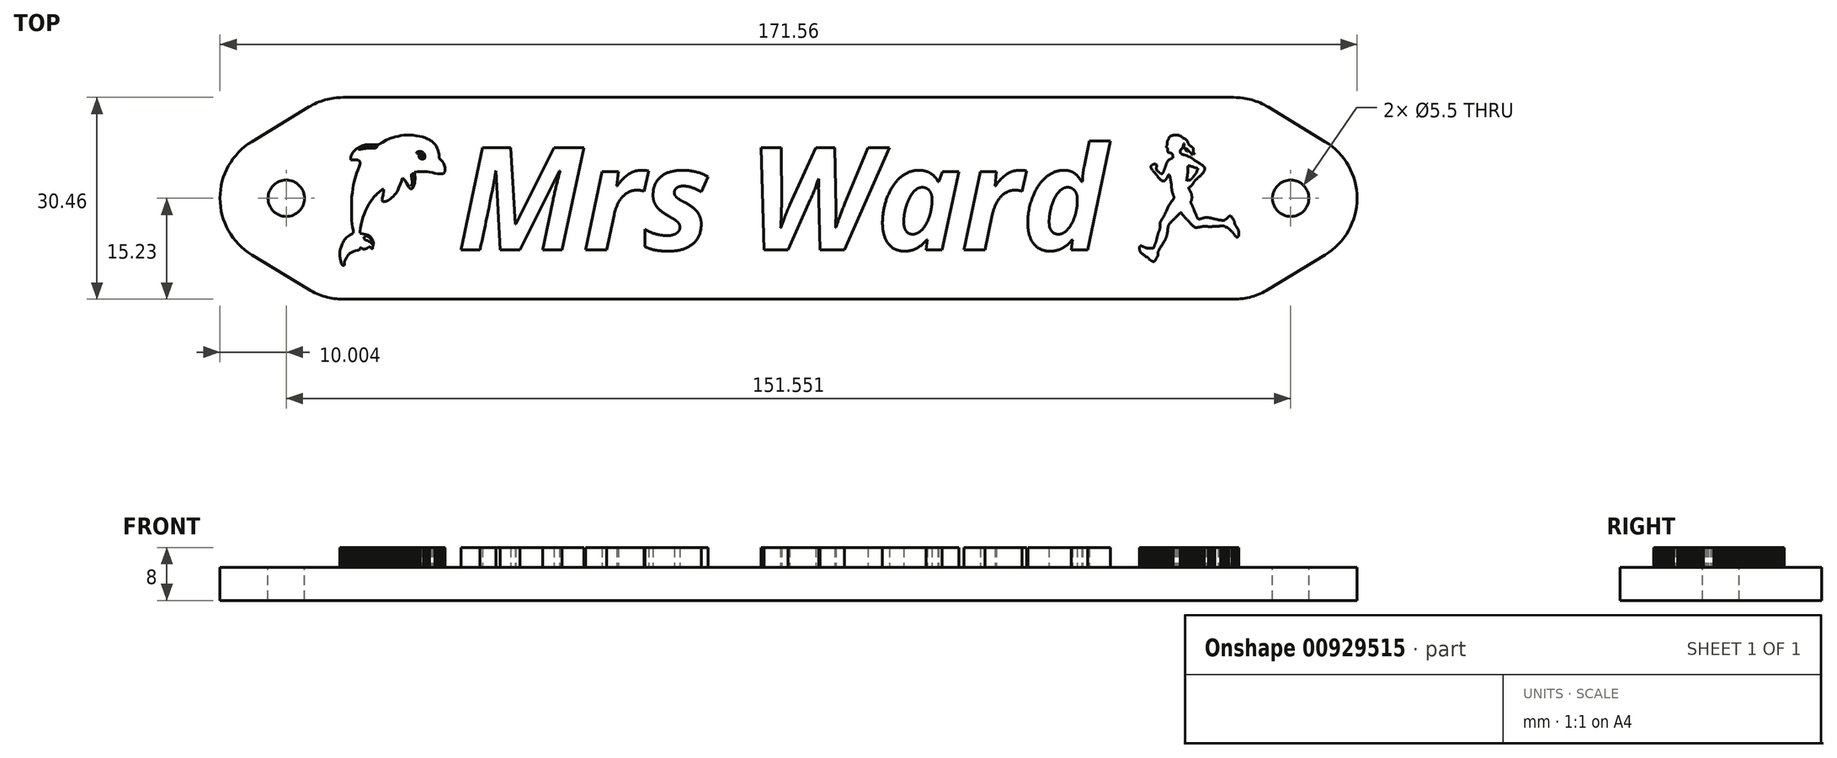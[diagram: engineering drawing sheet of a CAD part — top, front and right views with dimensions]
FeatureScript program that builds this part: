
annotation { "Feature Type Name" : "Feature", "Feature Type Description" : "" }
export const myFeature = defineFeature(function(context is Context, id is Id, definition is map)
    precondition{}
    {
        {
            var Q0;
            Q0=qCreatedBy(makeId("Top.planeOp"),FACE);
            var sketch = newSketch(context, id + "F0", { "sketchPlane" : qUnion([Q0])});
            skLineSegment(sketch, "E0.bottom", {"start": v(-100, -37.5) * mm, "end": v(100, -37.5) * mm, "construction": true});
            skLineSegment(sketch, "E0.top", {"start": v(-100, 37.5) * mm, "end": v(100, 37.5) * mm, "construction": true});
            skLineSegment(sketch, "E0.left", {"start": v(-100, -37.5) * mm, "end": v(-100, 37.5) * mm, "construction": true});
            skLineSegment(sketch, "E0.right", {"start": v(100, -37.5) * mm, "end": v(100, 37.5) * mm, "construction": true});
            skPoint(sketch, "E0.middle", {"position": v(0, 0) * mm});
            skLineSegment(sketch, "E1.bottom", {"start": v(-70, -15.23) * mm, "end": v(70, -15.23) * mm});
            skLineSegment(sketch, "E1.top", {"start": v(-70, 15.23) * mm, "end": v(70, 15.23) * mm});
            skLineSegment(sketch, "E1.left", {"start": v(-70, -15.23) * mm, "end": v(-70, 15.23) * mm});
            skLineSegment(sketch, "E1.right", {"start": v(70, -15.23) * mm, "end": v(70, 15.23) * mm});
            skLineSegment(sketch, "E2", {"start": v(-70, 0) * mm, "end": v(-95, 0) * mm, "construction": true});
            skLineSegment(sketch, "E3", {"start": v(-95, 0) * mm, "end": v(-70, 15.23) * mm});
            skLineSegment(sketch, "E4", {"start": v(-95, 0) * mm, "end": v(-70, -15.23) * mm});
            skLineSegment(sketch, "E5", {"start": v(70, 15.23) * mm, "end": v(95, 0) * mm});
            skLineSegment(sketch, "E6", {"start": v(95, 0) * mm, "end": v(70, -15.23) * mm});
            skLineSegment(sketch, "E7", {"start": v(70, 0) * mm, "end": v(95, 0) * mm, "construction": true});
            skSolve(sketch);
        }
        {
            var Q0;
            Q0 = qSketchRegion(id + "F0", true);
            extrude(context, id + "F1", {"entities" : qUnion([Q0]), "depth" : 5 * mm, "offsetDistance" : 25 * mm});
        }
        {
            var Q0;
            Q0=makeQuery(id+"F1.opExtrude","SWEPT_EDGE",EDGE,{"disambiguationData":[OSD([sQuery(id+"F0.wireOp",EDGE,"E3"),sQuery(id+"F0.wireOp",EDGE,"E4")])]});
            var Q1;
            Q1=makeQuery(id+"F1.opExtrude","SWEPT_EDGE",EDGE,{"disambiguationData":[OSD([sQuery(id+"F0.wireOp",EDGE,"E5"),sQuery(id+"F0.wireOp",EDGE,"E6")])]});
            fillet(context, id + "F2", {"entities" : qUnion([Q0, Q1]), "radius" : 10 * mm, "tangentPropagation" : true, "allowEdgeOverflow" : false});
        }
        {
            var Q0;
            Q0=makeQuery(id+"F1.opExtrude","SWEPT_EDGE",EDGE,{"disambiguationData":[OSD([sQuery(id+"F0.wireOp",EDGE,"E1.bottom"),sQuery(id+"F0.wireOp",EDGE,"E1.right"),sQuery(id+"F0.wireOp",EDGE,"E6")])]});
            var Q1;
            Q1=makeQuery(id+"F1.opExtrude","SWEPT_EDGE",EDGE,{"disambiguationData":[OSD([sQuery(id+"F0.wireOp",EDGE,"E1.bottom"),sQuery(id+"F0.wireOp",EDGE,"E1.left"),sQuery(id+"F0.wireOp",EDGE,"E4")])]});
            var Q2;
            Q2=makeQuery(id+"F1.opExtrude","SWEPT_EDGE",EDGE,{"disambiguationData":[OSD([sQuery(id+"F0.wireOp",EDGE,"E1.top"),sQuery(id+"F0.wireOp",EDGE,"E1.left"),sQuery(id+"F0.wireOp",EDGE,"E3")])]});
            var Q3;
            Q3=makeQuery(id+"F1.opExtrude","SWEPT_EDGE",EDGE,{"disambiguationData":[OSD([sQuery(id+"F0.wireOp",EDGE,"E1.top"),sQuery(id+"F0.wireOp",EDGE,"E1.right"),sQuery(id+"F0.wireOp",EDGE,"E5")])]});
            fillet(context, id + "F3", {"entities" : qUnion([Q0, Q1, Q2, Q3]), "radius" : 10 * mm, "tangentPropagation" : true, "allowEdgeOverflow" : false});
        }
        {
            var Q0;
            Q0=makeQuery(id+"F1.opExtrude","CAP_FACE",FACE,{"disambiguationData":[OSD([sQuery(id+"F0.wireOp",EDGE,"E1.bottom"),sQuery(id+"F0.wireOp",EDGE,"E1.top"),sQuery(id+"F0.wireOp",EDGE,"E3"),sQuery(id+"F0.wireOp",EDGE,"E4"),sQuery(id+"F0.wireOp",EDGE,"E5"),sQuery(id+"F0.wireOp",EDGE,"E6")])],"isStart":false});
            var sketch = newSketch(context, id + "F4", { "sketchPlane" : qUnion([Q0])});
            skText(sketch, "E8", { "text": "Mrs Ward", "fontName": "OpenSans-BoldItalic.ttf"});
            const initialGuessF4  = {"E8": [-0.05, -0.00778, 1, 0, 0.01555]};
            skSetInitialGuess(sketch, initialGuessF4);
            skSolve(sketch);
        }
        {
            var Q0;
            Q0 = qSketchRegion(id + "F4", true);
            extrude(context, id + "F5", {"entities" : qUnion([Q0]), "operationType" : NewBodyOperationType.ADD, "depth" : 3 * mm, "offsetDistance" : 25 * mm});
        }
        {
            var Q0;
            {var subQ0=sQuery(id+"F0.wireOp",EDGE,"E5");var subQ2=sQuery(id+"F0.wireOp",EDGE,"E1.top");var subQ3=sQuery(id+"F0.wireOp",EDGE,"E3");var subQ5=sQuery(id+"F0.wireOp",EDGE,"E4");var subQ6=sQuery(id+"F0.wireOp",EDGE,"E6");var subQ7=sQuery(id+"F0.wireOp",EDGE,"E1.bottom");Q0=makeQuery(id+"F5.boolean.opBoolean","SPLIT",FACE,{"disambiguationData":[TD([makeQuery(id+"F1.opExtrude","SWEPT_FACE",FACE,{"disambiguationData":[OSD([subQ7])]})])],"derivedFrom":makeQuery(id+"F1.opExtrude","CAP_FACE",FACE,{"disambiguationData":[OSD([subQ7,subQ2,subQ3,subQ5,subQ0,subQ6])],"isStart":false})});}
            var sketch = newSketch(context, id + "F6", { "sketchPlane" : qUnion([Q0])});
            skPoint(sketch, "E9", {"position": v(-75.78, 0) * mm});
            skPoint(sketch, "E10", {"position": v(75.78, 0) * mm});
            skSolve(sketch);
        }
        {
            var Q0;
            Q0=sQuery(id+"F6.wireOp",VERTEX,"E10");
            var Q1;
            Q1=sQuery(id+"F6.wireOp",VERTEX,"E9");
            var Q2;
            Q2=makeQuery(id+"F1.opExtrude","SWEPT_BODY",BODY,{"disambiguationData":[OSD([sQuery(id+"F0.wireOp",EDGE,"E1.bottom"),sQuery(id+"F0.wireOp",EDGE,"E1.top"),sQuery(id+"F0.wireOp",EDGE,"E3"),sQuery(id+"F0.wireOp",EDGE,"E4"),sQuery(id+"F0.wireOp",EDGE,"E5"),sQuery(id+"F0.wireOp",EDGE,"E6")])]});
            hole(context, id + "F7", {"style" : HoleStyle.SIMPLE, "endStyle" : HoleEndStyle.THROUGH, "standardTappedOrClearance" : lookupTablePath({ "fit" : "Normal", "standard" : "ISO", "size" : "M5", "type" : "Clearance" }), "standardBlindInLast" : lookupTablePath({ "fit" : "Normal", "standard" : "ISO", "size" : "M5", "type" : "Clearance" }), "holeDiameter" : 5.5 * mm, "majorDiameter" : 5 * mm, "isTappedThrough" : true, "tappedDepth" : 12 * mm, "tapClearance" : 3, "locations" : qUnion([Q0, Q1]), "scope" : qUnion([Q2])});
        }
        {
            var Q0;
            {var subQ0=sQuery(id+"F0.wireOp",EDGE,"E5");var subQ2=sQuery(id+"F0.wireOp",EDGE,"E1.top");var subQ3=sQuery(id+"F0.wireOp",EDGE,"E3");var subQ5=sQuery(id+"F0.wireOp",EDGE,"E4");var subQ6=sQuery(id+"F0.wireOp",EDGE,"E6");var subQ7=sQuery(id+"F0.wireOp",EDGE,"E1.bottom");Q0=makeQuery(id+"F5.boolean.opBoolean","SPLIT",FACE,{"disambiguationData":[TD([makeQuery(id+"F1.opExtrude","SWEPT_FACE",FACE,{"disambiguationData":[OSD([subQ7])]})])],"derivedFrom":makeQuery(id+"F1.opExtrude","CAP_FACE",FACE,{"disambiguationData":[OSD([subQ7,subQ2,subQ3,subQ5,subQ0,subQ6])],"isStart":false})});}
            var sketch = newSketch(context, id + "F8", { "sketchPlane" : qUnion([Q0])});
            skLineSegment(sketch, "E11.bottom", {"start": v(-69.8, 10) * mm, "end": v(-49.8, 10) * mm, "construction": true});
            skLineSegment(sketch, "E11.top", {"start": v(-69.8, -10) * mm, "end": v(-49.8, -10) * mm, "construction": true});
            skLineSegment(sketch, "E11.left", {"start": v(-69.8, 10) * mm, "end": v(-69.8, -10) * mm, "construction": true});
            skLineSegment(sketch, "E11.right", {"start": v(-49.8, 10) * mm, "end": v(-49.8, -10) * mm, "construction": true});
            skLineSegment(sketch, "E12", {"start": v(-69.8, -10) * mm, "end": v(-49.8, 10) * mm, "construction": true});
            skLineSegment(sketch, "E13", {"start": v(-75.78, 0) * mm, "end": v(-59.8, 0) * mm, "construction": true});
            skLineSegment(sketch, "E14", {"start": v(-67.3, -10.07) * mm, "end": v(-67.35, -10.02) * mm});
            skLineSegment(sketch, "E15", {"start": v(-67.35, -10.02) * mm, "end": v(-67.4, -9.96) * mm});
            skLineSegment(sketch, "E16", {"start": v(-67.4, -9.96) * mm, "end": v(-67.44, -9.9) * mm});
            skLineSegment(sketch, "E17", {"start": v(-67.44, -9.9) * mm, "end": v(-67.47, -9.81) * mm});
            skLineSegment(sketch, "E18", {"start": v(-67.47, -9.81) * mm, "end": v(-67.53, -9.61) * mm});
            skLineSegment(sketch, "E19", {"start": v(-67.53, -9.61) * mm, "end": v(-67.57, -9.36) * mm});
            skLineSegment(sketch, "E20", {"start": v(-67.57, -9.36) * mm, "end": v(-67.62, -9.1) * mm});
            skLineSegment(sketch, "E21", {"start": v(-67.62, -9.1) * mm, "end": v(-67.65, -8.93) * mm});
            skLineSegment(sketch, "E22", {"start": v(-67.65, -8.93) * mm, "end": v(-67.67, -8.85) * mm});
            skLineSegment(sketch, "E23", {"start": v(-67.67, -8.85) * mm, "end": v(-67.68, -8.72) * mm});
            skLineSegment(sketch, "E24", {"start": v(-67.68, -8.72) * mm, "end": v(-67.69, -8.36) * mm});
            skLineSegment(sketch, "E25", {"start": v(-67.69, -8.36) * mm, "end": v(-67.68, -8.02) * mm});
            skLineSegment(sketch, "E26", {"start": v(-67.68, -8.02) * mm, "end": v(-67.67, -7.9) * mm});
            skLineSegment(sketch, "E27", {"start": v(-67.67, -7.9) * mm, "end": v(-67.66, -7.84) * mm});
            skLineSegment(sketch, "E28", {"start": v(-67.66, -7.84) * mm, "end": v(-67.62, -7.74) * mm});
            skLineSegment(sketch, "E29", {"start": v(-67.62, -7.74) * mm, "end": v(-67.57, -7.54) * mm});
            skLineSegment(sketch, "E30", {"start": v(-67.57, -7.54) * mm, "end": v(-67.53, -7.38) * mm});
            skLineSegment(sketch, "E31", {"start": v(-67.53, -7.38) * mm, "end": v(-67.47, -7.2) * mm});
            skLineSegment(sketch, "E32", {"start": v(-67.47, -7.2) * mm, "end": v(-67.4, -7.02) * mm});
            skLineSegment(sketch, "E33", {"start": v(-67.4, -7.02) * mm, "end": v(-67.3, -6.83) * mm});
            skLineSegment(sketch, "E34", {"start": v(-67.3, -6.83) * mm, "end": v(-67.2, -6.64) * mm});
            skLineSegment(sketch, "E35", {"start": v(-67.2, -6.64) * mm, "end": v(-67.1, -6.46) * mm});
            skLineSegment(sketch, "E36", {"start": v(-67.1, -6.46) * mm, "end": v(-67, -6.29) * mm});
            skLineSegment(sketch, "E37", {"start": v(-67, -6.29) * mm, "end": v(-66.88, -6.14) * mm});
            skLineSegment(sketch, "E38", {"start": v(-66.88, -6.14) * mm, "end": v(-66.72, -5.95) * mm});
            skLineSegment(sketch, "E39", {"start": v(-66.72, -5.95) * mm, "end": v(-66.57, -5.8) * mm});
            skLineSegment(sketch, "E40", {"start": v(-66.57, -5.8) * mm, "end": v(-66.38, -5.68) * mm});
            skLineSegment(sketch, "E41", {"start": v(-66.38, -5.68) * mm, "end": v(-66.11, -5.51) * mm});
            skLineSegment(sketch, "E42", {"start": v(-66.11, -5.51) * mm, "end": v(-65.85, -5.36) * mm});
            skLineSegment(sketch, "E43", {"start": v(-65.85, -5.36) * mm, "end": v(-65.7, -5.26) * mm});
            skLineSegment(sketch, "E44", {"start": v(-65.7, -5.26) * mm, "end": v(-65.67, -5.22) * mm});
            skLineSegment(sketch, "E45", {"start": v(-65.67, -5.22) * mm, "end": v(-65.64, -5.2) * mm});
            skLineSegment(sketch, "E46", {"start": v(-65.64, -5.2) * mm, "end": v(-65.63, -5.16) * mm});
            skLineSegment(sketch, "E47", {"start": v(-65.63, -5.16) * mm, "end": v(-65.64, -5.13) * mm});
            skLineSegment(sketch, "E48", {"start": v(-65.64, -5.13) * mm, "end": v(-65.7, -4.8) * mm});
            skLineSegment(sketch, "E49", {"start": v(-65.7, -4.8) * mm, "end": v(-65.76, -4.4) * mm});
            skLineSegment(sketch, "E50", {"start": v(-65.76, -4.4) * mm, "end": v(-65.9, -3.34) * mm});
            skLineSegment(sketch, "E51", {"start": v(-65.9, -3.34) * mm, "end": v(-65.92, -3.07) * mm});
            skLineSegment(sketch, "E52", {"start": v(-65.92, -3.07) * mm, "end": v(-65.93, -2.66) * mm});
            skLineSegment(sketch, "E53", {"start": v(-65.93, -2.66) * mm, "end": v(-65.94, -1.6) * mm});
            skLineSegment(sketch, "E54", {"start": v(-65.94, -1.6) * mm, "end": v(-65.93, -0.52) * mm});
            skLineSegment(sketch, "E55", {"start": v(-65.93, -0.52) * mm, "end": v(-65.92, -0.1) * mm});
            skLineSegment(sketch, "E56", {"start": v(-65.92, -0.1) * mm, "end": v(-65.9, 0.18) * mm});
            skLineSegment(sketch, "E57", {"start": v(-65.9, 0.18) * mm, "end": v(-65.82, 0.86) * mm});
            skLineSegment(sketch, "E58", {"start": v(-65.82, 0.86) * mm, "end": v(-65.74, 1.46) * mm});
            skLineSegment(sketch, "E59", {"start": v(-65.74, 1.46) * mm, "end": v(-65.65, 1.99) * mm});
            skLineSegment(sketch, "E60", {"start": v(-65.65, 1.99) * mm, "end": v(-65.55, 2.47) * mm});
            skLineSegment(sketch, "E61", {"start": v(-65.55, 2.47) * mm, "end": v(-65.44, 2.92) * mm});
            skLineSegment(sketch, "E62", {"start": v(-65.44, 2.92) * mm, "end": v(-65.3, 3.37) * mm});
            skLineSegment(sketch, "E63", {"start": v(-65.3, 3.37) * mm, "end": v(-65.14, 3.82) * mm});
            skLineSegment(sketch, "E64", {"start": v(-65.14, 3.82) * mm, "end": v(-64.96, 4.3) * mm});
            skLineSegment(sketch, "E65", {"start": v(-64.96, 4.3) * mm, "end": v(-64.76, 4.8) * mm});
            skLineSegment(sketch, "E66", {"start": v(-64.76, 4.8) * mm, "end": v(-64.7, 5) * mm});
            skLineSegment(sketch, "E67", {"start": v(-64.7, 5) * mm, "end": v(-64.66, 5.15) * mm});
            skLineSegment(sketch, "E68", {"start": v(-64.66, 5.15) * mm, "end": v(-64.64, 5.28) * mm});
            skLineSegment(sketch, "E69", {"start": v(-64.64, 5.28) * mm, "end": v(-64.64, 5.38) * mm});
            skLineSegment(sketch, "E70", {"start": v(-64.64, 5.38) * mm, "end": v(-64.65, 5.47) * mm});
            skLineSegment(sketch, "E71", {"start": v(-64.65, 5.47) * mm, "end": v(-64.68, 5.54) * mm});
            skLineSegment(sketch, "E72", {"start": v(-64.68, 5.54) * mm, "end": v(-64.73, 5.62) * mm});
            skLineSegment(sketch, "E73", {"start": v(-64.73, 5.62) * mm, "end": v(-64.79, 5.68) * mm});
            skLineSegment(sketch, "E74", {"start": v(-64.79, 5.68) * mm, "end": v(-64.85, 5.73) * mm});
            skLineSegment(sketch, "E75", {"start": v(-64.85, 5.73) * mm, "end": v(-64.94, 5.76) * mm});
            skLineSegment(sketch, "E76", {"start": v(-64.94, 5.76) * mm, "end": v(-65.04, 5.78) * mm});
            skLineSegment(sketch, "E77", {"start": v(-65.04, 5.78) * mm, "end": v(-65.17, 5.8) * mm});
            skLineSegment(sketch, "E78", {"start": v(-65.17, 5.8) * mm, "end": v(-65.54, 5.8) * mm});
            skLineSegment(sketch, "E79", {"start": v(-65.54, 5.8) * mm, "end": v(-66.08, 5.77) * mm});
            skLineSegment(sketch, "E80", {"start": v(-66.08, 5.77) * mm, "end": v(-66.08, 5.96) * mm});
            skLineSegment(sketch, "E81", {"start": v(-66.08, 5.96) * mm, "end": v(-66.07, 6.05) * mm});
            skLineSegment(sketch, "E82", {"start": v(-66.07, 6.05) * mm, "end": v(-66.04, 6.16) * mm});
            skLineSegment(sketch, "E83", {"start": v(-66.04, 6.16) * mm, "end": v(-65.96, 6.42) * mm});
            skLineSegment(sketch, "E84", {"start": v(-65.96, 6.42) * mm, "end": v(-65.84, 6.7) * mm});
            skLineSegment(sketch, "E85", {"start": v(-65.84, 6.7) * mm, "end": v(-65.78, 6.82) * mm});
            skLineSegment(sketch, "E86", {"start": v(-65.78, 6.82) * mm, "end": v(-65.72, 6.92) * mm});
            skLineSegment(sketch, "E87", {"start": v(-65.72, 6.92) * mm, "end": v(-65.59, 7.09) * mm});
            skLineSegment(sketch, "E88", {"start": v(-65.59, 7.09) * mm, "end": v(-65.42, 7.25) * mm});
            skLineSegment(sketch, "E89", {"start": v(-65.42, 7.25) * mm, "end": v(-65.22, 7.42) * mm});
            skLineSegment(sketch, "E90", {"start": v(-65.22, 7.42) * mm, "end": v(-65, 7.57) * mm});
            skLineSegment(sketch, "E91", {"start": v(-65, 7.57) * mm, "end": v(-64.76, 7.71) * mm});
            skLineSegment(sketch, "E92", {"start": v(-64.76, 7.71) * mm, "end": v(-64.51, 7.84) * mm});
            skLineSegment(sketch, "E93", {"start": v(-64.51, 7.84) * mm, "end": v(-64.27, 7.94) * mm});
            skLineSegment(sketch, "E94", {"start": v(-64.27, 7.94) * mm, "end": v(-64.03, 8) * mm});
            skLineSegment(sketch, "E95", {"start": v(-64.03, 8) * mm, "end": v(-63.8, 8.05) * mm});
            skLineSegment(sketch, "E96", {"start": v(-63.8, 8.05) * mm, "end": v(-63.55, 8.08) * mm});
            skLineSegment(sketch, "E97", {"start": v(-63.55, 8.08) * mm, "end": v(-63.21, 8.1) * mm});
            skLineSegment(sketch, "E98", {"start": v(-63.21, 8.1) * mm, "end": v(-62.74, 8.1) * mm});
            skLineSegment(sketch, "E99", {"start": v(-62.74, 8.1) * mm, "end": v(-62.23, 8.1) * mm});
            skLineSegment(sketch, "E100", {"start": v(-62.23, 8.1) * mm, "end": v(-61.94, 8.11) * mm});
            skLineSegment(sketch, "E101", {"start": v(-61.94, 8.11) * mm, "end": v(-61.85, 8.12) * mm});
            skLineSegment(sketch, "E102", {"start": v(-61.85, 8.12) * mm, "end": v(-61.79, 8.14) * mm});
            skLineSegment(sketch, "E103", {"start": v(-61.79, 8.14) * mm, "end": v(-61.73, 8.17) * mm});
            skLineSegment(sketch, "E104", {"start": v(-61.73, 8.17) * mm, "end": v(-61.69, 8.2) * mm});
            skLineSegment(sketch, "E105", {"start": v(-61.69, 8.2) * mm, "end": v(-61.49, 8.33) * mm});
            skLineSegment(sketch, "E106", {"start": v(-61.49, 8.33) * mm, "end": v(-61.25, 8.47) * mm});
            skLineSegment(sketch, "E107", {"start": v(-61.25, 8.47) * mm, "end": v(-60.71, 8.76) * mm});
            skLineSegment(sketch, "E108", {"start": v(-60.71, 8.76) * mm, "end": v(-60.17, 9) * mm});
            skLineSegment(sketch, "E109", {"start": v(-60.17, 9) * mm, "end": v(-59.93, 9.1) * mm});
            skLineSegment(sketch, "E110", {"start": v(-59.93, 9.1) * mm, "end": v(-59.72, 9.18) * mm});
            skLineSegment(sketch, "E111", {"start": v(-59.72, 9.18) * mm, "end": v(-59.32, 9.29) * mm});
            skLineSegment(sketch, "E112", {"start": v(-59.32, 9.29) * mm, "end": v(-58.9, 9.38) * mm});
            skLineSegment(sketch, "E113", {"start": v(-58.9, 9.38) * mm, "end": v(-58.48, 9.46) * mm});
            skLineSegment(sketch, "E114", {"start": v(-58.48, 9.46) * mm, "end": v(-58.07, 9.52) * mm});
            skLineSegment(sketch, "E115", {"start": v(-58.07, 9.52) * mm, "end": v(-57.67, 9.55) * mm});
            skLineSegment(sketch, "E116", {"start": v(-57.67, 9.55) * mm, "end": v(-57.3, 9.57) * mm});
            skLineSegment(sketch, "E117", {"start": v(-57.3, 9.57) * mm, "end": v(-56.99, 9.56) * mm});
            skLineSegment(sketch, "E118", {"start": v(-56.99, 9.56) * mm, "end": v(-56.72, 9.53) * mm});
            skLineSegment(sketch, "E119", {"start": v(-56.72, 9.53) * mm, "end": v(-56.06, 9.43) * mm});
            skLineSegment(sketch, "E120", {"start": v(-56.06, 9.43) * mm, "end": v(-55.64, 9.36) * mm});
            skLineSegment(sketch, "E121", {"start": v(-55.64, 9.36) * mm, "end": v(-55.24, 9.26) * mm});
            skLineSegment(sketch, "E122", {"start": v(-55.24, 9.26) * mm, "end": v(-54.86, 9.14) * mm});
            skLineSegment(sketch, "E123", {"start": v(-54.86, 9.14) * mm, "end": v(-54.5, 9) * mm});
            skLineSegment(sketch, "E124", {"start": v(-54.5, 9) * mm, "end": v(-54.17, 8.82) * mm});
            skLineSegment(sketch, "E125", {"start": v(-54.17, 8.82) * mm, "end": v(-54.02, 8.73) * mm});
            skLineSegment(sketch, "E126", {"start": v(-54.02, 8.73) * mm, "end": v(-53.88, 8.63) * mm});
            skLineSegment(sketch, "E127", {"start": v(-53.88, 8.63) * mm, "end": v(-53.74, 8.52) * mm});
            skLineSegment(sketch, "E128", {"start": v(-53.74, 8.52) * mm, "end": v(-53.61, 8.41) * mm});
            skLineSegment(sketch, "E129", {"start": v(-53.61, 8.41) * mm, "end": v(-53.5, 8.3) * mm});
            skLineSegment(sketch, "E130", {"start": v(-53.5, 8.3) * mm, "end": v(-53.39, 8.18) * mm});
            skLineSegment(sketch, "E131", {"start": v(-53.39, 8.18) * mm, "end": v(-53.25, 8) * mm});
            skLineSegment(sketch, "E132", {"start": v(-53.25, 8) * mm, "end": v(-53.12, 7.8) * mm});
            skLineSegment(sketch, "E133", {"start": v(-53.12, 7.8) * mm, "end": v(-53, 7.56) * mm});
            skLineSegment(sketch, "E134", {"start": v(-53, 7.56) * mm, "end": v(-52.9, 7.32) * mm});
            skLineSegment(sketch, "E135", {"start": v(-52.9, 7.32) * mm, "end": v(-52.82, 7.07) * mm});
            skLineSegment(sketch, "E136", {"start": v(-52.82, 7.07) * mm, "end": v(-52.76, 6.83) * mm});
            skLineSegment(sketch, "E137", {"start": v(-52.76, 6.83) * mm, "end": v(-52.72, 6.6) * mm});
            skLineSegment(sketch, "E138", {"start": v(-52.72, 6.6) * mm, "end": v(-52.7, 6.38) * mm});
            skLineSegment(sketch, "E139", {"start": v(-52.7, 6.38) * mm, "end": v(-52.7, 6.04) * mm});
            skLineSegment(sketch, "E140", {"start": v(-52.7, 6.04) * mm, "end": v(-52.52, 5.86) * mm});
            skLineSegment(sketch, "E141", {"start": v(-52.52, 5.86) * mm, "end": v(-52.35, 5.7) * mm});
            skLineSegment(sketch, "E142", {"start": v(-52.35, 5.7) * mm, "end": v(-52.2, 5.54) * mm});
            skLineSegment(sketch, "E143", {"start": v(-52.2, 5.54) * mm, "end": v(-52.1, 5.38) * mm});
            skLineSegment(sketch, "E144", {"start": v(-52.1, 5.38) * mm, "end": v(-52, 5.21) * mm});
            skLineSegment(sketch, "E145", {"start": v(-52, 5.21) * mm, "end": v(-51.93, 5.04) * mm});
            skLineSegment(sketch, "E146", {"start": v(-51.93, 5.04) * mm, "end": v(-51.88, 4.86) * mm});
            skLineSegment(sketch, "E147", {"start": v(-51.88, 4.86) * mm, "end": v(-51.85, 4.67) * mm});
            skLineSegment(sketch, "E148", {"start": v(-51.85, 4.67) * mm, "end": v(-51.84, 4.46) * mm});
            skLineSegment(sketch, "E149", {"start": v(-51.84, 4.46) * mm, "end": v(-51.83, 4.25) * mm});
            skLineSegment(sketch, "E150", {"start": v(-51.83, 4.25) * mm, "end": v(-51.84, 4.11) * mm});
            skLineSegment(sketch, "E151", {"start": v(-51.84, 4.11) * mm, "end": v(-51.86, 4.01) * mm});
            skLineSegment(sketch, "E152", {"start": v(-51.86, 4.01) * mm, "end": v(-51.9, 3.93) * mm});
            skLineSegment(sketch, "E153", {"start": v(-51.9, 3.93) * mm, "end": v(-51.93, 3.88) * mm});
            skLineSegment(sketch, "E154", {"start": v(-51.93, 3.88) * mm, "end": v(-51.98, 3.83) * mm});
            skLineSegment(sketch, "E155", {"start": v(-51.98, 3.83) * mm, "end": v(-52.03, 3.79) * mm});
            skLineSegment(sketch, "E156", {"start": v(-52.03, 3.79) * mm, "end": v(-52.1, 3.75) * mm});
            skLineSegment(sketch, "E157", {"start": v(-52.1, 3.75) * mm, "end": v(-52.17, 3.72) * mm});
            skLineSegment(sketch, "E158", {"start": v(-52.17, 3.72) * mm, "end": v(-52.25, 3.7) * mm});
            skLineSegment(sketch, "E159", {"start": v(-52.25, 3.7) * mm, "end": v(-52.44, 3.68) * mm});
            skLineSegment(sketch, "E160", {"start": v(-52.44, 3.68) * mm, "end": v(-52.69, 3.68) * mm});
            skLineSegment(sketch, "E161", {"start": v(-52.69, 3.68) * mm, "end": v(-52.98, 3.72) * mm});
            skLineSegment(sketch, "E162", {"start": v(-52.98, 3.72) * mm, "end": v(-53.32, 3.78) * mm});
            skLineSegment(sketch, "E163", {"start": v(-53.32, 3.78) * mm, "end": v(-53.72, 3.86) * mm});
            skLineSegment(sketch, "E164", {"start": v(-53.72, 3.86) * mm, "end": v(-54.16, 3.96) * mm});
            skLineSegment(sketch, "E165", {"start": v(-54.16, 3.96) * mm, "end": v(-54.47, 4.02) * mm});
            skLineSegment(sketch, "E166", {"start": v(-54.47, 4.02) * mm, "end": v(-54.75, 4.04) * mm});
            skLineSegment(sketch, "E167", {"start": v(-54.75, 4.04) * mm, "end": v(-55.07, 4.05) * mm});
            skLineSegment(sketch, "E168", {"start": v(-55.07, 4.05) * mm, "end": v(-55.54, 4.04) * mm});
            skLineSegment(sketch, "E169", {"start": v(-55.54, 4.04) * mm, "end": v(-55.96, 4) * mm});
            skLineSegment(sketch, "E170", {"start": v(-55.96, 4) * mm, "end": v(-56.27, 3.96) * mm});
            skLineSegment(sketch, "E171", {"start": v(-56.27, 3.96) * mm, "end": v(-56.37, 3.94) * mm});
            skLineSegment(sketch, "E172", {"start": v(-56.37, 3.94) * mm, "end": v(-56.41, 3.91) * mm});
            skLineSegment(sketch, "E173", {"start": v(-56.41, 3.91) * mm, "end": v(-56.43, 3.87) * mm});
            skLineSegment(sketch, "E174", {"start": v(-56.43, 3.87) * mm, "end": v(-56.43, 3.8) * mm});
            skLineSegment(sketch, "E175", {"start": v(-56.43, 3.8) * mm, "end": v(-56.4, 3.55) * mm});
            skLineSegment(sketch, "E176", {"start": v(-56.4, 3.55) * mm, "end": v(-56.38, 3.4) * mm});
            skLineSegment(sketch, "E177", {"start": v(-56.38, 3.4) * mm, "end": v(-56.36, 3.22) * mm});
            skLineSegment(sketch, "E178", {"start": v(-56.36, 3.22) * mm, "end": v(-56.35, 2.87) * mm});
            skLineSegment(sketch, "E179", {"start": v(-56.35, 2.87) * mm, "end": v(-56.37, 2.52) * mm});
            skLineSegment(sketch, "E180", {"start": v(-56.37, 2.52) * mm, "end": v(-56.4, 2.37) * mm});
            skLineSegment(sketch, "E181", {"start": v(-56.4, 2.37) * mm, "end": v(-56.42, 2.25) * mm});
            skLineSegment(sketch, "E182", {"start": v(-56.42, 2.25) * mm, "end": v(-56.5, 2) * mm});
            skLineSegment(sketch, "E183", {"start": v(-56.5, 2) * mm, "end": v(-56.6, 1.74) * mm});
            skLineSegment(sketch, "E184", {"start": v(-56.6, 1.74) * mm, "end": v(-56.72, 1.52) * mm});
            skLineSegment(sketch, "E185", {"start": v(-56.72, 1.52) * mm, "end": v(-56.77, 1.45) * mm});
            skLineSegment(sketch, "E186", {"start": v(-56.77, 1.45) * mm, "end": v(-56.8, 1.4) * mm});
            skLineSegment(sketch, "E187", {"start": v(-56.8, 1.4) * mm, "end": v(-56.85, 1.4) * mm});
            skLineSegment(sketch, "E188", {"start": v(-56.85, 1.4) * mm, "end": v(-56.9, 1.4) * mm});
            skLineSegment(sketch, "E189", {"start": v(-56.9, 1.4) * mm, "end": v(-56.96, 1.41) * mm});
            skLineSegment(sketch, "E190", {"start": v(-56.96, 1.41) * mm, "end": v(-57.02, 1.44) * mm});
            skLineSegment(sketch, "E191", {"start": v(-57.02, 1.44) * mm, "end": v(-57.08, 1.5) * mm});
            skLineSegment(sketch, "E192", {"start": v(-57.08, 1.5) * mm, "end": v(-57.15, 1.55) * mm});
            skLineSegment(sketch, "E193", {"start": v(-57.15, 1.55) * mm, "end": v(-57.2, 1.62) * mm});
            skLineSegment(sketch, "E194", {"start": v(-57.2, 1.62) * mm, "end": v(-57.26, 1.7) * mm});
            skLineSegment(sketch, "E195", {"start": v(-57.26, 1.7) * mm, "end": v(-57.6, 2.26) * mm});
            skLineSegment(sketch, "E196", {"start": v(-57.6, 2.26) * mm, "end": v(-57.88, 2.68) * mm});
            skLineSegment(sketch, "E197", {"start": v(-57.88, 2.68) * mm, "end": v(-58, 2.83) * mm});
            skLineSegment(sketch, "E198", {"start": v(-58, 2.83) * mm, "end": v(-58.1, 2.95) * mm});
            skLineSegment(sketch, "E199", {"start": v(-58.1, 2.95) * mm, "end": v(-58.16, 3.01) * mm});
            skLineSegment(sketch, "E200", {"start": v(-58.16, 3.01) * mm, "end": v(-58.21, 3.04) * mm});
            skLineSegment(sketch, "E201", {"start": v(-58.21, 3.04) * mm, "end": v(-58.24, 3) * mm});
            skLineSegment(sketch, "E202", {"start": v(-58.24, 3) * mm, "end": v(-58.28, 2.92) * mm});
            skLineSegment(sketch, "E203", {"start": v(-58.28, 2.92) * mm, "end": v(-58.38, 2.65) * mm});
            skLineSegment(sketch, "E204", {"start": v(-58.38, 2.65) * mm, "end": v(-58.56, 2.18) * mm});
            skLineSegment(sketch, "E205", {"start": v(-58.56, 2.18) * mm, "end": v(-58.8, 1.6) * mm});
            skLineSegment(sketch, "E206", {"start": v(-58.8, 1.6) * mm, "end": v(-58.95, 1.23) * mm});
            skLineSegment(sketch, "E207", {"start": v(-58.95, 1.23) * mm, "end": v(-59.08, 0.98) * mm});
            skLineSegment(sketch, "E208", {"start": v(-59.08, 0.98) * mm, "end": v(-59.22, 0.78) * mm});
            skLineSegment(sketch, "E209", {"start": v(-59.22, 0.78) * mm, "end": v(-59.42, 0.55) * mm});
            skLineSegment(sketch, "E210", {"start": v(-59.42, 0.55) * mm, "end": v(-59.66, 0.3) * mm});
            skLineSegment(sketch, "E211", {"start": v(-59.66, 0.3) * mm, "end": v(-59.88, 0.07) * mm});
            skLineSegment(sketch, "E212", {"start": v(-59.88, 0.07) * mm, "end": v(-60.1, -0.11) * mm});
            skLineSegment(sketch, "E213", {"start": v(-60.1, -0.11) * mm, "end": v(-60.29, -0.26) * mm});
            skLineSegment(sketch, "E214", {"start": v(-60.29, -0.26) * mm, "end": v(-60.48, -0.37) * mm});
            skLineSegment(sketch, "E215", {"start": v(-60.48, -0.37) * mm, "end": v(-60.66, -0.44) * mm});
            skLineSegment(sketch, "E216", {"start": v(-60.66, -0.44) * mm, "end": v(-60.84, -0.49) * mm});
            skLineSegment(sketch, "E217", {"start": v(-60.84, -0.49) * mm, "end": v(-61.01, -0.5) * mm});
            skLineSegment(sketch, "E218", {"start": v(-61.01, -0.5) * mm, "end": v(-61.13, -0.5) * mm});
            skLineSegment(sketch, "E219", {"start": v(-61.13, -0.5) * mm, "end": v(-61.22, -0.47) * mm});
            skLineSegment(sketch, "E220", {"start": v(-61.22, -0.47) * mm, "end": v(-61.28, -0.43) * mm});
            skLineSegment(sketch, "E221", {"start": v(-61.28, -0.43) * mm, "end": v(-61.31, -0.35) * mm});
            skLineSegment(sketch, "E222", {"start": v(-61.31, -0.35) * mm, "end": v(-61.32, -0.25) * mm});
            skLineSegment(sketch, "E223", {"start": v(-61.32, -0.25) * mm, "end": v(-61.3, -0.12) * mm});
            skLineSegment(sketch, "E224", {"start": v(-61.3, -0.12) * mm, "end": v(-61.27, 0.05) * mm});
            skLineSegment(sketch, "E225", {"start": v(-61.27, 0.05) * mm, "end": v(-61.22, 0.27) * mm});
            skLineSegment(sketch, "E226", {"start": v(-61.22, 0.27) * mm, "end": v(-61.18, 0.43) * mm});
            skLineSegment(sketch, "E227", {"start": v(-61.18, 0.43) * mm, "end": v(-61.14, 0.61) * mm});
            skLineSegment(sketch, "E228", {"start": v(-61.14, 0.61) * mm, "end": v(-61.1, 0.98) * mm});
            skLineSegment(sketch, "E229", {"start": v(-61.1, 0.98) * mm, "end": v(-61.09, 1.14) * mm});
            skLineSegment(sketch, "E230", {"start": v(-61.09, 1.14) * mm, "end": v(-61.09, 1.26) * mm});
            skLineSegment(sketch, "E231", {"start": v(-61.09, 1.26) * mm, "end": v(-61.1, 1.35) * mm});
            skLineSegment(sketch, "E232", {"start": v(-61.1, 1.35) * mm, "end": v(-61.11, 1.37) * mm});
            skLineSegment(sketch, "E233", {"start": v(-61.11, 1.37) * mm, "end": v(-61.12, 1.38) * mm});
            skLineSegment(sketch, "E234", {"start": v(-61.12, 1.38) * mm, "end": v(-61.2, 1.35) * mm});
            skLineSegment(sketch, "E235", {"start": v(-61.2, 1.35) * mm, "end": v(-61.32, 1.26) * mm});
            skLineSegment(sketch, "E236", {"start": v(-61.32, 1.26) * mm, "end": v(-61.7, 0.97) * mm});
            skLineSegment(sketch, "E237", {"start": v(-61.7, 0.97) * mm, "end": v(-62.1, 0.63) * mm});
            skLineSegment(sketch, "E238", {"start": v(-62.1, 0.63) * mm, "end": v(-62.26, 0.48) * mm});
            skLineSegment(sketch, "E239", {"start": v(-62.26, 0.48) * mm, "end": v(-62.38, 0.37) * mm});
            skLineSegment(sketch, "E240", {"start": v(-62.38, 0.37) * mm, "end": v(-62.53, 0.2) * mm});
            skLineSegment(sketch, "E241", {"start": v(-62.53, 0.2) * mm, "end": v(-62.69, 0) * mm});
            skLineSegment(sketch, "E242", {"start": v(-62.69, 0) * mm, "end": v(-63, -0.42) * mm});
            skLineSegment(sketch, "E243", {"start": v(-63, -0.42) * mm, "end": v(-63.29, -0.89) * mm});
            skLineSegment(sketch, "E244", {"start": v(-63.29, -0.89) * mm, "end": v(-63.56, -1.38) * mm});
            skLineSegment(sketch, "E245", {"start": v(-63.56, -1.38) * mm, "end": v(-63.82, -1.88) * mm});
            skLineSegment(sketch, "E246", {"start": v(-63.82, -1.88) * mm, "end": v(-64.04, -2.38) * mm});
            skLineSegment(sketch, "E247", {"start": v(-64.04, -2.38) * mm, "end": v(-64.21, -2.87) * mm});
            skLineSegment(sketch, "E248", {"start": v(-64.21, -2.87) * mm, "end": v(-64.29, -3.1) * mm});
            skLineSegment(sketch, "E249", {"start": v(-64.29, -3.1) * mm, "end": v(-64.35, -3.32) * mm});
            skLineSegment(sketch, "E250", {"start": v(-64.35, -3.32) * mm, "end": v(-64.46, -3.89) * mm});
            skLineSegment(sketch, "E251", {"start": v(-64.46, -3.89) * mm, "end": v(-64.56, -4.5) * mm});
            skLineSegment(sketch, "E252", {"start": v(-64.56, -4.5) * mm, "end": v(-64.63, -5.02) * mm});
            skLineSegment(sketch, "E253", {"start": v(-64.63, -5.02) * mm, "end": v(-64.64, -5.19) * mm});
            skLineSegment(sketch, "E254", {"start": v(-64.64, -5.19) * mm, "end": v(-64.63, -5.26) * mm});
            skLineSegment(sketch, "E255", {"start": v(-64.63, -5.26) * mm, "end": v(-64.59, -5.28) * mm});
            skLineSegment(sketch, "E256", {"start": v(-64.59, -5.28) * mm, "end": v(-64.5, -5.3) * mm});
            skLineSegment(sketch, "E257", {"start": v(-64.5, -5.3) * mm, "end": v(-64.22, -5.36) * mm});
            skLineSegment(sketch, "E258", {"start": v(-64.22, -5.36) * mm, "end": v(-63.9, -5.43) * mm});
            skLineSegment(sketch, "E259", {"start": v(-63.9, -5.43) * mm, "end": v(-63.63, -5.5) * mm});
            skLineSegment(sketch, "E260", {"start": v(-63.63, -5.5) * mm, "end": v(-63.4, -5.6) * mm});
            skLineSegment(sketch, "E261", {"start": v(-63.4, -5.6) * mm, "end": v(-63.2, -5.7) * mm});
            skLineSegment(sketch, "E262", {"start": v(-63.2, -5.7) * mm, "end": v(-63.12, -5.77) * mm});
            skLineSegment(sketch, "E263", {"start": v(-63.12, -5.77) * mm, "end": v(-63.05, -5.84) * mm});
            skLineSegment(sketch, "E264", {"start": v(-63.05, -5.84) * mm, "end": v(-62.98, -5.91) * mm});
            skLineSegment(sketch, "E265", {"start": v(-62.98, -5.91) * mm, "end": v(-62.91, -6) * mm});
            skLineSegment(sketch, "E266", {"start": v(-62.91, -6) * mm, "end": v(-62.8, -6.18) * mm});
            skLineSegment(sketch, "E267", {"start": v(-62.8, -6.18) * mm, "end": v(-62.71, -6.4) * mm});
            skLineSegment(sketch, "E268", {"start": v(-62.71, -6.4) * mm, "end": v(-62.66, -6.54) * mm});
            skLineSegment(sketch, "E269", {"start": v(-62.66, -6.54) * mm, "end": v(-62.65, -6.67) * mm});
            skLineSegment(sketch, "E270", {"start": v(-62.65, -6.67) * mm, "end": v(-62.65, -6.84) * mm});
            skLineSegment(sketch, "E271", {"start": v(-62.65, -6.84) * mm, "end": v(-62.68, -7.1) * mm});
            skLineSegment(sketch, "E272", {"start": v(-62.68, -7.1) * mm, "end": v(-62.72, -7.45) * mm});
            skLineSegment(sketch, "E273", {"start": v(-62.72, -7.45) * mm, "end": v(-62.75, -7.55) * mm});
            skLineSegment(sketch, "E274", {"start": v(-62.75, -7.55) * mm, "end": v(-62.78, -7.61) * mm});
            skLineSegment(sketch, "E275", {"start": v(-62.78, -7.61) * mm, "end": v(-62.8, -7.63) * mm});
            skLineSegment(sketch, "E276", {"start": v(-62.8, -7.63) * mm, "end": v(-62.81, -7.64) * mm});
            skLineSegment(sketch, "E277", {"start": v(-62.81, -7.64) * mm, "end": v(-62.86, -7.62) * mm});
            skLineSegment(sketch, "E278", {"start": v(-62.86, -7.62) * mm, "end": v(-62.92, -7.57) * mm});
            skLineSegment(sketch, "E279", {"start": v(-62.92, -7.57) * mm, "end": v(-63, -7.5) * mm});
            skLineSegment(sketch, "E280", {"start": v(-63, -7.5) * mm, "end": v(-63.14, -7.37) * mm});
            skLineSegment(sketch, "E281", {"start": v(-63.14, -7.37) * mm, "end": v(-63.2, -7.33) * mm});
            skLineSegment(sketch, "E282", {"start": v(-63.2, -7.33) * mm, "end": v(-63.23, -7.31) * mm});
            skLineSegment(sketch, "E283", {"start": v(-63.23, -7.31) * mm, "end": v(-63.26, -7.32) * mm});
            skLineSegment(sketch, "E284", {"start": v(-63.26, -7.32) * mm, "end": v(-63.3, -7.35) * mm});
            skLineSegment(sketch, "E285", {"start": v(-63.3, -7.35) * mm, "end": v(-63.41, -7.43) * mm});
            skLineSegment(sketch, "E286", {"start": v(-63.41, -7.43) * mm, "end": v(-63.56, -7.53) * mm});
            skLineSegment(sketch, "E287", {"start": v(-63.56, -7.53) * mm, "end": v(-63.72, -7.61) * mm});
            skLineSegment(sketch, "E288", {"start": v(-63.72, -7.61) * mm, "end": v(-63.9, -7.66) * mm});
            skLineSegment(sketch, "E289", {"start": v(-63.9, -7.66) * mm, "end": v(-64.08, -7.68) * mm});
            skLineSegment(sketch, "E290", {"start": v(-64.08, -7.68) * mm, "end": v(-64.18, -7.68) * mm});
            skLineSegment(sketch, "E291", {"start": v(-64.18, -7.68) * mm, "end": v(-64.26, -7.66) * mm});
            skLineSegment(sketch, "E292", {"start": v(-64.26, -7.66) * mm, "end": v(-64.32, -7.61) * mm});
            skLineSegment(sketch, "E293", {"start": v(-64.32, -7.61) * mm, "end": v(-64.4, -7.54) * mm});
            skLineSegment(sketch, "E294", {"start": v(-64.4, -7.54) * mm, "end": v(-64.46, -7.48) * mm});
            skLineSegment(sketch, "E295", {"start": v(-64.46, -7.48) * mm, "end": v(-64.5, -7.45) * mm});
            skLineSegment(sketch, "E296", {"start": v(-64.5, -7.45) * mm, "end": v(-64.54, -7.44) * mm});
            skLineSegment(sketch, "E297", {"start": v(-64.54, -7.44) * mm, "end": v(-64.57, -7.46) * mm});
            skLineSegment(sketch, "E298", {"start": v(-64.57, -7.46) * mm, "end": v(-64.61, -7.51) * mm});
            skLineSegment(sketch, "E299", {"start": v(-64.61, -7.51) * mm, "end": v(-64.63, -7.57) * mm});
            skLineSegment(sketch, "E300", {"start": v(-64.63, -7.57) * mm, "end": v(-64.64, -7.62) * mm});
            skLineSegment(sketch, "E301", {"start": v(-64.64, -7.62) * mm, "end": v(-64.66, -7.67) * mm});
            skLineSegment(sketch, "E302", {"start": v(-64.66, -7.67) * mm, "end": v(-64.7, -7.72) * mm});
            skLineSegment(sketch, "E303", {"start": v(-64.7, -7.72) * mm, "end": v(-64.75, -7.76) * mm});
            skLineSegment(sketch, "E304", {"start": v(-64.75, -7.76) * mm, "end": v(-64.81, -7.8) * mm});
            skLineSegment(sketch, "E305", {"start": v(-64.81, -7.8) * mm, "end": v(-64.88, -7.84) * mm});
            skLineSegment(sketch, "E306", {"start": v(-64.88, -7.84) * mm, "end": v(-64.96, -7.87) * mm});
            skLineSegment(sketch, "E307", {"start": v(-64.96, -7.87) * mm, "end": v(-65.04, -7.89) * mm});
            skLineSegment(sketch, "E308", {"start": v(-65.04, -7.89) * mm, "end": v(-65.37, -7.95) * mm});
            skLineSegment(sketch, "E309", {"start": v(-65.37, -7.95) * mm, "end": v(-65.67, -8.03) * mm});
            skLineSegment(sketch, "E310", {"start": v(-65.67, -8.03) * mm, "end": v(-65.8, -8.08) * mm});
            skLineSegment(sketch, "E311", {"start": v(-65.8, -8.08) * mm, "end": v(-65.93, -8.14) * mm});
            skLineSegment(sketch, "E312", {"start": v(-65.93, -8.14) * mm, "end": v(-66.04, -8.2) * mm});
            skLineSegment(sketch, "E313", {"start": v(-66.04, -8.2) * mm, "end": v(-66.15, -8.28) * mm});
            skLineSegment(sketch, "E314", {"start": v(-66.15, -8.28) * mm, "end": v(-66.25, -8.36) * mm});
            skLineSegment(sketch, "E315", {"start": v(-66.25, -8.36) * mm, "end": v(-66.35, -8.45) * mm});
            skLineSegment(sketch, "E316", {"start": v(-66.35, -8.45) * mm, "end": v(-66.44, -8.55) * mm});
            skLineSegment(sketch, "E317", {"start": v(-66.44, -8.55) * mm, "end": v(-66.52, -8.66) * mm});
            skLineSegment(sketch, "E318", {"start": v(-66.52, -8.66) * mm, "end": v(-66.68, -8.9) * mm});
            skLineSegment(sketch, "E319", {"start": v(-66.68, -8.9) * mm, "end": v(-66.82, -9.2) * mm});
            skLineSegment(sketch, "E320", {"start": v(-66.82, -9.2) * mm, "end": v(-66.92, -9.43) * mm});
            skLineSegment(sketch, "E321", {"start": v(-66.92, -9.43) * mm, "end": v(-66.98, -9.6) * mm});
            skLineSegment(sketch, "E322", {"start": v(-66.98, -9.6) * mm, "end": v(-67, -9.74) * mm});
            skLineSegment(sketch, "E323", {"start": v(-67, -9.74) * mm, "end": v(-67.01, -9.9) * mm});
            skLineSegment(sketch, "E324", {"start": v(-67.01, -9.9) * mm, "end": v(-67.01, -10.04) * mm});
            skLineSegment(sketch, "E325", {"start": v(-67.01, -10.04) * mm, "end": v(-67.03, -10.12) * mm});
            skLineSegment(sketch, "E326", {"start": v(-67.03, -10.12) * mm, "end": v(-67.04, -10.15) * mm});
            skLineSegment(sketch, "E327", {"start": v(-67.04, -10.15) * mm, "end": v(-67.05, -10.16) * mm});
            skLineSegment(sketch, "E328", {"start": v(-67.05, -10.16) * mm, "end": v(-67.1, -10.17) * mm});
            skLineSegment(sketch, "E329", {"start": v(-67.1, -10.17) * mm, "end": v(-67.14, -10.16) * mm});
            skLineSegment(sketch, "E330", {"start": v(-67.14, -10.16) * mm, "end": v(-67.2, -10.14) * mm});
            skLineSegment(sketch, "E331", {"start": v(-67.2, -10.14) * mm, "end": v(-67.3, -10.07) * mm});
            skLineSegment(sketch, "E332", {"start": v(-67.16, -9.43) * mm, "end": v(-67.13, -9.21) * mm});
            skLineSegment(sketch, "E333", {"start": v(-67.13, -9.21) * mm, "end": v(-67.08, -9.03) * mm});
            skLineSegment(sketch, "E334", {"start": v(-67.08, -9.03) * mm, "end": v(-67, -8.85) * mm});
            skLineSegment(sketch, "E335", {"start": v(-67, -8.85) * mm, "end": v(-66.89, -8.63) * mm});
            skLineSegment(sketch, "E336", {"start": v(-66.89, -8.63) * mm, "end": v(-66.82, -8.52) * mm});
            skLineSegment(sketch, "E337", {"start": v(-66.82, -8.52) * mm, "end": v(-66.74, -8.4) * mm});
            skLineSegment(sketch, "E338", {"start": v(-66.74, -8.4) * mm, "end": v(-66.54, -8.18) * mm});
            skLineSegment(sketch, "E339", {"start": v(-66.54, -8.18) * mm, "end": v(-66.33, -7.98) * mm});
            skLineSegment(sketch, "E340", {"start": v(-66.33, -7.98) * mm, "end": v(-66.23, -7.9) * mm});
            skLineSegment(sketch, "E341", {"start": v(-66.23, -7.9) * mm, "end": v(-66.14, -7.85) * mm});
            skLineSegment(sketch, "E342", {"start": v(-66.14, -7.85) * mm, "end": v(-65.92, -7.77) * mm});
            skLineSegment(sketch, "E343", {"start": v(-65.92, -7.77) * mm, "end": v(-65.6, -7.69) * mm});
            skLineSegment(sketch, "E344", {"start": v(-65.6, -7.69) * mm, "end": v(-65.42, -7.64) * mm});
            skLineSegment(sketch, "E345", {"start": v(-65.42, -7.64) * mm, "end": v(-65.26, -7.59) * mm});
            skLineSegment(sketch, "E346", {"start": v(-65.26, -7.59) * mm, "end": v(-65.12, -7.53) * mm});
            skLineSegment(sketch, "E347", {"start": v(-65.12, -7.53) * mm, "end": v(-65, -7.47) * mm});
            skLineSegment(sketch, "E348", {"start": v(-65, -7.47) * mm, "end": v(-64.9, -7.41) * mm});
            skLineSegment(sketch, "E349", {"start": v(-64.9, -7.41) * mm, "end": v(-64.82, -7.34) * mm});
            skLineSegment(sketch, "E350", {"start": v(-64.82, -7.34) * mm, "end": v(-64.76, -7.27) * mm});
            skLineSegment(sketch, "E351", {"start": v(-64.76, -7.27) * mm, "end": v(-64.72, -7.2) * mm});
            skLineSegment(sketch, "E352", {"start": v(-64.72, -7.2) * mm, "end": v(-64.67, -7.04) * mm});
            skLineSegment(sketch, "E353", {"start": v(-64.67, -7.04) * mm, "end": v(-64.56, -7.13) * mm});
            skLineSegment(sketch, "E354", {"start": v(-64.56, -7.13) * mm, "end": v(-64.49, -7.18) * mm});
            skLineSegment(sketch, "E355", {"start": v(-64.49, -7.18) * mm, "end": v(-64.4, -7.23) * mm});
            skLineSegment(sketch, "E356", {"start": v(-64.4, -7.23) * mm, "end": v(-64.2, -7.32) * mm});
            skLineSegment(sketch, "E357", {"start": v(-64.2, -7.32) * mm, "end": v(-64.02, -7.37) * mm});
            skLineSegment(sketch, "E358", {"start": v(-64.02, -7.37) * mm, "end": v(-63.94, -7.38) * mm});
            skLineSegment(sketch, "E359", {"start": v(-63.94, -7.38) * mm, "end": v(-63.88, -7.38) * mm});
            skLineSegment(sketch, "E360", {"start": v(-63.88, -7.38) * mm, "end": v(-63.74, -7.32) * mm});
            skLineSegment(sketch, "E361", {"start": v(-63.74, -7.32) * mm, "end": v(-63.54, -7.24) * mm});
            skLineSegment(sketch, "E362", {"start": v(-63.54, -7.24) * mm, "end": v(-63.4, -7.17) * mm});
            skLineSegment(sketch, "E363", {"start": v(-63.4, -7.17) * mm, "end": v(-63.31, -7.15) * mm});
            skLineSegment(sketch, "E364", {"start": v(-63.31, -7.15) * mm, "end": v(-63.24, -7.16) * mm});
            skLineSegment(sketch, "E365", {"start": v(-63.24, -7.16) * mm, "end": v(-63.14, -7.2) * mm});
            skLineSegment(sketch, "E366", {"start": v(-63.14, -7.2) * mm, "end": v(-63.04, -7.24) * mm});
            skLineSegment(sketch, "E367", {"start": v(-63.04, -7.24) * mm, "end": v(-62.97, -7.24) * mm});
            skLineSegment(sketch, "E368", {"start": v(-62.97, -7.24) * mm, "end": v(-62.96, -7.23) * mm});
            skLineSegment(sketch, "E369", {"start": v(-62.96, -7.23) * mm, "end": v(-62.96, -7.2) * mm});
            skLineSegment(sketch, "E370", {"start": v(-62.96, -7.2) * mm, "end": v(-62.98, -7.14) * mm});
            skLineSegment(sketch, "E371", {"start": v(-62.98, -7.14) * mm, "end": v(-63.02, -7.09) * mm});
            skLineSegment(sketch, "E372", {"start": v(-63.02, -7.09) * mm, "end": v(-63.08, -7.03) * mm});
            skLineSegment(sketch, "E373", {"start": v(-63.08, -7.03) * mm, "end": v(-63.15, -6.98) * mm});
            skLineSegment(sketch, "E374", {"start": v(-63.15, -6.98) * mm, "end": v(-63.23, -6.94) * mm});
            skLineSegment(sketch, "E375", {"start": v(-63.23, -6.94) * mm, "end": v(-63.44, -6.85) * mm});
            skLineSegment(sketch, "E376", {"start": v(-63.44, -6.85) * mm, "end": v(-63.68, -6.8) * mm});
            skLineSegment(sketch, "E377", {"start": v(-63.68, -6.8) * mm, "end": v(-63.92, -6.74) * mm});
            skLineSegment(sketch, "E378", {"start": v(-63.92, -6.74) * mm, "end": v(-64.01, -6.7) * mm});
            skLineSegment(sketch, "E379", {"start": v(-64.01, -6.7) * mm, "end": v(-64.1, -6.67) * mm});
            skLineSegment(sketch, "E380", {"start": v(-64.1, -6.67) * mm, "end": v(-64.17, -6.63) * mm});
            skLineSegment(sketch, "E381", {"start": v(-64.17, -6.63) * mm, "end": v(-64.24, -6.58) * mm});
            skLineSegment(sketch, "E382", {"start": v(-64.24, -6.58) * mm, "end": v(-64.3, -6.52) * mm});
            skLineSegment(sketch, "E383", {"start": v(-64.3, -6.52) * mm, "end": v(-64.35, -6.46) * mm});
            skLineSegment(sketch, "E384", {"start": v(-64.35, -6.46) * mm, "end": v(-64.45, -6.32) * mm});
            skLineSegment(sketch, "E385", {"start": v(-64.45, -6.32) * mm, "end": v(-64.52, -6.2) * mm});
            skLineSegment(sketch, "E386", {"start": v(-64.52, -6.2) * mm, "end": v(-64.59, -6.04) * mm});
            skLineSegment(sketch, "E387", {"start": v(-64.59, -6.04) * mm, "end": v(-64.66, -5.84) * mm});
            skLineSegment(sketch, "E388", {"start": v(-64.66, -5.84) * mm, "end": v(-64.73, -5.57) * mm});
            skLineSegment(sketch, "E389", {"start": v(-64.73, -5.57) * mm, "end": v(-64.75, -5.44) * mm});
            skLineSegment(sketch, "E390", {"start": v(-64.75, -5.44) * mm, "end": v(-64.77, -5.3) * mm});
            skLineSegment(sketch, "E391", {"start": v(-64.77, -5.3) * mm, "end": v(-64.77, -4.97) * mm});
            skLineSegment(sketch, "E392", {"start": v(-64.77, -4.97) * mm, "end": v(-64.75, -4.54) * mm});
            skLineSegment(sketch, "E393", {"start": v(-64.75, -4.54) * mm, "end": v(-64.7, -4.04) * mm});
            skLineSegment(sketch, "E394", {"start": v(-64.7, -4.04) * mm, "end": v(-64.7, -3.8) * mm});
            skLineSegment(sketch, "E395", {"start": v(-64.7, -3.8) * mm, "end": v(-64.7, -3.74) * mm});
            skLineSegment(sketch, "E396", {"start": v(-64.7, -3.74) * mm, "end": v(-64.71, -3.7) * mm});
            skLineSegment(sketch, "E397", {"start": v(-64.71, -3.7) * mm, "end": v(-64.73, -3.7) * mm});
            skLineSegment(sketch, "E398", {"start": v(-64.73, -3.7) * mm, "end": v(-64.75, -3.7) * mm});
            skLineSegment(sketch, "E399", {"start": v(-64.75, -3.7) * mm, "end": v(-64.78, -3.7) * mm});
            skLineSegment(sketch, "E400", {"start": v(-64.78, -3.7) * mm, "end": v(-64.81, -3.71) * mm});
            skLineSegment(sketch, "E401", {"start": v(-64.81, -3.71) * mm, "end": v(-64.84, -3.75) * mm});
            skLineSegment(sketch, "E402", {"start": v(-64.84, -3.75) * mm, "end": v(-64.88, -3.8) * mm});
            skLineSegment(sketch, "E403", {"start": v(-64.88, -3.8) * mm, "end": v(-64.95, -3.97) * mm});
            skLineSegment(sketch, "E404", {"start": v(-64.95, -3.97) * mm, "end": v(-65.02, -4.2) * mm});
            skLineSegment(sketch, "E405", {"start": v(-65.02, -4.2) * mm, "end": v(-65.08, -4.37) * mm});
            skLineSegment(sketch, "E406", {"start": v(-65.08, -4.37) * mm, "end": v(-65.11, -4.43) * mm});
            skLineSegment(sketch, "E407", {"start": v(-65.11, -4.43) * mm, "end": v(-65.13, -4.45) * mm});
            skLineSegment(sketch, "E408", {"start": v(-65.13, -4.45) * mm, "end": v(-65.15, -4.45) * mm});
            skLineSegment(sketch, "E409", {"start": v(-65.15, -4.45) * mm, "end": v(-65.16, -4.43) * mm});
            skLineSegment(sketch, "E410", {"start": v(-65.16, -4.43) * mm, "end": v(-65.18, -4.37) * mm});
            skLineSegment(sketch, "E411", {"start": v(-65.18, -4.37) * mm, "end": v(-65.21, -4.1) * mm});
            skLineSegment(sketch, "E412", {"start": v(-65.21, -4.1) * mm, "end": v(-65.23, -3.67) * mm});
            skLineSegment(sketch, "E413", {"start": v(-65.23, -3.67) * mm, "end": v(-65.23, -3.1) * mm});
            skLineSegment(sketch, "E414", {"start": v(-65.23, -3.1) * mm, "end": v(-65.23, -2.69) * mm});
            skLineSegment(sketch, "E415", {"start": v(-65.23, -2.69) * mm, "end": v(-65.2, -2.38) * mm});
            skLineSegment(sketch, "E416", {"start": v(-65.2, -2.38) * mm, "end": v(-65.17, -2.08) * mm});
            skLineSegment(sketch, "E417", {"start": v(-65.17, -2.08) * mm, "end": v(-65.1, -1.7) * mm});
            skLineSegment(sketch, "E418", {"start": v(-65.1, -1.7) * mm, "end": v(-64.9, -0.78) * mm});
            skLineSegment(sketch, "E419", {"start": v(-64.9, -0.78) * mm, "end": v(-64.75, -0.28) * mm});
            skLineSegment(sketch, "E420", {"start": v(-64.75, -0.28) * mm, "end": v(-64.54, 0.38) * mm});
            skLineSegment(sketch, "E421", {"start": v(-64.54, 0.38) * mm, "end": v(-64.32, 1.02) * mm});
            skLineSegment(sketch, "E422", {"start": v(-64.32, 1.02) * mm, "end": v(-64.16, 1.44) * mm});
            skLineSegment(sketch, "E423", {"start": v(-64.16, 1.44) * mm, "end": v(-64.06, 1.66) * mm});
            skLineSegment(sketch, "E424", {"start": v(-64.06, 1.66) * mm, "end": v(-63.93, 1.9) * mm});
            skLineSegment(sketch, "E425", {"start": v(-63.93, 1.9) * mm, "end": v(-63.63, 2.42) * mm});
            skLineSegment(sketch, "E426", {"start": v(-63.63, 2.42) * mm, "end": v(-63.3, 2.93) * mm});
            skLineSegment(sketch, "E427", {"start": v(-63.3, 2.93) * mm, "end": v(-63, 3.37) * mm});
            skLineSegment(sketch, "E428", {"start": v(-63, 3.37) * mm, "end": v(-62.88, 3.52) * mm});
            skLineSegment(sketch, "E429", {"start": v(-62.88, 3.52) * mm, "end": v(-62.73, 3.67) * mm});
            skLineSegment(sketch, "E430", {"start": v(-62.73, 3.67) * mm, "end": v(-62.4, 4) * mm});
            skLineSegment(sketch, "E431", {"start": v(-62.4, 4) * mm, "end": v(-62.06, 4.3) * mm});
            skLineSegment(sketch, "E432", {"start": v(-62.06, 4.3) * mm, "end": v(-61.91, 4.4) * mm});
            skLineSegment(sketch, "E433", {"start": v(-61.91, 4.4) * mm, "end": v(-61.79, 4.48) * mm});
            skLineSegment(sketch, "E434", {"start": v(-61.79, 4.48) * mm, "end": v(-61.34, 4.72) * mm});
            skLineSegment(sketch, "E435", {"start": v(-61.34, 4.72) * mm, "end": v(-60.98, 4.9) * mm});
            skLineSegment(sketch, "E436", {"start": v(-60.98, 4.9) * mm, "end": v(-60.74, 5) * mm});
            skLineSegment(sketch, "E437", {"start": v(-60.74, 5) * mm, "end": v(-60.68, 5) * mm});
            skLineSegment(sketch, "E438", {"start": v(-60.68, 5) * mm, "end": v(-60.66, 5) * mm});
            skLineSegment(sketch, "E439", {"start": v(-60.66, 5) * mm, "end": v(-60.65, 5) * mm});
            skLineSegment(sketch, "E440", {"start": v(-60.65, 5) * mm, "end": v(-60.71, 4.94) * mm});
            skLineSegment(sketch, "E441", {"start": v(-60.71, 4.94) * mm, "end": v(-60.86, 4.84) * mm});
            skLineSegment(sketch, "E442", {"start": v(-60.86, 4.84) * mm, "end": v(-61.24, 4.59) * mm});
            skLineSegment(sketch, "E443", {"start": v(-61.24, 4.59) * mm, "end": v(-61.55, 4.36) * mm});
            skLineSegment(sketch, "E444", {"start": v(-61.55, 4.36) * mm, "end": v(-61.84, 4.1) * mm});
            skLineSegment(sketch, "E445", {"start": v(-61.84, 4.1) * mm, "end": v(-62.17, 3.76) * mm});
            skLineSegment(sketch, "E446", {"start": v(-62.17, 3.76) * mm, "end": v(-62.37, 3.55) * mm});
            skLineSegment(sketch, "E447", {"start": v(-62.37, 3.55) * mm, "end": v(-62.5, 3.39) * mm});
            skLineSegment(sketch, "E448", {"start": v(-62.5, 3.39) * mm, "end": v(-62.6, 3.2) * mm});
            skLineSegment(sketch, "E449", {"start": v(-62.6, 3.2) * mm, "end": v(-62.7, 2.96) * mm});
            skLineSegment(sketch, "E450", {"start": v(-62.7, 2.96) * mm, "end": v(-62.8, 2.7) * mm});
            skLineSegment(sketch, "E451", {"start": v(-62.8, 2.7) * mm, "end": v(-62.85, 2.53) * mm});
            skLineSegment(sketch, "E452", {"start": v(-62.85, 2.53) * mm, "end": v(-62.86, 2.47) * mm});
            skLineSegment(sketch, "E453", {"start": v(-62.86, 2.47) * mm, "end": v(-62.85, 2.43) * mm});
            skLineSegment(sketch, "E454", {"start": v(-62.85, 2.43) * mm, "end": v(-62.83, 2.4) * mm});
            skLineSegment(sketch, "E455", {"start": v(-62.83, 2.4) * mm, "end": v(-62.8, 2.4) * mm});
            skLineSegment(sketch, "E456", {"start": v(-62.8, 2.4) * mm, "end": v(-62.77, 2.41) * mm});
            skLineSegment(sketch, "E457", {"start": v(-62.77, 2.41) * mm, "end": v(-62.73, 2.47) * mm});
            skLineSegment(sketch, "E458", {"start": v(-62.73, 2.47) * mm, "end": v(-62.6, 2.66) * mm});
            skLineSegment(sketch, "E459", {"start": v(-62.6, 2.66) * mm, "end": v(-62.44, 2.9) * mm});
            skLineSegment(sketch, "E460", {"start": v(-62.44, 2.9) * mm, "end": v(-62.2, 3.2) * mm});
            skLineSegment(sketch, "E461", {"start": v(-62.2, 3.2) * mm, "end": v(-61.93, 3.48) * mm});
            skLineSegment(sketch, "E462", {"start": v(-61.93, 3.48) * mm, "end": v(-61.65, 3.75) * mm});
            skLineSegment(sketch, "E463", {"start": v(-61.65, 3.75) * mm, "end": v(-61.4, 3.96) * mm});
            skLineSegment(sketch, "E464", {"start": v(-61.4, 3.96) * mm, "end": v(-61.1, 4.18) * mm});
            skLineSegment(sketch, "E465", {"start": v(-61.1, 4.18) * mm, "end": v(-60.85, 4.34) * mm});
            skLineSegment(sketch, "E466", {"start": v(-60.85, 4.34) * mm, "end": v(-60.77, 4.39) * mm});
            skLineSegment(sketch, "E467", {"start": v(-60.77, 4.39) * mm, "end": v(-60.74, 4.4) * mm});
            skLineSegment(sketch, "E468", {"start": v(-60.74, 4.4) * mm, "end": v(-60.74, 4.37) * mm});
            skLineSegment(sketch, "E469", {"start": v(-60.74, 4.37) * mm, "end": v(-60.76, 4.33) * mm});
            skLineSegment(sketch, "E470", {"start": v(-60.76, 4.33) * mm, "end": v(-60.85, 4.2) * mm});
            skLineSegment(sketch, "E471", {"start": v(-60.85, 4.2) * mm, "end": v(-60.93, 4.08) * mm});
            skLineSegment(sketch, "E472", {"start": v(-60.93, 4.08) * mm, "end": v(-60.95, 4.03) * mm});
            skLineSegment(sketch, "E473", {"start": v(-60.95, 4.03) * mm, "end": v(-60.96, 3.99) * mm});
            skLineSegment(sketch, "E474", {"start": v(-60.96, 3.99) * mm, "end": v(-60.96, 3.94) * mm});
            skLineSegment(sketch, "E475", {"start": v(-60.96, 3.94) * mm, "end": v(-60.94, 3.9) * mm});
            skLineSegment(sketch, "E476", {"start": v(-60.94, 3.9) * mm, "end": v(-60.87, 3.78) * mm});
            skLineSegment(sketch, "E477", {"start": v(-60.87, 3.78) * mm, "end": v(-60.8, 3.7) * mm});
            skLineSegment(sketch, "E478", {"start": v(-60.8, 3.7) * mm, "end": v(-60.76, 3.59) * mm});
            skLineSegment(sketch, "E479", {"start": v(-60.76, 3.59) * mm, "end": v(-60.72, 3.47) * mm});
            skLineSegment(sketch, "E480", {"start": v(-60.72, 3.47) * mm, "end": v(-60.68, 3.32) * mm});
            skLineSegment(sketch, "E481", {"start": v(-60.68, 3.32) * mm, "end": v(-60.62, 2.98) * mm});
            skLineSegment(sketch, "E482", {"start": v(-60.62, 2.98) * mm, "end": v(-60.57, 2.54) * mm});
            skLineSegment(sketch, "E483", {"start": v(-60.57, 2.54) * mm, "end": v(-60.56, 2.23) * mm});
            skLineSegment(sketch, "E484", {"start": v(-60.56, 2.23) * mm, "end": v(-60.55, 1.96) * mm});
            skLineSegment(sketch, "E485", {"start": v(-60.55, 1.96) * mm, "end": v(-60.57, 1.7) * mm});
            skLineSegment(sketch, "E486", {"start": v(-60.57, 1.7) * mm, "end": v(-60.6, 1.47) * mm});
            skLineSegment(sketch, "E487", {"start": v(-60.6, 1.47) * mm, "end": v(-60.64, 1.24) * mm});
            skLineSegment(sketch, "E488", {"start": v(-60.64, 1.24) * mm, "end": v(-60.7, 1) * mm});
            skLineSegment(sketch, "E489", {"start": v(-60.7, 1) * mm, "end": v(-60.79, 0.75) * mm});
            skLineSegment(sketch, "E490", {"start": v(-60.79, 0.75) * mm, "end": v(-60.9, 0.47) * mm});
            skLineSegment(sketch, "E491", {"start": v(-60.9, 0.47) * mm, "end": v(-61, 0.21) * mm});
            skLineSegment(sketch, "E492", {"start": v(-61, 0.21) * mm, "end": v(-61.04, 0.06) * mm});
            skLineSegment(sketch, "E493", {"start": v(-61.04, 0.06) * mm, "end": v(-61.04, 0) * mm});
            skLineSegment(sketch, "E494", {"start": v(-61.04, 0) * mm, "end": v(-61.04, -0.03) * mm});
            skLineSegment(sketch, "E495", {"start": v(-61.04, -0.03) * mm, "end": v(-61.02, -0.06) * mm});
            skLineSegment(sketch, "E496", {"start": v(-61.02, -0.06) * mm, "end": v(-60.99, -0.08) * mm});
            skLineSegment(sketch, "E497", {"start": v(-60.99, -0.08) * mm, "end": v(-60.94, -0.1) * mm});
            skLineSegment(sketch, "E498", {"start": v(-60.94, -0.1) * mm, "end": v(-60.9, -0.1) * mm});
            skLineSegment(sketch, "E499", {"start": v(-60.9, -0.1) * mm, "end": v(-60.83, -0.1) * mm});
            skLineSegment(sketch, "E500", {"start": v(-60.83, -0.1) * mm, "end": v(-60.76, -0.06) * mm});
            skLineSegment(sketch, "E501", {"start": v(-60.76, -0.06) * mm, "end": v(-60.55, 0.09) * mm});
            skLineSegment(sketch, "E502", {"start": v(-60.55, 0.09) * mm, "end": v(-60.24, 0.35) * mm});
            skLineSegment(sketch, "E503", {"start": v(-60.24, 0.35) * mm, "end": v(-59.97, 0.6) * mm});
            skLineSegment(sketch, "E504", {"start": v(-59.97, 0.6) * mm, "end": v(-59.75, 0.81) * mm});
            skLineSegment(sketch, "E505", {"start": v(-59.75, 0.81) * mm, "end": v(-59.58, 1.02) * mm});
            skLineSegment(sketch, "E506", {"start": v(-59.58, 1.02) * mm, "end": v(-59.5, 1.13) * mm});
            skLineSegment(sketch, "E507", {"start": v(-59.5, 1.13) * mm, "end": v(-59.44, 1.25) * mm});
            skLineSegment(sketch, "E508", {"start": v(-59.44, 1.25) * mm, "end": v(-59.38, 1.38) * mm});
            skLineSegment(sketch, "E509", {"start": v(-59.38, 1.38) * mm, "end": v(-59.32, 1.52) * mm});
            skLineSegment(sketch, "E510", {"start": v(-59.32, 1.52) * mm, "end": v(-59.21, 1.85) * mm});
            skLineSegment(sketch, "E511", {"start": v(-59.21, 1.85) * mm, "end": v(-59.1, 2.26) * mm});
            skLineSegment(sketch, "E512", {"start": v(-59.1, 2.26) * mm, "end": v(-58.98, 2.78) * mm});
            skLineSegment(sketch, "E513", {"start": v(-58.98, 2.78) * mm, "end": v(-58.76, 3.72) * mm});
            skLineSegment(sketch, "E514", {"start": v(-58.76, 3.72) * mm, "end": v(-58.67, 4.06) * mm});
            skLineSegment(sketch, "E515", {"start": v(-58.67, 4.06) * mm, "end": v(-58.58, 4.33) * mm});
            skLineSegment(sketch, "E516", {"start": v(-58.58, 4.33) * mm, "end": v(-58.49, 4.55) * mm});
            skLineSegment(sketch, "E517", {"start": v(-58.49, 4.55) * mm, "end": v(-58.39, 4.72) * mm});
            skLineSegment(sketch, "E518", {"start": v(-58.39, 4.72) * mm, "end": v(-58.28, 4.88) * mm});
            skLineSegment(sketch, "E519", {"start": v(-58.28, 4.88) * mm, "end": v(-58.16, 5.02) * mm});
            skLineSegment(sketch, "E520", {"start": v(-58.16, 5.02) * mm, "end": v(-58.06, 5.13) * mm});
            skLineSegment(sketch, "E521", {"start": v(-58.06, 5.13) * mm, "end": v(-58, 5.2) * mm});
            skLineSegment(sketch, "E522", {"start": v(-58, 5.2) * mm, "end": v(-57.97, 5.26) * mm});
            skLineSegment(sketch, "E523", {"start": v(-57.97, 5.26) * mm, "end": v(-57.98, 5.3) * mm});
            skLineSegment(sketch, "E524", {"start": v(-57.98, 5.3) * mm, "end": v(-58.02, 5.32) * mm});
            skLineSegment(sketch, "E525", {"start": v(-58.02, 5.32) * mm, "end": v(-58.1, 5.33) * mm});
            skLineSegment(sketch, "E526", {"start": v(-58.1, 5.33) * mm, "end": v(-58.34, 5.35) * mm});
            skLineSegment(sketch, "E527", {"start": v(-58.34, 5.35) * mm, "end": v(-58.57, 5.36) * mm});
            skLineSegment(sketch, "E528", {"start": v(-58.57, 5.36) * mm, "end": v(-58.64, 5.37) * mm});
            skLineSegment(sketch, "E529", {"start": v(-58.64, 5.37) * mm, "end": v(-58.67, 5.38) * mm});
            skLineSegment(sketch, "E530", {"start": v(-58.67, 5.38) * mm, "end": v(-58.65, 5.4) * mm});
            skLineSegment(sketch, "E531", {"start": v(-58.65, 5.4) * mm, "end": v(-58.61, 5.44) * mm});
            skLineSegment(sketch, "E532", {"start": v(-58.61, 5.44) * mm, "end": v(-58.47, 5.51) * mm});
            skLineSegment(sketch, "E533", {"start": v(-58.47, 5.51) * mm, "end": v(-58.29, 5.6) * mm});
            skLineSegment(sketch, "E534", {"start": v(-58.29, 5.6) * mm, "end": v(-58.1, 5.66) * mm});
            skLineSegment(sketch, "E535", {"start": v(-58.1, 5.66) * mm, "end": v(-57.97, 5.69) * mm});
            skLineSegment(sketch, "E536", {"start": v(-57.97, 5.69) * mm, "end": v(-57.8, 5.7) * mm});
            skLineSegment(sketch, "E537", {"start": v(-57.8, 5.7) * mm, "end": v(-57.6, 5.7) * mm});
            skLineSegment(sketch, "E538", {"start": v(-57.6, 5.7) * mm, "end": v(-57.4, 5.7) * mm});
            skLineSegment(sketch, "E539", {"start": v(-57.4, 5.7) * mm, "end": v(-57.19, 5.69) * mm});
            skLineSegment(sketch, "E540", {"start": v(-57.19, 5.69) * mm, "end": v(-57, 5.66) * mm});
            skLineSegment(sketch, "E541", {"start": v(-57, 5.66) * mm, "end": v(-56.86, 5.63) * mm});
            skLineSegment(sketch, "E542", {"start": v(-56.86, 5.63) * mm, "end": v(-56.77, 5.6) * mm});
            skLineSegment(sketch, "E543", {"start": v(-56.77, 5.6) * mm, "end": v(-56.69, 5.54) * mm});
            skLineSegment(sketch, "E544", {"start": v(-56.69, 5.54) * mm, "end": v(-56.64, 5.48) * mm});
            skLineSegment(sketch, "E545", {"start": v(-56.64, 5.48) * mm, "end": v(-56.64, 5.46) * mm});
            skLineSegment(sketch, "E546", {"start": v(-56.64, 5.46) * mm, "end": v(-56.65, 5.44) * mm});
            skLineSegment(sketch, "E547", {"start": v(-56.65, 5.44) * mm, "end": v(-56.67, 5.43) * mm});
            skLineSegment(sketch, "E548", {"start": v(-56.67, 5.43) * mm, "end": v(-56.7, 5.43) * mm});
            skLineSegment(sketch, "E549", {"start": v(-56.7, 5.43) * mm, "end": v(-56.78, 5.42) * mm});
            skLineSegment(sketch, "E550", {"start": v(-56.78, 5.42) * mm, "end": v(-56.88, 5.38) * mm});
            skLineSegment(sketch, "E551", {"start": v(-56.88, 5.38) * mm, "end": v(-57.14, 5.26) * mm});
            skLineSegment(sketch, "E552", {"start": v(-57.14, 5.26) * mm, "end": v(-57.4, 5.1) * mm});
            skLineSegment(sketch, "E553", {"start": v(-57.4, 5.1) * mm, "end": v(-57.5, 5.03) * mm});
            skLineSegment(sketch, "E554", {"start": v(-57.5, 5.03) * mm, "end": v(-57.58, 4.96) * mm});
            skLineSegment(sketch, "E555", {"start": v(-57.58, 4.96) * mm, "end": v(-57.68, 4.82) * mm});
            skLineSegment(sketch, "E556", {"start": v(-57.68, 4.82) * mm, "end": v(-57.75, 4.7) * mm});
            skLineSegment(sketch, "E557", {"start": v(-57.75, 4.7) * mm, "end": v(-57.76, 4.65) * mm});
            skLineSegment(sketch, "E558", {"start": v(-57.76, 4.65) * mm, "end": v(-57.75, 4.62) * mm});
            skLineSegment(sketch, "E559", {"start": v(-57.75, 4.62) * mm, "end": v(-57.74, 4.6) * mm});
            skLineSegment(sketch, "E560", {"start": v(-57.74, 4.6) * mm, "end": v(-57.7, 4.61) * mm});
            skLineSegment(sketch, "E561", {"start": v(-57.7, 4.61) * mm, "end": v(-57.13, 4.8) * mm});
            skLineSegment(sketch, "E562", {"start": v(-57.13, 4.8) * mm, "end": v(-56.84, 4.87) * mm});
            skLineSegment(sketch, "E563", {"start": v(-56.84, 4.87) * mm, "end": v(-56.62, 4.92) * mm});
            skLineSegment(sketch, "E564", {"start": v(-56.62, 4.92) * mm, "end": v(-56.39, 4.94) * mm});
            skLineSegment(sketch, "E565", {"start": v(-56.39, 4.94) * mm, "end": v(-56.08, 4.94) * mm});
            skLineSegment(sketch, "E566", {"start": v(-56.08, 4.94) * mm, "end": v(-55.77, 4.93) * mm});
            skLineSegment(sketch, "E567", {"start": v(-55.77, 4.93) * mm, "end": v(-55.48, 4.9) * mm});
            skLineSegment(sketch, "E568", {"start": v(-55.48, 4.9) * mm, "end": v(-55.21, 4.86) * mm});
            skLineSegment(sketch, "E569", {"start": v(-55.21, 4.86) * mm, "end": v(-54.95, 4.8) * mm});
            skLineSegment(sketch, "E570", {"start": v(-54.95, 4.8) * mm, "end": v(-54.67, 4.7) * mm});
            skLineSegment(sketch, "E571", {"start": v(-54.67, 4.7) * mm, "end": v(-54.37, 4.57) * mm});
            skLineSegment(sketch, "E572", {"start": v(-54.37, 4.57) * mm, "end": v(-54.04, 4.4) * mm});
            skLineSegment(sketch, "E573", {"start": v(-54.04, 4.4) * mm, "end": v(-53.66, 4.2) * mm});
            skLineSegment(sketch, "E574", {"start": v(-53.66, 4.2) * mm, "end": v(-53.3, 4) * mm});
            skLineSegment(sketch, "E575", {"start": v(-53.3, 4) * mm, "end": v(-53.04, 3.89) * mm});
            skLineSegment(sketch, "E576", {"start": v(-53.04, 3.89) * mm, "end": v(-52.93, 3.85) * mm});
            skLineSegment(sketch, "E577", {"start": v(-52.93, 3.85) * mm, "end": v(-52.83, 3.83) * mm});
            skLineSegment(sketch, "E578", {"start": v(-52.83, 3.83) * mm, "end": v(-52.73, 3.82) * mm});
            skLineSegment(sketch, "E579", {"start": v(-52.73, 3.82) * mm, "end": v(-52.62, 3.82) * mm});
            skLineSegment(sketch, "E580", {"start": v(-52.62, 3.82) * mm, "end": v(-52.54, 3.82) * mm});
            skLineSegment(sketch, "E581", {"start": v(-52.54, 3.82) * mm, "end": v(-52.46, 3.84) * mm});
            skLineSegment(sketch, "E582", {"start": v(-52.46, 3.84) * mm, "end": v(-52.3, 3.9) * mm});
            skLineSegment(sketch, "E583", {"start": v(-52.3, 3.9) * mm, "end": v(-52.23, 3.92) * mm});
            skLineSegment(sketch, "E584", {"start": v(-52.23, 3.92) * mm, "end": v(-52.18, 3.96) * mm});
            skLineSegment(sketch, "E585", {"start": v(-52.18, 3.96) * mm, "end": v(-52.14, 4) * mm});
            skLineSegment(sketch, "E586", {"start": v(-52.14, 4) * mm, "end": v(-52.13, 4.03) * mm});
            skLineSegment(sketch, "E587", {"start": v(-52.13, 4.03) * mm, "end": v(-52.14, 4.05) * mm});
            skLineSegment(sketch, "E588", {"start": v(-52.14, 4.05) * mm, "end": v(-52.18, 4.06) * mm});
            skLineSegment(sketch, "E589", {"start": v(-52.18, 4.06) * mm, "end": v(-52.29, 4.09) * mm});
            skLineSegment(sketch, "E590", {"start": v(-52.29, 4.09) * mm, "end": v(-52.62, 4.13) * mm});
            skLineSegment(sketch, "E591", {"start": v(-52.62, 4.13) * mm, "end": v(-52.93, 4.2) * mm});
            skLineSegment(sketch, "E592", {"start": v(-52.93, 4.2) * mm, "end": v(-53.2, 4.28) * mm});
            skLineSegment(sketch, "E593", {"start": v(-53.2, 4.28) * mm, "end": v(-53.33, 4.33) * mm});
            skLineSegment(sketch, "E594", {"start": v(-53.33, 4.33) * mm, "end": v(-53.43, 4.38) * mm});
            skLineSegment(sketch, "E595", {"start": v(-53.43, 4.38) * mm, "end": v(-53.68, 4.53) * mm});
            skLineSegment(sketch, "E596", {"start": v(-53.68, 4.53) * mm, "end": v(-53.96, 4.72) * mm});
            skLineSegment(sketch, "E597", {"start": v(-53.96, 4.72) * mm, "end": v(-54.23, 4.92) * mm});
            skLineSegment(sketch, "E598", {"start": v(-54.23, 4.92) * mm, "end": v(-54.48, 5.13) * mm});
            skLineSegment(sketch, "E599", {"start": v(-54.48, 5.13) * mm, "end": v(-54.67, 5.29) * mm});
            skLineSegment(sketch, "E600", {"start": v(-54.67, 5.29) * mm, "end": v(-54.86, 5.41) * mm});
            skLineSegment(sketch, "E601", {"start": v(-54.86, 5.41) * mm, "end": v(-55.03, 5.5) * mm});
            skLineSegment(sketch, "E602", {"start": v(-55.03, 5.5) * mm, "end": v(-55.1, 5.51) * mm});
            skLineSegment(sketch, "E603", {"start": v(-55.1, 5.51) * mm, "end": v(-55.17, 5.52) * mm});
            skLineSegment(sketch, "E604", {"start": v(-55.17, 5.52) * mm, "end": v(-55.26, 5.54) * mm});
            skLineSegment(sketch, "E605", {"start": v(-55.26, 5.54) * mm, "end": v(-55.3, 5.55) * mm});
            skLineSegment(sketch, "E606", {"start": v(-55.3, 5.55) * mm, "end": v(-55.31, 5.57) * mm});
            skLineSegment(sketch, "E607", {"start": v(-55.31, 5.57) * mm, "end": v(-55.31, 5.59) * mm});
            skLineSegment(sketch, "E608", {"start": v(-55.31, 5.59) * mm, "end": v(-55.3, 5.6) * mm});
            skLineSegment(sketch, "E609", {"start": v(-55.3, 5.6) * mm, "end": v(-55.27, 5.6) * mm});
            skLineSegment(sketch, "E610", {"start": v(-55.27, 5.6) * mm, "end": v(-55.2, 5.6) * mm});
            skLineSegment(sketch, "E611", {"start": v(-55.2, 5.6) * mm, "end": v(-55.1, 5.6) * mm});
            skLineSegment(sketch, "E612", {"start": v(-55.1, 5.6) * mm, "end": v(-54.9, 5.55) * mm});
            skLineSegment(sketch, "E613", {"start": v(-54.9, 5.55) * mm, "end": v(-54.81, 5.51) * mm});
            skLineSegment(sketch, "E614", {"start": v(-54.81, 5.51) * mm, "end": v(-54.73, 5.48) * mm});
            skLineSegment(sketch, "E615", {"start": v(-54.73, 5.48) * mm, "end": v(-54.51, 5.32) * mm});
            skLineSegment(sketch, "E616", {"start": v(-54.51, 5.32) * mm, "end": v(-54.2, 5.09) * mm});
            skLineSegment(sketch, "E617", {"start": v(-54.2, 5.09) * mm, "end": v(-53.9, 4.86) * mm});
            skLineSegment(sketch, "E618", {"start": v(-53.9, 4.86) * mm, "end": v(-53.57, 4.64) * mm});
            skLineSegment(sketch, "E619", {"start": v(-53.57, 4.64) * mm, "end": v(-53.3, 4.48) * mm});
            skLineSegment(sketch, "E620", {"start": v(-53.3, 4.48) * mm, "end": v(-53.2, 4.43) * mm});
            skLineSegment(sketch, "E621", {"start": v(-53.2, 4.43) * mm, "end": v(-53.14, 4.42) * mm});
            skLineSegment(sketch, "E622", {"start": v(-53.14, 4.42) * mm, "end": v(-53.11, 4.42) * mm});
            skLineSegment(sketch, "E623", {"start": v(-53.11, 4.42) * mm, "end": v(-53.1, 4.44) * mm});
            skLineSegment(sketch, "E624", {"start": v(-53.1, 4.44) * mm, "end": v(-53.1, 4.46) * mm});
            skLineSegment(sketch, "E625", {"start": v(-53.1, 4.46) * mm, "end": v(-53.12, 4.49) * mm});
            skLineSegment(sketch, "E626", {"start": v(-53.12, 4.49) * mm, "end": v(-53.2, 4.57) * mm});
            skLineSegment(sketch, "E627", {"start": v(-53.2, 4.57) * mm, "end": v(-53.34, 4.68) * mm});
            skLineSegment(sketch, "E628", {"start": v(-53.34, 4.68) * mm, "end": v(-53.6, 4.89) * mm});
            skLineSegment(sketch, "E629", {"start": v(-53.6, 4.89) * mm, "end": v(-53.9, 5.14) * mm});
            skLineSegment(sketch, "E630", {"start": v(-53.9, 5.14) * mm, "end": v(-54.12, 5.36) * mm});
            skLineSegment(sketch, "E631", {"start": v(-54.12, 5.36) * mm, "end": v(-54.18, 5.43) * mm});
            skLineSegment(sketch, "E632", {"start": v(-54.18, 5.43) * mm, "end": v(-54.2, 5.47) * mm});
            skLineSegment(sketch, "E633", {"start": v(-54.2, 5.47) * mm, "end": v(-54.18, 5.47) * mm});
            skLineSegment(sketch, "E634", {"start": v(-54.18, 5.47) * mm, "end": v(-54.15, 5.45) * mm});
            skLineSegment(sketch, "E635", {"start": v(-54.15, 5.45) * mm, "end": v(-54.07, 5.37) * mm});
            skLineSegment(sketch, "E636", {"start": v(-54.07, 5.37) * mm, "end": v(-53.98, 5.29) * mm});
            skLineSegment(sketch, "E637", {"start": v(-53.98, 5.29) * mm, "end": v(-53.86, 5.19) * mm});
            skLineSegment(sketch, "E638", {"start": v(-53.86, 5.19) * mm, "end": v(-53.55, 4.95) * mm});
            skLineSegment(sketch, "E639", {"start": v(-53.55, 4.95) * mm, "end": v(-53.24, 4.74) * mm});
            skLineSegment(sketch, "E640", {"start": v(-53.24, 4.74) * mm, "end": v(-53.1, 4.66) * mm});
            skLineSegment(sketch, "E641", {"start": v(-53.1, 4.66) * mm, "end": v(-53, 4.6) * mm});
            skLineSegment(sketch, "E642", {"start": v(-53, 4.6) * mm, "end": v(-52.9, 4.57) * mm});
            skLineSegment(sketch, "E643", {"start": v(-52.9, 4.57) * mm, "end": v(-52.78, 4.53) * mm});
            skLineSegment(sketch, "E644", {"start": v(-52.78, 4.53) * mm, "end": v(-52.52, 4.49) * mm});
            skLineSegment(sketch, "E645", {"start": v(-52.52, 4.49) * mm, "end": v(-52.38, 4.48) * mm});
            skLineSegment(sketch, "E646", {"start": v(-52.38, 4.48) * mm, "end": v(-52.27, 4.48) * mm});
            skLineSegment(sketch, "E647", {"start": v(-52.27, 4.48) * mm, "end": v(-52.2, 4.5) * mm});
            skLineSegment(sketch, "E648", {"start": v(-52.2, 4.5) * mm, "end": v(-52.12, 4.55) * mm});
            skLineSegment(sketch, "E649", {"start": v(-52.12, 4.55) * mm, "end": v(-52.07, 4.6) * mm});
            skLineSegment(sketch, "E650", {"start": v(-52.07, 4.6) * mm, "end": v(-52.04, 4.63) * mm});
            skLineSegment(sketch, "E651", {"start": v(-52.04, 4.63) * mm, "end": v(-52.01, 4.68) * mm});
            skLineSegment(sketch, "E652", {"start": v(-52.01, 4.68) * mm, "end": v(-52, 4.72) * mm});
            skLineSegment(sketch, "E653", {"start": v(-52, 4.72) * mm, "end": v(-52, 4.78) * mm});
            skLineSegment(sketch, "E654", {"start": v(-52, 4.78) * mm, "end": v(-52, 4.83) * mm});
            skLineSegment(sketch, "E655", {"start": v(-52, 4.83) * mm, "end": v(-52.02, 4.9) * mm});
            skLineSegment(sketch, "E656", {"start": v(-52.02, 4.9) * mm, "end": v(-52.05, 4.96) * mm});
            skLineSegment(sketch, "E657", {"start": v(-52.05, 4.96) * mm, "end": v(-52.15, 5.1) * mm});
            skLineSegment(sketch, "E658", {"start": v(-52.15, 5.1) * mm, "end": v(-52.3, 5.27) * mm});
            skLineSegment(sketch, "E659", {"start": v(-52.3, 5.27) * mm, "end": v(-52.48, 5.46) * mm});
            skLineSegment(sketch, "E660", {"start": v(-52.48, 5.46) * mm, "end": v(-52.73, 5.69) * mm});
            skLineSegment(sketch, "E661", {"start": v(-52.73, 5.69) * mm, "end": v(-52.88, 5.82) * mm});
            skLineSegment(sketch, "E662", {"start": v(-52.88, 5.82) * mm, "end": v(-53.54, 5.82) * mm});
            skLineSegment(sketch, "E663", {"start": v(-53.54, 5.82) * mm, "end": v(-53.92, 5.82) * mm});
            skLineSegment(sketch, "E664", {"start": v(-53.92, 5.82) * mm, "end": v(-54.14, 5.84) * mm});
            skLineSegment(sketch, "E665", {"start": v(-54.14, 5.84) * mm, "end": v(-54.21, 5.85) * mm});
            skLineSegment(sketch, "E666", {"start": v(-54.21, 5.85) * mm, "end": v(-54.27, 5.88) * mm});
            skLineSegment(sketch, "E667", {"start": v(-54.27, 5.88) * mm, "end": v(-54.4, 5.95) * mm});
            skLineSegment(sketch, "E668", {"start": v(-54.4, 5.95) * mm, "end": v(-54.55, 6.06) * mm});
            skLineSegment(sketch, "E669", {"start": v(-54.55, 6.06) * mm, "end": v(-54.6, 6.1) * mm});
            skLineSegment(sketch, "E670", {"start": v(-54.6, 6.1) * mm, "end": v(-54.61, 6.13) * mm});
            skLineSegment(sketch, "E671", {"start": v(-54.61, 6.13) * mm, "end": v(-54.6, 6.16) * mm});
            skLineSegment(sketch, "E672", {"start": v(-54.6, 6.16) * mm, "end": v(-54.56, 6.15) * mm});
            skLineSegment(sketch, "E673", {"start": v(-54.56, 6.15) * mm, "end": v(-54.3, 6.05) * mm});
            skLineSegment(sketch, "E674", {"start": v(-54.3, 6.05) * mm, "end": v(-54.2, 6.01) * mm});
            skLineSegment(sketch, "E675", {"start": v(-54.2, 6.01) * mm, "end": v(-54.07, 5.99) * mm});
            skLineSegment(sketch, "E676", {"start": v(-54.07, 5.99) * mm, "end": v(-53.92, 5.97) * mm});
            skLineSegment(sketch, "E677", {"start": v(-53.92, 5.97) * mm, "end": v(-53.75, 5.96) * mm});
            skLineSegment(sketch, "E678", {"start": v(-53.75, 5.96) * mm, "end": v(-53.54, 5.96) * mm});
            skLineSegment(sketch, "E679", {"start": v(-53.54, 5.96) * mm, "end": v(-53.42, 5.98) * mm});
            skLineSegment(sketch, "E680", {"start": v(-53.42, 5.98) * mm, "end": v(-53.38, 5.99) * mm});
            skLineSegment(sketch, "E681", {"start": v(-53.38, 5.99) * mm, "end": v(-53.35, 6) * mm});
            skLineSegment(sketch, "E682", {"start": v(-53.35, 6) * mm, "end": v(-53.3, 6.07) * mm});
            skLineSegment(sketch, "E683", {"start": v(-53.3, 6.07) * mm, "end": v(-53.25, 6.17) * mm});
            skLineSegment(sketch, "E684", {"start": v(-53.25, 6.17) * mm, "end": v(-53.23, 6.29) * mm});
            skLineSegment(sketch, "E685", {"start": v(-53.23, 6.29) * mm, "end": v(-53.23, 6.42) * mm});
            skLineSegment(sketch, "E686", {"start": v(-53.23, 6.42) * mm, "end": v(-53.25, 6.57) * mm});
            skLineSegment(sketch, "E687", {"start": v(-53.25, 6.57) * mm, "end": v(-53.3, 6.74) * mm});
            skLineSegment(sketch, "E688", {"start": v(-53.3, 6.74) * mm, "end": v(-53.37, 6.94) * mm});
            skLineSegment(sketch, "E689", {"start": v(-53.37, 6.94) * mm, "end": v(-53.47, 7.15) * mm});
            skLineSegment(sketch, "E690", {"start": v(-53.47, 7.15) * mm, "end": v(-53.6, 7.4) * mm});
            skLineSegment(sketch, "E691", {"start": v(-53.6, 7.4) * mm, "end": v(-53.75, 7.7) * mm});
            skLineSegment(sketch, "E692", {"start": v(-53.75, 7.7) * mm, "end": v(-53.8, 7.8) * mm});
            skLineSegment(sketch, "E693", {"start": v(-53.8, 7.8) * mm, "end": v(-53.8, 7.85) * mm});
            skLineSegment(sketch, "E694", {"start": v(-53.8, 7.85) * mm, "end": v(-53.79, 7.85) * mm});
            skLineSegment(sketch, "E695", {"start": v(-53.79, 7.85) * mm, "end": v(-53.76, 7.84) * mm});
            skLineSegment(sketch, "E696", {"start": v(-53.76, 7.84) * mm, "end": v(-53.7, 7.77) * mm});
            skLineSegment(sketch, "E697", {"start": v(-53.7, 7.77) * mm, "end": v(-53.6, 7.66) * mm});
            skLineSegment(sketch, "E698", {"start": v(-53.6, 7.66) * mm, "end": v(-53.5, 7.5) * mm});
            skLineSegment(sketch, "E699", {"start": v(-53.5, 7.5) * mm, "end": v(-53.28, 7.16) * mm});
            skLineSegment(sketch, "E700", {"start": v(-53.28, 7.16) * mm, "end": v(-53.19, 6.98) * mm});
            skLineSegment(sketch, "E701", {"start": v(-53.19, 6.98) * mm, "end": v(-53.12, 6.83) * mm});
            skLineSegment(sketch, "E702", {"start": v(-53.12, 6.83) * mm, "end": v(-53.04, 6.66) * mm});
            skLineSegment(sketch, "E703", {"start": v(-53.04, 6.66) * mm, "end": v(-53, 6.62) * mm});
            skLineSegment(sketch, "E704", {"start": v(-53, 6.62) * mm, "end": v(-52.98, 6.6) * mm});
            skLineSegment(sketch, "E705", {"start": v(-52.98, 6.6) * mm, "end": v(-52.96, 6.6) * mm});
            skLineSegment(sketch, "E706", {"start": v(-52.96, 6.6) * mm, "end": v(-52.94, 6.64) * mm});
            skLineSegment(sketch, "E707", {"start": v(-52.94, 6.64) * mm, "end": v(-52.93, 6.7) * mm});
            skLineSegment(sketch, "E708", {"start": v(-52.93, 6.7) * mm, "end": v(-52.93, 6.78) * mm});
            skLineSegment(sketch, "E709", {"start": v(-52.93, 6.78) * mm, "end": v(-52.94, 6.87) * mm});
            skLineSegment(sketch, "E710", {"start": v(-52.94, 6.87) * mm, "end": v(-52.97, 7) * mm});
            skLineSegment(sketch, "E711", {"start": v(-52.97, 7) * mm, "end": v(-53.08, 7.3) * mm});
            skLineSegment(sketch, "E712", {"start": v(-53.08, 7.3) * mm, "end": v(-53.23, 7.62) * mm});
            skLineSegment(sketch, "E713", {"start": v(-53.23, 7.62) * mm, "end": v(-53.3, 7.77) * mm});
            skLineSegment(sketch, "E714", {"start": v(-53.3, 7.77) * mm, "end": v(-53.37, 7.9) * mm});
            skLineSegment(sketch, "E715", {"start": v(-53.37, 7.9) * mm, "end": v(-53.42, 7.97) * mm});
            skLineSegment(sketch, "E716", {"start": v(-53.42, 7.97) * mm, "end": v(-53.5, 8.05) * mm});
            skLineSegment(sketch, "E717", {"start": v(-53.5, 8.05) * mm, "end": v(-53.67, 8.2) * mm});
            skLineSegment(sketch, "E718", {"start": v(-53.67, 8.2) * mm, "end": v(-53.88, 8.37) * mm});
            skLineSegment(sketch, "E719", {"start": v(-53.88, 8.37) * mm, "end": v(-54.13, 8.52) * mm});
            skLineSegment(sketch, "E720", {"start": v(-54.13, 8.52) * mm, "end": v(-54.4, 8.67) * mm});
            skLineSegment(sketch, "E721", {"start": v(-54.4, 8.67) * mm, "end": v(-54.69, 8.8) * mm});
            skLineSegment(sketch, "E722", {"start": v(-54.69, 8.8) * mm, "end": v(-54.98, 8.93) * mm});
            skLineSegment(sketch, "E723", {"start": v(-54.98, 8.93) * mm, "end": v(-55.27, 9.02) * mm});
            skLineSegment(sketch, "E724", {"start": v(-55.27, 9.02) * mm, "end": v(-55.54, 9.08) * mm});
            skLineSegment(sketch, "E725", {"start": v(-55.54, 9.08) * mm, "end": v(-55.85, 9.13) * mm});
            skLineSegment(sketch, "E726", {"start": v(-55.85, 9.13) * mm, "end": v(-56.18, 9.17) * mm});
            skLineSegment(sketch, "E727", {"start": v(-56.18, 9.17) * mm, "end": v(-56.54, 9.2) * mm});
            skLineSegment(sketch, "E728", {"start": v(-56.54, 9.2) * mm, "end": v(-56.9, 9.2) * mm});
            skLineSegment(sketch, "E729", {"start": v(-56.9, 9.2) * mm, "end": v(-57.25, 9.2) * mm});
            skLineSegment(sketch, "E730", {"start": v(-57.25, 9.2) * mm, "end": v(-57.6, 9.19) * mm});
            skLineSegment(sketch, "E731", {"start": v(-57.6, 9.19) * mm, "end": v(-57.9, 9.16) * mm});
            skLineSegment(sketch, "E732", {"start": v(-57.9, 9.16) * mm, "end": v(-58.22, 9.1) * mm});
            skLineSegment(sketch, "E733", {"start": v(-58.22, 9.1) * mm, "end": v(-58.53, 9.05) * mm});
            skLineSegment(sketch, "E734", {"start": v(-58.53, 9.05) * mm, "end": v(-58.84, 8.98) * mm});
            skLineSegment(sketch, "E735", {"start": v(-58.84, 8.98) * mm, "end": v(-59.14, 8.9) * mm});
            skLineSegment(sketch, "E736", {"start": v(-59.14, 8.9) * mm, "end": v(-59.44, 8.8) * mm});
            skLineSegment(sketch, "E737", {"start": v(-59.44, 8.8) * mm, "end": v(-59.73, 8.7) * mm});
            skLineSegment(sketch, "E738", {"start": v(-59.73, 8.7) * mm, "end": v(-60.02, 8.58) * mm});
            skLineSegment(sketch, "E739", {"start": v(-60.02, 8.58) * mm, "end": v(-60.3, 8.45) * mm});
            skLineSegment(sketch, "E740", {"start": v(-60.3, 8.45) * mm, "end": v(-60.58, 8.31) * mm});
            skLineSegment(sketch, "E741", {"start": v(-60.58, 8.31) * mm, "end": v(-60.85, 8.17) * mm});
            skLineSegment(sketch, "E742", {"start": v(-60.85, 8.17) * mm, "end": v(-61.1, 8) * mm});
            skLineSegment(sketch, "E743", {"start": v(-61.1, 8) * mm, "end": v(-61.36, 7.84) * mm});
            skLineSegment(sketch, "E744", {"start": v(-61.36, 7.84) * mm, "end": v(-61.6, 7.66) * mm});
            skLineSegment(sketch, "E745", {"start": v(-61.6, 7.66) * mm, "end": v(-61.84, 7.47) * mm});
            skLineSegment(sketch, "E746", {"start": v(-61.84, 7.47) * mm, "end": v(-62.07, 7.28) * mm});
            skLineSegment(sketch, "E747", {"start": v(-62.07, 7.28) * mm, "end": v(-62.29, 7.07) * mm});
            skLineSegment(sketch, "E748", {"start": v(-62.29, 7.07) * mm, "end": v(-62.44, 6.91) * mm});
            skLineSegment(sketch, "E749", {"start": v(-62.44, 6.91) * mm, "end": v(-62.6, 6.72) * mm});
            skLineSegment(sketch, "E750", {"start": v(-62.6, 6.72) * mm, "end": v(-62.96, 6.27) * mm});
            skLineSegment(sketch, "E751", {"start": v(-62.96, 6.27) * mm, "end": v(-63.3, 5.79) * mm});
            skLineSegment(sketch, "E752", {"start": v(-63.3, 5.79) * mm, "end": v(-63.45, 5.56) * mm});
            skLineSegment(sketch, "E753", {"start": v(-63.45, 5.56) * mm, "end": v(-63.58, 5.36) * mm});
            skLineSegment(sketch, "E754", {"start": v(-63.58, 5.36) * mm, "end": v(-63.8, 4.93) * mm});
            skLineSegment(sketch, "E755", {"start": v(-63.8, 4.93) * mm, "end": v(-64.06, 4.35) * mm});
            skLineSegment(sketch, "E756", {"start": v(-64.06, 4.35) * mm, "end": v(-64.31, 3.74) * mm});
            skLineSegment(sketch, "E757", {"start": v(-64.31, 3.74) * mm, "end": v(-64.5, 3.22) * mm});
            skLineSegment(sketch, "E758", {"start": v(-64.5, 3.22) * mm, "end": v(-64.6, 2.98) * mm});
            skLineSegment(sketch, "E759", {"start": v(-64.6, 2.98) * mm, "end": v(-64.63, 2.92) * mm});
            skLineSegment(sketch, "E760", {"start": v(-64.63, 2.92) * mm, "end": v(-64.65, 2.9) * mm});
            skLineSegment(sketch, "E761", {"start": v(-64.65, 2.9) * mm, "end": v(-64.66, 2.92) * mm});
            skLineSegment(sketch, "E762", {"start": v(-64.66, 2.92) * mm, "end": v(-64.66, 2.97) * mm});
            skLineSegment(sketch, "E763", {"start": v(-64.66, 2.97) * mm, "end": v(-64.6, 3.2) * mm});
            skLineSegment(sketch, "E764", {"start": v(-64.6, 3.2) * mm, "end": v(-64.47, 3.63) * mm});
            skLineSegment(sketch, "E765", {"start": v(-64.47, 3.63) * mm, "end": v(-64.26, 4.22) * mm});
            skLineSegment(sketch, "E766", {"start": v(-64.26, 4.22) * mm, "end": v(-64.04, 4.8) * mm});
            skLineSegment(sketch, "E767", {"start": v(-64.04, 4.8) * mm, "end": v(-63.86, 5.2) * mm});
            skLineSegment(sketch, "E768", {"start": v(-63.86, 5.2) * mm, "end": v(-63.67, 5.55) * mm});
            skLineSegment(sketch, "E769", {"start": v(-63.67, 5.55) * mm, "end": v(-63.44, 5.93) * mm});
            skLineSegment(sketch, "E770", {"start": v(-63.44, 5.93) * mm, "end": v(-63.17, 6.32) * mm});
            skLineSegment(sketch, "E771", {"start": v(-63.17, 6.32) * mm, "end": v(-62.86, 6.76) * mm});
            skLineSegment(sketch, "E772", {"start": v(-62.86, 6.76) * mm, "end": v(-62.56, 7.16) * mm});
            skLineSegment(sketch, "E773", {"start": v(-62.56, 7.16) * mm, "end": v(-62.47, 7.3) * mm});
            skLineSegment(sketch, "E774", {"start": v(-62.47, 7.3) * mm, "end": v(-62.44, 7.36) * mm});
            skLineSegment(sketch, "E775", {"start": v(-62.44, 7.36) * mm, "end": v(-62.45, 7.38) * mm});
            skLineSegment(sketch, "E776", {"start": v(-62.45, 7.38) * mm, "end": v(-62.46, 7.4) * mm});
            skLineSegment(sketch, "E777", {"start": v(-62.46, 7.4) * mm, "end": v(-62.48, 7.4) * mm});
            skLineSegment(sketch, "E778", {"start": v(-62.48, 7.4) * mm, "end": v(-62.52, 7.4) * mm});
            skLineSegment(sketch, "E779", {"start": v(-62.52, 7.4) * mm, "end": v(-62.6, 7.36) * mm});
            skLineSegment(sketch, "E780", {"start": v(-62.6, 7.36) * mm, "end": v(-62.7, 7.3) * mm});
            skLineSegment(sketch, "E781", {"start": v(-62.7, 7.3) * mm, "end": v(-62.82, 7.2) * mm});
            skLineSegment(sketch, "E782", {"start": v(-62.82, 7.2) * mm, "end": v(-62.95, 7.1) * mm});
            skLineSegment(sketch, "E783", {"start": v(-62.95, 7.1) * mm, "end": v(-63.07, 6.97) * mm});
            skLineSegment(sketch, "E784", {"start": v(-63.07, 6.97) * mm, "end": v(-63.2, 6.84) * mm});
            skLineSegment(sketch, "E785", {"start": v(-63.2, 6.84) * mm, "end": v(-63.31, 6.7) * mm});
            skLineSegment(sketch, "E786", {"start": v(-63.31, 6.7) * mm, "end": v(-63.39, 6.64) * mm});
            skLineSegment(sketch, "E787", {"start": v(-63.39, 6.64) * mm, "end": v(-63.41, 6.63) * mm});
            skLineSegment(sketch, "E788", {"start": v(-63.41, 6.63) * mm, "end": v(-63.42, 6.64) * mm});
            skLineSegment(sketch, "E789", {"start": v(-63.42, 6.64) * mm, "end": v(-63.44, 6.7) * mm});
            skLineSegment(sketch, "E790", {"start": v(-63.44, 6.7) * mm, "end": v(-63.45, 6.77) * mm});
            skLineSegment(sketch, "E791", {"start": v(-63.45, 6.77) * mm, "end": v(-63.48, 6.84) * mm});
            skLineSegment(sketch, "E792", {"start": v(-63.48, 6.84) * mm, "end": v(-63.59, 7) * mm});
            skLineSegment(sketch, "E793", {"start": v(-63.59, 7) * mm, "end": v(-63.73, 7.14) * mm});
            skLineSegment(sketch, "E794", {"start": v(-63.73, 7.14) * mm, "end": v(-63.8, 7.2) * mm});
            skLineSegment(sketch, "E795", {"start": v(-63.8, 7.2) * mm, "end": v(-63.86, 7.23) * mm});
            skLineSegment(sketch, "E796", {"start": v(-63.86, 7.23) * mm, "end": v(-63.94, 7.25) * mm});
            skLineSegment(sketch, "E797", {"start": v(-63.94, 7.25) * mm, "end": v(-64.05, 7.26) * mm});
            skLineSegment(sketch, "E798", {"start": v(-64.05, 7.26) * mm, "end": v(-64.17, 7.26) * mm});
            skLineSegment(sketch, "E799", {"start": v(-64.17, 7.26) * mm, "end": v(-64.3, 7.26) * mm});
            skLineSegment(sketch, "E800", {"start": v(-64.3, 7.26) * mm, "end": v(-64.45, 7.24) * mm});
            skLineSegment(sketch, "E801", {"start": v(-64.45, 7.24) * mm, "end": v(-64.6, 7.2) * mm});
            skLineSegment(sketch, "E802", {"start": v(-64.6, 7.2) * mm, "end": v(-64.73, 7.16) * mm});
            skLineSegment(sketch, "E803", {"start": v(-64.73, 7.16) * mm, "end": v(-64.86, 7.1) * mm});
            skLineSegment(sketch, "E804", {"start": v(-64.86, 7.1) * mm, "end": v(-64.98, 7.03) * mm});
            skLineSegment(sketch, "E805", {"start": v(-64.98, 7.03) * mm, "end": v(-65.1, 6.95) * mm});
            skLineSegment(sketch, "E806", {"start": v(-65.1, 6.95) * mm, "end": v(-65.2, 6.85) * mm});
            skLineSegment(sketch, "E807", {"start": v(-65.2, 6.85) * mm, "end": v(-65.29, 6.75) * mm});
            skLineSegment(sketch, "E808", {"start": v(-65.29, 6.75) * mm, "end": v(-65.4, 6.6) * mm});
            skLineSegment(sketch, "E809", {"start": v(-65.4, 6.6) * mm, "end": v(-65.46, 6.48) * mm});
            skLineSegment(sketch, "E810", {"start": v(-65.46, 6.48) * mm, "end": v(-65.5, 6.38) * mm});
            skLineSegment(sketch, "E811", {"start": v(-65.5, 6.38) * mm, "end": v(-65.5, 6.35) * mm});
            skLineSegment(sketch, "E812", {"start": v(-65.5, 6.35) * mm, "end": v(-65.49, 6.31) * mm});
            skLineSegment(sketch, "E813", {"start": v(-65.49, 6.31) * mm, "end": v(-65.47, 6.29) * mm});
            skLineSegment(sketch, "E814", {"start": v(-65.47, 6.29) * mm, "end": v(-65.44, 6.26) * mm});
            skLineSegment(sketch, "E815", {"start": v(-65.44, 6.26) * mm, "end": v(-65.35, 6.23) * mm});
            skLineSegment(sketch, "E816", {"start": v(-65.35, 6.23) * mm, "end": v(-65.22, 6.22) * mm});
            skLineSegment(sketch, "E817", {"start": v(-65.22, 6.22) * mm, "end": v(-65.04, 6.21) * mm});
            skLineSegment(sketch, "E818", {"start": v(-65.04, 6.21) * mm, "end": v(-64.77, 6.2) * mm});
            skLineSegment(sketch, "E819", {"start": v(-64.77, 6.2) * mm, "end": v(-64.66, 6.18) * mm});
            skLineSegment(sketch, "E820", {"start": v(-64.66, 6.18) * mm, "end": v(-64.57, 6.16) * mm});
            skLineSegment(sketch, "E821", {"start": v(-64.57, 6.16) * mm, "end": v(-64.5, 6.12) * mm});
            skLineSegment(sketch, "E822", {"start": v(-64.5, 6.12) * mm, "end": v(-64.42, 6.08) * mm});
            skLineSegment(sketch, "E823", {"start": v(-64.42, 6.08) * mm, "end": v(-64.37, 6.02) * mm});
            skLineSegment(sketch, "E824", {"start": v(-64.37, 6.02) * mm, "end": v(-64.31, 5.95) * mm});
            skLineSegment(sketch, "E825", {"start": v(-64.31, 5.95) * mm, "end": v(-64.27, 5.87) * mm});
            skLineSegment(sketch, "E826", {"start": v(-64.27, 5.87) * mm, "end": v(-64.24, 5.78) * mm});
            skLineSegment(sketch, "E827", {"start": v(-64.24, 5.78) * mm, "end": v(-64.23, 5.67) * mm});
            skLineSegment(sketch, "E828", {"start": v(-64.23, 5.67) * mm, "end": v(-64.24, 5.55) * mm});
            skLineSegment(sketch, "E829", {"start": v(-64.24, 5.55) * mm, "end": v(-64.27, 5.4) * mm});
            skLineSegment(sketch, "E830", {"start": v(-64.27, 5.4) * mm, "end": v(-64.32, 5.23) * mm});
            skLineSegment(sketch, "E831", {"start": v(-64.32, 5.23) * mm, "end": v(-64.48, 4.79) * mm});
            skLineSegment(sketch, "E832", {"start": v(-64.48, 4.79) * mm, "end": v(-64.74, 4.12) * mm});
            skLineSegment(sketch, "E833", {"start": v(-64.74, 4.12) * mm, "end": v(-64.84, 3.84) * mm});
            skLineSegment(sketch, "E834", {"start": v(-64.84, 3.84) * mm, "end": v(-64.92, 3.61) * mm});
            skLineSegment(sketch, "E835", {"start": v(-64.92, 3.61) * mm, "end": v(-65.02, 3.28) * mm});
            skLineSegment(sketch, "E836", {"start": v(-65.02, 3.28) * mm, "end": v(-65.24, 2.45) * mm});
            skLineSegment(sketch, "E837", {"start": v(-65.24, 2.45) * mm, "end": v(-65.45, 1.56) * mm});
            skLineSegment(sketch, "E838", {"start": v(-65.45, 1.56) * mm, "end": v(-65.53, 1.17) * mm});
            skLineSegment(sketch, "E839", {"start": v(-65.53, 1.17) * mm, "end": v(-65.6, 0.85) * mm});
            skLineSegment(sketch, "E840", {"start": v(-65.6, 0.85) * mm, "end": v(-65.65, 0.46) * mm});
            skLineSegment(sketch, "E841", {"start": v(-65.65, 0.46) * mm, "end": v(-65.7, 0.01) * mm});
            skLineSegment(sketch, "E842", {"start": v(-65.7, 0.01) * mm, "end": v(-65.73, -0.49) * mm});
            skLineSegment(sketch, "E843", {"start": v(-65.73, -0.49) * mm, "end": v(-65.75, -1.02) * mm});
            skLineSegment(sketch, "E844", {"start": v(-65.75, -1.02) * mm, "end": v(-65.76, -1.56) * mm});
            skLineSegment(sketch, "E845", {"start": v(-65.76, -1.56) * mm, "end": v(-65.75, -2.11) * mm});
            skLineSegment(sketch, "E846", {"start": v(-65.75, -2.11) * mm, "end": v(-65.74, -2.65) * mm});
            skLineSegment(sketch, "E847", {"start": v(-65.74, -2.65) * mm, "end": v(-65.7, -3.15) * mm});
            skLineSegment(sketch, "E848", {"start": v(-65.7, -3.15) * mm, "end": v(-65.67, -3.58) * mm});
            skLineSegment(sketch, "E849", {"start": v(-65.67, -3.58) * mm, "end": v(-65.61, -4) * mm});
            skLineSegment(sketch, "E850", {"start": v(-65.61, -4) * mm, "end": v(-65.53, -4.53) * mm});
            skLineSegment(sketch, "E851", {"start": v(-65.53, -4.53) * mm, "end": v(-65.4, -5.28) * mm});
            skLineSegment(sketch, "E852", {"start": v(-65.4, -5.28) * mm, "end": v(-65.36, -5.52) * mm});
            skLineSegment(sketch, "E853", {"start": v(-65.36, -5.52) * mm, "end": v(-65.35, -5.64) * mm});
            skLineSegment(sketch, "E854", {"start": v(-65.35, -5.64) * mm, "end": v(-65.44, -5.67) * mm});
            skLineSegment(sketch, "E855", {"start": v(-65.44, -5.67) * mm, "end": v(-65.62, -5.7) * mm});
            skLineSegment(sketch, "E856", {"start": v(-65.62, -5.7) * mm, "end": v(-65.78, -5.74) * mm});
            skLineSegment(sketch, "E857", {"start": v(-65.78, -5.74) * mm, "end": v(-65.93, -5.79) * mm});
            skLineSegment(sketch, "E858", {"start": v(-65.93, -5.79) * mm, "end": v(-66.07, -5.84) * mm});
            skLineSegment(sketch, "E859", {"start": v(-66.07, -5.84) * mm, "end": v(-66.2, -5.9) * mm});
            skLineSegment(sketch, "E860", {"start": v(-66.2, -5.9) * mm, "end": v(-66.33, -5.97) * mm});
            skLineSegment(sketch, "E861", {"start": v(-66.33, -5.97) * mm, "end": v(-66.44, -6.05) * mm});
            skLineSegment(sketch, "E862", {"start": v(-66.44, -6.05) * mm, "end": v(-66.55, -6.14) * mm});
            skLineSegment(sketch, "E863", {"start": v(-66.55, -6.14) * mm, "end": v(-66.64, -6.23) * mm});
            skLineSegment(sketch, "E864", {"start": v(-66.64, -6.23) * mm, "end": v(-66.73, -6.35) * mm});
            skLineSegment(sketch, "E865", {"start": v(-66.73, -6.35) * mm, "end": v(-66.82, -6.48) * mm});
            skLineSegment(sketch, "E866", {"start": v(-66.82, -6.48) * mm, "end": v(-67, -6.76) * mm});
            skLineSegment(sketch, "E867", {"start": v(-67, -6.76) * mm, "end": v(-67.15, -7.07) * mm});
            skLineSegment(sketch, "E868", {"start": v(-67.15, -7.07) * mm, "end": v(-67.27, -7.4) * mm});
            skLineSegment(sketch, "E869", {"start": v(-67.27, -7.4) * mm, "end": v(-67.38, -7.72) * mm});
            skLineSegment(sketch, "E870", {"start": v(-67.38, -7.72) * mm, "end": v(-67.44, -8.04) * mm});
            skLineSegment(sketch, "E871", {"start": v(-67.44, -8.04) * mm, "end": v(-67.48, -8.33) * mm});
            skLineSegment(sketch, "E872", {"start": v(-67.48, -8.33) * mm, "end": v(-67.48, -8.47) * mm});
            skLineSegment(sketch, "E873", {"start": v(-67.48, -8.47) * mm, "end": v(-67.47, -8.6) * mm});
            skLineSegment(sketch, "E874", {"start": v(-67.47, -8.6) * mm, "end": v(-67.4, -9.1) * mm});
            skLineSegment(sketch, "E875", {"start": v(-67.4, -9.1) * mm, "end": v(-67.35, -9.44) * mm});
            skLineSegment(sketch, "E876", {"start": v(-67.35, -9.44) * mm, "end": v(-67.3, -9.64) * mm});
            skLineSegment(sketch, "E877", {"start": v(-67.3, -9.64) * mm, "end": v(-67.28, -9.68) * mm});
            skLineSegment(sketch, "E878", {"start": v(-67.28, -9.68) * mm, "end": v(-67.25, -9.7) * mm});
            skLineSegment(sketch, "E879", {"start": v(-67.25, -9.7) * mm, "end": v(-67.22, -9.68) * mm});
            skLineSegment(sketch, "E880", {"start": v(-67.22, -9.68) * mm, "end": v(-67.2, -9.63) * mm});
            skLineSegment(sketch, "E881", {"start": v(-67.2, -9.63) * mm, "end": v(-67.18, -9.54) * mm});
            skLineSegment(sketch, "E882", {"start": v(-67.18, -9.54) * mm, "end": v(-67.16, -9.43) * mm});
            skLineSegment(sketch, "E883", {"start": v(-55.65, 6.07) * mm, "end": v(-55.7, 6.13) * mm});
            skLineSegment(sketch, "E884", {"start": v(-55.7, 6.13) * mm, "end": v(-55.72, 6.19) * mm});
            skLineSegment(sketch, "E885", {"start": v(-55.72, 6.19) * mm, "end": v(-55.75, 6.25) * mm});
            skLineSegment(sketch, "E886", {"start": v(-55.75, 6.25) * mm, "end": v(-55.76, 6.31) * mm});
            skLineSegment(sketch, "E887", {"start": v(-55.76, 6.31) * mm, "end": v(-55.77, 6.38) * mm});
            skLineSegment(sketch, "E888", {"start": v(-55.77, 6.38) * mm, "end": v(-55.76, 6.45) * mm});
            skLineSegment(sketch, "E889", {"start": v(-55.76, 6.45) * mm, "end": v(-55.72, 6.6) * mm});
            skLineSegment(sketch, "E890", {"start": v(-55.72, 6.6) * mm, "end": v(-55.68, 6.68) * mm});
            skLineSegment(sketch, "E891", {"start": v(-55.68, 6.68) * mm, "end": v(-55.66, 6.7) * mm});
            skLineSegment(sketch, "E892", {"start": v(-55.66, 6.7) * mm, "end": v(-55.63, 6.71) * mm});
            skLineSegment(sketch, "E893", {"start": v(-55.63, 6.71) * mm, "end": v(-55.6, 6.71) * mm});
            skLineSegment(sketch, "E894", {"start": v(-55.6, 6.71) * mm, "end": v(-55.55, 6.7) * mm});
            skLineSegment(sketch, "E895", {"start": v(-55.55, 6.7) * mm, "end": v(-55.43, 6.65) * mm});
            skLineSegment(sketch, "E896", {"start": v(-55.43, 6.65) * mm, "end": v(-55.33, 6.59) * mm});
            skLineSegment(sketch, "E897", {"start": v(-55.33, 6.59) * mm, "end": v(-55.27, 6.53) * mm});
            skLineSegment(sketch, "E898", {"start": v(-55.27, 6.53) * mm, "end": v(-55.26, 6.5) * mm});
            skLineSegment(sketch, "E899", {"start": v(-55.26, 6.5) * mm, "end": v(-55.26, 6.47) * mm});
            skLineSegment(sketch, "E900", {"start": v(-55.26, 6.47) * mm, "end": v(-55.28, 6.44) * mm});
            skLineSegment(sketch, "E901", {"start": v(-55.28, 6.44) * mm, "end": v(-55.3, 6.42) * mm});
            skLineSegment(sketch, "E902", {"start": v(-55.3, 6.42) * mm, "end": v(-55.35, 6.36) * mm});
            skLineSegment(sketch, "E903", {"start": v(-55.35, 6.36) * mm, "end": v(-55.36, 6.3) * mm});
            skLineSegment(sketch, "E904", {"start": v(-55.36, 6.3) * mm, "end": v(-55.35, 6.23) * mm});
            skLineSegment(sketch, "E905", {"start": v(-55.35, 6.23) * mm, "end": v(-55.32, 6.18) * mm});
            skLineSegment(sketch, "E906", {"start": v(-55.32, 6.18) * mm, "end": v(-55.28, 6.13) * mm});
            skLineSegment(sketch, "E907", {"start": v(-55.28, 6.13) * mm, "end": v(-55.22, 6.1) * mm});
            skLineSegment(sketch, "E908", {"start": v(-55.22, 6.1) * mm, "end": v(-55.16, 6.1) * mm});
            skLineSegment(sketch, "E909", {"start": v(-55.16, 6.1) * mm, "end": v(-55.09, 6.12) * mm});
            skLineSegment(sketch, "E910", {"start": v(-55.09, 6.12) * mm, "end": v(-55.03, 6.17) * mm});
            skLineSegment(sketch, "E911", {"start": v(-55.03, 6.17) * mm, "end": v(-55, 6.24) * mm});
            skLineSegment(sketch, "E912", {"start": v(-55, 6.24) * mm, "end": v(-54.99, 6.31) * mm});
            skLineSegment(sketch, "E913", {"start": v(-54.99, 6.31) * mm, "end": v(-55, 6.4) * mm});
            skLineSegment(sketch, "E914", {"start": v(-55, 6.4) * mm, "end": v(-55.03, 6.49) * mm});
            skLineSegment(sketch, "E915", {"start": v(-55.03, 6.49) * mm, "end": v(-55.09, 6.58) * mm});
            skLineSegment(sketch, "E916", {"start": v(-55.09, 6.58) * mm, "end": v(-55.16, 6.67) * mm});
            skLineSegment(sketch, "E917", {"start": v(-55.16, 6.67) * mm, "end": v(-55.25, 6.75) * mm});
            skLineSegment(sketch, "E918", {"start": v(-55.25, 6.75) * mm, "end": v(-55.32, 6.8) * mm});
            skLineSegment(sketch, "E919", {"start": v(-55.32, 6.8) * mm, "end": v(-55.4, 6.83) * mm});
            skLineSegment(sketch, "E920", {"start": v(-55.4, 6.83) * mm, "end": v(-55.48, 6.86) * mm});
            skLineSegment(sketch, "E921", {"start": v(-55.48, 6.86) * mm, "end": v(-55.57, 6.87) * mm});
            skLineSegment(sketch, "E922", {"start": v(-55.57, 6.87) * mm, "end": v(-55.66, 6.88) * mm});
            skLineSegment(sketch, "E923", {"start": v(-55.66, 6.88) * mm, "end": v(-55.77, 6.87) * mm});
            skLineSegment(sketch, "E924", {"start": v(-55.77, 6.87) * mm, "end": v(-56, 6.84) * mm});
            skLineSegment(sketch, "E925", {"start": v(-56, 6.84) * mm, "end": v(-56.12, 6.82) * mm});
            skLineSegment(sketch, "E926", {"start": v(-56.12, 6.82) * mm, "end": v(-56.15, 6.83) * mm});
            skLineSegment(sketch, "E927", {"start": v(-56.15, 6.83) * mm, "end": v(-56.16, 6.85) * mm});
            skLineSegment(sketch, "E928", {"start": v(-56.16, 6.85) * mm, "end": v(-56.15, 6.9) * mm});
            skLineSegment(sketch, "E929", {"start": v(-56.15, 6.9) * mm, "end": v(-56.1, 6.94) * mm});
            skLineSegment(sketch, "E930", {"start": v(-56.1, 6.94) * mm, "end": v(-56.04, 6.98) * mm});
            skLineSegment(sketch, "E931", {"start": v(-56.04, 6.98) * mm, "end": v(-55.97, 7.02) * mm});
            skLineSegment(sketch, "E932", {"start": v(-55.97, 7.02) * mm, "end": v(-55.88, 7.05) * mm});
            skLineSegment(sketch, "E933", {"start": v(-55.88, 7.05) * mm, "end": v(-55.78, 7.07) * mm});
            skLineSegment(sketch, "E934", {"start": v(-55.78, 7.07) * mm, "end": v(-55.68, 7.09) * mm});
            skLineSegment(sketch, "E935", {"start": v(-55.68, 7.09) * mm, "end": v(-55.6, 7.1) * mm});
            skLineSegment(sketch, "E936", {"start": v(-55.6, 7.1) * mm, "end": v(-55.44, 7.07) * mm});
            skLineSegment(sketch, "E937", {"start": v(-55.44, 7.07) * mm, "end": v(-55.3, 7.03) * mm});
            skLineSegment(sketch, "E938", {"start": v(-55.3, 7.03) * mm, "end": v(-55.17, 6.95) * mm});
            skLineSegment(sketch, "E939", {"start": v(-55.17, 6.95) * mm, "end": v(-55.06, 6.86) * mm});
            skLineSegment(sketch, "E940", {"start": v(-55.06, 6.86) * mm, "end": v(-54.97, 6.74) * mm});
            skLineSegment(sketch, "E941", {"start": v(-54.97, 6.74) * mm, "end": v(-54.9, 6.61) * mm});
            skLineSegment(sketch, "E942", {"start": v(-54.9, 6.61) * mm, "end": v(-54.86, 6.46) * mm});
            skLineSegment(sketch, "E943", {"start": v(-54.86, 6.46) * mm, "end": v(-54.84, 6.3) * mm});
            skLineSegment(sketch, "E944", {"start": v(-54.84, 6.3) * mm, "end": v(-54.84, 6.2) * mm});
            skLineSegment(sketch, "E945", {"start": v(-54.84, 6.2) * mm, "end": v(-54.86, 6.13) * mm});
            skLineSegment(sketch, "E946", {"start": v(-54.86, 6.13) * mm, "end": v(-54.88, 6.06) * mm});
            skLineSegment(sketch, "E947", {"start": v(-54.88, 6.06) * mm, "end": v(-54.93, 6.01) * mm});
            skLineSegment(sketch, "E948", {"start": v(-54.93, 6.01) * mm, "end": v(-54.99, 5.98) * mm});
            skLineSegment(sketch, "E949", {"start": v(-54.99, 5.98) * mm, "end": v(-55.06, 5.95) * mm});
            skLineSegment(sketch, "E950", {"start": v(-55.06, 5.95) * mm, "end": v(-55.16, 5.94) * mm});
            skLineSegment(sketch, "E951", {"start": v(-55.16, 5.94) * mm, "end": v(-55.28, 5.94) * mm});
            skLineSegment(sketch, "E952", {"start": v(-55.28, 5.94) * mm, "end": v(-55.42, 5.94) * mm});
            skLineSegment(sketch, "E953", {"start": v(-55.42, 5.94) * mm, "end": v(-55.5, 5.96) * mm});
            skLineSegment(sketch, "E954", {"start": v(-55.5, 5.96) * mm, "end": v(-55.58, 6) * mm});
            skLineSegment(sketch, "E955", {"start": v(-55.58, 6) * mm, "end": v(-55.65, 6.07) * mm});
            skLineSegment(sketch, "E956", {"start": v(-62.76, -6.83) * mm, "end": v(-62.76, -6.75) * mm});
            skLineSegment(sketch, "E957", {"start": v(-62.76, -6.75) * mm, "end": v(-62.78, -6.67) * mm});
            skLineSegment(sketch, "E958", {"start": v(-62.78, -6.67) * mm, "end": v(-62.84, -6.49) * mm});
            skLineSegment(sketch, "E959", {"start": v(-62.84, -6.49) * mm, "end": v(-62.93, -6.3) * mm});
            skLineSegment(sketch, "E960", {"start": v(-62.93, -6.3) * mm, "end": v(-63.05, -6.13) * mm});
            skLineSegment(sketch, "E961", {"start": v(-63.05, -6.13) * mm, "end": v(-63.2, -5.95) * mm});
            skLineSegment(sketch, "E962", {"start": v(-63.2, -5.95) * mm, "end": v(-63.27, -5.89) * mm});
            skLineSegment(sketch, "E963", {"start": v(-63.27, -5.89) * mm, "end": v(-63.34, -5.83) * mm});
            skLineSegment(sketch, "E964", {"start": v(-63.34, -5.83) * mm, "end": v(-63.41, -5.8) * mm});
            skLineSegment(sketch, "E965", {"start": v(-63.41, -5.8) * mm, "end": v(-63.48, -5.77) * mm});
            skLineSegment(sketch, "E966", {"start": v(-63.48, -5.77) * mm, "end": v(-63.66, -5.73) * mm});
            skLineSegment(sketch, "E967", {"start": v(-63.66, -5.73) * mm, "end": v(-63.76, -5.71) * mm});
            skLineSegment(sketch, "E968", {"start": v(-63.76, -5.71) * mm, "end": v(-63.84, -5.72) * mm});
            skLineSegment(sketch, "E969", {"start": v(-63.84, -5.72) * mm, "end": v(-63.9, -5.75) * mm});
            skLineSegment(sketch, "E970", {"start": v(-63.9, -5.75) * mm, "end": v(-63.96, -5.8) * mm});
            skLineSegment(sketch, "E971", {"start": v(-63.96, -5.8) * mm, "end": v(-64, -5.84) * mm});
            skLineSegment(sketch, "E972", {"start": v(-64, -5.84) * mm, "end": v(-64.04, -5.89) * mm});
            skLineSegment(sketch, "E973", {"start": v(-64.04, -5.89) * mm, "end": v(-64.06, -5.94) * mm});
            skLineSegment(sketch, "E974", {"start": v(-64.06, -5.94) * mm, "end": v(-64.07, -5.98) * mm});
            skLineSegment(sketch, "E975", {"start": v(-64.07, -5.98) * mm, "end": v(-64.06, -6.02) * mm});
            skLineSegment(sketch, "E976", {"start": v(-64.06, -6.02) * mm, "end": v(-64.04, -6.07) * mm});
            skLineSegment(sketch, "E977", {"start": v(-64.04, -6.07) * mm, "end": v(-63.96, -6.18) * mm});
            skLineSegment(sketch, "E978", {"start": v(-63.96, -6.18) * mm, "end": v(-63.86, -6.28) * mm});
            skLineSegment(sketch, "E979", {"start": v(-63.86, -6.28) * mm, "end": v(-63.8, -6.31) * mm});
            skLineSegment(sketch, "E980", {"start": v(-63.8, -6.31) * mm, "end": v(-63.76, -6.33) * mm});
            skLineSegment(sketch, "E981", {"start": v(-63.76, -6.33) * mm, "end": v(-63.51, -6.4) * mm});
            skLineSegment(sketch, "E982", {"start": v(-63.51, -6.4) * mm, "end": v(-63.3, -6.5) * mm});
            skLineSegment(sketch, "E983", {"start": v(-63.3, -6.5) * mm, "end": v(-63.13, -6.6) * mm});
            skLineSegment(sketch, "E984", {"start": v(-63.13, -6.6) * mm, "end": v(-63.06, -6.65) * mm});
            skLineSegment(sketch, "E985", {"start": v(-63.06, -6.65) * mm, "end": v(-63, -6.71) * mm});
            skLineSegment(sketch, "E986", {"start": v(-63, -6.71) * mm, "end": v(-62.9, -6.83) * mm});
            skLineSegment(sketch, "E987", {"start": v(-62.9, -6.83) * mm, "end": v(-62.82, -6.88) * mm});
            skLineSegment(sketch, "E988", {"start": v(-62.82, -6.88) * mm, "end": v(-62.8, -6.9) * mm});
            skLineSegment(sketch, "E989", {"start": v(-62.8, -6.9) * mm, "end": v(-62.78, -6.88) * mm});
            skLineSegment(sketch, "E990", {"start": v(-62.78, -6.88) * mm, "end": v(-62.76, -6.86) * mm});
            skLineSegment(sketch, "E991", {"start": v(-62.76, -6.86) * mm, "end": v(-62.76, -6.83) * mm});
            skLineSegment(sketch, "E992", {"start": v(-64.24, -1.97) * mm, "end": v(-64.04, -1.6) * mm});
            skLineSegment(sketch, "E993", {"start": v(-64.04, -1.6) * mm, "end": v(-63.76, -1.12) * mm});
            skLineSegment(sketch, "E994", {"start": v(-63.76, -1.12) * mm, "end": v(-63.46, -0.64) * mm});
            skLineSegment(sketch, "E995", {"start": v(-63.46, -0.64) * mm, "end": v(-63.22, -0.28) * mm});
            skLineSegment(sketch, "E996", {"start": v(-63.22, -0.28) * mm, "end": v(-62.95, 0.08) * mm});
            skLineSegment(sketch, "E997", {"start": v(-62.95, 0.08) * mm, "end": v(-62.7, 0.4) * mm});
            skLineSegment(sketch, "E998", {"start": v(-62.7, 0.4) * mm, "end": v(-62.45, 0.7) * mm});
            skLineSegment(sketch, "E999", {"start": v(-62.45, 0.7) * mm, "end": v(-62.22, 0.95) * mm});
            skLineSegment(sketch, "E1000", {"start": v(-62.22, 0.95) * mm, "end": v(-62, 1.18) * mm});
            skLineSegment(sketch, "E1001", {"start": v(-62, 1.18) * mm, "end": v(-61.78, 1.37) * mm});
            skLineSegment(sketch, "E1002", {"start": v(-61.78, 1.37) * mm, "end": v(-61.57, 1.53) * mm});
            skLineSegment(sketch, "E1003", {"start": v(-61.57, 1.53) * mm, "end": v(-61.37, 1.65) * mm});
            skLineSegment(sketch, "E1004", {"start": v(-61.37, 1.65) * mm, "end": v(-61.14, 1.8) * mm});
            skLineSegment(sketch, "E1005", {"start": v(-61.14, 1.8) * mm, "end": v(-61.06, 1.87) * mm});
            skLineSegment(sketch, "E1006", {"start": v(-61.06, 1.87) * mm, "end": v(-61, 1.91) * mm});
            skLineSegment(sketch, "E1007", {"start": v(-61, 1.91) * mm, "end": v(-60.98, 2) * mm});
            skLineSegment(sketch, "E1008", {"start": v(-60.98, 2) * mm, "end": v(-60.96, 2.12) * mm});
            skLineSegment(sketch, "E1009", {"start": v(-60.96, 2.12) * mm, "end": v(-60.95, 2.28) * mm});
            skLineSegment(sketch, "E1010", {"start": v(-60.95, 2.28) * mm, "end": v(-60.95, 2.47) * mm});
            skLineSegment(sketch, "E1011", {"start": v(-60.95, 2.47) * mm, "end": v(-60.95, 2.65) * mm});
            skLineSegment(sketch, "E1012", {"start": v(-60.95, 2.65) * mm, "end": v(-60.97, 2.82) * mm});
            skLineSegment(sketch, "E1013", {"start": v(-60.97, 2.82) * mm, "end": v(-61, 2.96) * mm});
            skLineSegment(sketch, "E1014", {"start": v(-61, 2.96) * mm, "end": v(-61.02, 3.05) * mm});
            skLineSegment(sketch, "E1015", {"start": v(-61.02, 3.05) * mm, "end": v(-61.05, 3.1) * mm});
            skLineSegment(sketch, "E1016", {"start": v(-61.05, 3.1) * mm, "end": v(-61.1, 3.14) * mm});
            skLineSegment(sketch, "E1017", {"start": v(-61.1, 3.14) * mm, "end": v(-61.13, 3.16) * mm});
            skLineSegment(sketch, "E1018", {"start": v(-61.13, 3.16) * mm, "end": v(-61.16, 3.17) * mm});
            skLineSegment(sketch, "E1019", {"start": v(-61.16, 3.17) * mm, "end": v(-61.21, 3.16) * mm});
            skLineSegment(sketch, "E1020", {"start": v(-61.21, 3.16) * mm, "end": v(-61.31, 3.11) * mm});
            skLineSegment(sketch, "E1021", {"start": v(-61.31, 3.11) * mm, "end": v(-61.58, 2.96) * mm});
            skLineSegment(sketch, "E1022", {"start": v(-61.58, 2.96) * mm, "end": v(-61.9, 2.77) * mm});
            skLineSegment(sketch, "E1023", {"start": v(-61.9, 2.77) * mm, "end": v(-62.15, 2.6) * mm});
            skLineSegment(sketch, "E1024", {"start": v(-62.15, 2.6) * mm, "end": v(-62.28, 2.48) * mm});
            skLineSegment(sketch, "E1025", {"start": v(-62.28, 2.48) * mm, "end": v(-62.43, 2.33) * mm});
            skLineSegment(sketch, "E1026", {"start": v(-62.43, 2.33) * mm, "end": v(-62.77, 1.93) * mm});
            skLineSegment(sketch, "E1027", {"start": v(-62.77, 1.93) * mm, "end": v(-63.11, 1.48) * mm});
            skLineSegment(sketch, "E1028", {"start": v(-63.11, 1.48) * mm, "end": v(-63.26, 1.27) * mm});
            skLineSegment(sketch, "E1029", {"start": v(-63.26, 1.27) * mm, "end": v(-63.37, 1.09) * mm});
            skLineSegment(sketch, "E1030", {"start": v(-63.37, 1.09) * mm, "end": v(-63.5, 0.87) * mm});
            skLineSegment(sketch, "E1031", {"start": v(-63.5, 0.87) * mm, "end": v(-63.61, 0.63) * mm});
            skLineSegment(sketch, "E1032", {"start": v(-63.61, 0.63) * mm, "end": v(-63.83, 0.11) * mm});
            skLineSegment(sketch, "E1033", {"start": v(-63.83, 0.11) * mm, "end": v(-64.02, -0.4) * mm});
            skLineSegment(sketch, "E1034", {"start": v(-64.02, -0.4) * mm, "end": v(-64.1, -0.65) * mm});
            skLineSegment(sketch, "E1035", {"start": v(-64.1, -0.65) * mm, "end": v(-64.16, -0.87) * mm});
            skLineSegment(sketch, "E1036", {"start": v(-64.16, -0.87) * mm, "end": v(-64.23, -1.2) * mm});
            skLineSegment(sketch, "E1037", {"start": v(-64.23, -1.2) * mm, "end": v(-64.34, -1.68) * mm});
            skLineSegment(sketch, "E1038", {"start": v(-64.34, -1.68) * mm, "end": v(-64.37, -1.9) * mm});
            skLineSegment(sketch, "E1039", {"start": v(-64.37, -1.9) * mm, "end": v(-64.39, -2.04) * mm});
            skLineSegment(sketch, "E1040", {"start": v(-64.39, -2.04) * mm, "end": v(-64.39, -2.08) * mm});
            skLineSegment(sketch, "E1041", {"start": v(-64.39, -2.08) * mm, "end": v(-64.38, -2.1) * mm});
            skLineSegment(sketch, "E1042", {"start": v(-64.38, -2.1) * mm, "end": v(-64.36, -2.11) * mm});
            skLineSegment(sketch, "E1043", {"start": v(-64.36, -2.11) * mm, "end": v(-64.34, -2.11) * mm});
            skLineSegment(sketch, "E1044", {"start": v(-64.34, -2.11) * mm, "end": v(-64.3, -2.07) * mm});
            skLineSegment(sketch, "E1045", {"start": v(-64.3, -2.07) * mm, "end": v(-64.24, -1.97) * mm});
            skLineSegment(sketch, "E1046", {"start": v(-56.7, 1.98) * mm, "end": v(-56.65, 2.06) * mm});
            skLineSegment(sketch, "E1047", {"start": v(-56.65, 2.06) * mm, "end": v(-56.61, 2.15) * mm});
            skLineSegment(sketch, "E1048", {"start": v(-56.61, 2.15) * mm, "end": v(-56.58, 2.24) * mm});
            skLineSegment(sketch, "E1049", {"start": v(-56.58, 2.24) * mm, "end": v(-56.55, 2.35) * mm});
            skLineSegment(sketch, "E1050", {"start": v(-56.55, 2.35) * mm, "end": v(-56.52, 2.62) * mm});
            skLineSegment(sketch, "E1051", {"start": v(-56.52, 2.62) * mm, "end": v(-56.51, 2.97) * mm});
            skLineSegment(sketch, "E1052", {"start": v(-56.51, 2.97) * mm, "end": v(-56.53, 3.34) * mm});
            skLineSegment(sketch, "E1053", {"start": v(-56.53, 3.34) * mm, "end": v(-56.54, 3.47) * mm});
            skLineSegment(sketch, "E1054", {"start": v(-56.54, 3.47) * mm, "end": v(-56.56, 3.57) * mm});
            skLineSegment(sketch, "E1055", {"start": v(-56.56, 3.57) * mm, "end": v(-56.6, 3.65) * mm});
            skLineSegment(sketch, "E1056", {"start": v(-56.6, 3.65) * mm, "end": v(-56.63, 3.7) * mm});
            skLineSegment(sketch, "E1057", {"start": v(-56.63, 3.7) * mm, "end": v(-56.67, 3.72) * mm});
            skLineSegment(sketch, "E1058", {"start": v(-56.67, 3.72) * mm, "end": v(-56.72, 3.73) * mm});
            skLineSegment(sketch, "E1059", {"start": v(-56.72, 3.73) * mm, "end": v(-56.79, 3.72) * mm});
            skLineSegment(sketch, "E1060", {"start": v(-56.79, 3.72) * mm, "end": v(-56.84, 3.7) * mm});
            skLineSegment(sketch, "E1061", {"start": v(-56.84, 3.7) * mm, "end": v(-56.87, 3.65) * mm});
            skLineSegment(sketch, "E1062", {"start": v(-56.87, 3.65) * mm, "end": v(-56.9, 3.57) * mm});
            skLineSegment(sketch, "E1063", {"start": v(-56.9, 3.57) * mm, "end": v(-56.9, 3.47) * mm});
            skLineSegment(sketch, "E1064", {"start": v(-56.9, 3.47) * mm, "end": v(-56.89, 3.34) * mm});
            skLineSegment(sketch, "E1065", {"start": v(-56.89, 3.34) * mm, "end": v(-56.84, 2.96) * mm});
            skLineSegment(sketch, "E1066", {"start": v(-56.84, 2.96) * mm, "end": v(-56.79, 2.6) * mm});
            skLineSegment(sketch, "E1067", {"start": v(-56.79, 2.6) * mm, "end": v(-56.77, 2.35) * mm});
            skLineSegment(sketch, "E1068", {"start": v(-56.77, 2.35) * mm, "end": v(-56.78, 2.26) * mm});
            skLineSegment(sketch, "E1069", {"start": v(-56.78, 2.26) * mm, "end": v(-56.8, 2.18) * mm});
            skLineSegment(sketch, "E1070", {"start": v(-56.8, 2.18) * mm, "end": v(-56.82, 2.12) * mm});
            skLineSegment(sketch, "E1071", {"start": v(-56.82, 2.12) * mm, "end": v(-56.86, 2.07) * mm});
            skLineSegment(sketch, "E1072", {"start": v(-56.86, 2.07) * mm, "end": v(-56.88, 2.04) * mm});
            skLineSegment(sketch, "E1073", {"start": v(-56.88, 2.04) * mm, "end": v(-56.9, 2) * mm});
            skLineSegment(sketch, "E1074", {"start": v(-56.9, 2) * mm, "end": v(-56.92, 1.93) * mm});
            skLineSegment(sketch, "E1075", {"start": v(-56.92, 1.93) * mm, "end": v(-56.9, 1.87) * mm});
            skLineSegment(sketch, "E1076", {"start": v(-56.9, 1.87) * mm, "end": v(-56.89, 1.85) * mm});
            skLineSegment(sketch, "E1077", {"start": v(-56.89, 1.85) * mm, "end": v(-56.86, 1.84) * mm});
            skLineSegment(sketch, "E1078", {"start": v(-56.86, 1.84) * mm, "end": v(-56.83, 1.85) * mm});
            skLineSegment(sketch, "E1079", {"start": v(-56.83, 1.85) * mm, "end": v(-56.8, 1.88) * mm});
            skLineSegment(sketch, "E1080", {"start": v(-56.8, 1.88) * mm, "end": v(-56.7, 1.98) * mm});
            skLineSegment(sketch, "E1081", {"start": v(-64.27, 7.48) * mm, "end": v(-64.07, 7.5) * mm});
            skLineSegment(sketch, "E1082", {"start": v(-64.07, 7.5) * mm, "end": v(-63.83, 7.53) * mm});
            skLineSegment(sketch, "E1083", {"start": v(-63.83, 7.53) * mm, "end": v(-63.52, 7.54) * mm});
            skLineSegment(sketch, "E1084", {"start": v(-63.52, 7.54) * mm, "end": v(-63.13, 7.55) * mm});
            skLineSegment(sketch, "E1085", {"start": v(-63.13, 7.55) * mm, "end": v(-62.32, 7.54) * mm});
            skLineSegment(sketch, "E1086", {"start": v(-62.32, 7.54) * mm, "end": v(-62.17, 7.71) * mm});
            skLineSegment(sketch, "E1087", {"start": v(-62.17, 7.71) * mm, "end": v(-62.06, 7.84) * mm});
            skLineSegment(sketch, "E1088", {"start": v(-62.06, 7.84) * mm, "end": v(-62.03, 7.89) * mm});
            skLineSegment(sketch, "E1089", {"start": v(-62.03, 7.89) * mm, "end": v(-62.03, 7.92) * mm});
            skLineSegment(sketch, "E1090", {"start": v(-62.03, 7.92) * mm, "end": v(-62.05, 7.93) * mm});
            skLineSegment(sketch, "E1091", {"start": v(-62.05, 7.93) * mm, "end": v(-62.08, 7.94) * mm});
            skLineSegment(sketch, "E1092", {"start": v(-62.08, 7.94) * mm, "end": v(-62.22, 7.95) * mm});
            skLineSegment(sketch, "E1093", {"start": v(-62.22, 7.95) * mm, "end": v(-62.64, 7.96) * mm});
            skLineSegment(sketch, "E1094", {"start": v(-62.64, 7.96) * mm, "end": v(-63.14, 7.94) * mm});
            skLineSegment(sketch, "E1095", {"start": v(-63.14, 7.94) * mm, "end": v(-63.38, 7.92) * mm});
            skLineSegment(sketch, "E1096", {"start": v(-63.38, 7.92) * mm, "end": v(-63.6, 7.9) * mm});
            skLineSegment(sketch, "E1097", {"start": v(-63.6, 7.9) * mm, "end": v(-63.8, 7.85) * mm});
            skLineSegment(sketch, "E1098", {"start": v(-63.8, 7.85) * mm, "end": v(-64.03, 7.8) * mm});
            skLineSegment(sketch, "E1099", {"start": v(-64.03, 7.8) * mm, "end": v(-64.25, 7.73) * mm});
            skLineSegment(sketch, "E1100", {"start": v(-64.25, 7.73) * mm, "end": v(-64.46, 7.66) * mm});
            skLineSegment(sketch, "E1101", {"start": v(-64.46, 7.66) * mm, "end": v(-64.64, 7.59) * mm});
            skLineSegment(sketch, "E1102", {"start": v(-64.64, 7.59) * mm, "end": v(-64.78, 7.52) * mm});
            skLineSegment(sketch, "E1103", {"start": v(-64.78, 7.52) * mm, "end": v(-64.87, 7.45) * mm});
            skLineSegment(sketch, "E1104", {"start": v(-64.87, 7.45) * mm, "end": v(-64.9, 7.42) * mm});
            skLineSegment(sketch, "E1105", {"start": v(-64.9, 7.42) * mm, "end": v(-64.9, 7.4) * mm});
            skLineSegment(sketch, "E1106", {"start": v(-64.9, 7.4) * mm, "end": v(-64.9, 7.38) * mm});
            skLineSegment(sketch, "E1107", {"start": v(-64.9, 7.38) * mm, "end": v(-64.88, 7.37) * mm});
            skLineSegment(sketch, "E1108", {"start": v(-64.88, 7.37) * mm, "end": v(-64.8, 7.37) * mm});
            skLineSegment(sketch, "E1109", {"start": v(-64.8, 7.37) * mm, "end": v(-64.6, 7.4) * mm});
            skLineSegment(sketch, "E1110", {"start": v(-64.6, 7.4) * mm, "end": v(-64.27, 7.48) * mm});
            skSolve(sketch);
        }
        {
            var Q0;
            Q0=makeQuery(id+"F8.imprint","IMPRINT",FACE,{"disambiguationData":[TD([[makeQuery(id+"F8.imprint","IMPRINT",EDGE,{"derivedFrom":sQuery(id+"F8.wireOp",EDGE,"E332")}),1.0]])]});
            var Q1;
            Q1=makeQuery(id+"F8.imprint","IMPRINT",FACE,{"disambiguationData":[TD([[makeQuery(id+"F8.imprint","IMPRINT",EDGE,{"derivedFrom":sQuery(id+"F8.wireOp",EDGE,"E992")}),1.0]])]});
            var Q2;
            Q2=makeQuery(id+"F8.imprint","IMPRINT",FACE,{"disambiguationData":[TD([[makeQuery(id+"F8.imprint","IMPRINT",EDGE,{"derivedFrom":sQuery(id+"F8.wireOp",EDGE,"E14")}),-1.0]])]});
            extrude(context, id + "F9", {"entities" : qUnion([Q0, Q1, Q2]), "operationType" : NewBodyOperationType.ADD, "depth" : 3 * mm, "offsetDistance" : 25 * mm});
        }
        {
            var Q0;
            {var subQ44=sQuery(id+"F0.wireOp",EDGE,"E5");var subQ46=sQuery(id+"F0.wireOp",EDGE,"E1.top");var subQ49=sQuery(id+"F0.wireOp",EDGE,"E3");var subQ55=sQuery(id+"F0.wireOp",EDGE,"E6");var subQ56=sQuery(id+"F0.wireOp",EDGE,"E1.bottom");var subQ63=sQuery(id+"F0.wireOp",EDGE,"E4");var subQ74=makeQuery(id+"F1.opExtrude","SWEPT_FACE",FACE,{"disambiguationData":[OSD([subQ56])]});Q0=makeQuery(id+"F9.boolean.opBoolean","SPLIT",FACE,{"disambiguationData":[TD([subQ74])],"derivedFrom":makeQuery(id+"F5.boolean.opBoolean","SPLIT",FACE,{"disambiguationData":[TD([subQ74])],"derivedFrom":makeQuery(id+"F1.opExtrude","CAP_FACE",FACE,{"disambiguationData":[OSD([subQ56,subQ46,subQ49,subQ63,subQ44,subQ55])],"isStart":false})})});}
            var sketch = newSketch(context, id + "F10", { "sketchPlane" : qUnion([Q0])});
            skLineSegment(sketch, "E1111", {"start": v(54.8, -9.47) * mm, "end": v(54.76, -9.44) * mm});
            skLineSegment(sketch, "E1112", {"start": v(54.76, -9.44) * mm, "end": v(54.71, -9.42) * mm});
            skLineSegment(sketch, "E1113", {"start": v(54.71, -9.42) * mm, "end": v(54.67, -9.4) * mm});
            skLineSegment(sketch, "E1114", {"start": v(54.67, -9.4) * mm, "end": v(54.63, -9.36) * mm});
            skLineSegment(sketch, "E1115", {"start": v(54.63, -9.36) * mm, "end": v(54.59, -9.33) * mm});
            skLineSegment(sketch, "E1116", {"start": v(54.59, -9.33) * mm, "end": v(54.55, -9.3) * mm});
            skLineSegment(sketch, "E1117", {"start": v(54.55, -9.3) * mm, "end": v(54.5, -9.26) * mm});
            skLineSegment(sketch, "E1118", {"start": v(54.5, -9.26) * mm, "end": v(54.47, -9.23) * mm});
            skLineSegment(sketch, "E1119", {"start": v(54.47, -9.23) * mm, "end": v(54.43, -9.2) * mm});
            skLineSegment(sketch, "E1120", {"start": v(54.43, -9.2) * mm, "end": v(54.4, -9.16) * mm});
            skLineSegment(sketch, "E1121", {"start": v(54.4, -9.16) * mm, "end": v(54.37, -9.13) * mm});
            skLineSegment(sketch, "E1122", {"start": v(54.37, -9.13) * mm, "end": v(54.35, -9.1) * mm});
            skLineSegment(sketch, "E1123", {"start": v(54.35, -9.1) * mm, "end": v(54.33, -9.07) * mm});
            skLineSegment(sketch, "E1124", {"start": v(54.33, -9.07) * mm, "end": v(54.31, -9.04) * mm});
            skLineSegment(sketch, "E1125", {"start": v(54.31, -9.04) * mm, "end": v(54.3, -9.02) * mm});
            skLineSegment(sketch, "E1126", {"start": v(54.3, -9.02) * mm, "end": v(54.3, -9) * mm});
            skLineSegment(sketch, "E1127", {"start": v(54.3, -9) * mm, "end": v(54.3, -8.99) * mm});
            skLineSegment(sketch, "E1128", {"start": v(54.3, -8.99) * mm, "end": v(54.3, -8.97) * mm});
            skLineSegment(sketch, "E1129", {"start": v(54.3, -8.97) * mm, "end": v(54.28, -8.96) * mm});
            skLineSegment(sketch, "E1130", {"start": v(54.28, -8.96) * mm, "end": v(54.26, -8.95) * mm});
            skLineSegment(sketch, "E1131", {"start": v(54.26, -8.95) * mm, "end": v(54.24, -8.94) * mm});
            skLineSegment(sketch, "E1132", {"start": v(54.24, -8.94) * mm, "end": v(54.21, -8.92) * mm});
            skLineSegment(sketch, "E1133", {"start": v(54.21, -8.92) * mm, "end": v(54.18, -8.91) * mm});
            skLineSegment(sketch, "E1134", {"start": v(54.18, -8.91) * mm, "end": v(54.15, -8.9) * mm});
            skLineSegment(sketch, "E1135", {"start": v(54.15, -8.9) * mm, "end": v(54.08, -8.88) * mm});
            skLineSegment(sketch, "E1136", {"start": v(54.08, -8.88) * mm, "end": v(54, -8.85) * mm});
            skLineSegment(sketch, "E1137", {"start": v(54, -8.85) * mm, "end": v(53.93, -8.8) * mm});
            skLineSegment(sketch, "E1138", {"start": v(53.93, -8.8) * mm, "end": v(53.85, -8.76) * mm});
            skLineSegment(sketch, "E1139", {"start": v(53.85, -8.76) * mm, "end": v(53.77, -8.7) * mm});
            skLineSegment(sketch, "E1140", {"start": v(53.77, -8.7) * mm, "end": v(53.69, -8.65) * mm});
            skLineSegment(sketch, "E1141", {"start": v(53.69, -8.65) * mm, "end": v(53.6, -8.58) * mm});
            skLineSegment(sketch, "E1142", {"start": v(53.6, -8.58) * mm, "end": v(53.52, -8.52) * mm});
            skLineSegment(sketch, "E1143", {"start": v(53.52, -8.52) * mm, "end": v(53.44, -8.45) * mm});
            skLineSegment(sketch, "E1144", {"start": v(53.44, -8.45) * mm, "end": v(53.36, -8.37) * mm});
            skLineSegment(sketch, "E1145", {"start": v(53.36, -8.37) * mm, "end": v(53.29, -8.3) * mm});
            skLineSegment(sketch, "E1146", {"start": v(53.29, -8.3) * mm, "end": v(53.22, -8.23) * mm});
            skLineSegment(sketch, "E1147", {"start": v(53.22, -8.23) * mm, "end": v(53.16, -8.16) * mm});
            skLineSegment(sketch, "E1148", {"start": v(53.16, -8.16) * mm, "end": v(53.1, -8.09) * mm});
            skLineSegment(sketch, "E1149", {"start": v(53.1, -8.09) * mm, "end": v(53.06, -8.02) * mm});
            skLineSegment(sketch, "E1150", {"start": v(53.06, -8.02) * mm, "end": v(53.03, -7.96) * mm});
            skLineSegment(sketch, "E1151", {"start": v(53.03, -7.96) * mm, "end": v(53, -7.9) * mm});
            skLineSegment(sketch, "E1152", {"start": v(53, -7.9) * mm, "end": v(52.98, -7.84) * mm});
            skLineSegment(sketch, "E1153", {"start": v(52.98, -7.84) * mm, "end": v(52.97, -7.78) * mm});
            skLineSegment(sketch, "E1154", {"start": v(52.97, -7.78) * mm, "end": v(52.95, -7.72) * mm});
            skLineSegment(sketch, "E1155", {"start": v(52.95, -7.72) * mm, "end": v(52.95, -7.66) * mm});
            skLineSegment(sketch, "E1156", {"start": v(52.95, -7.66) * mm, "end": v(52.94, -7.6) * mm});
            skLineSegment(sketch, "E1157", {"start": v(52.94, -7.6) * mm, "end": v(52.94, -7.55) * mm});
            skLineSegment(sketch, "E1158", {"start": v(52.94, -7.55) * mm, "end": v(52.94, -7.5) * mm});
            skLineSegment(sketch, "E1159", {"start": v(52.94, -7.5) * mm, "end": v(52.95, -7.44) * mm});
            skLineSegment(sketch, "E1160", {"start": v(52.95, -7.44) * mm, "end": v(52.96, -7.4) * mm});
            skLineSegment(sketch, "E1161", {"start": v(52.96, -7.4) * mm, "end": v(52.98, -7.35) * mm});
            skLineSegment(sketch, "E1162", {"start": v(52.98, -7.35) * mm, "end": v(53, -7.3) * mm});
            skLineSegment(sketch, "E1163", {"start": v(53, -7.3) * mm, "end": v(53.02, -7.27) * mm});
            skLineSegment(sketch, "E1164", {"start": v(53.02, -7.27) * mm, "end": v(53.04, -7.24) * mm});
            skLineSegment(sketch, "E1165", {"start": v(53.04, -7.24) * mm, "end": v(53.07, -7.22) * mm});
            skLineSegment(sketch, "E1166", {"start": v(53.07, -7.22) * mm, "end": v(53.1, -7.2) * mm});
            skLineSegment(sketch, "E1167", {"start": v(53.1, -7.2) * mm, "end": v(53.12, -7.2) * mm});
            skLineSegment(sketch, "E1168", {"start": v(53.12, -7.2) * mm, "end": v(53.14, -7.19) * mm});
            skLineSegment(sketch, "E1169", {"start": v(53.14, -7.19) * mm, "end": v(53.15, -7.18) * mm});
            skLineSegment(sketch, "E1170", {"start": v(53.15, -7.18) * mm, "end": v(53.17, -7.18) * mm});
            skLineSegment(sketch, "E1171", {"start": v(53.17, -7.18) * mm, "end": v(53.18, -7.18) * mm});
            skLineSegment(sketch, "E1172", {"start": v(53.18, -7.18) * mm, "end": v(53.2, -7.18) * mm});
            skLineSegment(sketch, "E1173", {"start": v(53.2, -7.18) * mm, "end": v(53.22, -7.19) * mm});
            skLineSegment(sketch, "E1174", {"start": v(53.22, -7.19) * mm, "end": v(53.25, -7.2) * mm});
            skLineSegment(sketch, "E1175", {"start": v(53.25, -7.2) * mm, "end": v(53.27, -7.2) * mm});
            skLineSegment(sketch, "E1176", {"start": v(53.27, -7.2) * mm, "end": v(53.3, -7.21) * mm});
            skLineSegment(sketch, "E1177", {"start": v(53.3, -7.21) * mm, "end": v(53.34, -7.23) * mm});
            skLineSegment(sketch, "E1178", {"start": v(53.34, -7.23) * mm, "end": v(53.37, -7.24) * mm});
            skLineSegment(sketch, "E1179", {"start": v(53.37, -7.24) * mm, "end": v(53.42, -7.26) * mm});
            skLineSegment(sketch, "E1180", {"start": v(53.42, -7.26) * mm, "end": v(53.46, -7.28) * mm});
            skLineSegment(sketch, "E1181", {"start": v(53.46, -7.28) * mm, "end": v(53.52, -7.3) * mm});
            skLineSegment(sketch, "E1182", {"start": v(53.52, -7.3) * mm, "end": v(53.58, -7.33) * mm});
            skLineSegment(sketch, "E1183", {"start": v(53.58, -7.33) * mm, "end": v(53.64, -7.37) * mm});
            skLineSegment(sketch, "E1184", {"start": v(53.64, -7.37) * mm, "end": v(53.7, -7.4) * mm});
            skLineSegment(sketch, "E1185", {"start": v(53.7, -7.4) * mm, "end": v(53.75, -7.42) * mm});
            skLineSegment(sketch, "E1186", {"start": v(53.75, -7.42) * mm, "end": v(53.8, -7.44) * mm});
            skLineSegment(sketch, "E1187", {"start": v(53.8, -7.44) * mm, "end": v(53.85, -7.46) * mm});
            skLineSegment(sketch, "E1188", {"start": v(53.85, -7.46) * mm, "end": v(53.89, -7.47) * mm});
            skLineSegment(sketch, "E1189", {"start": v(53.89, -7.47) * mm, "end": v(53.93, -7.48) * mm});
            skLineSegment(sketch, "E1190", {"start": v(53.93, -7.48) * mm, "end": v(53.97, -7.5) * mm});
            skLineSegment(sketch, "E1191", {"start": v(53.97, -7.5) * mm, "end": v(54.02, -7.5) * mm});
            skLineSegment(sketch, "E1192", {"start": v(54.02, -7.5) * mm, "end": v(54.06, -7.51) * mm});
            skLineSegment(sketch, "E1193", {"start": v(54.06, -7.51) * mm, "end": v(54.11, -7.52) * mm});
            skLineSegment(sketch, "E1194", {"start": v(54.11, -7.52) * mm, "end": v(54.17, -7.52) * mm});
            skLineSegment(sketch, "E1195", {"start": v(54.17, -7.52) * mm, "end": v(54.23, -7.53) * mm});
            skLineSegment(sketch, "E1196", {"start": v(54.23, -7.53) * mm, "end": v(54.3, -7.54) * mm});
            skLineSegment(sketch, "E1197", {"start": v(54.3, -7.54) * mm, "end": v(54.39, -7.54) * mm});
            skLineSegment(sketch, "E1198", {"start": v(54.39, -7.54) * mm, "end": v(54.48, -7.55) * mm});
            skLineSegment(sketch, "E1199", {"start": v(54.48, -7.55) * mm, "end": v(54.58, -7.55) * mm});
            skLineSegment(sketch, "E1200", {"start": v(54.58, -7.55) * mm, "end": v(54.67, -7.56) * mm});
            skLineSegment(sketch, "E1201", {"start": v(54.67, -7.56) * mm, "end": v(54.75, -7.56) * mm});
            skLineSegment(sketch, "E1202", {"start": v(54.75, -7.56) * mm, "end": v(54.82, -7.56) * mm});
            skLineSegment(sketch, "E1203", {"start": v(54.82, -7.56) * mm, "end": v(54.88, -7.56) * mm});
            skLineSegment(sketch, "E1204", {"start": v(54.88, -7.56) * mm, "end": v(54.93, -7.56) * mm});
            skLineSegment(sketch, "E1205", {"start": v(54.93, -7.56) * mm, "end": v(54.97, -7.56) * mm});
            skLineSegment(sketch, "E1206", {"start": v(54.97, -7.56) * mm, "end": v(55, -7.55) * mm});
            skLineSegment(sketch, "E1207", {"start": v(55, -7.55) * mm, "end": v(55.04, -7.54) * mm});
            skLineSegment(sketch, "E1208", {"start": v(55.04, -7.54) * mm, "end": v(55.06, -7.52) * mm});
            skLineSegment(sketch, "E1209", {"start": v(55.06, -7.52) * mm, "end": v(55.08, -7.5) * mm});
            skLineSegment(sketch, "E1210", {"start": v(55.08, -7.5) * mm, "end": v(55.1, -7.49) * mm});
            skLineSegment(sketch, "E1211", {"start": v(55.1, -7.49) * mm, "end": v(55.11, -7.46) * mm});
            skLineSegment(sketch, "E1212", {"start": v(55.11, -7.46) * mm, "end": v(55.13, -7.43) * mm});
            skLineSegment(sketch, "E1213", {"start": v(55.13, -7.43) * mm, "end": v(55.14, -7.4) * mm});
            skLineSegment(sketch, "E1214", {"start": v(55.14, -7.4) * mm, "end": v(55.15, -7.36) * mm});
            skLineSegment(sketch, "E1215", {"start": v(55.15, -7.36) * mm, "end": v(55.16, -7.32) * mm});
            skLineSegment(sketch, "E1216", {"start": v(55.16, -7.32) * mm, "end": v(55.18, -7.28) * mm});
            skLineSegment(sketch, "E1217", {"start": v(55.18, -7.28) * mm, "end": v(55.2, -7.23) * mm});
            skLineSegment(sketch, "E1218", {"start": v(55.2, -7.23) * mm, "end": v(55.22, -7.18) * mm});
            skLineSegment(sketch, "E1219", {"start": v(55.22, -7.18) * mm, "end": v(55.24, -7.12) * mm});
            skLineSegment(sketch, "E1220", {"start": v(55.24, -7.12) * mm, "end": v(55.27, -7.06) * mm});
            skLineSegment(sketch, "E1221", {"start": v(55.27, -7.06) * mm, "end": v(55.3, -7) * mm});
            skLineSegment(sketch, "E1222", {"start": v(55.3, -7) * mm, "end": v(55.32, -6.94) * mm});
            skLineSegment(sketch, "E1223", {"start": v(55.32, -6.94) * mm, "end": v(55.33, -6.9) * mm});
            skLineSegment(sketch, "E1224", {"start": v(55.33, -6.9) * mm, "end": v(55.35, -6.87) * mm});
            skLineSegment(sketch, "E1225", {"start": v(55.35, -6.87) * mm, "end": v(55.36, -6.83) * mm});
            skLineSegment(sketch, "E1226", {"start": v(55.36, -6.83) * mm, "end": v(55.38, -6.78) * mm});
            skLineSegment(sketch, "E1227", {"start": v(55.38, -6.78) * mm, "end": v(55.4, -6.73) * mm});
            skLineSegment(sketch, "E1228", {"start": v(55.4, -6.73) * mm, "end": v(55.41, -6.68) * mm});
            skLineSegment(sketch, "E1229", {"start": v(55.41, -6.68) * mm, "end": v(55.43, -6.63) * mm});
            skLineSegment(sketch, "E1230", {"start": v(55.43, -6.63) * mm, "end": v(55.45, -6.57) * mm});
            skLineSegment(sketch, "E1231", {"start": v(55.45, -6.57) * mm, "end": v(55.46, -6.51) * mm});
            skLineSegment(sketch, "E1232", {"start": v(55.46, -6.51) * mm, "end": v(55.48, -6.45) * mm});
            skLineSegment(sketch, "E1233", {"start": v(55.48, -6.45) * mm, "end": v(55.5, -6.4) * mm});
            skLineSegment(sketch, "E1234", {"start": v(55.5, -6.4) * mm, "end": v(55.51, -6.33) * mm});
            skLineSegment(sketch, "E1235", {"start": v(55.51, -6.33) * mm, "end": v(55.53, -6.27) * mm});
            skLineSegment(sketch, "E1236", {"start": v(55.53, -6.27) * mm, "end": v(55.54, -6.2) * mm});
            skLineSegment(sketch, "E1237", {"start": v(55.54, -6.2) * mm, "end": v(55.56, -6.15) * mm});
            skLineSegment(sketch, "E1238", {"start": v(55.56, -6.15) * mm, "end": v(55.57, -6.09) * mm});
            skLineSegment(sketch, "E1239", {"start": v(55.57, -6.09) * mm, "end": v(55.6, -5.97) * mm});
            skLineSegment(sketch, "E1240", {"start": v(55.6, -5.97) * mm, "end": v(55.62, -5.86) * mm});
            skLineSegment(sketch, "E1241", {"start": v(55.62, -5.86) * mm, "end": v(55.65, -5.77) * mm});
            skLineSegment(sketch, "E1242", {"start": v(55.65, -5.77) * mm, "end": v(55.67, -5.69) * mm});
            skLineSegment(sketch, "E1243", {"start": v(55.67, -5.69) * mm, "end": v(55.68, -5.61) * mm});
            skLineSegment(sketch, "E1244", {"start": v(55.68, -5.61) * mm, "end": v(55.7, -5.54) * mm});
            skLineSegment(sketch, "E1245", {"start": v(55.7, -5.54) * mm, "end": v(55.72, -5.48) * mm});
            skLineSegment(sketch, "E1246", {"start": v(55.72, -5.48) * mm, "end": v(55.73, -5.42) * mm});
            skLineSegment(sketch, "E1247", {"start": v(55.73, -5.42) * mm, "end": v(55.75, -5.37) * mm});
            skLineSegment(sketch, "E1248", {"start": v(55.75, -5.37) * mm, "end": v(55.77, -5.31) * mm});
            skLineSegment(sketch, "E1249", {"start": v(55.77, -5.31) * mm, "end": v(55.79, -5.26) * mm});
            skLineSegment(sketch, "E1250", {"start": v(55.79, -5.26) * mm, "end": v(55.8, -5.2) * mm});
            skLineSegment(sketch, "E1251", {"start": v(55.8, -5.2) * mm, "end": v(55.83, -5.15) * mm});
            skLineSegment(sketch, "E1252", {"start": v(55.83, -5.15) * mm, "end": v(55.86, -5.09) * mm});
            skLineSegment(sketch, "E1253", {"start": v(55.86, -5.09) * mm, "end": v(55.88, -5.02) * mm});
            skLineSegment(sketch, "E1254", {"start": v(55.88, -5.02) * mm, "end": v(55.91, -4.95) * mm});
            skLineSegment(sketch, "E1255", {"start": v(55.91, -4.95) * mm, "end": v(55.93, -4.9) * mm});
            skLineSegment(sketch, "E1256", {"start": v(55.93, -4.9) * mm, "end": v(55.95, -4.85) * mm});
            skLineSegment(sketch, "E1257", {"start": v(55.95, -4.85) * mm, "end": v(55.97, -4.8) * mm});
            skLineSegment(sketch, "E1258", {"start": v(55.97, -4.8) * mm, "end": v(55.99, -4.76) * mm});
            skLineSegment(sketch, "E1259", {"start": v(55.99, -4.76) * mm, "end": v(56, -4.72) * mm});
            skLineSegment(sketch, "E1260", {"start": v(56, -4.72) * mm, "end": v(56, -4.68) * mm});
            skLineSegment(sketch, "E1261", {"start": v(56, -4.68) * mm, "end": v(56.02, -4.64) * mm});
            skLineSegment(sketch, "E1262", {"start": v(56.02, -4.64) * mm, "end": v(56.03, -4.6) * mm});
            skLineSegment(sketch, "E1263", {"start": v(56.03, -4.6) * mm, "end": v(56.03, -4.56) * mm});
            skLineSegment(sketch, "E1264", {"start": v(56.03, -4.56) * mm, "end": v(56.04, -4.51) * mm});
            skLineSegment(sketch, "E1265", {"start": v(56.04, -4.51) * mm, "end": v(56.05, -4.46) * mm});
            skLineSegment(sketch, "E1266", {"start": v(56.05, -4.46) * mm, "end": v(56.05, -4.4) * mm});
            skLineSegment(sketch, "E1267", {"start": v(56.05, -4.4) * mm, "end": v(56.05, -4.34) * mm});
            skLineSegment(sketch, "E1268", {"start": v(56.05, -4.34) * mm, "end": v(56.06, -4.27) * mm});
            skLineSegment(sketch, "E1269", {"start": v(56.06, -4.27) * mm, "end": v(56.06, -4.2) * mm});
            skLineSegment(sketch, "E1270", {"start": v(56.06, -4.2) * mm, "end": v(56.06, -4.1) * mm});
            skLineSegment(sketch, "E1271", {"start": v(56.06, -4.1) * mm, "end": v(56.09, -3.59) * mm});
            skLineSegment(sketch, "E1272", {"start": v(56.09, -3.59) * mm, "end": v(56.3, -3.28) * mm});
            skLineSegment(sketch, "E1273", {"start": v(56.3, -3.28) * mm, "end": v(56.34, -3.2) * mm});
            skLineSegment(sketch, "E1274", {"start": v(56.34, -3.2) * mm, "end": v(56.4, -3.12) * mm});
            skLineSegment(sketch, "E1275", {"start": v(56.4, -3.12) * mm, "end": v(56.45, -3.03) * mm});
            skLineSegment(sketch, "E1276", {"start": v(56.45, -3.03) * mm, "end": v(56.5, -2.93) * mm});
            skLineSegment(sketch, "E1277", {"start": v(56.5, -2.93) * mm, "end": v(56.56, -2.82) * mm});
            skLineSegment(sketch, "E1278", {"start": v(56.56, -2.82) * mm, "end": v(56.62, -2.72) * mm});
            skLineSegment(sketch, "E1279", {"start": v(56.62, -2.72) * mm, "end": v(56.67, -2.62) * mm});
            skLineSegment(sketch, "E1280", {"start": v(56.67, -2.62) * mm, "end": v(56.71, -2.52) * mm});
            skLineSegment(sketch, "E1281", {"start": v(56.71, -2.52) * mm, "end": v(56.81, -2.31) * mm});
            skLineSegment(sketch, "E1282", {"start": v(56.81, -2.31) * mm, "end": v(56.9, -2.12) * mm});
            skLineSegment(sketch, "E1283", {"start": v(56.9, -2.12) * mm, "end": v(57, -1.93) * mm});
            skLineSegment(sketch, "E1284", {"start": v(57, -1.93) * mm, "end": v(57.08, -1.76) * mm});
            skLineSegment(sketch, "E1285", {"start": v(57.08, -1.76) * mm, "end": v(57.15, -1.6) * mm});
            skLineSegment(sketch, "E1286", {"start": v(57.15, -1.6) * mm, "end": v(57.23, -1.46) * mm});
            skLineSegment(sketch, "E1287", {"start": v(57.23, -1.46) * mm, "end": v(57.3, -1.32) * mm});
            skLineSegment(sketch, "E1288", {"start": v(57.3, -1.32) * mm, "end": v(57.36, -1.2) * mm});
            skLineSegment(sketch, "E1289", {"start": v(57.36, -1.2) * mm, "end": v(57.42, -1.09) * mm});
            skLineSegment(sketch, "E1290", {"start": v(57.42, -1.09) * mm, "end": v(57.47, -0.99) * mm});
            skLineSegment(sketch, "E1291", {"start": v(57.47, -0.99) * mm, "end": v(57.52, -0.9) * mm});
            skLineSegment(sketch, "E1292", {"start": v(57.52, -0.9) * mm, "end": v(57.57, -0.8) * mm});
            skLineSegment(sketch, "E1293", {"start": v(57.57, -0.8) * mm, "end": v(57.62, -0.74) * mm});
            skLineSegment(sketch, "E1294", {"start": v(57.62, -0.74) * mm, "end": v(57.66, -0.67) * mm});
            skLineSegment(sketch, "E1295", {"start": v(57.66, -0.67) * mm, "end": v(57.7, -0.61) * mm});
            skLineSegment(sketch, "E1296", {"start": v(57.7, -0.61) * mm, "end": v(57.74, -0.56) * mm});
            skLineSegment(sketch, "E1297", {"start": v(57.74, -0.56) * mm, "end": v(57.8, -0.49) * mm});
            skLineSegment(sketch, "E1298", {"start": v(57.8, -0.49) * mm, "end": v(57.85, -0.42) * mm});
            skLineSegment(sketch, "E1299", {"start": v(57.85, -0.42) * mm, "end": v(57.9, -0.36) * mm});
            skLineSegment(sketch, "E1300", {"start": v(57.9, -0.36) * mm, "end": v(57.94, -0.3) * mm});
            skLineSegment(sketch, "E1301", {"start": v(57.94, -0.3) * mm, "end": v(57.98, -0.24) * mm});
            skLineSegment(sketch, "E1302", {"start": v(57.98, -0.24) * mm, "end": v(58.01, -0.2) * mm});
            skLineSegment(sketch, "E1303", {"start": v(58.01, -0.2) * mm, "end": v(58.04, -0.15) * mm});
            skLineSegment(sketch, "E1304", {"start": v(58.04, -0.15) * mm, "end": v(58.07, -0.1) * mm});
            skLineSegment(sketch, "E1305", {"start": v(58.07, -0.1) * mm, "end": v(58.1, -0.07) * mm});
            skLineSegment(sketch, "E1306", {"start": v(58.1, -0.07) * mm, "end": v(58.11, -0.03) * mm});
            skLineSegment(sketch, "E1307", {"start": v(58.11, -0.03) * mm, "end": v(58.13, 0) * mm});
            skLineSegment(sketch, "E1308", {"start": v(58.13, 0) * mm, "end": v(58.14, 0.03) * mm});
            skLineSegment(sketch, "E1309", {"start": v(58.14, 0.03) * mm, "end": v(58.15, 0.06) * mm});
            skLineSegment(sketch, "E1310", {"start": v(58.15, 0.06) * mm, "end": v(58.16, 0.08) * mm});
            skLineSegment(sketch, "E1311", {"start": v(58.16, 0.08) * mm, "end": v(58.16, 0.1) * mm});
            skLineSegment(sketch, "E1312", {"start": v(58.16, 0.1) * mm, "end": v(58.16, 0.13) * mm});
            skLineSegment(sketch, "E1313", {"start": v(58.16, 0.13) * mm, "end": v(58.16, 0.16) * mm});
            skLineSegment(sketch, "E1314", {"start": v(58.16, 0.16) * mm, "end": v(58.15, 0.2) * mm});
            skLineSegment(sketch, "E1315", {"start": v(58.15, 0.2) * mm, "end": v(58.14, 0.24) * mm});
            skLineSegment(sketch, "E1316", {"start": v(58.14, 0.24) * mm, "end": v(58.13, 0.3) * mm});
            skLineSegment(sketch, "E1317", {"start": v(58.13, 0.3) * mm, "end": v(58.1, 0.35) * mm});
            skLineSegment(sketch, "E1318", {"start": v(58.1, 0.35) * mm, "end": v(58.09, 0.41) * mm});
            skLineSegment(sketch, "E1319", {"start": v(58.09, 0.41) * mm, "end": v(58.07, 0.48) * mm});
            skLineSegment(sketch, "E1320", {"start": v(58.07, 0.48) * mm, "end": v(58.04, 0.54) * mm});
            skLineSegment(sketch, "E1321", {"start": v(58.04, 0.54) * mm, "end": v(58.01, 0.62) * mm});
            skLineSegment(sketch, "E1322", {"start": v(58.01, 0.62) * mm, "end": v(57.98, 0.69) * mm});
            skLineSegment(sketch, "E1323", {"start": v(57.98, 0.69) * mm, "end": v(57.96, 0.75) * mm});
            skLineSegment(sketch, "E1324", {"start": v(57.96, 0.75) * mm, "end": v(57.94, 0.82) * mm});
            skLineSegment(sketch, "E1325", {"start": v(57.94, 0.82) * mm, "end": v(57.92, 0.88) * mm});
            skLineSegment(sketch, "E1326", {"start": v(57.92, 0.88) * mm, "end": v(57.9, 0.94) * mm});
            skLineSegment(sketch, "E1327", {"start": v(57.9, 0.94) * mm, "end": v(57.88, 1) * mm});
            skLineSegment(sketch, "E1328", {"start": v(57.88, 1) * mm, "end": v(57.87, 1.07) * mm});
            skLineSegment(sketch, "E1329", {"start": v(57.87, 1.07) * mm, "end": v(57.86, 1.13) * mm});
            skLineSegment(sketch, "E1330", {"start": v(57.86, 1.13) * mm, "end": v(57.84, 1.2) * mm});
            skLineSegment(sketch, "E1331", {"start": v(57.84, 1.2) * mm, "end": v(57.83, 1.27) * mm});
            skLineSegment(sketch, "E1332", {"start": v(57.83, 1.27) * mm, "end": v(57.83, 1.34) * mm});
            skLineSegment(sketch, "E1333", {"start": v(57.83, 1.34) * mm, "end": v(57.82, 1.42) * mm});
            skLineSegment(sketch, "E1334", {"start": v(57.82, 1.42) * mm, "end": v(57.8, 1.51) * mm});
            skLineSegment(sketch, "E1335", {"start": v(57.8, 1.51) * mm, "end": v(57.8, 1.6) * mm});
            skLineSegment(sketch, "E1336", {"start": v(57.8, 1.6) * mm, "end": v(57.8, 1.7) * mm});
            skLineSegment(sketch, "E1337", {"start": v(57.8, 1.7) * mm, "end": v(57.79, 1.82) * mm});
            skLineSegment(sketch, "E1338", {"start": v(57.79, 1.82) * mm, "end": v(57.78, 1.93) * mm});
            skLineSegment(sketch, "E1339", {"start": v(57.78, 1.93) * mm, "end": v(57.76, 2.05) * mm});
            skLineSegment(sketch, "E1340", {"start": v(57.76, 2.05) * mm, "end": v(57.75, 2.16) * mm});
            skLineSegment(sketch, "E1341", {"start": v(57.75, 2.16) * mm, "end": v(57.74, 2.27) * mm});
            skLineSegment(sketch, "E1342", {"start": v(57.74, 2.27) * mm, "end": v(57.72, 2.38) * mm});
            skLineSegment(sketch, "E1343", {"start": v(57.72, 2.38) * mm, "end": v(57.7, 2.47) * mm});
            skLineSegment(sketch, "E1344", {"start": v(57.7, 2.47) * mm, "end": v(57.69, 2.54) * mm});
            skLineSegment(sketch, "E1345", {"start": v(57.69, 2.54) * mm, "end": v(57.67, 2.62) * mm});
            skLineSegment(sketch, "E1346", {"start": v(57.67, 2.62) * mm, "end": v(57.66, 2.7) * mm});
            skLineSegment(sketch, "E1347", {"start": v(57.66, 2.7) * mm, "end": v(57.64, 2.78) * mm});
            skLineSegment(sketch, "E1348", {"start": v(57.64, 2.78) * mm, "end": v(57.62, 2.87) * mm});
            skLineSegment(sketch, "E1349", {"start": v(57.62, 2.87) * mm, "end": v(57.6, 2.96) * mm});
            skLineSegment(sketch, "E1350", {"start": v(57.6, 2.96) * mm, "end": v(57.59, 3.04) * mm});
            skLineSegment(sketch, "E1351", {"start": v(57.59, 3.04) * mm, "end": v(57.57, 3.12) * mm});
            skLineSegment(sketch, "E1352", {"start": v(57.57, 3.12) * mm, "end": v(57.56, 3.2) * mm});
            skLineSegment(sketch, "E1353", {"start": v(57.56, 3.2) * mm, "end": v(57.53, 3.3) * mm});
            skLineSegment(sketch, "E1354", {"start": v(57.53, 3.3) * mm, "end": v(57.51, 3.4) * mm});
            skLineSegment(sketch, "E1355", {"start": v(57.51, 3.4) * mm, "end": v(57.48, 3.48) * mm});
            skLineSegment(sketch, "E1356", {"start": v(57.48, 3.48) * mm, "end": v(57.46, 3.54) * mm});
            skLineSegment(sketch, "E1357", {"start": v(57.46, 3.54) * mm, "end": v(57.43, 3.57) * mm});
            skLineSegment(sketch, "E1358", {"start": v(57.43, 3.57) * mm, "end": v(57.4, 3.59) * mm});
            skLineSegment(sketch, "E1359", {"start": v(57.4, 3.59) * mm, "end": v(57.37, 3.59) * mm});
            skLineSegment(sketch, "E1360", {"start": v(57.37, 3.59) * mm, "end": v(57.34, 3.56) * mm});
            skLineSegment(sketch, "E1361", {"start": v(57.34, 3.56) * mm, "end": v(57.33, 3.55) * mm});
            skLineSegment(sketch, "E1362", {"start": v(57.33, 3.55) * mm, "end": v(57.32, 3.53) * mm});
            skLineSegment(sketch, "E1363", {"start": v(57.32, 3.53) * mm, "end": v(57.3, 3.5) * mm});
            skLineSegment(sketch, "E1364", {"start": v(57.3, 3.5) * mm, "end": v(57.29, 3.47) * mm});
            skLineSegment(sketch, "E1365", {"start": v(57.29, 3.47) * mm, "end": v(57.27, 3.44) * mm});
            skLineSegment(sketch, "E1366", {"start": v(57.27, 3.44) * mm, "end": v(57.26, 3.4) * mm});
            skLineSegment(sketch, "E1367", {"start": v(57.26, 3.4) * mm, "end": v(57.24, 3.37) * mm});
            skLineSegment(sketch, "E1368", {"start": v(57.24, 3.37) * mm, "end": v(57.23, 3.33) * mm});
            skLineSegment(sketch, "E1369", {"start": v(57.23, 3.33) * mm, "end": v(57.21, 3.28) * mm});
            skLineSegment(sketch, "E1370", {"start": v(57.21, 3.28) * mm, "end": v(57.19, 3.23) * mm});
            skLineSegment(sketch, "E1371", {"start": v(57.19, 3.23) * mm, "end": v(57.16, 3.18) * mm});
            skLineSegment(sketch, "E1372", {"start": v(57.16, 3.18) * mm, "end": v(57.14, 3.13) * mm});
            skLineSegment(sketch, "E1373", {"start": v(57.14, 3.13) * mm, "end": v(57.1, 3.08) * mm});
            skLineSegment(sketch, "E1374", {"start": v(57.1, 3.08) * mm, "end": v(57.08, 3.02) * mm});
            skLineSegment(sketch, "E1375", {"start": v(57.08, 3.02) * mm, "end": v(57.04, 2.97) * mm});
            skLineSegment(sketch, "E1376", {"start": v(57.04, 2.97) * mm, "end": v(57.01, 2.92) * mm});
            skLineSegment(sketch, "E1377", {"start": v(57.01, 2.92) * mm, "end": v(56.98, 2.88) * mm});
            skLineSegment(sketch, "E1378", {"start": v(56.98, 2.88) * mm, "end": v(56.95, 2.83) * mm});
            skLineSegment(sketch, "E1379", {"start": v(56.95, 2.83) * mm, "end": v(56.91, 2.8) * mm});
            skLineSegment(sketch, "E1380", {"start": v(56.91, 2.8) * mm, "end": v(56.88, 2.75) * mm});
            skLineSegment(sketch, "E1381", {"start": v(56.88, 2.75) * mm, "end": v(56.85, 2.72) * mm});
            skLineSegment(sketch, "E1382", {"start": v(56.85, 2.72) * mm, "end": v(56.82, 2.7) * mm});
            skLineSegment(sketch, "E1383", {"start": v(56.82, 2.7) * mm, "end": v(56.8, 2.67) * mm});
            skLineSegment(sketch, "E1384", {"start": v(56.8, 2.67) * mm, "end": v(56.77, 2.66) * mm});
            skLineSegment(sketch, "E1385", {"start": v(56.77, 2.66) * mm, "end": v(56.75, 2.65) * mm});
            skLineSegment(sketch, "E1386", {"start": v(56.75, 2.65) * mm, "end": v(56.72, 2.64) * mm});
            skLineSegment(sketch, "E1387", {"start": v(56.72, 2.64) * mm, "end": v(56.68, 2.63) * mm});
            skLineSegment(sketch, "E1388", {"start": v(56.68, 2.63) * mm, "end": v(56.65, 2.62) * mm});
            skLineSegment(sketch, "E1389", {"start": v(56.65, 2.62) * mm, "end": v(56.61, 2.6) * mm});
            skLineSegment(sketch, "E1390", {"start": v(56.61, 2.6) * mm, "end": v(56.58, 2.6) * mm});
            skLineSegment(sketch, "E1391", {"start": v(56.58, 2.6) * mm, "end": v(56.54, 2.6) * mm});
            skLineSegment(sketch, "E1392", {"start": v(56.54, 2.6) * mm, "end": v(56.5, 2.6) * mm});
            skLineSegment(sketch, "E1393", {"start": v(56.5, 2.6) * mm, "end": v(56.48, 2.6) * mm});
            skLineSegment(sketch, "E1394", {"start": v(56.48, 2.6) * mm, "end": v(56.46, 2.6) * mm});
            skLineSegment(sketch, "E1395", {"start": v(56.46, 2.6) * mm, "end": v(56.44, 2.6) * mm});
            skLineSegment(sketch, "E1396", {"start": v(56.44, 2.6) * mm, "end": v(56.42, 2.6) * mm});
            skLineSegment(sketch, "E1397", {"start": v(56.42, 2.6) * mm, "end": v(56.4, 2.61) * mm});
            skLineSegment(sketch, "E1398", {"start": v(56.4, 2.61) * mm, "end": v(56.38, 2.62) * mm});
            skLineSegment(sketch, "E1399", {"start": v(56.38, 2.62) * mm, "end": v(56.36, 2.63) * mm});
            skLineSegment(sketch, "E1400", {"start": v(56.36, 2.63) * mm, "end": v(56.34, 2.64) * mm});
            skLineSegment(sketch, "E1401", {"start": v(56.34, 2.64) * mm, "end": v(56.32, 2.65) * mm});
            skLineSegment(sketch, "E1402", {"start": v(56.32, 2.65) * mm, "end": v(56.3, 2.67) * mm});
            skLineSegment(sketch, "E1403", {"start": v(56.3, 2.67) * mm, "end": v(56.27, 2.69) * mm});
            skLineSegment(sketch, "E1404", {"start": v(56.27, 2.69) * mm, "end": v(56.24, 2.7) * mm});
            skLineSegment(sketch, "E1405", {"start": v(56.24, 2.7) * mm, "end": v(56.2, 2.73) * mm});
            skLineSegment(sketch, "E1406", {"start": v(56.2, 2.73) * mm, "end": v(56.18, 2.76) * mm});
            skLineSegment(sketch, "E1407", {"start": v(56.18, 2.76) * mm, "end": v(56.14, 2.8) * mm});
            skLineSegment(sketch, "E1408", {"start": v(56.14, 2.8) * mm, "end": v(56.1, 2.83) * mm});
            skLineSegment(sketch, "E1409", {"start": v(56.1, 2.83) * mm, "end": v(56.05, 2.88) * mm});
            skLineSegment(sketch, "E1410", {"start": v(56.05, 2.88) * mm, "end": v(56, 2.93) * mm});
            skLineSegment(sketch, "E1411", {"start": v(56, 2.93) * mm, "end": v(55.94, 2.99) * mm});
            skLineSegment(sketch, "E1412", {"start": v(55.94, 2.99) * mm, "end": v(55.89, 3.04) * mm});
            skLineSegment(sketch, "E1413", {"start": v(55.89, 3.04) * mm, "end": v(55.84, 3.1) * mm});
            skLineSegment(sketch, "E1414", {"start": v(55.84, 3.1) * mm, "end": v(55.8, 3.15) * mm});
            skLineSegment(sketch, "E1415", {"start": v(55.8, 3.15) * mm, "end": v(55.77, 3.2) * mm});
            skLineSegment(sketch, "E1416", {"start": v(55.77, 3.2) * mm, "end": v(55.75, 3.23) * mm});
            skLineSegment(sketch, "E1417", {"start": v(55.75, 3.23) * mm, "end": v(55.72, 3.27) * mm});
            skLineSegment(sketch, "E1418", {"start": v(55.72, 3.27) * mm, "end": v(55.7, 3.3) * mm});
            skLineSegment(sketch, "E1419", {"start": v(55.7, 3.3) * mm, "end": v(55.67, 3.35) * mm});
            skLineSegment(sketch, "E1420", {"start": v(55.67, 3.35) * mm, "end": v(55.64, 3.39) * mm});
            skLineSegment(sketch, "E1421", {"start": v(55.64, 3.39) * mm, "end": v(55.62, 3.43) * mm});
            skLineSegment(sketch, "E1422", {"start": v(55.62, 3.43) * mm, "end": v(55.58, 3.47) * mm});
            skLineSegment(sketch, "E1423", {"start": v(55.58, 3.47) * mm, "end": v(55.55, 3.52) * mm});
            skLineSegment(sketch, "E1424", {"start": v(55.55, 3.52) * mm, "end": v(55.52, 3.56) * mm});
            skLineSegment(sketch, "E1425", {"start": v(55.52, 3.56) * mm, "end": v(55.48, 3.61) * mm});
            skLineSegment(sketch, "E1426", {"start": v(55.48, 3.61) * mm, "end": v(55.44, 3.66) * mm});
            skLineSegment(sketch, "E1427", {"start": v(55.44, 3.66) * mm, "end": v(55.4, 3.71) * mm});
            skLineSegment(sketch, "E1428", {"start": v(55.4, 3.71) * mm, "end": v(55.35, 3.76) * mm});
            skLineSegment(sketch, "E1429", {"start": v(55.35, 3.76) * mm, "end": v(55.3, 3.82) * mm});
            skLineSegment(sketch, "E1430", {"start": v(55.3, 3.82) * mm, "end": v(55.24, 3.88) * mm});
            skLineSegment(sketch, "E1431", {"start": v(55.24, 3.88) * mm, "end": v(55.19, 3.94) * mm});
            skLineSegment(sketch, "E1432", {"start": v(55.19, 3.94) * mm, "end": v(55.13, 4) * mm});
            skLineSegment(sketch, "E1433", {"start": v(55.13, 4) * mm, "end": v(55.03, 4.12) * mm});
            skLineSegment(sketch, "E1434", {"start": v(55.03, 4.12) * mm, "end": v(54.94, 4.23) * mm});
            skLineSegment(sketch, "E1435", {"start": v(54.94, 4.23) * mm, "end": v(54.86, 4.33) * mm});
            skLineSegment(sketch, "E1436", {"start": v(54.86, 4.33) * mm, "end": v(54.8, 4.43) * mm});
            skLineSegment(sketch, "E1437", {"start": v(54.8, 4.43) * mm, "end": v(54.74, 4.51) * mm});
            skLineSegment(sketch, "E1438", {"start": v(54.74, 4.51) * mm, "end": v(54.7, 4.6) * mm});
            skLineSegment(sketch, "E1439", {"start": v(54.7, 4.6) * mm, "end": v(54.68, 4.67) * mm});
            skLineSegment(sketch, "E1440", {"start": v(54.68, 4.67) * mm, "end": v(54.67, 4.74) * mm});
            skLineSegment(sketch, "E1441", {"start": v(54.67, 4.74) * mm, "end": v(54.68, 4.8) * mm});
            skLineSegment(sketch, "E1442", {"start": v(54.68, 4.8) * mm, "end": v(54.7, 4.87) * mm});
            skLineSegment(sketch, "E1443", {"start": v(54.7, 4.87) * mm, "end": v(54.72, 4.92) * mm});
            skLineSegment(sketch, "E1444", {"start": v(54.72, 4.92) * mm, "end": v(54.77, 4.97) * mm});
            skLineSegment(sketch, "E1445", {"start": v(54.77, 4.97) * mm, "end": v(54.82, 5.02) * mm});
            skLineSegment(sketch, "E1446", {"start": v(54.82, 5.02) * mm, "end": v(54.9, 5.06) * mm});
            skLineSegment(sketch, "E1447", {"start": v(54.9, 5.06) * mm, "end": v(54.98, 5.1) * mm});
            skLineSegment(sketch, "E1448", {"start": v(54.98, 5.1) * mm, "end": v(55.07, 5.13) * mm});
            skLineSegment(sketch, "E1449", {"start": v(55.07, 5.13) * mm, "end": v(55.13, 5.14) * mm});
            skLineSegment(sketch, "E1450", {"start": v(55.13, 5.14) * mm, "end": v(55.19, 5.15) * mm});
            skLineSegment(sketch, "E1451", {"start": v(55.19, 5.15) * mm, "end": v(55.25, 5.16) * mm});
            skLineSegment(sketch, "E1452", {"start": v(55.25, 5.16) * mm, "end": v(55.3, 5.16) * mm});
            skLineSegment(sketch, "E1453", {"start": v(55.3, 5.16) * mm, "end": v(55.35, 5.15) * mm});
            skLineSegment(sketch, "E1454", {"start": v(55.35, 5.15) * mm, "end": v(55.4, 5.14) * mm});
            skLineSegment(sketch, "E1455", {"start": v(55.4, 5.14) * mm, "end": v(55.44, 5.12) * mm});
            skLineSegment(sketch, "E1456", {"start": v(55.44, 5.12) * mm, "end": v(55.47, 5.1) * mm});
            skLineSegment(sketch, "E1457", {"start": v(55.47, 5.1) * mm, "end": v(55.5, 5.08) * mm});
            skLineSegment(sketch, "E1458", {"start": v(55.5, 5.08) * mm, "end": v(55.53, 5.05) * mm});
            skLineSegment(sketch, "E1459", {"start": v(55.53, 5.05) * mm, "end": v(55.56, 5.02) * mm});
            skLineSegment(sketch, "E1460", {"start": v(55.56, 5.02) * mm, "end": v(55.57, 5) * mm});
            skLineSegment(sketch, "E1461", {"start": v(55.57, 5) * mm, "end": v(55.58, 4.96) * mm});
            skLineSegment(sketch, "E1462", {"start": v(55.58, 4.96) * mm, "end": v(55.58, 4.92) * mm});
            skLineSegment(sketch, "E1463", {"start": v(55.58, 4.92) * mm, "end": v(55.57, 4.88) * mm});
            skLineSegment(sketch, "E1464", {"start": v(55.57, 4.88) * mm, "end": v(55.56, 4.84) * mm});
            skLineSegment(sketch, "E1465", {"start": v(55.56, 4.84) * mm, "end": v(55.55, 4.8) * mm});
            skLineSegment(sketch, "E1466", {"start": v(55.55, 4.8) * mm, "end": v(55.54, 4.77) * mm});
            skLineSegment(sketch, "E1467", {"start": v(55.54, 4.77) * mm, "end": v(55.53, 4.73) * mm});
            skLineSegment(sketch, "E1468", {"start": v(55.53, 4.73) * mm, "end": v(55.52, 4.7) * mm});
            skLineSegment(sketch, "E1469", {"start": v(55.52, 4.7) * mm, "end": v(55.52, 4.65) * mm});
            skLineSegment(sketch, "E1470", {"start": v(55.52, 4.65) * mm, "end": v(55.52, 4.6) * mm});
            skLineSegment(sketch, "E1471", {"start": v(55.52, 4.6) * mm, "end": v(55.52, 4.56) * mm});
            skLineSegment(sketch, "E1472", {"start": v(55.52, 4.56) * mm, "end": v(55.52, 4.5) * mm});
            skLineSegment(sketch, "E1473", {"start": v(55.52, 4.5) * mm, "end": v(55.52, 4.46) * mm});
            skLineSegment(sketch, "E1474", {"start": v(55.52, 4.46) * mm, "end": v(55.52, 4.42) * mm});
            skLineSegment(sketch, "E1475", {"start": v(55.52, 4.42) * mm, "end": v(55.53, 4.37) * mm});
            skLineSegment(sketch, "E1476", {"start": v(55.53, 4.37) * mm, "end": v(55.53, 4.33) * mm});
            skLineSegment(sketch, "E1477", {"start": v(55.53, 4.33) * mm, "end": v(55.54, 4.3) * mm});
            skLineSegment(sketch, "E1478", {"start": v(55.54, 4.3) * mm, "end": v(55.55, 4.26) * mm});
            skLineSegment(sketch, "E1479", {"start": v(55.55, 4.26) * mm, "end": v(55.56, 4.23) * mm});
            skLineSegment(sketch, "E1480", {"start": v(55.56, 4.23) * mm, "end": v(55.58, 4.2) * mm});
            skLineSegment(sketch, "E1481", {"start": v(55.58, 4.2) * mm, "end": v(55.59, 4.19) * mm});
            skLineSegment(sketch, "E1482", {"start": v(55.59, 4.19) * mm, "end": v(55.6, 4.17) * mm});
            skLineSegment(sketch, "E1483", {"start": v(55.6, 4.17) * mm, "end": v(55.63, 4.14) * mm});
            skLineSegment(sketch, "E1484", {"start": v(55.63, 4.14) * mm, "end": v(55.65, 4.12) * mm});
            skLineSegment(sketch, "E1485", {"start": v(55.65, 4.12) * mm, "end": v(55.68, 4.1) * mm});
            skLineSegment(sketch, "E1486", {"start": v(55.68, 4.1) * mm, "end": v(55.7, 4.08) * mm});
            skLineSegment(sketch, "E1487", {"start": v(55.7, 4.08) * mm, "end": v(55.74, 4.06) * mm});
            skLineSegment(sketch, "E1488", {"start": v(55.74, 4.06) * mm, "end": v(55.76, 4.04) * mm});
            skLineSegment(sketch, "E1489", {"start": v(55.76, 4.04) * mm, "end": v(55.8, 4.02) * mm});
            skLineSegment(sketch, "E1490", {"start": v(55.8, 4.02) * mm, "end": v(55.83, 4) * mm});
            skLineSegment(sketch, "E1491", {"start": v(55.83, 4) * mm, "end": v(55.86, 3.97) * mm});
            skLineSegment(sketch, "E1492", {"start": v(55.86, 3.97) * mm, "end": v(55.9, 3.94) * mm});
            skLineSegment(sketch, "E1493", {"start": v(55.9, 3.94) * mm, "end": v(55.94, 3.9) * mm});
            skLineSegment(sketch, "E1494", {"start": v(55.94, 3.9) * mm, "end": v(55.98, 3.88) * mm});
            skLineSegment(sketch, "E1495", {"start": v(55.98, 3.88) * mm, "end": v(56.02, 3.85) * mm});
            skLineSegment(sketch, "E1496", {"start": v(56.02, 3.85) * mm, "end": v(56.06, 3.81) * mm});
            skLineSegment(sketch, "E1497", {"start": v(56.06, 3.81) * mm, "end": v(56.1, 3.78) * mm});
            skLineSegment(sketch, "E1498", {"start": v(56.1, 3.78) * mm, "end": v(56.13, 3.75) * mm});
            skLineSegment(sketch, "E1499", {"start": v(56.13, 3.75) * mm, "end": v(56.17, 3.73) * mm});
            skLineSegment(sketch, "E1500", {"start": v(56.17, 3.73) * mm, "end": v(56.2, 3.7) * mm});
            skLineSegment(sketch, "E1501", {"start": v(56.2, 3.7) * mm, "end": v(56.24, 3.7) * mm});
            skLineSegment(sketch, "E1502", {"start": v(56.24, 3.7) * mm, "end": v(56.27, 3.68) * mm});
            skLineSegment(sketch, "E1503", {"start": v(56.27, 3.68) * mm, "end": v(56.3, 3.67) * mm});
            skLineSegment(sketch, "E1504", {"start": v(56.3, 3.67) * mm, "end": v(56.32, 3.67) * mm});
            skLineSegment(sketch, "E1505", {"start": v(56.32, 3.67) * mm, "end": v(56.34, 3.67) * mm});
            skLineSegment(sketch, "E1506", {"start": v(56.34, 3.67) * mm, "end": v(56.36, 3.67) * mm});
            skLineSegment(sketch, "E1507", {"start": v(56.36, 3.67) * mm, "end": v(56.37, 3.68) * mm});
            skLineSegment(sketch, "E1508", {"start": v(56.37, 3.68) * mm, "end": v(56.39, 3.68) * mm});
            skLineSegment(sketch, "E1509", {"start": v(56.39, 3.68) * mm, "end": v(56.4, 3.7) * mm});
            skLineSegment(sketch, "E1510", {"start": v(56.4, 3.7) * mm, "end": v(56.41, 3.7) * mm});
            skLineSegment(sketch, "E1511", {"start": v(56.41, 3.7) * mm, "end": v(56.43, 3.73) * mm});
            skLineSegment(sketch, "E1512", {"start": v(56.43, 3.73) * mm, "end": v(56.44, 3.75) * mm});
            skLineSegment(sketch, "E1513", {"start": v(56.44, 3.75) * mm, "end": v(56.46, 3.78) * mm});
            skLineSegment(sketch, "E1514", {"start": v(56.46, 3.78) * mm, "end": v(56.48, 3.81) * mm});
            skLineSegment(sketch, "E1515", {"start": v(56.48, 3.81) * mm, "end": v(56.5, 3.86) * mm});
            skLineSegment(sketch, "E1516", {"start": v(56.5, 3.86) * mm, "end": v(56.52, 3.9) * mm});
            skLineSegment(sketch, "E1517", {"start": v(56.52, 3.9) * mm, "end": v(56.55, 3.96) * mm});
            skLineSegment(sketch, "E1518", {"start": v(56.55, 3.96) * mm, "end": v(56.58, 4.03) * mm});
            skLineSegment(sketch, "E1519", {"start": v(56.58, 4.03) * mm, "end": v(56.61, 4.11) * mm});
            skLineSegment(sketch, "E1520", {"start": v(56.61, 4.11) * mm, "end": v(56.65, 4.2) * mm});
            skLineSegment(sketch, "E1521", {"start": v(56.65, 4.2) * mm, "end": v(56.67, 4.25) * mm});
            skLineSegment(sketch, "E1522", {"start": v(56.67, 4.25) * mm, "end": v(56.7, 4.31) * mm});
            skLineSegment(sketch, "E1523", {"start": v(56.7, 4.31) * mm, "end": v(56.72, 4.37) * mm});
            skLineSegment(sketch, "E1524", {"start": v(56.72, 4.37) * mm, "end": v(56.74, 4.43) * mm});
            skLineSegment(sketch, "E1525", {"start": v(56.74, 4.43) * mm, "end": v(56.76, 4.48) * mm});
            skLineSegment(sketch, "E1526", {"start": v(56.76, 4.48) * mm, "end": v(56.78, 4.54) * mm});
            skLineSegment(sketch, "E1527", {"start": v(56.78, 4.54) * mm, "end": v(56.8, 4.6) * mm});
            skLineSegment(sketch, "E1528", {"start": v(56.8, 4.6) * mm, "end": v(56.83, 4.65) * mm});
            skLineSegment(sketch, "E1529", {"start": v(56.83, 4.65) * mm, "end": v(56.85, 4.7) * mm});
            skLineSegment(sketch, "E1530", {"start": v(56.85, 4.7) * mm, "end": v(56.87, 4.76) * mm});
            skLineSegment(sketch, "E1531", {"start": v(56.87, 4.76) * mm, "end": v(56.88, 4.8) * mm});
            skLineSegment(sketch, "E1532", {"start": v(56.88, 4.8) * mm, "end": v(56.9, 4.85) * mm});
            skLineSegment(sketch, "E1533", {"start": v(56.9, 4.85) * mm, "end": v(56.92, 4.9) * mm});
            skLineSegment(sketch, "E1534", {"start": v(56.92, 4.9) * mm, "end": v(56.93, 4.94) * mm});
            skLineSegment(sketch, "E1535", {"start": v(56.93, 4.94) * mm, "end": v(56.94, 4.97) * mm});
            skLineSegment(sketch, "E1536", {"start": v(56.94, 4.97) * mm, "end": v(56.95, 5) * mm});
            skLineSegment(sketch, "E1537", {"start": v(56.95, 5) * mm, "end": v(56.98, 5.1) * mm});
            skLineSegment(sketch, "E1538", {"start": v(56.98, 5.1) * mm, "end": v(57.01, 5.19) * mm});
            skLineSegment(sketch, "E1539", {"start": v(57.01, 5.19) * mm, "end": v(57.04, 5.27) * mm});
            skLineSegment(sketch, "E1540", {"start": v(57.04, 5.27) * mm, "end": v(57.08, 5.35) * mm});
            skLineSegment(sketch, "E1541", {"start": v(57.08, 5.35) * mm, "end": v(57.11, 5.42) * mm});
            skLineSegment(sketch, "E1542", {"start": v(57.11, 5.42) * mm, "end": v(57.15, 5.5) * mm});
            skLineSegment(sketch, "E1543", {"start": v(57.15, 5.5) * mm, "end": v(57.19, 5.56) * mm});
            skLineSegment(sketch, "E1544", {"start": v(57.19, 5.56) * mm, "end": v(57.23, 5.61) * mm});
            skLineSegment(sketch, "E1545", {"start": v(57.23, 5.61) * mm, "end": v(57.27, 5.67) * mm});
            skLineSegment(sketch, "E1546", {"start": v(57.27, 5.67) * mm, "end": v(57.31, 5.72) * mm});
            skLineSegment(sketch, "E1547", {"start": v(57.31, 5.72) * mm, "end": v(57.36, 5.76) * mm});
            skLineSegment(sketch, "E1548", {"start": v(57.36, 5.76) * mm, "end": v(57.41, 5.8) * mm});
            skLineSegment(sketch, "E1549", {"start": v(57.41, 5.8) * mm, "end": v(57.46, 5.84) * mm});
            skLineSegment(sketch, "E1550", {"start": v(57.46, 5.84) * mm, "end": v(57.52, 5.87) * mm});
            skLineSegment(sketch, "E1551", {"start": v(57.52, 5.87) * mm, "end": v(57.58, 5.9) * mm});
            skLineSegment(sketch, "E1552", {"start": v(57.58, 5.9) * mm, "end": v(57.64, 5.93) * mm});
            skLineSegment(sketch, "E1553", {"start": v(57.64, 5.93) * mm, "end": v(57.7, 5.96) * mm});
            skLineSegment(sketch, "E1554", {"start": v(57.7, 5.96) * mm, "end": v(57.76, 5.98) * mm});
            skLineSegment(sketch, "E1555", {"start": v(57.76, 5.98) * mm, "end": v(57.8, 6) * mm});
            skLineSegment(sketch, "E1556", {"start": v(57.8, 6) * mm, "end": v(57.85, 6.02) * mm});
            skLineSegment(sketch, "E1557", {"start": v(57.85, 6.02) * mm, "end": v(57.89, 6.04) * mm});
            skLineSegment(sketch, "E1558", {"start": v(57.89, 6.04) * mm, "end": v(57.92, 6.06) * mm});
            skLineSegment(sketch, "E1559", {"start": v(57.92, 6.06) * mm, "end": v(57.94, 6.08) * mm});
            skLineSegment(sketch, "E1560", {"start": v(57.94, 6.08) * mm, "end": v(57.96, 6.1) * mm});
            skLineSegment(sketch, "E1561", {"start": v(57.96, 6.1) * mm, "end": v(57.98, 6.11) * mm});
            skLineSegment(sketch, "E1562", {"start": v(57.98, 6.11) * mm, "end": v(58, 6.13) * mm});
            skLineSegment(sketch, "E1563", {"start": v(58, 6.13) * mm, "end": v(58, 6.15) * mm});
            skLineSegment(sketch, "E1564", {"start": v(58, 6.15) * mm, "end": v(58, 6.18) * mm});
            skLineSegment(sketch, "E1565", {"start": v(58, 6.18) * mm, "end": v(58, 6.2) * mm});
            skLineSegment(sketch, "E1566", {"start": v(58, 6.2) * mm, "end": v(58, 6.23) * mm});
            skLineSegment(sketch, "E1567", {"start": v(58, 6.23) * mm, "end": v(58, 6.26) * mm});
            skLineSegment(sketch, "E1568", {"start": v(58, 6.26) * mm, "end": v(58, 6.3) * mm});
            skLineSegment(sketch, "E1569", {"start": v(58, 6.3) * mm, "end": v(57.99, 6.36) * mm});
            skLineSegment(sketch, "E1570", {"start": v(57.99, 6.36) * mm, "end": v(57.98, 6.42) * mm});
            skLineSegment(sketch, "E1571", {"start": v(57.98, 6.42) * mm, "end": v(57.97, 6.47) * mm});
            skLineSegment(sketch, "E1572", {"start": v(57.97, 6.47) * mm, "end": v(57.96, 6.52) * mm});
            skLineSegment(sketch, "E1573", {"start": v(57.96, 6.52) * mm, "end": v(57.95, 6.56) * mm});
            skLineSegment(sketch, "E1574", {"start": v(57.95, 6.56) * mm, "end": v(57.94, 6.6) * mm});
            skLineSegment(sketch, "E1575", {"start": v(57.94, 6.6) * mm, "end": v(57.93, 6.63) * mm});
            skLineSegment(sketch, "E1576", {"start": v(57.93, 6.63) * mm, "end": v(57.92, 6.66) * mm});
            skLineSegment(sketch, "E1577", {"start": v(57.92, 6.66) * mm, "end": v(57.9, 6.7) * mm});
            skLineSegment(sketch, "E1578", {"start": v(57.9, 6.7) * mm, "end": v(57.9, 6.71) * mm});
            skLineSegment(sketch, "E1579", {"start": v(57.9, 6.71) * mm, "end": v(57.88, 6.73) * mm});
            skLineSegment(sketch, "E1580", {"start": v(57.88, 6.73) * mm, "end": v(57.86, 6.75) * mm});
            skLineSegment(sketch, "E1581", {"start": v(57.86, 6.75) * mm, "end": v(57.84, 6.76) * mm});
            skLineSegment(sketch, "E1582", {"start": v(57.84, 6.76) * mm, "end": v(57.82, 6.78) * mm});
            skLineSegment(sketch, "E1583", {"start": v(57.82, 6.78) * mm, "end": v(57.8, 6.8) * mm});
            skLineSegment(sketch, "E1584", {"start": v(57.8, 6.8) * mm, "end": v(57.78, 6.8) * mm});
            skLineSegment(sketch, "E1585", {"start": v(57.78, 6.8) * mm, "end": v(57.75, 6.81) * mm});
            skLineSegment(sketch, "E1586", {"start": v(57.75, 6.81) * mm, "end": v(57.72, 6.82) * mm});
            skLineSegment(sketch, "E1587", {"start": v(57.72, 6.82) * mm, "end": v(57.68, 6.83) * mm});
            skLineSegment(sketch, "E1588", {"start": v(57.68, 6.83) * mm, "end": v(57.64, 6.84) * mm});
            skLineSegment(sketch, "E1589", {"start": v(57.64, 6.84) * mm, "end": v(57.6, 6.84) * mm});
            skLineSegment(sketch, "E1590", {"start": v(57.6, 6.84) * mm, "end": v(57.56, 6.85) * mm});
            skLineSegment(sketch, "E1591", {"start": v(57.56, 6.85) * mm, "end": v(57.52, 6.85) * mm});
            skLineSegment(sketch, "E1592", {"start": v(57.52, 6.85) * mm, "end": v(57.49, 6.85) * mm});
            skLineSegment(sketch, "E1593", {"start": v(57.49, 6.85) * mm, "end": v(57.46, 6.85) * mm});
            skLineSegment(sketch, "E1594", {"start": v(57.46, 6.85) * mm, "end": v(57.43, 6.86) * mm});
            skLineSegment(sketch, "E1595", {"start": v(57.43, 6.86) * mm, "end": v(57.4, 6.86) * mm});
            skLineSegment(sketch, "E1596", {"start": v(57.4, 6.86) * mm, "end": v(57.38, 6.86) * mm});
            skLineSegment(sketch, "E1597", {"start": v(57.38, 6.86) * mm, "end": v(57.35, 6.87) * mm});
            skLineSegment(sketch, "E1598", {"start": v(57.35, 6.87) * mm, "end": v(57.33, 6.88) * mm});
            skLineSegment(sketch, "E1599", {"start": v(57.33, 6.88) * mm, "end": v(57.32, 6.89) * mm});
            skLineSegment(sketch, "E1600", {"start": v(57.32, 6.89) * mm, "end": v(57.3, 6.9) * mm});
            skLineSegment(sketch, "E1601", {"start": v(57.3, 6.9) * mm, "end": v(57.29, 6.91) * mm});
            skLineSegment(sketch, "E1602", {"start": v(57.29, 6.91) * mm, "end": v(57.28, 6.93) * mm});
            skLineSegment(sketch, "E1603", {"start": v(57.28, 6.93) * mm, "end": v(57.27, 6.95) * mm});
            skLineSegment(sketch, "E1604", {"start": v(57.27, 6.95) * mm, "end": v(57.26, 6.97) * mm});
            skLineSegment(sketch, "E1605", {"start": v(57.26, 6.97) * mm, "end": v(57.25, 7) * mm});
            skLineSegment(sketch, "E1606", {"start": v(57.25, 7) * mm, "end": v(57.24, 7.03) * mm});
            skLineSegment(sketch, "E1607", {"start": v(57.24, 7.03) * mm, "end": v(57.24, 7.06) * mm});
            skLineSegment(sketch, "E1608", {"start": v(57.24, 7.06) * mm, "end": v(57.23, 7.1) * mm});
            skLineSegment(sketch, "E1609", {"start": v(57.23, 7.1) * mm, "end": v(57.21, 7.18) * mm});
            skLineSegment(sketch, "E1610", {"start": v(57.21, 7.18) * mm, "end": v(57.2, 7.24) * mm});
            skLineSegment(sketch, "E1611", {"start": v(57.2, 7.24) * mm, "end": v(57.2, 7.3) * mm});
            skLineSegment(sketch, "E1612", {"start": v(57.2, 7.3) * mm, "end": v(57.19, 7.35) * mm});
            skLineSegment(sketch, "E1613", {"start": v(57.19, 7.35) * mm, "end": v(57.18, 7.39) * mm});
            skLineSegment(sketch, "E1614", {"start": v(57.18, 7.39) * mm, "end": v(57.18, 7.43) * mm});
            skLineSegment(sketch, "E1615", {"start": v(57.18, 7.43) * mm, "end": v(57.18, 7.47) * mm});
            skLineSegment(sketch, "E1616", {"start": v(57.18, 7.47) * mm, "end": v(57.18, 7.51) * mm});
            skLineSegment(sketch, "E1617", {"start": v(57.18, 7.51) * mm, "end": v(57.17, 7.54) * mm});
            skLineSegment(sketch, "E1618", {"start": v(57.17, 7.54) * mm, "end": v(57.17, 7.57) * mm});
            skLineSegment(sketch, "E1619", {"start": v(57.17, 7.57) * mm, "end": v(57.16, 7.6) * mm});
            skLineSegment(sketch, "E1620", {"start": v(57.16, 7.6) * mm, "end": v(57.15, 7.61) * mm});
            skLineSegment(sketch, "E1621", {"start": v(57.15, 7.61) * mm, "end": v(57.14, 7.63) * mm});
            skLineSegment(sketch, "E1622", {"start": v(57.14, 7.63) * mm, "end": v(57.12, 7.65) * mm});
            skLineSegment(sketch, "E1623", {"start": v(57.12, 7.65) * mm, "end": v(57.1, 7.66) * mm});
            skLineSegment(sketch, "E1624", {"start": v(57.1, 7.66) * mm, "end": v(57.08, 7.67) * mm});
            skLineSegment(sketch, "E1625", {"start": v(57.08, 7.67) * mm, "end": v(57.04, 7.7) * mm});
            skLineSegment(sketch, "E1626", {"start": v(57.04, 7.7) * mm, "end": v(57.01, 7.72) * mm});
            skLineSegment(sketch, "E1627", {"start": v(57.01, 7.72) * mm, "end": v(57, 7.74) * mm});
            skLineSegment(sketch, "E1628", {"start": v(57, 7.74) * mm, "end": v(57, 7.77) * mm});
            skLineSegment(sketch, "E1629", {"start": v(57, 7.77) * mm, "end": v(57, 7.8) * mm});
            skLineSegment(sketch, "E1630", {"start": v(57, 7.8) * mm, "end": v(57.02, 7.85) * mm});
            skLineSegment(sketch, "E1631", {"start": v(57.02, 7.85) * mm, "end": v(57.04, 7.9) * mm});
            skLineSegment(sketch, "E1632", {"start": v(57.04, 7.9) * mm, "end": v(57.08, 7.96) * mm});
            skLineSegment(sketch, "E1633", {"start": v(57.08, 7.96) * mm, "end": v(57.11, 8) * mm});
            skLineSegment(sketch, "E1634", {"start": v(57.11, 8) * mm, "end": v(57.14, 8.05) * mm});
            skLineSegment(sketch, "E1635", {"start": v(57.14, 8.05) * mm, "end": v(57.15, 8.09) * mm});
            skLineSegment(sketch, "E1636", {"start": v(57.15, 8.09) * mm, "end": v(57.16, 8.12) * mm});
            skLineSegment(sketch, "E1637", {"start": v(57.16, 8.12) * mm, "end": v(57.17, 8.16) * mm});
            skLineSegment(sketch, "E1638", {"start": v(57.17, 8.16) * mm, "end": v(57.17, 8.2) * mm});
            skLineSegment(sketch, "E1639", {"start": v(57.17, 8.2) * mm, "end": v(57.16, 8.26) * mm});
            skLineSegment(sketch, "E1640", {"start": v(57.16, 8.26) * mm, "end": v(57.16, 8.33) * mm});
            skLineSegment(sketch, "E1641", {"start": v(57.16, 8.33) * mm, "end": v(57.15, 8.37) * mm});
            skLineSegment(sketch, "E1642", {"start": v(57.15, 8.37) * mm, "end": v(57.15, 8.4) * mm});
            skLineSegment(sketch, "E1643", {"start": v(57.15, 8.4) * mm, "end": v(57.15, 8.43) * mm});
            skLineSegment(sketch, "E1644", {"start": v(57.15, 8.43) * mm, "end": v(57.15, 8.46) * mm});
            skLineSegment(sketch, "E1645", {"start": v(57.15, 8.46) * mm, "end": v(57.15, 8.49) * mm});
            skLineSegment(sketch, "E1646", {"start": v(57.15, 8.49) * mm, "end": v(57.15, 8.51) * mm});
            skLineSegment(sketch, "E1647", {"start": v(57.15, 8.51) * mm, "end": v(57.15, 8.54) * mm});
            skLineSegment(sketch, "E1648", {"start": v(57.15, 8.54) * mm, "end": v(57.16, 8.57) * mm});
            skLineSegment(sketch, "E1649", {"start": v(57.16, 8.57) * mm, "end": v(57.17, 8.6) * mm});
            skLineSegment(sketch, "E1650", {"start": v(57.17, 8.6) * mm, "end": v(57.18, 8.63) * mm});
            skLineSegment(sketch, "E1651", {"start": v(57.18, 8.63) * mm, "end": v(57.2, 8.67) * mm});
            skLineSegment(sketch, "E1652", {"start": v(57.2, 8.67) * mm, "end": v(57.21, 8.71) * mm});
            skLineSegment(sketch, "E1653", {"start": v(57.21, 8.71) * mm, "end": v(57.23, 8.76) * mm});
            skLineSegment(sketch, "E1654", {"start": v(57.23, 8.76) * mm, "end": v(57.26, 8.8) * mm});
            skLineSegment(sketch, "E1655", {"start": v(57.26, 8.8) * mm, "end": v(57.28, 8.87) * mm});
            skLineSegment(sketch, "E1656", {"start": v(57.28, 8.87) * mm, "end": v(57.31, 8.93) * mm});
            skLineSegment(sketch, "E1657", {"start": v(57.31, 8.93) * mm, "end": v(57.34, 9) * mm});
            skLineSegment(sketch, "E1658", {"start": v(57.34, 9) * mm, "end": v(57.37, 9.05) * mm});
            skLineSegment(sketch, "E1659", {"start": v(57.37, 9.05) * mm, "end": v(57.4, 9.1) * mm});
            skLineSegment(sketch, "E1660", {"start": v(57.4, 9.1) * mm, "end": v(57.42, 9.14) * mm});
            skLineSegment(sketch, "E1661", {"start": v(57.42, 9.14) * mm, "end": v(57.44, 9.18) * mm});
            skLineSegment(sketch, "E1662", {"start": v(57.44, 9.18) * mm, "end": v(57.45, 9.21) * mm});
            skLineSegment(sketch, "E1663", {"start": v(57.45, 9.21) * mm, "end": v(57.47, 9.24) * mm});
            skLineSegment(sketch, "E1664", {"start": v(57.47, 9.24) * mm, "end": v(57.5, 9.27) * mm});
            skLineSegment(sketch, "E1665", {"start": v(57.5, 9.27) * mm, "end": v(57.5, 9.29) * mm});
            skLineSegment(sketch, "E1666", {"start": v(57.5, 9.29) * mm, "end": v(57.53, 9.3) * mm});
            skLineSegment(sketch, "E1667", {"start": v(57.53, 9.3) * mm, "end": v(57.54, 9.33) * mm});
            skLineSegment(sketch, "E1668", {"start": v(57.54, 9.33) * mm, "end": v(57.56, 9.34) * mm});
            skLineSegment(sketch, "E1669", {"start": v(57.56, 9.34) * mm, "end": v(57.58, 9.35) * mm});
            skLineSegment(sketch, "E1670", {"start": v(57.58, 9.35) * mm, "end": v(57.6, 9.37) * mm});
            skLineSegment(sketch, "E1671", {"start": v(57.6, 9.37) * mm, "end": v(57.63, 9.38) * mm});
            skLineSegment(sketch, "E1672", {"start": v(57.63, 9.38) * mm, "end": v(57.66, 9.4) * mm});
            skLineSegment(sketch, "E1673", {"start": v(57.66, 9.4) * mm, "end": v(57.75, 9.43) * mm});
            skLineSegment(sketch, "E1674", {"start": v(57.75, 9.43) * mm, "end": v(57.85, 9.47) * mm});
            skLineSegment(sketch, "E1675", {"start": v(57.85, 9.47) * mm, "end": v(57.96, 9.5) * mm});
            skLineSegment(sketch, "E1676", {"start": v(57.96, 9.5) * mm, "end": v(58.08, 9.52) * mm});
            skLineSegment(sketch, "E1677", {"start": v(58.08, 9.52) * mm, "end": v(58.2, 9.54) * mm});
            skLineSegment(sketch, "E1678", {"start": v(58.2, 9.54) * mm, "end": v(58.32, 9.55) * mm});
            skLineSegment(sketch, "E1679", {"start": v(58.32, 9.55) * mm, "end": v(58.45, 9.55) * mm});
            skLineSegment(sketch, "E1680", {"start": v(58.45, 9.55) * mm, "end": v(58.58, 9.55) * mm});
            skLineSegment(sketch, "E1681", {"start": v(58.58, 9.55) * mm, "end": v(58.7, 9.54) * mm});
            skLineSegment(sketch, "E1682", {"start": v(58.7, 9.54) * mm, "end": v(58.82, 9.52) * mm});
            skLineSegment(sketch, "E1683", {"start": v(58.82, 9.52) * mm, "end": v(58.93, 9.49) * mm});
            skLineSegment(sketch, "E1684", {"start": v(58.93, 9.49) * mm, "end": v(59.03, 9.45) * mm});
            skLineSegment(sketch, "E1685", {"start": v(59.03, 9.45) * mm, "end": v(59.13, 9.4) * mm});
            skLineSegment(sketch, "E1686", {"start": v(59.13, 9.4) * mm, "end": v(59.22, 9.34) * mm});
            skLineSegment(sketch, "E1687", {"start": v(59.22, 9.34) * mm, "end": v(59.3, 9.28) * mm});
            skLineSegment(sketch, "E1688", {"start": v(59.3, 9.28) * mm, "end": v(59.38, 9.2) * mm});
            skLineSegment(sketch, "E1689", {"start": v(59.38, 9.2) * mm, "end": v(59.4, 9.17) * mm});
            skLineSegment(sketch, "E1690", {"start": v(59.4, 9.17) * mm, "end": v(59.43, 9.15) * mm});
            skLineSegment(sketch, "E1691", {"start": v(59.43, 9.15) * mm, "end": v(59.45, 9.13) * mm});
            skLineSegment(sketch, "E1692", {"start": v(59.45, 9.13) * mm, "end": v(59.48, 9.1) * mm});
            skLineSegment(sketch, "E1693", {"start": v(59.48, 9.1) * mm, "end": v(59.5, 9.1) * mm});
            skLineSegment(sketch, "E1694", {"start": v(59.5, 9.1) * mm, "end": v(59.53, 9.08) * mm});
            skLineSegment(sketch, "E1695", {"start": v(59.53, 9.08) * mm, "end": v(59.55, 9.08) * mm});
            skLineSegment(sketch, "E1696", {"start": v(59.55, 9.08) * mm, "end": v(59.57, 9.07) * mm});
            skLineSegment(sketch, "E1697", {"start": v(59.57, 9.07) * mm, "end": v(59.6, 9.07) * mm});
            skLineSegment(sketch, "E1698", {"start": v(59.6, 9.07) * mm, "end": v(59.62, 9.07) * mm});
            skLineSegment(sketch, "E1699", {"start": v(59.62, 9.07) * mm, "end": v(59.65, 9.06) * mm});
            skLineSegment(sketch, "E1700", {"start": v(59.65, 9.06) * mm, "end": v(59.68, 9.05) * mm});
            skLineSegment(sketch, "E1701", {"start": v(59.68, 9.05) * mm, "end": v(59.7, 9.04) * mm});
            skLineSegment(sketch, "E1702", {"start": v(59.7, 9.04) * mm, "end": v(59.74, 9.03) * mm});
            skLineSegment(sketch, "E1703", {"start": v(59.74, 9.03) * mm, "end": v(59.77, 9.02) * mm});
            skLineSegment(sketch, "E1704", {"start": v(59.77, 9.02) * mm, "end": v(59.8, 9) * mm});
            skLineSegment(sketch, "E1705", {"start": v(59.8, 9) * mm, "end": v(59.84, 8.98) * mm});
            skLineSegment(sketch, "E1706", {"start": v(59.84, 8.98) * mm, "end": v(59.87, 8.97) * mm});
            skLineSegment(sketch, "E1707", {"start": v(59.87, 8.97) * mm, "end": v(59.9, 8.95) * mm});
            skLineSegment(sketch, "E1708", {"start": v(59.9, 8.95) * mm, "end": v(59.93, 8.93) * mm});
            skLineSegment(sketch, "E1709", {"start": v(59.93, 8.93) * mm, "end": v(59.95, 8.92) * mm});
            skLineSegment(sketch, "E1710", {"start": v(59.95, 8.92) * mm, "end": v(59.98, 8.9) * mm});
            skLineSegment(sketch, "E1711", {"start": v(59.98, 8.9) * mm, "end": v(60, 8.88) * mm});
            skLineSegment(sketch, "E1712", {"start": v(60, 8.88) * mm, "end": v(60.01, 8.86) * mm});
            skLineSegment(sketch, "E1713", {"start": v(60.01, 8.86) * mm, "end": v(60.03, 8.84) * mm});
            skLineSegment(sketch, "E1714", {"start": v(60.03, 8.84) * mm, "end": v(60.05, 8.8) * mm});
            skLineSegment(sketch, "E1715", {"start": v(60.05, 8.8) * mm, "end": v(60.08, 8.76) * mm});
            skLineSegment(sketch, "E1716", {"start": v(60.08, 8.76) * mm, "end": v(60.11, 8.7) * mm});
            skLineSegment(sketch, "E1717", {"start": v(60.11, 8.7) * mm, "end": v(60.15, 8.64) * mm});
            skLineSegment(sketch, "E1718", {"start": v(60.15, 8.64) * mm, "end": v(60.19, 8.57) * mm});
            skLineSegment(sketch, "E1719", {"start": v(60.19, 8.57) * mm, "end": v(60.23, 8.5) * mm});
            skLineSegment(sketch, "E1720", {"start": v(60.23, 8.5) * mm, "end": v(60.26, 8.42) * mm});
            skLineSegment(sketch, "E1721", {"start": v(60.26, 8.42) * mm, "end": v(60.3, 8.35) * mm});
            skLineSegment(sketch, "E1722", {"start": v(60.3, 8.35) * mm, "end": v(60.34, 8.28) * mm});
            skLineSegment(sketch, "E1723", {"start": v(60.34, 8.28) * mm, "end": v(60.37, 8.22) * mm});
            skLineSegment(sketch, "E1724", {"start": v(60.37, 8.22) * mm, "end": v(60.4, 8.16) * mm});
            skLineSegment(sketch, "E1725", {"start": v(60.4, 8.16) * mm, "end": v(60.43, 8.11) * mm});
            skLineSegment(sketch, "E1726", {"start": v(60.43, 8.11) * mm, "end": v(60.46, 8.07) * mm});
            skLineSegment(sketch, "E1727", {"start": v(60.46, 8.07) * mm, "end": v(60.49, 8.03) * mm});
            skLineSegment(sketch, "E1728", {"start": v(60.49, 8.03) * mm, "end": v(60.52, 8) * mm});
            skLineSegment(sketch, "E1729", {"start": v(60.52, 8) * mm, "end": v(60.54, 7.96) * mm});
            skLineSegment(sketch, "E1730", {"start": v(60.54, 7.96) * mm, "end": v(60.57, 7.94) * mm});
            skLineSegment(sketch, "E1731", {"start": v(60.57, 7.94) * mm, "end": v(60.6, 7.91) * mm});
            skLineSegment(sketch, "E1732", {"start": v(60.6, 7.91) * mm, "end": v(60.62, 7.9) * mm});
            skLineSegment(sketch, "E1733", {"start": v(60.62, 7.9) * mm, "end": v(60.65, 7.87) * mm});
            skLineSegment(sketch, "E1734", {"start": v(60.65, 7.87) * mm, "end": v(60.68, 7.86) * mm});
            skLineSegment(sketch, "E1735", {"start": v(60.68, 7.86) * mm, "end": v(60.7, 7.84) * mm});
            skLineSegment(sketch, "E1736", {"start": v(60.7, 7.84) * mm, "end": v(60.74, 7.83) * mm});
            skLineSegment(sketch, "E1737", {"start": v(60.74, 7.83) * mm, "end": v(60.77, 7.81) * mm});
            skLineSegment(sketch, "E1738", {"start": v(60.77, 7.81) * mm, "end": v(60.8, 7.8) * mm});
            skLineSegment(sketch, "E1739", {"start": v(60.8, 7.8) * mm, "end": v(60.83, 7.78) * mm});
            skLineSegment(sketch, "E1740", {"start": v(60.83, 7.78) * mm, "end": v(60.86, 7.76) * mm});
            skLineSegment(sketch, "E1741", {"start": v(60.86, 7.76) * mm, "end": v(60.89, 7.74) * mm});
            skLineSegment(sketch, "E1742", {"start": v(60.89, 7.74) * mm, "end": v(60.92, 7.72) * mm});
            skLineSegment(sketch, "E1743", {"start": v(60.92, 7.72) * mm, "end": v(60.95, 7.7) * mm});
            skLineSegment(sketch, "E1744", {"start": v(60.95, 7.7) * mm, "end": v(60.97, 7.68) * mm});
            skLineSegment(sketch, "E1745", {"start": v(60.97, 7.68) * mm, "end": v(60.98, 7.66) * mm});
            skLineSegment(sketch, "E1746", {"start": v(60.98, 7.66) * mm, "end": v(61, 7.64) * mm});
            skLineSegment(sketch, "E1747", {"start": v(61, 7.64) * mm, "end": v(61.01, 7.63) * mm});
            skLineSegment(sketch, "E1748", {"start": v(61.01, 7.63) * mm, "end": v(61.02, 7.62) * mm});
            skLineSegment(sketch, "E1749", {"start": v(61.02, 7.62) * mm, "end": v(61.03, 7.6) * mm});
            skLineSegment(sketch, "E1750", {"start": v(61.03, 7.6) * mm, "end": v(61.04, 7.59) * mm});
            skLineSegment(sketch, "E1751", {"start": v(61.04, 7.59) * mm, "end": v(61.05, 7.57) * mm});
            skLineSegment(sketch, "E1752", {"start": v(61.05, 7.57) * mm, "end": v(61.05, 7.55) * mm});
            skLineSegment(sketch, "E1753", {"start": v(61.05, 7.55) * mm, "end": v(61.06, 7.53) * mm});
            skLineSegment(sketch, "E1754", {"start": v(61.06, 7.53) * mm, "end": v(61.06, 7.5) * mm});
            skLineSegment(sketch, "E1755", {"start": v(61.06, 7.5) * mm, "end": v(61.06, 7.48) * mm});
            skLineSegment(sketch, "E1756", {"start": v(61.06, 7.48) * mm, "end": v(61.07, 7.45) * mm});
            skLineSegment(sketch, "E1757", {"start": v(61.07, 7.45) * mm, "end": v(61.07, 7.42) * mm});
            skLineSegment(sketch, "E1758", {"start": v(61.07, 7.42) * mm, "end": v(61.07, 7.38) * mm});
            skLineSegment(sketch, "E1759", {"start": v(61.07, 7.38) * mm, "end": v(61.07, 7.34) * mm});
            skLineSegment(sketch, "E1760", {"start": v(61.07, 7.34) * mm, "end": v(61.07, 7.29) * mm});
            skLineSegment(sketch, "E1761", {"start": v(61.07, 7.29) * mm, "end": v(61.07, 7.23) * mm});
            skLineSegment(sketch, "E1762", {"start": v(61.07, 7.23) * mm, "end": v(61.07, 7.19) * mm});
            skLineSegment(sketch, "E1763", {"start": v(61.07, 7.19) * mm, "end": v(61.07, 7.14) * mm});
            skLineSegment(sketch, "E1764", {"start": v(61.07, 7.14) * mm, "end": v(61.08, 7.1) * mm});
            skLineSegment(sketch, "E1765", {"start": v(61.08, 7.1) * mm, "end": v(61.08, 7.06) * mm});
            skLineSegment(sketch, "E1766", {"start": v(61.08, 7.06) * mm, "end": v(61.08, 7.03) * mm});
            skLineSegment(sketch, "E1767", {"start": v(61.08, 7.03) * mm, "end": v(61.1, 7) * mm});
            skLineSegment(sketch, "E1768", {"start": v(61.1, 7) * mm, "end": v(61.1, 6.96) * mm});
            skLineSegment(sketch, "E1769", {"start": v(61.1, 6.96) * mm, "end": v(61.1, 6.93) * mm});
            skLineSegment(sketch, "E1770", {"start": v(61.1, 6.93) * mm, "end": v(61.12, 6.9) * mm});
            skLineSegment(sketch, "E1771", {"start": v(61.12, 6.9) * mm, "end": v(61.13, 6.88) * mm});
            skLineSegment(sketch, "E1772", {"start": v(61.13, 6.88) * mm, "end": v(61.15, 6.85) * mm});
            skLineSegment(sketch, "E1773", {"start": v(61.15, 6.85) * mm, "end": v(61.17, 6.83) * mm});
            skLineSegment(sketch, "E1774", {"start": v(61.17, 6.83) * mm, "end": v(61.18, 6.8) * mm});
            skLineSegment(sketch, "E1775", {"start": v(61.18, 6.8) * mm, "end": v(61.2, 6.77) * mm});
            skLineSegment(sketch, "E1776", {"start": v(61.2, 6.77) * mm, "end": v(61.23, 6.75) * mm});
            skLineSegment(sketch, "E1777", {"start": v(61.23, 6.75) * mm, "end": v(61.26, 6.72) * mm});
            skLineSegment(sketch, "E1778", {"start": v(61.26, 6.72) * mm, "end": v(61.27, 6.7) * mm});
            skLineSegment(sketch, "E1779", {"start": v(61.27, 6.7) * mm, "end": v(61.28, 6.68) * mm});
            skLineSegment(sketch, "E1780", {"start": v(61.28, 6.68) * mm, "end": v(61.28, 6.68) * mm});
            skLineSegment(sketch, "E1781", {"start": v(61.28, 6.68) * mm, "end": v(61.26, 6.68) * mm});
            skLineSegment(sketch, "E1782", {"start": v(61.26, 6.68) * mm, "end": v(61.23, 6.7) * mm});
            skLineSegment(sketch, "E1783", {"start": v(61.23, 6.7) * mm, "end": v(61.19, 6.71) * mm});
            skLineSegment(sketch, "E1784", {"start": v(61.19, 6.71) * mm, "end": v(61.13, 6.74) * mm});
            skLineSegment(sketch, "E1785", {"start": v(61.13, 6.74) * mm, "end": v(61.1, 6.76) * mm});
            skLineSegment(sketch, "E1786", {"start": v(61.1, 6.76) * mm, "end": v(61.08, 6.77) * mm});
            skLineSegment(sketch, "E1787", {"start": v(61.08, 6.77) * mm, "end": v(61.06, 6.77) * mm});
            skLineSegment(sketch, "E1788", {"start": v(61.06, 6.77) * mm, "end": v(61.04, 6.78) * mm});
            skLineSegment(sketch, "E1789", {"start": v(61.04, 6.78) * mm, "end": v(61.03, 6.77) * mm});
            skLineSegment(sketch, "E1790", {"start": v(61.03, 6.77) * mm, "end": v(61.01, 6.77) * mm});
            skLineSegment(sketch, "E1791", {"start": v(61.01, 6.77) * mm, "end": v(61, 6.76) * mm});
            skLineSegment(sketch, "E1792", {"start": v(61, 6.76) * mm, "end": v(61, 6.74) * mm});
            skLineSegment(sketch, "E1793", {"start": v(61, 6.74) * mm, "end": v(60.98, 6.71) * mm});
            skLineSegment(sketch, "E1794", {"start": v(60.98, 6.71) * mm, "end": v(60.97, 6.68) * mm});
            skLineSegment(sketch, "E1795", {"start": v(60.97, 6.68) * mm, "end": v(60.96, 6.64) * mm});
            skLineSegment(sketch, "E1796", {"start": v(60.96, 6.64) * mm, "end": v(60.96, 6.6) * mm});
            skLineSegment(sketch, "E1797", {"start": v(60.96, 6.6) * mm, "end": v(60.96, 6.57) * mm});
            skLineSegment(sketch, "E1798", {"start": v(60.96, 6.57) * mm, "end": v(60.96, 6.55) * mm});
            skLineSegment(sketch, "E1799", {"start": v(60.96, 6.55) * mm, "end": v(60.95, 6.54) * mm});
            skLineSegment(sketch, "E1800", {"start": v(60.95, 6.54) * mm, "end": v(60.95, 6.53) * mm});
            skLineSegment(sketch, "E1801", {"start": v(60.95, 6.53) * mm, "end": v(60.94, 6.53) * mm});
            skLineSegment(sketch, "E1802", {"start": v(60.94, 6.53) * mm, "end": v(60.93, 6.54) * mm});
            skLineSegment(sketch, "E1803", {"start": v(60.93, 6.54) * mm, "end": v(60.9, 6.56) * mm});
            skLineSegment(sketch, "E1804", {"start": v(60.9, 6.56) * mm, "end": v(60.89, 6.58) * mm});
            skLineSegment(sketch, "E1805", {"start": v(60.89, 6.58) * mm, "end": v(60.86, 6.6) * mm});
            skLineSegment(sketch, "E1806", {"start": v(60.86, 6.6) * mm, "end": v(60.83, 6.64) * mm});
            skLineSegment(sketch, "E1807", {"start": v(60.83, 6.64) * mm, "end": v(60.82, 6.67) * mm});
            skLineSegment(sketch, "E1808", {"start": v(60.82, 6.67) * mm, "end": v(60.81, 6.7) * mm});
            skLineSegment(sketch, "E1809", {"start": v(60.81, 6.7) * mm, "end": v(60.8, 6.73) * mm});
            skLineSegment(sketch, "E1810", {"start": v(60.8, 6.73) * mm, "end": v(60.8, 6.76) * mm});
            skLineSegment(sketch, "E1811", {"start": v(60.8, 6.76) * mm, "end": v(60.78, 6.8) * mm});
            skLineSegment(sketch, "E1812", {"start": v(60.78, 6.8) * mm, "end": v(60.76, 6.82) * mm});
            skLineSegment(sketch, "E1813", {"start": v(60.76, 6.82) * mm, "end": v(60.73, 6.85) * mm});
            skLineSegment(sketch, "E1814", {"start": v(60.73, 6.85) * mm, "end": v(60.7, 6.87) * mm});
            skLineSegment(sketch, "E1815", {"start": v(60.7, 6.87) * mm, "end": v(60.66, 6.9) * mm});
            skLineSegment(sketch, "E1816", {"start": v(60.66, 6.9) * mm, "end": v(60.62, 6.92) * mm});
            skLineSegment(sketch, "E1817", {"start": v(60.62, 6.92) * mm, "end": v(60.6, 6.93) * mm});
            skLineSegment(sketch, "E1818", {"start": v(60.6, 6.93) * mm, "end": v(60.57, 6.95) * mm});
            skLineSegment(sketch, "E1819", {"start": v(60.57, 6.95) * mm, "end": v(60.54, 6.98) * mm});
            skLineSegment(sketch, "E1820", {"start": v(60.54, 6.98) * mm, "end": v(60.51, 7) * mm});
            skLineSegment(sketch, "E1821", {"start": v(60.51, 7) * mm, "end": v(60.48, 7.04) * mm});
            skLineSegment(sketch, "E1822", {"start": v(60.48, 7.04) * mm, "end": v(60.45, 7.08) * mm});
            skLineSegment(sketch, "E1823", {"start": v(60.45, 7.08) * mm, "end": v(60.42, 7.12) * mm});
            skLineSegment(sketch, "E1824", {"start": v(60.42, 7.12) * mm, "end": v(60.4, 7.16) * mm});
            skLineSegment(sketch, "E1825", {"start": v(60.4, 7.16) * mm, "end": v(60.37, 7.2) * mm});
            skLineSegment(sketch, "E1826", {"start": v(60.37, 7.2) * mm, "end": v(60.35, 7.22) * mm});
            skLineSegment(sketch, "E1827", {"start": v(60.35, 7.22) * mm, "end": v(60.33, 7.25) * mm});
            skLineSegment(sketch, "E1828", {"start": v(60.33, 7.25) * mm, "end": v(60.32, 7.27) * mm});
            skLineSegment(sketch, "E1829", {"start": v(60.32, 7.27) * mm, "end": v(60.3, 7.29) * mm});
            skLineSegment(sketch, "E1830", {"start": v(60.3, 7.29) * mm, "end": v(60.3, 7.3) * mm});
            skLineSegment(sketch, "E1831", {"start": v(60.3, 7.3) * mm, "end": v(60.28, 7.3) * mm});
            skLineSegment(sketch, "E1832", {"start": v(60.28, 7.3) * mm, "end": v(60.28, 7.31) * mm});
            skLineSegment(sketch, "E1833", {"start": v(60.28, 7.31) * mm, "end": v(60.27, 7.31) * mm});
            skLineSegment(sketch, "E1834", {"start": v(60.27, 7.31) * mm, "end": v(60.27, 7.31) * mm});
            skLineSegment(sketch, "E1835", {"start": v(60.27, 7.31) * mm, "end": v(60.26, 7.3) * mm});
            skLineSegment(sketch, "E1836", {"start": v(60.26, 7.3) * mm, "end": v(60.26, 7.3) * mm});
            skLineSegment(sketch, "E1837", {"start": v(60.26, 7.3) * mm, "end": v(60.26, 7.29) * mm});
            skLineSegment(sketch, "E1838", {"start": v(60.26, 7.29) * mm, "end": v(60.26, 7.27) * mm});
            skLineSegment(sketch, "E1839", {"start": v(60.26, 7.27) * mm, "end": v(60.26, 7.26) * mm});
            skLineSegment(sketch, "E1840", {"start": v(60.26, 7.26) * mm, "end": v(60.26, 7.23) * mm});
            skLineSegment(sketch, "E1841", {"start": v(60.26, 7.23) * mm, "end": v(60.26, 7.21) * mm});
            skLineSegment(sketch, "E1842", {"start": v(60.26, 7.21) * mm, "end": v(60.26, 7.19) * mm});
            skLineSegment(sketch, "E1843", {"start": v(60.26, 7.19) * mm, "end": v(60.25, 7.17) * mm});
            skLineSegment(sketch, "E1844", {"start": v(60.25, 7.17) * mm, "end": v(60.25, 7.15) * mm});
            skLineSegment(sketch, "E1845", {"start": v(60.25, 7.15) * mm, "end": v(60.24, 7.13) * mm});
            skLineSegment(sketch, "E1846", {"start": v(60.24, 7.13) * mm, "end": v(60.24, 7.11) * mm});
            skLineSegment(sketch, "E1847", {"start": v(60.24, 7.11) * mm, "end": v(60.23, 7.1) * mm});
            skLineSegment(sketch, "E1848", {"start": v(60.23, 7.1) * mm, "end": v(60.22, 7.1) * mm});
            skLineSegment(sketch, "E1849", {"start": v(60.22, 7.1) * mm, "end": v(60.21, 7.1) * mm});
            skLineSegment(sketch, "E1850", {"start": v(60.21, 7.1) * mm, "end": v(60.2, 7.1) * mm});
            skLineSegment(sketch, "E1851", {"start": v(60.2, 7.1) * mm, "end": v(60.19, 7.12) * mm});
            skLineSegment(sketch, "E1852", {"start": v(60.19, 7.12) * mm, "end": v(60.18, 7.14) * mm});
            skLineSegment(sketch, "E1853", {"start": v(60.18, 7.14) * mm, "end": v(60.17, 7.18) * mm});
            skLineSegment(sketch, "E1854", {"start": v(60.17, 7.18) * mm, "end": v(60.16, 7.23) * mm});
            skLineSegment(sketch, "E1855", {"start": v(60.16, 7.23) * mm, "end": v(60.15, 7.28) * mm});
            skLineSegment(sketch, "E1856", {"start": v(60.15, 7.28) * mm, "end": v(60.14, 7.35) * mm});
            skLineSegment(sketch, "E1857", {"start": v(60.14, 7.35) * mm, "end": v(60.13, 7.39) * mm});
            skLineSegment(sketch, "E1858", {"start": v(60.13, 7.39) * mm, "end": v(60.12, 7.42) * mm});
            skLineSegment(sketch, "E1859", {"start": v(60.12, 7.42) * mm, "end": v(60.1, 7.46) * mm});
            skLineSegment(sketch, "E1860", {"start": v(60.1, 7.46) * mm, "end": v(60.08, 7.49) * mm});
            skLineSegment(sketch, "E1861", {"start": v(60.08, 7.49) * mm, "end": v(60.05, 7.5) * mm});
            skLineSegment(sketch, "E1862", {"start": v(60.05, 7.5) * mm, "end": v(60.03, 7.52) * mm});
            skLineSegment(sketch, "E1863", {"start": v(60.03, 7.52) * mm, "end": v(60, 7.53) * mm});
            skLineSegment(sketch, "E1864", {"start": v(60, 7.53) * mm, "end": v(59.99, 7.52) * mm});
            skLineSegment(sketch, "E1865", {"start": v(59.99, 7.52) * mm, "end": v(59.98, 7.5) * mm});
            skLineSegment(sketch, "E1866", {"start": v(59.98, 7.5) * mm, "end": v(59.98, 7.5) * mm});
            skLineSegment(sketch, "E1867", {"start": v(59.98, 7.5) * mm, "end": v(59.99, 7.47) * mm});
            skLineSegment(sketch, "E1868", {"start": v(59.99, 7.47) * mm, "end": v(59.99, 7.44) * mm});
            skLineSegment(sketch, "E1869", {"start": v(59.99, 7.44) * mm, "end": v(60, 7.41) * mm});
            skLineSegment(sketch, "E1870", {"start": v(60, 7.41) * mm, "end": v(60, 7.38) * mm});
            skLineSegment(sketch, "E1871", {"start": v(60, 7.38) * mm, "end": v(60.01, 7.34) * mm});
            skLineSegment(sketch, "E1872", {"start": v(60.01, 7.34) * mm, "end": v(60.02, 7.3) * mm});
            skLineSegment(sketch, "E1873", {"start": v(60.02, 7.3) * mm, "end": v(60.03, 7.25) * mm});
            skLineSegment(sketch, "E1874", {"start": v(60.03, 7.25) * mm, "end": v(60.04, 7.21) * mm});
            skLineSegment(sketch, "E1875", {"start": v(60.04, 7.21) * mm, "end": v(60.05, 7.18) * mm});
            skLineSegment(sketch, "E1876", {"start": v(60.05, 7.18) * mm, "end": v(60.05, 7.15) * mm});
            skLineSegment(sketch, "E1877", {"start": v(60.05, 7.15) * mm, "end": v(60.06, 7.13) * mm});
            skLineSegment(sketch, "E1878", {"start": v(60.06, 7.13) * mm, "end": v(60.06, 7.1) * mm});
            skLineSegment(sketch, "E1879", {"start": v(60.06, 7.1) * mm, "end": v(60.06, 7.1) * mm});
            skLineSegment(sketch, "E1880", {"start": v(60.06, 7.1) * mm, "end": v(60.06, 7.09) * mm});
            skLineSegment(sketch, "E1881", {"start": v(60.06, 7.09) * mm, "end": v(60.05, 7.09) * mm});
            skLineSegment(sketch, "E1882", {"start": v(60.05, 7.09) * mm, "end": v(60.04, 7.1) * mm});
            skLineSegment(sketch, "E1883", {"start": v(60.04, 7.1) * mm, "end": v(60.03, 7.1) * mm});
            skLineSegment(sketch, "E1884", {"start": v(60.03, 7.1) * mm, "end": v(60.02, 7.12) * mm});
            skLineSegment(sketch, "E1885", {"start": v(60.02, 7.12) * mm, "end": v(60.01, 7.14) * mm});
            skLineSegment(sketch, "E1886", {"start": v(60.01, 7.14) * mm, "end": v(60, 7.17) * mm});
            skLineSegment(sketch, "E1887", {"start": v(60, 7.17) * mm, "end": v(59.98, 7.2) * mm});
            skLineSegment(sketch, "E1888", {"start": v(59.98, 7.2) * mm, "end": v(59.96, 7.25) * mm});
            skLineSegment(sketch, "E1889", {"start": v(59.96, 7.25) * mm, "end": v(59.95, 7.28) * mm});
            skLineSegment(sketch, "E1890", {"start": v(59.95, 7.28) * mm, "end": v(59.93, 7.33) * mm});
            skLineSegment(sketch, "E1891", {"start": v(59.93, 7.33) * mm, "end": v(59.9, 7.37) * mm});
            skLineSegment(sketch, "E1892", {"start": v(59.9, 7.37) * mm, "end": v(59.88, 7.4) * mm});
            skLineSegment(sketch, "E1893", {"start": v(59.88, 7.4) * mm, "end": v(59.85, 7.45) * mm});
            skLineSegment(sketch, "E1894", {"start": v(59.85, 7.45) * mm, "end": v(59.83, 7.48) * mm});
            skLineSegment(sketch, "E1895", {"start": v(59.83, 7.48) * mm, "end": v(59.8, 7.52) * mm});
            skLineSegment(sketch, "E1896", {"start": v(59.8, 7.52) * mm, "end": v(59.78, 7.54) * mm});
            skLineSegment(sketch, "E1897", {"start": v(59.78, 7.54) * mm, "end": v(59.76, 7.56) * mm});
            skLineSegment(sketch, "E1898", {"start": v(59.76, 7.56) * mm, "end": v(59.74, 7.58) * mm});
            skLineSegment(sketch, "E1899", {"start": v(59.74, 7.58) * mm, "end": v(59.73, 7.6) * mm});
            skLineSegment(sketch, "E1900", {"start": v(59.73, 7.6) * mm, "end": v(59.71, 7.61) * mm});
            skLineSegment(sketch, "E1901", {"start": v(59.71, 7.61) * mm, "end": v(59.7, 7.63) * mm});
            skLineSegment(sketch, "E1902", {"start": v(59.7, 7.63) * mm, "end": v(59.7, 7.64) * mm});
            skLineSegment(sketch, "E1903", {"start": v(59.7, 7.64) * mm, "end": v(59.69, 7.66) * mm});
            skLineSegment(sketch, "E1904", {"start": v(59.69, 7.66) * mm, "end": v(59.68, 7.68) * mm});
            skLineSegment(sketch, "E1905", {"start": v(59.68, 7.68) * mm, "end": v(59.68, 7.7) * mm});
            skLineSegment(sketch, "E1906", {"start": v(59.68, 7.7) * mm, "end": v(59.68, 7.71) * mm});
            skLineSegment(sketch, "E1907", {"start": v(59.68, 7.71) * mm, "end": v(59.68, 7.73) * mm});
            skLineSegment(sketch, "E1908", {"start": v(59.68, 7.73) * mm, "end": v(59.68, 7.76) * mm});
            skLineSegment(sketch, "E1909", {"start": v(59.68, 7.76) * mm, "end": v(59.68, 7.79) * mm});
            skLineSegment(sketch, "E1910", {"start": v(59.68, 7.79) * mm, "end": v(59.68, 7.82) * mm});
            skLineSegment(sketch, "E1911", {"start": v(59.68, 7.82) * mm, "end": v(59.69, 7.85) * mm});
            skLineSegment(sketch, "E1912", {"start": v(59.69, 7.85) * mm, "end": v(59.7, 7.9) * mm});
            skLineSegment(sketch, "E1913", {"start": v(59.7, 7.9) * mm, "end": v(59.7, 7.95) * mm});
            skLineSegment(sketch, "E1914", {"start": v(59.7, 7.95) * mm, "end": v(59.7, 8) * mm});
            skLineSegment(sketch, "E1915", {"start": v(59.7, 8) * mm, "end": v(59.7, 8.04) * mm});
            skLineSegment(sketch, "E1916", {"start": v(59.7, 8.04) * mm, "end": v(59.7, 8.06) * mm});
            skLineSegment(sketch, "E1917", {"start": v(59.7, 8.06) * mm, "end": v(59.7, 8.08) * mm});
            skLineSegment(sketch, "E1918", {"start": v(59.7, 8.08) * mm, "end": v(59.7, 8.1) * mm});
            skLineSegment(sketch, "E1919", {"start": v(59.7, 8.1) * mm, "end": v(59.69, 8.1) * mm});
            skLineSegment(sketch, "E1920", {"start": v(59.69, 8.1) * mm, "end": v(59.67, 8.1) * mm});
            skLineSegment(sketch, "E1921", {"start": v(59.67, 8.1) * mm, "end": v(59.66, 8.09) * mm});
            skLineSegment(sketch, "E1922", {"start": v(59.66, 8.09) * mm, "end": v(59.66, 8.09) * mm});
            skLineSegment(sketch, "E1923", {"start": v(59.66, 8.09) * mm, "end": v(59.65, 8.1) * mm});
            skLineSegment(sketch, "E1924", {"start": v(59.65, 8.1) * mm, "end": v(59.65, 8.1) * mm});
            skLineSegment(sketch, "E1925", {"start": v(59.65, 8.1) * mm, "end": v(59.65, 8.12) * mm});
            skLineSegment(sketch, "E1926", {"start": v(59.65, 8.12) * mm, "end": v(59.65, 8.14) * mm});
            skLineSegment(sketch, "E1927", {"start": v(59.65, 8.14) * mm, "end": v(59.66, 8.16) * mm});
            skLineSegment(sketch, "E1928", {"start": v(59.66, 8.16) * mm, "end": v(59.66, 8.2) * mm});
            skLineSegment(sketch, "E1929", {"start": v(59.66, 8.2) * mm, "end": v(59.66, 8.23) * mm});
            skLineSegment(sketch, "E1930", {"start": v(59.66, 8.23) * mm, "end": v(59.66, 8.25) * mm});
            skLineSegment(sketch, "E1931", {"start": v(59.66, 8.25) * mm, "end": v(59.65, 8.26) * mm});
            skLineSegment(sketch, "E1932", {"start": v(59.65, 8.26) * mm, "end": v(59.64, 8.25) * mm});
            skLineSegment(sketch, "E1933", {"start": v(59.64, 8.25) * mm, "end": v(59.63, 8.24) * mm});
            skLineSegment(sketch, "E1934", {"start": v(59.63, 8.24) * mm, "end": v(59.62, 8.21) * mm});
            skLineSegment(sketch, "E1935", {"start": v(59.62, 8.21) * mm, "end": v(59.61, 8.18) * mm});
            skLineSegment(sketch, "E1936", {"start": v(59.61, 8.18) * mm, "end": v(59.6, 8.14) * mm});
            skLineSegment(sketch, "E1937", {"start": v(59.6, 8.14) * mm, "end": v(59.6, 8.09) * mm});
            skLineSegment(sketch, "E1938", {"start": v(59.6, 8.09) * mm, "end": v(59.58, 8.04) * mm});
            skLineSegment(sketch, "E1939", {"start": v(59.58, 8.04) * mm, "end": v(59.57, 7.98) * mm});
            skLineSegment(sketch, "E1940", {"start": v(59.57, 7.98) * mm, "end": v(59.56, 7.93) * mm});
            skLineSegment(sketch, "E1941", {"start": v(59.56, 7.93) * mm, "end": v(59.56, 7.87) * mm});
            skLineSegment(sketch, "E1942", {"start": v(59.56, 7.87) * mm, "end": v(59.55, 7.82) * mm});
            skLineSegment(sketch, "E1943", {"start": v(59.55, 7.82) * mm, "end": v(59.53, 7.78) * mm});
            skLineSegment(sketch, "E1944", {"start": v(59.53, 7.78) * mm, "end": v(59.52, 7.74) * mm});
            skLineSegment(sketch, "E1945", {"start": v(59.52, 7.74) * mm, "end": v(59.5, 7.7) * mm});
            skLineSegment(sketch, "E1946", {"start": v(59.5, 7.7) * mm, "end": v(59.5, 7.67) * mm});
            skLineSegment(sketch, "E1947", {"start": v(59.5, 7.67) * mm, "end": v(59.48, 7.63) * mm});
            skLineSegment(sketch, "E1948", {"start": v(59.48, 7.63) * mm, "end": v(59.46, 7.6) * mm});
            skLineSegment(sketch, "E1949", {"start": v(59.46, 7.6) * mm, "end": v(59.44, 7.58) * mm});
            skLineSegment(sketch, "E1950", {"start": v(59.44, 7.58) * mm, "end": v(59.42, 7.55) * mm});
            skLineSegment(sketch, "E1951", {"start": v(59.42, 7.55) * mm, "end": v(59.4, 7.53) * mm});
            skLineSegment(sketch, "E1952", {"start": v(59.4, 7.53) * mm, "end": v(59.37, 7.5) * mm});
            skLineSegment(sketch, "E1953", {"start": v(59.37, 7.5) * mm, "end": v(59.35, 7.48) * mm});
            skLineSegment(sketch, "E1954", {"start": v(59.35, 7.48) * mm, "end": v(59.32, 7.46) * mm});
            skLineSegment(sketch, "E1955", {"start": v(59.32, 7.46) * mm, "end": v(59.29, 7.44) * mm});
            skLineSegment(sketch, "E1956", {"start": v(59.29, 7.44) * mm, "end": v(59.25, 7.41) * mm});
            skLineSegment(sketch, "E1957", {"start": v(59.25, 7.41) * mm, "end": v(59.21, 7.38) * mm});
            skLineSegment(sketch, "E1958", {"start": v(59.21, 7.38) * mm, "end": v(59.18, 7.35) * mm});
            skLineSegment(sketch, "E1959", {"start": v(59.18, 7.35) * mm, "end": v(59.15, 7.31) * mm});
            skLineSegment(sketch, "E1960", {"start": v(59.15, 7.31) * mm, "end": v(59.13, 7.27) * mm});
            skLineSegment(sketch, "E1961", {"start": v(59.13, 7.27) * mm, "end": v(59.12, 7.23) * mm});
            skLineSegment(sketch, "E1962", {"start": v(59.12, 7.23) * mm, "end": v(59.1, 7.18) * mm});
            skLineSegment(sketch, "E1963", {"start": v(59.1, 7.18) * mm, "end": v(59.1, 7.14) * mm});
            skLineSegment(sketch, "E1964", {"start": v(59.1, 7.14) * mm, "end": v(59.1, 7.1) * mm});
            skLineSegment(sketch, "E1965", {"start": v(59.1, 7.1) * mm, "end": v(59.1, 7.04) * mm});
            skLineSegment(sketch, "E1966", {"start": v(59.1, 7.04) * mm, "end": v(59.1, 7) * mm});
            skLineSegment(sketch, "E1967", {"start": v(59.1, 7) * mm, "end": v(59.11, 6.95) * mm});
            skLineSegment(sketch, "E1968", {"start": v(59.11, 6.95) * mm, "end": v(59.13, 6.9) * mm});
            skLineSegment(sketch, "E1969", {"start": v(59.13, 6.9) * mm, "end": v(59.15, 6.86) * mm});
            skLineSegment(sketch, "E1970", {"start": v(59.15, 6.86) * mm, "end": v(59.17, 6.81) * mm});
            skLineSegment(sketch, "E1971", {"start": v(59.17, 6.81) * mm, "end": v(59.2, 6.77) * mm});
            skLineSegment(sketch, "E1972", {"start": v(59.2, 6.77) * mm, "end": v(59.22, 6.75) * mm});
            skLineSegment(sketch, "E1973", {"start": v(59.22, 6.75) * mm, "end": v(59.23, 6.74) * mm});
            skLineSegment(sketch, "E1974", {"start": v(59.23, 6.74) * mm, "end": v(59.25, 6.72) * mm});
            skLineSegment(sketch, "E1975", {"start": v(59.25, 6.72) * mm, "end": v(59.26, 6.71) * mm});
            skLineSegment(sketch, "E1976", {"start": v(59.26, 6.71) * mm, "end": v(59.28, 6.7) * mm});
            skLineSegment(sketch, "E1977", {"start": v(59.28, 6.7) * mm, "end": v(59.3, 6.69) * mm});
            skLineSegment(sketch, "E1978", {"start": v(59.3, 6.69) * mm, "end": v(59.32, 6.67) * mm});
            skLineSegment(sketch, "E1979", {"start": v(59.32, 6.67) * mm, "end": v(59.35, 6.66) * mm});
            skLineSegment(sketch, "E1980", {"start": v(59.35, 6.66) * mm, "end": v(59.38, 6.65) * mm});
            skLineSegment(sketch, "E1981", {"start": v(59.38, 6.65) * mm, "end": v(59.41, 6.64) * mm});
            skLineSegment(sketch, "E1982", {"start": v(59.41, 6.64) * mm, "end": v(59.45, 6.63) * mm});
            skLineSegment(sketch, "E1983", {"start": v(59.45, 6.63) * mm, "end": v(59.49, 6.61) * mm});
            skLineSegment(sketch, "E1984", {"start": v(59.49, 6.61) * mm, "end": v(59.53, 6.6) * mm});
            skLineSegment(sketch, "E1985", {"start": v(59.53, 6.6) * mm, "end": v(59.58, 6.58) * mm});
            skLineSegment(sketch, "E1986", {"start": v(59.58, 6.58) * mm, "end": v(59.63, 6.57) * mm});
            skLineSegment(sketch, "E1987", {"start": v(59.63, 6.57) * mm, "end": v(59.69, 6.55) * mm});
            skLineSegment(sketch, "E1988", {"start": v(59.69, 6.55) * mm, "end": v(59.9, 6.49) * mm});
            skLineSegment(sketch, "E1989", {"start": v(59.9, 6.49) * mm, "end": v(60.12, 6.4) * mm});
            skLineSegment(sketch, "E1990", {"start": v(60.12, 6.4) * mm, "end": v(60.34, 6.32) * mm});
            skLineSegment(sketch, "E1991", {"start": v(60.34, 6.32) * mm, "end": v(60.55, 6.22) * mm});
            skLineSegment(sketch, "E1992", {"start": v(60.55, 6.22) * mm, "end": v(60.75, 6.1) * mm});
            skLineSegment(sketch, "E1993", {"start": v(60.75, 6.1) * mm, "end": v(60.95, 5.98) * mm});
            skLineSegment(sketch, "E1994", {"start": v(60.95, 5.98) * mm, "end": v(61.15, 5.84) * mm});
            skLineSegment(sketch, "E1995", {"start": v(61.15, 5.84) * mm, "end": v(61.34, 5.7) * mm});
            skLineSegment(sketch, "E1996", {"start": v(61.34, 5.7) * mm, "end": v(61.38, 5.66) * mm});
            skLineSegment(sketch, "E1997", {"start": v(61.38, 5.66) * mm, "end": v(61.44, 5.62) * mm});
            skLineSegment(sketch, "E1998", {"start": v(61.44, 5.62) * mm, "end": v(61.5, 5.58) * mm});
            skLineSegment(sketch, "E1999", {"start": v(61.5, 5.58) * mm, "end": v(61.58, 5.53) * mm});
            skLineSegment(sketch, "E2000", {"start": v(61.58, 5.53) * mm, "end": v(61.65, 5.48) * mm});
            skLineSegment(sketch, "E2001", {"start": v(61.65, 5.48) * mm, "end": v(61.73, 5.43) * mm});
            skLineSegment(sketch, "E2002", {"start": v(61.73, 5.43) * mm, "end": v(61.8, 5.39) * mm});
            skLineSegment(sketch, "E2003", {"start": v(61.8, 5.39) * mm, "end": v(61.88, 5.34) * mm});
            skLineSegment(sketch, "E2004", {"start": v(61.88, 5.34) * mm, "end": v(61.99, 5.28) * mm});
            skLineSegment(sketch, "E2005", {"start": v(61.99, 5.28) * mm, "end": v(62.08, 5.23) * mm});
            skLineSegment(sketch, "E2006", {"start": v(62.08, 5.23) * mm, "end": v(62.17, 5.17) * mm});
            skLineSegment(sketch, "E2007", {"start": v(62.17, 5.17) * mm, "end": v(62.25, 5.12) * mm});
            skLineSegment(sketch, "E2008", {"start": v(62.25, 5.12) * mm, "end": v(62.33, 5.07) * mm});
            skLineSegment(sketch, "E2009", {"start": v(62.33, 5.07) * mm, "end": v(62.4, 5.02) * mm});
            skLineSegment(sketch, "E2010", {"start": v(62.4, 5.02) * mm, "end": v(62.46, 4.98) * mm});
            skLineSegment(sketch, "E2011", {"start": v(62.46, 4.98) * mm, "end": v(62.52, 4.93) * mm});
            skLineSegment(sketch, "E2012", {"start": v(62.52, 4.93) * mm, "end": v(62.57, 4.9) * mm});
            skLineSegment(sketch, "E2013", {"start": v(62.57, 4.9) * mm, "end": v(62.61, 4.85) * mm});
            skLineSegment(sketch, "E2014", {"start": v(62.61, 4.85) * mm, "end": v(62.65, 4.81) * mm});
            skLineSegment(sketch, "E2015", {"start": v(62.65, 4.81) * mm, "end": v(62.69, 4.77) * mm});
            skLineSegment(sketch, "E2016", {"start": v(62.69, 4.77) * mm, "end": v(62.71, 4.74) * mm});
            skLineSegment(sketch, "E2017", {"start": v(62.71, 4.74) * mm, "end": v(62.74, 4.7) * mm});
            skLineSegment(sketch, "E2018", {"start": v(62.74, 4.7) * mm, "end": v(62.75, 4.67) * mm});
            skLineSegment(sketch, "E2019", {"start": v(62.75, 4.67) * mm, "end": v(62.77, 4.63) * mm});
            skLineSegment(sketch, "E2020", {"start": v(62.77, 4.63) * mm, "end": v(62.78, 4.55) * mm});
            skLineSegment(sketch, "E2021", {"start": v(62.78, 4.55) * mm, "end": v(62.79, 4.47) * mm});
            skLineSegment(sketch, "E2022", {"start": v(62.79, 4.47) * mm, "end": v(62.78, 4.37) * mm});
            skLineSegment(sketch, "E2023", {"start": v(62.78, 4.37) * mm, "end": v(62.77, 4.28) * mm});
            skLineSegment(sketch, "E2024", {"start": v(62.77, 4.28) * mm, "end": v(62.75, 4.19) * mm});
            skLineSegment(sketch, "E2025", {"start": v(62.75, 4.19) * mm, "end": v(62.71, 4.1) * mm});
            skLineSegment(sketch, "E2026", {"start": v(62.71, 4.1) * mm, "end": v(62.67, 4) * mm});
            skLineSegment(sketch, "E2027", {"start": v(62.67, 4) * mm, "end": v(62.62, 3.92) * mm});
            skLineSegment(sketch, "E2028", {"start": v(62.62, 3.92) * mm, "end": v(62.59, 3.88) * mm});
            skLineSegment(sketch, "E2029", {"start": v(62.59, 3.88) * mm, "end": v(62.54, 3.82) * mm});
            skLineSegment(sketch, "E2030", {"start": v(62.54, 3.82) * mm, "end": v(62.49, 3.76) * mm});
            skLineSegment(sketch, "E2031", {"start": v(62.49, 3.76) * mm, "end": v(62.43, 3.7) * mm});
            skLineSegment(sketch, "E2032", {"start": v(62.43, 3.7) * mm, "end": v(62.36, 3.62) * mm});
            skLineSegment(sketch, "E2033", {"start": v(62.36, 3.62) * mm, "end": v(62.29, 3.54) * mm});
            skLineSegment(sketch, "E2034", {"start": v(62.29, 3.54) * mm, "end": v(62.21, 3.47) * mm});
            skLineSegment(sketch, "E2035", {"start": v(62.21, 3.47) * mm, "end": v(62.13, 3.39) * mm});
            skLineSegment(sketch, "E2036", {"start": v(62.13, 3.39) * mm, "end": v(62.05, 3.31) * mm});
            skLineSegment(sketch, "E2037", {"start": v(62.05, 3.31) * mm, "end": v(61.97, 3.24) * mm});
            skLineSegment(sketch, "E2038", {"start": v(61.97, 3.24) * mm, "end": v(61.9, 3.16) * mm});
            skLineSegment(sketch, "E2039", {"start": v(61.9, 3.16) * mm, "end": v(61.82, 3.1) * mm});
            skLineSegment(sketch, "E2040", {"start": v(61.82, 3.1) * mm, "end": v(61.75, 3.04) * mm});
            skLineSegment(sketch, "E2041", {"start": v(61.75, 3.04) * mm, "end": v(61.69, 2.98) * mm});
            skLineSegment(sketch, "E2042", {"start": v(61.69, 2.98) * mm, "end": v(61.63, 2.94) * mm});
            skLineSegment(sketch, "E2043", {"start": v(61.63, 2.94) * mm, "end": v(61.58, 2.9) * mm});
            skLineSegment(sketch, "E2044", {"start": v(61.58, 2.9) * mm, "end": v(61.54, 2.88) * mm});
            skLineSegment(sketch, "E2045", {"start": v(61.54, 2.88) * mm, "end": v(61.5, 2.85) * mm});
            skLineSegment(sketch, "E2046", {"start": v(61.5, 2.85) * mm, "end": v(61.47, 2.82) * mm});
            skLineSegment(sketch, "E2047", {"start": v(61.47, 2.82) * mm, "end": v(61.44, 2.8) * mm});
            skLineSegment(sketch, "E2048", {"start": v(61.44, 2.8) * mm, "end": v(61.4, 2.76) * mm});
            skLineSegment(sketch, "E2049", {"start": v(61.4, 2.76) * mm, "end": v(61.38, 2.73) * mm});
            skLineSegment(sketch, "E2050", {"start": v(61.38, 2.73) * mm, "end": v(61.35, 2.7) * mm});
            skLineSegment(sketch, "E2051", {"start": v(61.35, 2.7) * mm, "end": v(61.32, 2.66) * mm});
            skLineSegment(sketch, "E2052", {"start": v(61.32, 2.66) * mm, "end": v(61.29, 2.62) * mm});
            skLineSegment(sketch, "E2053", {"start": v(61.29, 2.62) * mm, "end": v(61.25, 2.58) * mm});
            skLineSegment(sketch, "E2054", {"start": v(61.25, 2.58) * mm, "end": v(61.22, 2.53) * mm});
            skLineSegment(sketch, "E2055", {"start": v(61.22, 2.53) * mm, "end": v(61.2, 2.48) * mm});
            skLineSegment(sketch, "E2056", {"start": v(61.2, 2.48) * mm, "end": v(61.16, 2.43) * mm});
            skLineSegment(sketch, "E2057", {"start": v(61.16, 2.43) * mm, "end": v(61.12, 2.37) * mm});
            skLineSegment(sketch, "E2058", {"start": v(61.12, 2.37) * mm, "end": v(61.09, 2.31) * mm});
            skLineSegment(sketch, "E2059", {"start": v(61.09, 2.31) * mm, "end": v(61.05, 2.25) * mm});
            skLineSegment(sketch, "E2060", {"start": v(61.05, 2.25) * mm, "end": v(61.02, 2.2) * mm});
            skLineSegment(sketch, "E2061", {"start": v(61.02, 2.2) * mm, "end": v(61, 2.15) * mm});
            skLineSegment(sketch, "E2062", {"start": v(61, 2.15) * mm, "end": v(60.96, 2.1) * mm});
            skLineSegment(sketch, "E2063", {"start": v(60.96, 2.1) * mm, "end": v(60.91, 2.05) * mm});
            skLineSegment(sketch, "E2064", {"start": v(60.91, 2.05) * mm, "end": v(60.87, 2) * mm});
            skLineSegment(sketch, "E2065", {"start": v(60.87, 2) * mm, "end": v(60.83, 1.95) * mm});
            skLineSegment(sketch, "E2066", {"start": v(60.83, 1.95) * mm, "end": v(60.78, 1.9) * mm});
            skLineSegment(sketch, "E2067", {"start": v(60.78, 1.9) * mm, "end": v(60.73, 1.85) * mm});
            skLineSegment(sketch, "E2068", {"start": v(60.73, 1.85) * mm, "end": v(60.69, 1.8) * mm});
            skLineSegment(sketch, "E2069", {"start": v(60.69, 1.8) * mm, "end": v(60.64, 1.77) * mm});
            skLineSegment(sketch, "E2070", {"start": v(60.64, 1.77) * mm, "end": v(60.6, 1.73) * mm});
            skLineSegment(sketch, "E2071", {"start": v(60.6, 1.73) * mm, "end": v(60.56, 1.7) * mm});
            skLineSegment(sketch, "E2072", {"start": v(60.56, 1.7) * mm, "end": v(60.52, 1.67) * mm});
            skLineSegment(sketch, "E2073", {"start": v(60.52, 1.67) * mm, "end": v(60.48, 1.65) * mm});
            skLineSegment(sketch, "E2074", {"start": v(60.48, 1.65) * mm, "end": v(60.46, 1.64) * mm});
            skLineSegment(sketch, "E2075", {"start": v(60.46, 1.64) * mm, "end": v(60.43, 1.64) * mm});
            skLineSegment(sketch, "E2076", {"start": v(60.43, 1.64) * mm, "end": v(60.41, 1.64) * mm});
            skLineSegment(sketch, "E2077", {"start": v(60.41, 1.64) * mm, "end": v(60.4, 1.64) * mm});
            skLineSegment(sketch, "E2078", {"start": v(60.4, 1.64) * mm, "end": v(60.39, 1.63) * mm});
            skLineSegment(sketch, "E2079", {"start": v(60.39, 1.63) * mm, "end": v(60.38, 1.62) * mm});
            skLineSegment(sketch, "E2080", {"start": v(60.38, 1.62) * mm, "end": v(60.37, 1.61) * mm});
            skLineSegment(sketch, "E2081", {"start": v(60.37, 1.61) * mm, "end": v(60.37, 1.6) * mm});
            skLineSegment(sketch, "E2082", {"start": v(60.37, 1.6) * mm, "end": v(60.37, 1.59) * mm});
            skLineSegment(sketch, "E2083", {"start": v(60.37, 1.59) * mm, "end": v(60.37, 1.57) * mm});
            skLineSegment(sketch, "E2084", {"start": v(60.37, 1.57) * mm, "end": v(60.38, 1.54) * mm});
            skLineSegment(sketch, "E2085", {"start": v(60.38, 1.54) * mm, "end": v(60.39, 1.52) * mm});
            skLineSegment(sketch, "E2086", {"start": v(60.39, 1.52) * mm, "end": v(60.4, 1.48) * mm});
            skLineSegment(sketch, "E2087", {"start": v(60.4, 1.48) * mm, "end": v(60.42, 1.45) * mm});
            skLineSegment(sketch, "E2088", {"start": v(60.42, 1.45) * mm, "end": v(60.44, 1.4) * mm});
            skLineSegment(sketch, "E2089", {"start": v(60.44, 1.4) * mm, "end": v(60.47, 1.36) * mm});
            skLineSegment(sketch, "E2090", {"start": v(60.47, 1.36) * mm, "end": v(60.5, 1.3) * mm});
            skLineSegment(sketch, "E2091", {"start": v(60.5, 1.3) * mm, "end": v(60.53, 1.24) * mm});
            skLineSegment(sketch, "E2092", {"start": v(60.53, 1.24) * mm, "end": v(60.58, 1.16) * mm});
            skLineSegment(sketch, "E2093", {"start": v(60.58, 1.16) * mm, "end": v(60.62, 1.08) * mm});
            skLineSegment(sketch, "E2094", {"start": v(60.62, 1.08) * mm, "end": v(60.66, 1) * mm});
            skLineSegment(sketch, "E2095", {"start": v(60.66, 1) * mm, "end": v(60.7, 0.94) * mm});
            skLineSegment(sketch, "E2096", {"start": v(60.7, 0.94) * mm, "end": v(60.73, 0.87) * mm});
            skLineSegment(sketch, "E2097", {"start": v(60.73, 0.87) * mm, "end": v(60.75, 0.8) * mm});
            skLineSegment(sketch, "E2098", {"start": v(60.75, 0.8) * mm, "end": v(60.78, 0.74) * mm});
            skLineSegment(sketch, "E2099", {"start": v(60.78, 0.74) * mm, "end": v(60.8, 0.68) * mm});
            skLineSegment(sketch, "E2100", {"start": v(60.8, 0.68) * mm, "end": v(60.81, 0.61) * mm});
            skLineSegment(sketch, "E2101", {"start": v(60.81, 0.61) * mm, "end": v(60.83, 0.55) * mm});
            skLineSegment(sketch, "E2102", {"start": v(60.83, 0.55) * mm, "end": v(60.84, 0.5) * mm});
            skLineSegment(sketch, "E2103", {"start": v(60.84, 0.5) * mm, "end": v(60.85, 0.43) * mm});
            skLineSegment(sketch, "E2104", {"start": v(60.85, 0.43) * mm, "end": v(60.86, 0.36) * mm});
            skLineSegment(sketch, "E2105", {"start": v(60.86, 0.36) * mm, "end": v(60.86, 0.3) * mm});
            skLineSegment(sketch, "E2106", {"start": v(60.86, 0.3) * mm, "end": v(60.86, 0.23) * mm});
            skLineSegment(sketch, "E2107", {"start": v(60.86, 0.23) * mm, "end": v(60.86, 0.16) * mm});
            skLineSegment(sketch, "E2108", {"start": v(60.86, 0.16) * mm, "end": v(60.86, 0.07) * mm});
            skLineSegment(sketch, "E2109", {"start": v(60.86, 0.07) * mm, "end": v(60.86, 0) * mm});
            skLineSegment(sketch, "E2110", {"start": v(60.86, 0) * mm, "end": v(60.85, -0.07) * mm});
            skLineSegment(sketch, "E2111", {"start": v(60.85, -0.07) * mm, "end": v(60.85, -0.13) * mm});
            skLineSegment(sketch, "E2112", {"start": v(60.85, -0.13) * mm, "end": v(60.83, -0.18) * mm});
            skLineSegment(sketch, "E2113", {"start": v(60.83, -0.18) * mm, "end": v(60.82, -0.23) * mm});
            skLineSegment(sketch, "E2114", {"start": v(60.82, -0.23) * mm, "end": v(60.8, -0.29) * mm});
            skLineSegment(sketch, "E2115", {"start": v(60.8, -0.29) * mm, "end": v(60.78, -0.34) * mm});
            skLineSegment(sketch, "E2116", {"start": v(60.78, -0.34) * mm, "end": v(60.76, -0.38) * mm});
            skLineSegment(sketch, "E2117", {"start": v(60.76, -0.38) * mm, "end": v(60.75, -0.42) * mm});
            skLineSegment(sketch, "E2118", {"start": v(60.75, -0.42) * mm, "end": v(60.73, -0.46) * mm});
            skLineSegment(sketch, "E2119", {"start": v(60.73, -0.46) * mm, "end": v(60.72, -0.5) * mm});
            skLineSegment(sketch, "E2120", {"start": v(60.72, -0.5) * mm, "end": v(60.72, -0.53) * mm});
            skLineSegment(sketch, "E2121", {"start": v(60.72, -0.53) * mm, "end": v(60.7, -0.56) * mm});
            skLineSegment(sketch, "E2122", {"start": v(60.7, -0.56) * mm, "end": v(60.7, -0.6) * mm});
            skLineSegment(sketch, "E2123", {"start": v(60.7, -0.6) * mm, "end": v(60.7, -0.62) * mm});
            skLineSegment(sketch, "E2124", {"start": v(60.7, -0.62) * mm, "end": v(60.71, -0.65) * mm});
            skLineSegment(sketch, "E2125", {"start": v(60.71, -0.65) * mm, "end": v(60.72, -0.68) * mm});
            skLineSegment(sketch, "E2126", {"start": v(60.72, -0.68) * mm, "end": v(60.73, -0.71) * mm});
            skLineSegment(sketch, "E2127", {"start": v(60.73, -0.71) * mm, "end": v(60.74, -0.74) * mm});
            skLineSegment(sketch, "E2128", {"start": v(60.74, -0.74) * mm, "end": v(60.75, -0.78) * mm});
            skLineSegment(sketch, "E2129", {"start": v(60.75, -0.78) * mm, "end": v(60.77, -0.81) * mm});
            skLineSegment(sketch, "E2130", {"start": v(60.77, -0.81) * mm, "end": v(60.8, -0.85) * mm});
            skLineSegment(sketch, "E2131", {"start": v(60.8, -0.85) * mm, "end": v(60.82, -0.9) * mm});
            skLineSegment(sketch, "E2132", {"start": v(60.82, -0.9) * mm, "end": v(60.83, -0.91) * mm});
            skLineSegment(sketch, "E2133", {"start": v(60.83, -0.91) * mm, "end": v(60.85, -0.94) * mm});
            skLineSegment(sketch, "E2134", {"start": v(60.85, -0.94) * mm, "end": v(60.86, -0.98) * mm});
            skLineSegment(sketch, "E2135", {"start": v(60.86, -0.98) * mm, "end": v(60.88, -1.02) * mm});
            skLineSegment(sketch, "E2136", {"start": v(60.88, -1.02) * mm, "end": v(60.9, -1.07) * mm});
            skLineSegment(sketch, "E2137", {"start": v(60.9, -1.07) * mm, "end": v(60.93, -1.12) * mm});
            skLineSegment(sketch, "E2138", {"start": v(60.93, -1.12) * mm, "end": v(60.96, -1.18) * mm});
            skLineSegment(sketch, "E2139", {"start": v(60.96, -1.18) * mm, "end": v(60.98, -1.24) * mm});
            skLineSegment(sketch, "E2140", {"start": v(60.98, -1.24) * mm, "end": v(61.01, -1.3) * mm});
            skLineSegment(sketch, "E2141", {"start": v(61.01, -1.3) * mm, "end": v(61.04, -1.38) * mm});
            skLineSegment(sketch, "E2142", {"start": v(61.04, -1.38) * mm, "end": v(61.07, -1.45) * mm});
            skLineSegment(sketch, "E2143", {"start": v(61.07, -1.45) * mm, "end": v(61.1, -1.52) * mm});
            skLineSegment(sketch, "E2144", {"start": v(61.1, -1.52) * mm, "end": v(61.13, -1.6) * mm});
            skLineSegment(sketch, "E2145", {"start": v(61.13, -1.6) * mm, "end": v(61.16, -1.67) * mm});
            skLineSegment(sketch, "E2146", {"start": v(61.16, -1.67) * mm, "end": v(61.19, -1.74) * mm});
            skLineSegment(sketch, "E2147", {"start": v(61.19, -1.74) * mm, "end": v(61.22, -1.82) * mm});
            skLineSegment(sketch, "E2148", {"start": v(61.22, -1.82) * mm, "end": v(61.28, -2) * mm});
            skLineSegment(sketch, "E2149", {"start": v(61.28, -2) * mm, "end": v(61.35, -2.15) * mm});
            skLineSegment(sketch, "E2150", {"start": v(61.35, -2.15) * mm, "end": v(61.4, -2.29) * mm});
            skLineSegment(sketch, "E2151", {"start": v(61.4, -2.29) * mm, "end": v(61.45, -2.42) * mm});
            skLineSegment(sketch, "E2152", {"start": v(61.45, -2.42) * mm, "end": v(61.5, -2.53) * mm});
            skLineSegment(sketch, "E2153", {"start": v(61.5, -2.53) * mm, "end": v(61.54, -2.63) * mm});
            skLineSegment(sketch, "E2154", {"start": v(61.54, -2.63) * mm, "end": v(61.58, -2.72) * mm});
            skLineSegment(sketch, "E2155", {"start": v(61.58, -2.72) * mm, "end": v(61.61, -2.8) * mm});
            skLineSegment(sketch, "E2156", {"start": v(61.61, -2.8) * mm, "end": v(61.64, -2.87) * mm});
            skLineSegment(sketch, "E2157", {"start": v(61.64, -2.87) * mm, "end": v(61.67, -2.92) * mm});
            skLineSegment(sketch, "E2158", {"start": v(61.67, -2.92) * mm, "end": v(61.7, -2.97) * mm});
            skLineSegment(sketch, "E2159", {"start": v(61.7, -2.97) * mm, "end": v(61.72, -3) * mm});
            skLineSegment(sketch, "E2160", {"start": v(61.72, -3) * mm, "end": v(61.74, -3.04) * mm});
            skLineSegment(sketch, "E2161", {"start": v(61.74, -3.04) * mm, "end": v(61.76, -3.06) * mm});
            skLineSegment(sketch, "E2162", {"start": v(61.76, -3.06) * mm, "end": v(61.78, -3.08) * mm});
            skLineSegment(sketch, "E2163", {"start": v(61.78, -3.08) * mm, "end": v(61.8, -3.1) * mm});
            skLineSegment(sketch, "E2164", {"start": v(61.8, -3.1) * mm, "end": v(61.82, -3.1) * mm});
            skLineSegment(sketch, "E2165", {"start": v(61.82, -3.1) * mm, "end": v(61.85, -3.11) * mm});
            skLineSegment(sketch, "E2166", {"start": v(61.85, -3.11) * mm, "end": v(61.88, -3.12) * mm});
            skLineSegment(sketch, "E2167", {"start": v(61.88, -3.12) * mm, "end": v(61.9, -3.13) * mm});
            skLineSegment(sketch, "E2168", {"start": v(61.9, -3.13) * mm, "end": v(61.94, -3.13) * mm});
            skLineSegment(sketch, "E2169", {"start": v(61.94, -3.13) * mm, "end": v(61.97, -3.13) * mm});
            skLineSegment(sketch, "E2170", {"start": v(61.97, -3.13) * mm, "end": v(62, -3.13) * mm});
            skLineSegment(sketch, "E2171", {"start": v(62, -3.13) * mm, "end": v(62.04, -3.13) * mm});
            skLineSegment(sketch, "E2172", {"start": v(62.04, -3.13) * mm, "end": v(62.08, -3.12) * mm});
            skLineSegment(sketch, "E2173", {"start": v(62.08, -3.12) * mm, "end": v(62.12, -3.11) * mm});
            skLineSegment(sketch, "E2174", {"start": v(62.12, -3.11) * mm, "end": v(62.17, -3.1) * mm});
            skLineSegment(sketch, "E2175", {"start": v(62.17, -3.1) * mm, "end": v(62.22, -3.1) * mm});
            skLineSegment(sketch, "E2176", {"start": v(62.22, -3.1) * mm, "end": v(62.27, -3.08) * mm});
            skLineSegment(sketch, "E2177", {"start": v(62.27, -3.08) * mm, "end": v(62.33, -3.06) * mm});
            skLineSegment(sketch, "E2178", {"start": v(62.33, -3.06) * mm, "end": v(62.39, -3.04) * mm});
            skLineSegment(sketch, "E2179", {"start": v(62.39, -3.04) * mm, "end": v(62.45, -3.02) * mm});
            skLineSegment(sketch, "E2180", {"start": v(62.45, -3.02) * mm, "end": v(62.54, -2.99) * mm});
            skLineSegment(sketch, "E2181", {"start": v(62.54, -2.99) * mm, "end": v(62.62, -2.96) * mm});
            skLineSegment(sketch, "E2182", {"start": v(62.62, -2.96) * mm, "end": v(62.7, -2.94) * mm});
            skLineSegment(sketch, "E2183", {"start": v(62.7, -2.94) * mm, "end": v(62.78, -2.93) * mm});
            skLineSegment(sketch, "E2184", {"start": v(62.78, -2.93) * mm, "end": v(62.87, -2.91) * mm});
            skLineSegment(sketch, "E2185", {"start": v(62.87, -2.91) * mm, "end": v(62.95, -2.9) * mm});
            skLineSegment(sketch, "E2186", {"start": v(62.95, -2.9) * mm, "end": v(63.03, -2.9) * mm});
            skLineSegment(sketch, "E2187", {"start": v(63.03, -2.9) * mm, "end": v(63.12, -2.9) * mm});
            skLineSegment(sketch, "E2188", {"start": v(63.12, -2.9) * mm, "end": v(63.2, -2.9) * mm});
            skLineSegment(sketch, "E2189", {"start": v(63.2, -2.9) * mm, "end": v(63.3, -2.91) * mm});
            skLineSegment(sketch, "E2190", {"start": v(63.3, -2.91) * mm, "end": v(63.4, -2.93) * mm});
            skLineSegment(sketch, "E2191", {"start": v(63.4, -2.93) * mm, "end": v(63.5, -2.94) * mm});
            skLineSegment(sketch, "E2192", {"start": v(63.5, -2.94) * mm, "end": v(63.62, -2.96) * mm});
            skLineSegment(sketch, "E2193", {"start": v(63.62, -2.96) * mm, "end": v(63.75, -3) * mm});
            skLineSegment(sketch, "E2194", {"start": v(63.75, -3) * mm, "end": v(63.88, -3.02) * mm});
            skLineSegment(sketch, "E2195", {"start": v(63.88, -3.02) * mm, "end": v(64.03, -3.06) * mm});
            skLineSegment(sketch, "E2196", {"start": v(64.03, -3.06) * mm, "end": v(64.1, -3.07) * mm});
            skLineSegment(sketch, "E2197", {"start": v(64.1, -3.07) * mm, "end": v(64.16, -3.09) * mm});
            skLineSegment(sketch, "E2198", {"start": v(64.16, -3.09) * mm, "end": v(64.22, -3.1) * mm});
            skLineSegment(sketch, "E2199", {"start": v(64.22, -3.1) * mm, "end": v(64.28, -3.12) * mm});
            skLineSegment(sketch, "E2200", {"start": v(64.28, -3.12) * mm, "end": v(64.35, -3.13) * mm});
            skLineSegment(sketch, "E2201", {"start": v(64.35, -3.13) * mm, "end": v(64.4, -3.15) * mm});
            skLineSegment(sketch, "E2202", {"start": v(64.4, -3.15) * mm, "end": v(64.46, -3.16) * mm});
            skLineSegment(sketch, "E2203", {"start": v(64.46, -3.16) * mm, "end": v(64.52, -3.18) * mm});
            skLineSegment(sketch, "E2204", {"start": v(64.52, -3.18) * mm, "end": v(64.57, -3.19) * mm});
            skLineSegment(sketch, "E2205", {"start": v(64.57, -3.19) * mm, "end": v(64.61, -3.2) * mm});
            skLineSegment(sketch, "E2206", {"start": v(64.61, -3.2) * mm, "end": v(64.66, -3.21) * mm});
            skLineSegment(sketch, "E2207", {"start": v(64.66, -3.21) * mm, "end": v(64.7, -3.22) * mm});
            skLineSegment(sketch, "E2208", {"start": v(64.7, -3.22) * mm, "end": v(64.73, -3.23) * mm});
            skLineSegment(sketch, "E2209", {"start": v(64.73, -3.23) * mm, "end": v(64.76, -3.24) * mm});
            skLineSegment(sketch, "E2210", {"start": v(64.76, -3.24) * mm, "end": v(64.79, -3.24) * mm});
            skLineSegment(sketch, "E2211", {"start": v(64.79, -3.24) * mm, "end": v(64.8, -3.25) * mm});
            skLineSegment(sketch, "E2212", {"start": v(64.8, -3.25) * mm, "end": v(64.86, -3.26) * mm});
            skLineSegment(sketch, "E2213", {"start": v(64.86, -3.26) * mm, "end": v(64.92, -3.27) * mm});
            skLineSegment(sketch, "E2214", {"start": v(64.92, -3.27) * mm, "end": v(64.98, -3.28) * mm});
            skLineSegment(sketch, "E2215", {"start": v(64.98, -3.28) * mm, "end": v(65.05, -3.29) * mm});
            skLineSegment(sketch, "E2216", {"start": v(65.05, -3.29) * mm, "end": v(65.12, -3.3) * mm});
            skLineSegment(sketch, "E2217", {"start": v(65.12, -3.3) * mm, "end": v(65.19, -3.3) * mm});
            skLineSegment(sketch, "E2218", {"start": v(65.19, -3.3) * mm, "end": v(65.26, -3.31) * mm});
            skLineSegment(sketch, "E2219", {"start": v(65.26, -3.31) * mm, "end": v(65.33, -3.32) * mm});
            skLineSegment(sketch, "E2220", {"start": v(65.33, -3.32) * mm, "end": v(65.4, -3.33) * mm});
            skLineSegment(sketch, "E2221", {"start": v(65.4, -3.33) * mm, "end": v(65.46, -3.33) * mm});
            skLineSegment(sketch, "E2222", {"start": v(65.46, -3.33) * mm, "end": v(65.52, -3.33) * mm});
            skLineSegment(sketch, "E2223", {"start": v(65.52, -3.33) * mm, "end": v(65.58, -3.34) * mm});
            skLineSegment(sketch, "E2224", {"start": v(65.58, -3.34) * mm, "end": v(65.63, -3.34) * mm});
            skLineSegment(sketch, "E2225", {"start": v(65.63, -3.34) * mm, "end": v(65.67, -3.34) * mm});
            skLineSegment(sketch, "E2226", {"start": v(65.67, -3.34) * mm, "end": v(65.71, -3.34) * mm});
            skLineSegment(sketch, "E2227", {"start": v(65.71, -3.34) * mm, "end": v(65.74, -3.33) * mm});
            skLineSegment(sketch, "E2228", {"start": v(65.74, -3.33) * mm, "end": v(65.76, -3.33) * mm});
            skLineSegment(sketch, "E2229", {"start": v(65.76, -3.33) * mm, "end": v(65.78, -3.32) * mm});
            skLineSegment(sketch, "E2230", {"start": v(65.78, -3.32) * mm, "end": v(65.8, -3.3) * mm});
            skLineSegment(sketch, "E2231", {"start": v(65.8, -3.3) * mm, "end": v(65.83, -3.29) * mm});
            skLineSegment(sketch, "E2232", {"start": v(65.83, -3.29) * mm, "end": v(65.86, -3.27) * mm});
            skLineSegment(sketch, "E2233", {"start": v(65.86, -3.27) * mm, "end": v(65.9, -3.24) * mm});
            skLineSegment(sketch, "E2234", {"start": v(65.9, -3.24) * mm, "end": v(65.94, -3.21) * mm});
            skLineSegment(sketch, "E2235", {"start": v(65.94, -3.21) * mm, "end": v(65.98, -3.17) * mm});
            skLineSegment(sketch, "E2236", {"start": v(65.98, -3.17) * mm, "end": v(66.03, -3.13) * mm});
            skLineSegment(sketch, "E2237", {"start": v(66.03, -3.13) * mm, "end": v(66.09, -3.08) * mm});
            skLineSegment(sketch, "E2238", {"start": v(66.09, -3.08) * mm, "end": v(66.15, -3.03) * mm});
            skLineSegment(sketch, "E2239", {"start": v(66.15, -3.03) * mm, "end": v(66.22, -2.96) * mm});
            skLineSegment(sketch, "E2240", {"start": v(66.22, -2.96) * mm, "end": v(66.3, -2.89) * mm});
            skLineSegment(sketch, "E2241", {"start": v(66.3, -2.89) * mm, "end": v(66.37, -2.8) * mm});
            skLineSegment(sketch, "E2242", {"start": v(66.37, -2.8) * mm, "end": v(66.47, -2.72) * mm});
            skLineSegment(sketch, "E2243", {"start": v(66.47, -2.72) * mm, "end": v(66.57, -2.62) * mm});
            skLineSegment(sketch, "E2244", {"start": v(66.57, -2.62) * mm, "end": v(66.57, -2.62) * mm});
            skLineSegment(sketch, "E2245", {"start": v(66.57, -2.62) * mm, "end": v(66.58, -2.62) * mm});
            skLineSegment(sketch, "E2246", {"start": v(66.58, -2.62) * mm, "end": v(66.6, -2.63) * mm});
            skLineSegment(sketch, "E2247", {"start": v(66.6, -2.63) * mm, "end": v(66.6, -2.63) * mm});
            skLineSegment(sketch, "E2248", {"start": v(66.6, -2.63) * mm, "end": v(66.62, -2.64) * mm});
            skLineSegment(sketch, "E2249", {"start": v(66.62, -2.64) * mm, "end": v(66.64, -2.65) * mm});
            skLineSegment(sketch, "E2250", {"start": v(66.64, -2.65) * mm, "end": v(66.66, -2.66) * mm});
            skLineSegment(sketch, "E2251", {"start": v(66.66, -2.66) * mm, "end": v(66.68, -2.67) * mm});
            skLineSegment(sketch, "E2252", {"start": v(66.68, -2.67) * mm, "end": v(66.73, -2.7) * mm});
            skLineSegment(sketch, "E2253", {"start": v(66.73, -2.7) * mm, "end": v(66.79, -2.75) * mm});
            skLineSegment(sketch, "E2254", {"start": v(66.79, -2.75) * mm, "end": v(66.84, -2.8) * mm});
            skLineSegment(sketch, "E2255", {"start": v(66.84, -2.8) * mm, "end": v(66.9, -2.87) * mm});
            skLineSegment(sketch, "E2256", {"start": v(66.9, -2.87) * mm, "end": v(66.95, -2.93) * mm});
            skLineSegment(sketch, "E2257", {"start": v(66.95, -2.93) * mm, "end": v(67, -3) * mm});
            skLineSegment(sketch, "E2258", {"start": v(67, -3) * mm, "end": v(67.05, -3.08) * mm});
            skLineSegment(sketch, "E2259", {"start": v(67.05, -3.08) * mm, "end": v(67.1, -3.16) * mm});
            skLineSegment(sketch, "E2260", {"start": v(67.1, -3.16) * mm, "end": v(67.15, -3.24) * mm});
            skLineSegment(sketch, "E2261", {"start": v(67.15, -3.24) * mm, "end": v(67.19, -3.32) * mm});
            skLineSegment(sketch, "E2262", {"start": v(67.19, -3.32) * mm, "end": v(67.23, -3.4) * mm});
            skLineSegment(sketch, "E2263", {"start": v(67.23, -3.4) * mm, "end": v(67.26, -3.48) * mm});
            skLineSegment(sketch, "E2264", {"start": v(67.26, -3.48) * mm, "end": v(67.28, -3.55) * mm});
            skLineSegment(sketch, "E2265", {"start": v(67.28, -3.55) * mm, "end": v(67.3, -3.62) * mm});
            skLineSegment(sketch, "E2266", {"start": v(67.3, -3.62) * mm, "end": v(67.32, -3.69) * mm});
            skLineSegment(sketch, "E2267", {"start": v(67.32, -3.69) * mm, "end": v(67.32, -3.74) * mm});
            skLineSegment(sketch, "E2268", {"start": v(67.32, -3.74) * mm, "end": v(67.32, -3.77) * mm});
            skLineSegment(sketch, "E2269", {"start": v(67.32, -3.77) * mm, "end": v(67.32, -3.8) * mm});
            skLineSegment(sketch, "E2270", {"start": v(67.32, -3.8) * mm, "end": v(67.33, -3.81) * mm});
            skLineSegment(sketch, "E2271", {"start": v(67.33, -3.81) * mm, "end": v(67.33, -3.83) * mm});
            skLineSegment(sketch, "E2272", {"start": v(67.33, -3.83) * mm, "end": v(67.33, -3.85) * mm});
            skLineSegment(sketch, "E2273", {"start": v(67.33, -3.85) * mm, "end": v(67.34, -3.88) * mm});
            skLineSegment(sketch, "E2274", {"start": v(67.34, -3.88) * mm, "end": v(67.35, -3.9) * mm});
            skLineSegment(sketch, "E2275", {"start": v(67.35, -3.9) * mm, "end": v(67.36, -3.92) * mm});
            skLineSegment(sketch, "E2276", {"start": v(67.36, -3.92) * mm, "end": v(67.37, -3.94) * mm});
            skLineSegment(sketch, "E2277", {"start": v(67.37, -3.94) * mm, "end": v(67.38, -3.97) * mm});
            skLineSegment(sketch, "E2278", {"start": v(67.38, -3.97) * mm, "end": v(67.4, -4) * mm});
            skLineSegment(sketch, "E2279", {"start": v(67.4, -4) * mm, "end": v(67.41, -4.02) * mm});
            skLineSegment(sketch, "E2280", {"start": v(67.41, -4.02) * mm, "end": v(67.43, -4.05) * mm});
            skLineSegment(sketch, "E2281", {"start": v(67.43, -4.05) * mm, "end": v(67.45, -4.08) * mm});
            skLineSegment(sketch, "E2282", {"start": v(67.45, -4.08) * mm, "end": v(67.48, -4.12) * mm});
            skLineSegment(sketch, "E2283", {"start": v(67.48, -4.12) * mm, "end": v(67.5, -4.15) * mm});
            skLineSegment(sketch, "E2284", {"start": v(67.5, -4.15) * mm, "end": v(67.55, -4.2) * mm});
            skLineSegment(sketch, "E2285", {"start": v(67.55, -4.2) * mm, "end": v(67.59, -4.27) * mm});
            skLineSegment(sketch, "E2286", {"start": v(67.59, -4.27) * mm, "end": v(67.63, -4.34) * mm});
            skLineSegment(sketch, "E2287", {"start": v(67.63, -4.34) * mm, "end": v(67.67, -4.4) * mm});
            skLineSegment(sketch, "E2288", {"start": v(67.67, -4.4) * mm, "end": v(67.71, -4.47) * mm});
            skLineSegment(sketch, "E2289", {"start": v(67.71, -4.47) * mm, "end": v(67.75, -4.53) * mm});
            skLineSegment(sketch, "E2290", {"start": v(67.75, -4.53) * mm, "end": v(67.78, -4.6) * mm});
            skLineSegment(sketch, "E2291", {"start": v(67.78, -4.6) * mm, "end": v(67.8, -4.65) * mm});
            skLineSegment(sketch, "E2292", {"start": v(67.8, -4.65) * mm, "end": v(67.83, -4.69) * mm});
            skLineSegment(sketch, "E2293", {"start": v(67.83, -4.69) * mm, "end": v(67.84, -4.72) * mm});
            skLineSegment(sketch, "E2294", {"start": v(67.84, -4.72) * mm, "end": v(67.86, -4.76) * mm});
            skLineSegment(sketch, "E2295", {"start": v(67.86, -4.76) * mm, "end": v(67.87, -4.79) * mm});
            skLineSegment(sketch, "E2296", {"start": v(67.87, -4.79) * mm, "end": v(67.88, -4.82) * mm});
            skLineSegment(sketch, "E2297", {"start": v(67.88, -4.82) * mm, "end": v(67.9, -4.85) * mm});
            skLineSegment(sketch, "E2298", {"start": v(67.9, -4.85) * mm, "end": v(67.9, -4.88) * mm});
            skLineSegment(sketch, "E2299", {"start": v(67.9, -4.88) * mm, "end": v(67.9, -4.91) * mm});
            skLineSegment(sketch, "E2300", {"start": v(67.9, -4.91) * mm, "end": v(67.91, -4.95) * mm});
            skLineSegment(sketch, "E2301", {"start": v(67.91, -4.95) * mm, "end": v(67.92, -4.98) * mm});
            skLineSegment(sketch, "E2302", {"start": v(67.92, -4.98) * mm, "end": v(67.92, -5.02) * mm});
            skLineSegment(sketch, "E2303", {"start": v(67.92, -5.02) * mm, "end": v(67.93, -5.06) * mm});
            skLineSegment(sketch, "E2304", {"start": v(67.93, -5.06) * mm, "end": v(67.93, -5.1) * mm});
            skLineSegment(sketch, "E2305", {"start": v(67.93, -5.1) * mm, "end": v(67.93, -5.15) * mm});
            skLineSegment(sketch, "E2306", {"start": v(67.93, -5.15) * mm, "end": v(67.94, -5.2) * mm});
            skLineSegment(sketch, "E2307", {"start": v(67.94, -5.2) * mm, "end": v(67.94, -5.26) * mm});
            skLineSegment(sketch, "E2308", {"start": v(67.94, -5.26) * mm, "end": v(67.94, -5.33) * mm});
            skLineSegment(sketch, "E2309", {"start": v(67.94, -5.33) * mm, "end": v(67.94, -5.4) * mm});
            skLineSegment(sketch, "E2310", {"start": v(67.94, -5.4) * mm, "end": v(67.94, -5.46) * mm});
            skLineSegment(sketch, "E2311", {"start": v(67.94, -5.46) * mm, "end": v(67.94, -5.51) * mm});
            skLineSegment(sketch, "E2312", {"start": v(67.94, -5.51) * mm, "end": v(67.93, -5.56) * mm});
            skLineSegment(sketch, "E2313", {"start": v(67.93, -5.56) * mm, "end": v(67.93, -5.6) * mm});
            skLineSegment(sketch, "E2314", {"start": v(67.93, -5.6) * mm, "end": v(67.92, -5.65) * mm});
            skLineSegment(sketch, "E2315", {"start": v(67.92, -5.65) * mm, "end": v(67.91, -5.68) * mm});
            skLineSegment(sketch, "E2316", {"start": v(67.91, -5.68) * mm, "end": v(67.9, -5.71) * mm});
            skLineSegment(sketch, "E2317", {"start": v(67.9, -5.71) * mm, "end": v(67.89, -5.74) * mm});
            skLineSegment(sketch, "E2318", {"start": v(67.89, -5.74) * mm, "end": v(67.87, -5.77) * mm});
            skLineSegment(sketch, "E2319", {"start": v(67.87, -5.77) * mm, "end": v(67.86, -5.8) * mm});
            skLineSegment(sketch, "E2320", {"start": v(67.86, -5.8) * mm, "end": v(67.84, -5.81) * mm});
            skLineSegment(sketch, "E2321", {"start": v(67.84, -5.81) * mm, "end": v(67.81, -5.83) * mm});
            skLineSegment(sketch, "E2322", {"start": v(67.81, -5.83) * mm, "end": v(67.79, -5.85) * mm});
            skLineSegment(sketch, "E2323", {"start": v(67.79, -5.85) * mm, "end": v(67.76, -5.87) * mm});
            skLineSegment(sketch, "E2324", {"start": v(67.76, -5.87) * mm, "end": v(67.74, -5.88) * mm});
            skLineSegment(sketch, "E2325", {"start": v(67.74, -5.88) * mm, "end": v(67.73, -5.88) * mm});
            skLineSegment(sketch, "E2326", {"start": v(67.73, -5.88) * mm, "end": v(67.71, -5.89) * mm});
            skLineSegment(sketch, "E2327", {"start": v(67.71, -5.89) * mm, "end": v(67.7, -5.9) * mm});
            skLineSegment(sketch, "E2328", {"start": v(67.7, -5.9) * mm, "end": v(67.69, -5.9) * mm});
            skLineSegment(sketch, "E2329", {"start": v(67.69, -5.9) * mm, "end": v(67.68, -5.9) * mm});
            skLineSegment(sketch, "E2330", {"start": v(67.68, -5.9) * mm, "end": v(67.66, -5.9) * mm});
            skLineSegment(sketch, "E2331", {"start": v(67.66, -5.9) * mm, "end": v(67.65, -5.9) * mm});
            skLineSegment(sketch, "E2332", {"start": v(67.65, -5.9) * mm, "end": v(67.64, -5.89) * mm});
            skLineSegment(sketch, "E2333", {"start": v(67.64, -5.89) * mm, "end": v(67.62, -5.88) * mm});
            skLineSegment(sketch, "E2334", {"start": v(67.62, -5.88) * mm, "end": v(67.6, -5.87) * mm});
            skLineSegment(sketch, "E2335", {"start": v(67.6, -5.87) * mm, "end": v(67.59, -5.86) * mm});
            skLineSegment(sketch, "E2336", {"start": v(67.59, -5.86) * mm, "end": v(67.57, -5.84) * mm});
            skLineSegment(sketch, "E2337", {"start": v(67.57, -5.84) * mm, "end": v(67.54, -5.82) * mm});
            skLineSegment(sketch, "E2338", {"start": v(67.54, -5.82) * mm, "end": v(67.52, -5.8) * mm});
            skLineSegment(sketch, "E2339", {"start": v(67.52, -5.8) * mm, "end": v(67.49, -5.78) * mm});
            skLineSegment(sketch, "E2340", {"start": v(67.49, -5.78) * mm, "end": v(67.4, -5.7) * mm});
            skLineSegment(sketch, "E2341", {"start": v(67.4, -5.7) * mm, "end": v(67.33, -5.62) * mm});
            skLineSegment(sketch, "E2342", {"start": v(67.33, -5.62) * mm, "end": v(67.27, -5.53) * mm});
            skLineSegment(sketch, "E2343", {"start": v(67.27, -5.53) * mm, "end": v(67.23, -5.44) * mm});
            skLineSegment(sketch, "E2344", {"start": v(67.23, -5.44) * mm, "end": v(67.21, -5.42) * mm});
            skLineSegment(sketch, "E2345", {"start": v(67.21, -5.42) * mm, "end": v(67.2, -5.39) * mm});
            skLineSegment(sketch, "E2346", {"start": v(67.2, -5.39) * mm, "end": v(67.18, -5.36) * mm});
            skLineSegment(sketch, "E2347", {"start": v(67.18, -5.36) * mm, "end": v(67.16, -5.33) * mm});
            skLineSegment(sketch, "E2348", {"start": v(67.16, -5.33) * mm, "end": v(67.14, -5.3) * mm});
            skLineSegment(sketch, "E2349", {"start": v(67.14, -5.3) * mm, "end": v(67.12, -5.27) * mm});
            skLineSegment(sketch, "E2350", {"start": v(67.12, -5.27) * mm, "end": v(67.1, -5.24) * mm});
            skLineSegment(sketch, "E2351", {"start": v(67.1, -5.24) * mm, "end": v(67.06, -5.2) * mm});
            skLineSegment(sketch, "E2352", {"start": v(67.06, -5.2) * mm, "end": v(67.03, -5.16) * mm});
            skLineSegment(sketch, "E2353", {"start": v(67.03, -5.16) * mm, "end": v(67, -5.13) * mm});
            skLineSegment(sketch, "E2354", {"start": v(67, -5.13) * mm, "end": v(66.95, -5.08) * mm});
            skLineSegment(sketch, "E2355", {"start": v(66.95, -5.08) * mm, "end": v(66.91, -5.04) * mm});
            skLineSegment(sketch, "E2356", {"start": v(66.91, -5.04) * mm, "end": v(66.86, -4.99) * mm});
            skLineSegment(sketch, "E2357", {"start": v(66.86, -4.99) * mm, "end": v(66.81, -4.94) * mm});
            skLineSegment(sketch, "E2358", {"start": v(66.81, -4.94) * mm, "end": v(66.75, -4.88) * mm});
            skLineSegment(sketch, "E2359", {"start": v(66.75, -4.88) * mm, "end": v(66.7, -4.82) * mm});
            skLineSegment(sketch, "E2360", {"start": v(66.7, -4.82) * mm, "end": v(66.62, -4.76) * mm});
            skLineSegment(sketch, "E2361", {"start": v(66.62, -4.76) * mm, "end": v(66.56, -4.7) * mm});
            skLineSegment(sketch, "E2362", {"start": v(66.56, -4.7) * mm, "end": v(66.5, -4.64) * mm});
            skLineSegment(sketch, "E2363", {"start": v(66.5, -4.64) * mm, "end": v(66.45, -4.6) * mm});
            skLineSegment(sketch, "E2364", {"start": v(66.45, -4.6) * mm, "end": v(66.4, -4.55) * mm});
            skLineSegment(sketch, "E2365", {"start": v(66.4, -4.55) * mm, "end": v(66.36, -4.52) * mm});
            skLineSegment(sketch, "E2366", {"start": v(66.36, -4.52) * mm, "end": v(66.33, -4.49) * mm});
            skLineSegment(sketch, "E2367", {"start": v(66.33, -4.49) * mm, "end": v(66.3, -4.46) * mm});
            skLineSegment(sketch, "E2368", {"start": v(66.3, -4.46) * mm, "end": v(66.27, -4.44) * mm});
            skLineSegment(sketch, "E2369", {"start": v(66.27, -4.44) * mm, "end": v(66.24, -4.43) * mm});
            skLineSegment(sketch, "E2370", {"start": v(66.24, -4.43) * mm, "end": v(66.22, -4.41) * mm});
            skLineSegment(sketch, "E2371", {"start": v(66.22, -4.41) * mm, "end": v(66.2, -4.4) * mm});
            skLineSegment(sketch, "E2372", {"start": v(66.2, -4.4) * mm, "end": v(66.17, -4.4) * mm});
            skLineSegment(sketch, "E2373", {"start": v(66.17, -4.4) * mm, "end": v(66.15, -4.4) * mm});
            skLineSegment(sketch, "E2374", {"start": v(66.15, -4.4) * mm, "end": v(66.13, -4.4) * mm});
            skLineSegment(sketch, "E2375", {"start": v(66.13, -4.4) * mm, "end": v(66.11, -4.4) * mm});
            skLineSegment(sketch, "E2376", {"start": v(66.11, -4.4) * mm, "end": v(66.05, -4.39) * mm});
            skLineSegment(sketch, "E2377", {"start": v(66.05, -4.39) * mm, "end": v(65.99, -4.37) * mm});
            skLineSegment(sketch, "E2378", {"start": v(65.99, -4.37) * mm, "end": v(65.93, -4.34) * mm});
            skLineSegment(sketch, "E2379", {"start": v(65.93, -4.34) * mm, "end": v(65.88, -4.29) * mm});
            skLineSegment(sketch, "E2380", {"start": v(65.88, -4.29) * mm, "end": v(65.86, -4.27) * mm});
            skLineSegment(sketch, "E2381", {"start": v(65.86, -4.27) * mm, "end": v(65.84, -4.26) * mm});
            skLineSegment(sketch, "E2382", {"start": v(65.84, -4.26) * mm, "end": v(65.83, -4.24) * mm});
            skLineSegment(sketch, "E2383", {"start": v(65.83, -4.24) * mm, "end": v(65.8, -4.23) * mm});
            skLineSegment(sketch, "E2384", {"start": v(65.8, -4.23) * mm, "end": v(65.8, -4.22) * mm});
            skLineSegment(sketch, "E2385", {"start": v(65.8, -4.22) * mm, "end": v(65.77, -4.21) * mm});
            skLineSegment(sketch, "E2386", {"start": v(65.77, -4.21) * mm, "end": v(65.75, -4.2) * mm});
            skLineSegment(sketch, "E2387", {"start": v(65.75, -4.2) * mm, "end": v(65.73, -4.2) * mm});
            skLineSegment(sketch, "E2388", {"start": v(65.73, -4.2) * mm, "end": v(65.7, -4.2) * mm});
            skLineSegment(sketch, "E2389", {"start": v(65.7, -4.2) * mm, "end": v(65.68, -4.2) * mm});
            skLineSegment(sketch, "E2390", {"start": v(65.68, -4.2) * mm, "end": v(65.64, -4.2) * mm});
            skLineSegment(sketch, "E2391", {"start": v(65.64, -4.2) * mm, "end": v(65.6, -4.2) * mm});
            skLineSegment(sketch, "E2392", {"start": v(65.6, -4.2) * mm, "end": v(65.56, -4.2) * mm});
            skLineSegment(sketch, "E2393", {"start": v(65.56, -4.2) * mm, "end": v(65.5, -4.19) * mm});
            skLineSegment(sketch, "E2394", {"start": v(65.5, -4.19) * mm, "end": v(65.45, -4.19) * mm});
            skLineSegment(sketch, "E2395", {"start": v(65.45, -4.19) * mm, "end": v(65.38, -4.2) * mm});
            skLineSegment(sketch, "E2396", {"start": v(65.38, -4.2) * mm, "end": v(65.29, -4.2) * mm});
            skLineSegment(sketch, "E2397", {"start": v(65.29, -4.2) * mm, "end": v(65.18, -4.2) * mm});
            skLineSegment(sketch, "E2398", {"start": v(65.18, -4.2) * mm, "end": v(65.07, -4.2) * mm});
            skLineSegment(sketch, "E2399", {"start": v(65.07, -4.2) * mm, "end": v(64.94, -4.2) * mm});
            skLineSegment(sketch, "E2400", {"start": v(64.94, -4.2) * mm, "end": v(64.81, -4.21) * mm});
            skLineSegment(sketch, "E2401", {"start": v(64.81, -4.21) * mm, "end": v(64.68, -4.22) * mm});
            skLineSegment(sketch, "E2402", {"start": v(64.68, -4.22) * mm, "end": v(64.56, -4.23) * mm});
            skLineSegment(sketch, "E2403", {"start": v(64.56, -4.23) * mm, "end": v(64.44, -4.24) * mm});
            skLineSegment(sketch, "E2404", {"start": v(64.44, -4.24) * mm, "end": v(64.3, -4.25) * mm});
            skLineSegment(sketch, "E2405", {"start": v(64.3, -4.25) * mm, "end": v(64.15, -4.26) * mm});
            skLineSegment(sketch, "E2406", {"start": v(64.15, -4.26) * mm, "end": v(64, -4.27) * mm});
            skLineSegment(sketch, "E2407", {"start": v(64, -4.27) * mm, "end": v(63.85, -4.27) * mm});
            skLineSegment(sketch, "E2408", {"start": v(63.85, -4.27) * mm, "end": v(63.7, -4.28) * mm});
            skLineSegment(sketch, "E2409", {"start": v(63.7, -4.28) * mm, "end": v(63.54, -4.27) * mm});
            skLineSegment(sketch, "E2410", {"start": v(63.54, -4.27) * mm, "end": v(63.37, -4.27) * mm});
            skLineSegment(sketch, "E2411", {"start": v(63.37, -4.27) * mm, "end": v(63.2, -4.27) * mm});
            skLineSegment(sketch, "E2412", {"start": v(63.2, -4.27) * mm, "end": v(63.1, -4.26) * mm});
            skLineSegment(sketch, "E2413", {"start": v(63.1, -4.26) * mm, "end": v(63.02, -4.26) * mm});
            skLineSegment(sketch, "E2414", {"start": v(63.02, -4.26) * mm, "end": v(62.94, -4.26) * mm});
            skLineSegment(sketch, "E2415", {"start": v(62.94, -4.26) * mm, "end": v(62.86, -4.26) * mm});
            skLineSegment(sketch, "E2416", {"start": v(62.86, -4.26) * mm, "end": v(62.8, -4.26) * mm});
            skLineSegment(sketch, "E2417", {"start": v(62.8, -4.26) * mm, "end": v(62.73, -4.26) * mm});
            skLineSegment(sketch, "E2418", {"start": v(62.73, -4.26) * mm, "end": v(62.67, -4.26) * mm});
            skLineSegment(sketch, "E2419", {"start": v(62.67, -4.26) * mm, "end": v(62.61, -4.26) * mm});
            skLineSegment(sketch, "E2420", {"start": v(62.61, -4.26) * mm, "end": v(62.56, -4.26) * mm});
            skLineSegment(sketch, "E2421", {"start": v(62.56, -4.26) * mm, "end": v(62.52, -4.26) * mm});
            skLineSegment(sketch, "E2422", {"start": v(62.52, -4.26) * mm, "end": v(62.47, -4.27) * mm});
            skLineSegment(sketch, "E2423", {"start": v(62.47, -4.27) * mm, "end": v(62.43, -4.27) * mm});
            skLineSegment(sketch, "E2424", {"start": v(62.43, -4.27) * mm, "end": v(62.4, -4.28) * mm});
            skLineSegment(sketch, "E2425", {"start": v(62.4, -4.28) * mm, "end": v(62.35, -4.28) * mm});
            skLineSegment(sketch, "E2426", {"start": v(62.35, -4.28) * mm, "end": v(62.32, -4.3) * mm});
            skLineSegment(sketch, "E2427", {"start": v(62.32, -4.3) * mm, "end": v(62.28, -4.3) * mm});
            skLineSegment(sketch, "E2428", {"start": v(62.28, -4.3) * mm, "end": v(62.19, -4.32) * mm});
            skLineSegment(sketch, "E2429", {"start": v(62.19, -4.32) * mm, "end": v(62.1, -4.34) * mm});
            skLineSegment(sketch, "E2430", {"start": v(62.1, -4.34) * mm, "end": v(62.02, -4.36) * mm});
            skLineSegment(sketch, "E2431", {"start": v(62.02, -4.36) * mm, "end": v(61.94, -4.37) * mm});
            skLineSegment(sketch, "E2432", {"start": v(61.94, -4.37) * mm, "end": v(61.87, -4.38) * mm});
            skLineSegment(sketch, "E2433", {"start": v(61.87, -4.38) * mm, "end": v(61.8, -4.4) * mm});
            skLineSegment(sketch, "E2434", {"start": v(61.8, -4.4) * mm, "end": v(61.74, -4.4) * mm});
            skLineSegment(sketch, "E2435", {"start": v(61.74, -4.4) * mm, "end": v(61.69, -4.4) * mm});
            skLineSegment(sketch, "E2436", {"start": v(61.69, -4.4) * mm, "end": v(61.63, -4.41) * mm});
            skLineSegment(sketch, "E2437", {"start": v(61.63, -4.41) * mm, "end": v(61.59, -4.42) * mm});
            skLineSegment(sketch, "E2438", {"start": v(61.59, -4.42) * mm, "end": v(61.54, -4.42) * mm});
            skLineSegment(sketch, "E2439", {"start": v(61.54, -4.42) * mm, "end": v(61.5, -4.42) * mm});
            skLineSegment(sketch, "E2440", {"start": v(61.5, -4.42) * mm, "end": v(61.47, -4.42) * mm});
            skLineSegment(sketch, "E2441", {"start": v(61.47, -4.42) * mm, "end": v(61.43, -4.41) * mm});
            skLineSegment(sketch, "E2442", {"start": v(61.43, -4.41) * mm, "end": v(61.4, -4.4) * mm});
            skLineSegment(sketch, "E2443", {"start": v(61.4, -4.4) * mm, "end": v(61.37, -4.4) * mm});
            skLineSegment(sketch, "E2444", {"start": v(61.37, -4.4) * mm, "end": v(61.29, -4.37) * mm});
            skLineSegment(sketch, "E2445", {"start": v(61.29, -4.37) * mm, "end": v(61.2, -4.32) * mm});
            skLineSegment(sketch, "E2446", {"start": v(61.2, -4.32) * mm, "end": v(61.12, -4.27) * mm});
            skLineSegment(sketch, "E2447", {"start": v(61.12, -4.27) * mm, "end": v(61.03, -4.2) * mm});
            skLineSegment(sketch, "E2448", {"start": v(61.03, -4.2) * mm, "end": v(60.94, -4.11) * mm});
            skLineSegment(sketch, "E2449", {"start": v(60.94, -4.11) * mm, "end": v(60.84, -4.01) * mm});
            skLineSegment(sketch, "E2450", {"start": v(60.84, -4.01) * mm, "end": v(60.74, -3.9) * mm});
            skLineSegment(sketch, "E2451", {"start": v(60.74, -3.9) * mm, "end": v(60.64, -3.77) * mm});
            skLineSegment(sketch, "E2452", {"start": v(60.64, -3.77) * mm, "end": v(60.58, -3.7) * mm});
            skLineSegment(sketch, "E2453", {"start": v(60.58, -3.7) * mm, "end": v(60.52, -3.63) * mm});
            skLineSegment(sketch, "E2454", {"start": v(60.52, -3.63) * mm, "end": v(60.45, -3.56) * mm});
            skLineSegment(sketch, "E2455", {"start": v(60.45, -3.56) * mm, "end": v(60.38, -3.48) * mm});
            skLineSegment(sketch, "E2456", {"start": v(60.38, -3.48) * mm, "end": v(60.32, -3.41) * mm});
            skLineSegment(sketch, "E2457", {"start": v(60.32, -3.41) * mm, "end": v(60.25, -3.35) * mm});
            skLineSegment(sketch, "E2458", {"start": v(60.25, -3.35) * mm, "end": v(60.19, -3.3) * mm});
            skLineSegment(sketch, "E2459", {"start": v(60.19, -3.3) * mm, "end": v(60.13, -3.24) * mm});
            skLineSegment(sketch, "E2460", {"start": v(60.13, -3.24) * mm, "end": v(60.09, -3.2) * mm});
            skLineSegment(sketch, "E2461", {"start": v(60.09, -3.2) * mm, "end": v(60.03, -3.15) * mm});
            skLineSegment(sketch, "E2462", {"start": v(60.03, -3.15) * mm, "end": v(59.98, -3.1) * mm});
            skLineSegment(sketch, "E2463", {"start": v(59.98, -3.1) * mm, "end": v(59.92, -3.03) * mm});
            skLineSegment(sketch, "E2464", {"start": v(59.92, -3.03) * mm, "end": v(59.85, -2.97) * mm});
            skLineSegment(sketch, "E2465", {"start": v(59.85, -2.97) * mm, "end": v(59.8, -2.9) * mm});
            skLineSegment(sketch, "E2466", {"start": v(59.8, -2.9) * mm, "end": v(59.73, -2.82) * mm});
            skLineSegment(sketch, "E2467", {"start": v(59.73, -2.82) * mm, "end": v(59.66, -2.74) * mm});
            skLineSegment(sketch, "E2468", {"start": v(59.66, -2.74) * mm, "end": v(59.6, -2.67) * mm});
            skLineSegment(sketch, "E2469", {"start": v(59.6, -2.67) * mm, "end": v(59.54, -2.59) * mm});
            skLineSegment(sketch, "E2470", {"start": v(59.54, -2.59) * mm, "end": v(59.49, -2.52) * mm});
            skLineSegment(sketch, "E2471", {"start": v(59.49, -2.52) * mm, "end": v(59.43, -2.45) * mm});
            skLineSegment(sketch, "E2472", {"start": v(59.43, -2.45) * mm, "end": v(59.39, -2.38) * mm});
            skLineSegment(sketch, "E2473", {"start": v(59.39, -2.38) * mm, "end": v(59.35, -2.32) * mm});
            skLineSegment(sketch, "E2474", {"start": v(59.35, -2.32) * mm, "end": v(59.32, -2.27) * mm});
            skLineSegment(sketch, "E2475", {"start": v(59.32, -2.27) * mm, "end": v(59.3, -2.23) * mm});
            skLineSegment(sketch, "E2476", {"start": v(59.3, -2.23) * mm, "end": v(59.28, -2.2) * mm});
            skLineSegment(sketch, "E2477", {"start": v(59.28, -2.2) * mm, "end": v(59.25, -2.16) * mm});
            skLineSegment(sketch, "E2478", {"start": v(59.25, -2.16) * mm, "end": v(59.23, -2.14) * mm});
            skLineSegment(sketch, "E2479", {"start": v(59.23, -2.14) * mm, "end": v(59.21, -2.14) * mm});
            skLineSegment(sketch, "E2480", {"start": v(59.21, -2.14) * mm, "end": v(59.2, -2.14) * mm});
            skLineSegment(sketch, "E2481", {"start": v(59.2, -2.14) * mm, "end": v(59.19, -2.15) * mm});
            skLineSegment(sketch, "E2482", {"start": v(59.19, -2.15) * mm, "end": v(59.17, -2.16) * mm});
            skLineSegment(sketch, "E2483", {"start": v(59.17, -2.16) * mm, "end": v(59.15, -2.18) * mm});
            skLineSegment(sketch, "E2484", {"start": v(59.15, -2.18) * mm, "end": v(59.12, -2.2) * mm});
            skLineSegment(sketch, "E2485", {"start": v(59.12, -2.2) * mm, "end": v(59.09, -2.24) * mm});
            skLineSegment(sketch, "E2486", {"start": v(59.09, -2.24) * mm, "end": v(59.05, -2.27) * mm});
            skLineSegment(sketch, "E2487", {"start": v(59.05, -2.27) * mm, "end": v(59.01, -2.3) * mm});
            skLineSegment(sketch, "E2488", {"start": v(59.01, -2.3) * mm, "end": v(58.97, -2.35) * mm});
            skLineSegment(sketch, "E2489", {"start": v(58.97, -2.35) * mm, "end": v(58.92, -2.4) * mm});
            skLineSegment(sketch, "E2490", {"start": v(58.92, -2.4) * mm, "end": v(58.87, -2.44) * mm});
            skLineSegment(sketch, "E2491", {"start": v(58.87, -2.44) * mm, "end": v(58.82, -2.5) * mm});
            skLineSegment(sketch, "E2492", {"start": v(58.82, -2.5) * mm, "end": v(58.77, -2.55) * mm});
            skLineSegment(sketch, "E2493", {"start": v(58.77, -2.55) * mm, "end": v(58.71, -2.6) * mm});
            skLineSegment(sketch, "E2494", {"start": v(58.71, -2.6) * mm, "end": v(58.66, -2.66) * mm});
            skLineSegment(sketch, "E2495", {"start": v(58.66, -2.66) * mm, "end": v(58.6, -2.72) * mm});
            skLineSegment(sketch, "E2496", {"start": v(58.6, -2.72) * mm, "end": v(58.54, -2.78) * mm});
            skLineSegment(sketch, "E2497", {"start": v(58.54, -2.78) * mm, "end": v(58.48, -2.84) * mm});
            skLineSegment(sketch, "E2498", {"start": v(58.48, -2.84) * mm, "end": v(58.43, -2.9) * mm});
            skLineSegment(sketch, "E2499", {"start": v(58.43, -2.9) * mm, "end": v(58.37, -2.95) * mm});
            skLineSegment(sketch, "E2500", {"start": v(58.37, -2.95) * mm, "end": v(58.32, -3) * mm});
            skLineSegment(sketch, "E2501", {"start": v(58.32, -3) * mm, "end": v(58.27, -3.06) * mm});
            skLineSegment(sketch, "E2502", {"start": v(58.27, -3.06) * mm, "end": v(58.21, -3.1) * mm});
            skLineSegment(sketch, "E2503", {"start": v(58.21, -3.1) * mm, "end": v(58.17, -3.16) * mm});
            skLineSegment(sketch, "E2504", {"start": v(58.17, -3.16) * mm, "end": v(58.12, -3.2) * mm});
            skLineSegment(sketch, "E2505", {"start": v(58.12, -3.2) * mm, "end": v(58.08, -3.24) * mm});
            skLineSegment(sketch, "E2506", {"start": v(58.08, -3.24) * mm, "end": v(58.04, -3.28) * mm});
            skLineSegment(sketch, "E2507", {"start": v(58.04, -3.28) * mm, "end": v(58, -3.3) * mm});
            skLineSegment(sketch, "E2508", {"start": v(58, -3.3) * mm, "end": v(57.98, -3.33) * mm});
            skLineSegment(sketch, "E2509", {"start": v(57.98, -3.33) * mm, "end": v(57.95, -3.36) * mm});
            skLineSegment(sketch, "E2510", {"start": v(57.95, -3.36) * mm, "end": v(57.93, -3.37) * mm});
            skLineSegment(sketch, "E2511", {"start": v(57.93, -3.37) * mm, "end": v(57.92, -3.38) * mm});
            skLineSegment(sketch, "E2512", {"start": v(57.92, -3.38) * mm, "end": v(57.9, -3.4) * mm});
            skLineSegment(sketch, "E2513", {"start": v(57.9, -3.4) * mm, "end": v(57.87, -3.43) * mm});
            skLineSegment(sketch, "E2514", {"start": v(57.87, -3.43) * mm, "end": v(57.84, -3.46) * mm});
            skLineSegment(sketch, "E2515", {"start": v(57.84, -3.46) * mm, "end": v(57.8, -3.5) * mm});
            skLineSegment(sketch, "E2516", {"start": v(57.8, -3.5) * mm, "end": v(57.76, -3.53) * mm});
            skLineSegment(sketch, "E2517", {"start": v(57.76, -3.53) * mm, "end": v(57.72, -3.58) * mm});
            skLineSegment(sketch, "E2518", {"start": v(57.72, -3.58) * mm, "end": v(57.68, -3.62) * mm});
            skLineSegment(sketch, "E2519", {"start": v(57.68, -3.62) * mm, "end": v(57.64, -3.67) * mm});
            skLineSegment(sketch, "E2520", {"start": v(57.64, -3.67) * mm, "end": v(57.6, -3.72) * mm});
            skLineSegment(sketch, "E2521", {"start": v(57.6, -3.72) * mm, "end": v(57.56, -3.77) * mm});
            skLineSegment(sketch, "E2522", {"start": v(57.56, -3.77) * mm, "end": v(57.52, -3.82) * mm});
            skLineSegment(sketch, "E2523", {"start": v(57.52, -3.82) * mm, "end": v(57.48, -3.87) * mm});
            skLineSegment(sketch, "E2524", {"start": v(57.48, -3.87) * mm, "end": v(57.44, -3.92) * mm});
            skLineSegment(sketch, "E2525", {"start": v(57.44, -3.92) * mm, "end": v(57.4, -3.97) * mm});
            skLineSegment(sketch, "E2526", {"start": v(57.4, -3.97) * mm, "end": v(57.37, -4.01) * mm});
            skLineSegment(sketch, "E2527", {"start": v(57.37, -4.01) * mm, "end": v(57.35, -4.05) * mm});
            skLineSegment(sketch, "E2528", {"start": v(57.35, -4.05) * mm, "end": v(57.33, -4.08) * mm});
            skLineSegment(sketch, "E2529", {"start": v(57.33, -4.08) * mm, "end": v(57.32, -4.12) * mm});
            skLineSegment(sketch, "E2530", {"start": v(57.32, -4.12) * mm, "end": v(57.3, -4.17) * mm});
            skLineSegment(sketch, "E2531", {"start": v(57.3, -4.17) * mm, "end": v(57.3, -4.23) * mm});
            skLineSegment(sketch, "E2532", {"start": v(57.3, -4.23) * mm, "end": v(57.28, -4.3) * mm});
            skLineSegment(sketch, "E2533", {"start": v(57.28, -4.3) * mm, "end": v(57.27, -4.36) * mm});
            skLineSegment(sketch, "E2534", {"start": v(57.27, -4.36) * mm, "end": v(57.26, -4.44) * mm});
            skLineSegment(sketch, "E2535", {"start": v(57.26, -4.44) * mm, "end": v(57.25, -4.52) * mm});
            skLineSegment(sketch, "E2536", {"start": v(57.25, -4.52) * mm, "end": v(57.23, -4.63) * mm});
            skLineSegment(sketch, "E2537", {"start": v(57.23, -4.63) * mm, "end": v(57.22, -4.73) * mm});
            skLineSegment(sketch, "E2538", {"start": v(57.22, -4.73) * mm, "end": v(57.21, -4.83) * mm});
            skLineSegment(sketch, "E2539", {"start": v(57.21, -4.83) * mm, "end": v(57.2, -4.92) * mm});
            skLineSegment(sketch, "E2540", {"start": v(57.2, -4.92) * mm, "end": v(57.19, -5) * mm});
            skLineSegment(sketch, "E2541", {"start": v(57.19, -5) * mm, "end": v(57.18, -5.1) * mm});
            skLineSegment(sketch, "E2542", {"start": v(57.18, -5.1) * mm, "end": v(57.17, -5.18) * mm});
            skLineSegment(sketch, "E2543", {"start": v(57.17, -5.18) * mm, "end": v(57.15, -5.25) * mm});
            skLineSegment(sketch, "E2544", {"start": v(57.15, -5.25) * mm, "end": v(57.14, -5.33) * mm});
            skLineSegment(sketch, "E2545", {"start": v(57.14, -5.33) * mm, "end": v(57.13, -5.4) * mm});
            skLineSegment(sketch, "E2546", {"start": v(57.13, -5.4) * mm, "end": v(57.12, -5.47) * mm});
            skLineSegment(sketch, "E2547", {"start": v(57.12, -5.47) * mm, "end": v(57.1, -5.53) * mm});
            skLineSegment(sketch, "E2548", {"start": v(57.1, -5.53) * mm, "end": v(57.09, -5.6) * mm});
            skLineSegment(sketch, "E2549", {"start": v(57.09, -5.6) * mm, "end": v(57.07, -5.66) * mm});
            skLineSegment(sketch, "E2550", {"start": v(57.07, -5.66) * mm, "end": v(57.06, -5.71) * mm});
            skLineSegment(sketch, "E2551", {"start": v(57.06, -5.71) * mm, "end": v(57.04, -5.77) * mm});
            skLineSegment(sketch, "E2552", {"start": v(57.04, -5.77) * mm, "end": v(57.02, -5.83) * mm});
            skLineSegment(sketch, "E2553", {"start": v(57.02, -5.83) * mm, "end": v(57, -5.88) * mm});
            skLineSegment(sketch, "E2554", {"start": v(57, -5.88) * mm, "end": v(56.98, -5.94) * mm});
            skLineSegment(sketch, "E2555", {"start": v(56.98, -5.94) * mm, "end": v(56.96, -6) * mm});
            skLineSegment(sketch, "E2556", {"start": v(56.96, -6) * mm, "end": v(56.94, -6.04) * mm});
            skLineSegment(sketch, "E2557", {"start": v(56.94, -6.04) * mm, "end": v(56.92, -6.1) * mm});
            skLineSegment(sketch, "E2558", {"start": v(56.92, -6.1) * mm, "end": v(56.9, -6.15) * mm});
            skLineSegment(sketch, "E2559", {"start": v(56.9, -6.15) * mm, "end": v(56.86, -6.2) * mm});
            skLineSegment(sketch, "E2560", {"start": v(56.86, -6.2) * mm, "end": v(56.84, -6.26) * mm});
            skLineSegment(sketch, "E2561", {"start": v(56.84, -6.26) * mm, "end": v(56.8, -6.31) * mm});
            skLineSegment(sketch, "E2562", {"start": v(56.8, -6.31) * mm, "end": v(56.78, -6.37) * mm});
            skLineSegment(sketch, "E2563", {"start": v(56.78, -6.37) * mm, "end": v(56.74, -6.42) * mm});
            skLineSegment(sketch, "E2564", {"start": v(56.74, -6.42) * mm, "end": v(56.7, -6.48) * mm});
            skLineSegment(sketch, "E2565", {"start": v(56.7, -6.48) * mm, "end": v(56.67, -6.54) * mm});
            skLineSegment(sketch, "E2566", {"start": v(56.67, -6.54) * mm, "end": v(56.63, -6.6) * mm});
            skLineSegment(sketch, "E2567", {"start": v(56.63, -6.6) * mm, "end": v(56.6, -6.67) * mm});
            skLineSegment(sketch, "E2568", {"start": v(56.6, -6.67) * mm, "end": v(56.48, -6.84) * mm});
            skLineSegment(sketch, "E2569", {"start": v(56.48, -6.84) * mm, "end": v(56.37, -7.01) * mm});
            skLineSegment(sketch, "E2570", {"start": v(56.37, -7.01) * mm, "end": v(56.27, -7.18) * mm});
            skLineSegment(sketch, "E2571", {"start": v(56.27, -7.18) * mm, "end": v(56.18, -7.33) * mm});
            skLineSegment(sketch, "E2572", {"start": v(56.18, -7.33) * mm, "end": v(56.1, -7.48) * mm});
            skLineSegment(sketch, "E2573", {"start": v(56.1, -7.48) * mm, "end": v(56.01, -7.62) * mm});
            skLineSegment(sketch, "E2574", {"start": v(56.01, -7.62) * mm, "end": v(55.94, -7.76) * mm});
            skLineSegment(sketch, "E2575", {"start": v(55.94, -7.76) * mm, "end": v(55.88, -7.87) * mm});
            skLineSegment(sketch, "E2576", {"start": v(55.88, -7.87) * mm, "end": v(55.86, -7.92) * mm});
            skLineSegment(sketch, "E2577", {"start": v(55.86, -7.92) * mm, "end": v(55.84, -7.97) * mm});
            skLineSegment(sketch, "E2578", {"start": v(55.84, -7.97) * mm, "end": v(55.82, -8) * mm});
            skLineSegment(sketch, "E2579", {"start": v(55.82, -8) * mm, "end": v(55.8, -8.04) * mm});
            skLineSegment(sketch, "E2580", {"start": v(55.8, -8.04) * mm, "end": v(55.79, -8.07) * mm});
            skLineSegment(sketch, "E2581", {"start": v(55.79, -8.07) * mm, "end": v(55.78, -8.1) * mm});
            skLineSegment(sketch, "E2582", {"start": v(55.78, -8.1) * mm, "end": v(55.77, -8.13) * mm});
            skLineSegment(sketch, "E2583", {"start": v(55.77, -8.13) * mm, "end": v(55.76, -8.16) * mm});
            skLineSegment(sketch, "E2584", {"start": v(55.76, -8.16) * mm, "end": v(55.75, -8.18) * mm});
            skLineSegment(sketch, "E2585", {"start": v(55.75, -8.18) * mm, "end": v(55.75, -8.2) * mm});
            skLineSegment(sketch, "E2586", {"start": v(55.75, -8.2) * mm, "end": v(55.75, -8.24) * mm});
            skLineSegment(sketch, "E2587", {"start": v(55.75, -8.24) * mm, "end": v(55.75, -8.26) * mm});
            skLineSegment(sketch, "E2588", {"start": v(55.75, -8.26) * mm, "end": v(55.75, -8.3) * mm});
            skLineSegment(sketch, "E2589", {"start": v(55.75, -8.3) * mm, "end": v(55.75, -8.32) * mm});
            skLineSegment(sketch, "E2590", {"start": v(55.75, -8.32) * mm, "end": v(55.75, -8.36) * mm});
            skLineSegment(sketch, "E2591", {"start": v(55.75, -8.36) * mm, "end": v(55.76, -8.4) * mm});
            skLineSegment(sketch, "E2592", {"start": v(55.76, -8.4) * mm, "end": v(55.76, -8.44) * mm});
            skLineSegment(sketch, "E2593", {"start": v(55.76, -8.44) * mm, "end": v(55.77, -8.47) * mm});
            skLineSegment(sketch, "E2594", {"start": v(55.77, -8.47) * mm, "end": v(55.77, -8.5) * mm});
            skLineSegment(sketch, "E2595", {"start": v(55.77, -8.5) * mm, "end": v(55.77, -8.53) * mm});
            skLineSegment(sketch, "E2596", {"start": v(55.77, -8.53) * mm, "end": v(55.77, -8.56) * mm});
            skLineSegment(sketch, "E2597", {"start": v(55.77, -8.56) * mm, "end": v(55.77, -8.58) * mm});
            skLineSegment(sketch, "E2598", {"start": v(55.77, -8.58) * mm, "end": v(55.76, -8.6) * mm});
            skLineSegment(sketch, "E2599", {"start": v(55.76, -8.6) * mm, "end": v(55.76, -8.62) * mm});
            skLineSegment(sketch, "E2600", {"start": v(55.76, -8.62) * mm, "end": v(55.75, -8.64) * mm});
            skLineSegment(sketch, "E2601", {"start": v(55.75, -8.64) * mm, "end": v(55.75, -8.66) * mm});
            skLineSegment(sketch, "E2602", {"start": v(55.75, -8.66) * mm, "end": v(55.74, -8.68) * mm});
            skLineSegment(sketch, "E2603", {"start": v(55.74, -8.68) * mm, "end": v(55.72, -8.7) * mm});
            skLineSegment(sketch, "E2604", {"start": v(55.72, -8.7) * mm, "end": v(55.7, -8.73) * mm});
            skLineSegment(sketch, "E2605", {"start": v(55.7, -8.73) * mm, "end": v(55.7, -8.75) * mm});
            skLineSegment(sketch, "E2606", {"start": v(55.7, -8.75) * mm, "end": v(55.67, -8.78) * mm});
            skLineSegment(sketch, "E2607", {"start": v(55.67, -8.78) * mm, "end": v(55.65, -8.81) * mm});
            skLineSegment(sketch, "E2608", {"start": v(55.65, -8.81) * mm, "end": v(55.62, -8.85) * mm});
            skLineSegment(sketch, "E2609", {"start": v(55.62, -8.85) * mm, "end": v(55.6, -8.9) * mm});
            skLineSegment(sketch, "E2610", {"start": v(55.6, -8.9) * mm, "end": v(55.56, -8.95) * mm});
            skLineSegment(sketch, "E2611", {"start": v(55.56, -8.95) * mm, "end": v(55.53, -9) * mm});
            skLineSegment(sketch, "E2612", {"start": v(55.53, -9) * mm, "end": v(55.5, -9.07) * mm});
            skLineSegment(sketch, "E2613", {"start": v(55.5, -9.07) * mm, "end": v(55.46, -9.12) * mm});
            skLineSegment(sketch, "E2614", {"start": v(55.46, -9.12) * mm, "end": v(55.43, -9.17) * mm});
            skLineSegment(sketch, "E2615", {"start": v(55.43, -9.17) * mm, "end": v(55.41, -9.22) * mm});
            skLineSegment(sketch, "E2616", {"start": v(55.41, -9.22) * mm, "end": v(55.37, -9.3) * mm});
            skLineSegment(sketch, "E2617", {"start": v(55.37, -9.3) * mm, "end": v(55.33, -9.37) * mm});
            skLineSegment(sketch, "E2618", {"start": v(55.33, -9.37) * mm, "end": v(55.29, -9.43) * mm});
            skLineSegment(sketch, "E2619", {"start": v(55.29, -9.43) * mm, "end": v(55.24, -9.48) * mm});
            skLineSegment(sketch, "E2620", {"start": v(55.24, -9.48) * mm, "end": v(55.2, -9.52) * mm});
            skLineSegment(sketch, "E2621", {"start": v(55.2, -9.52) * mm, "end": v(55.16, -9.55) * mm});
            skLineSegment(sketch, "E2622", {"start": v(55.16, -9.55) * mm, "end": v(55.12, -9.56) * mm});
            skLineSegment(sketch, "E2623", {"start": v(55.12, -9.56) * mm, "end": v(55.08, -9.57) * mm});
            skLineSegment(sketch, "E2624", {"start": v(55.08, -9.57) * mm, "end": v(55.06, -9.57) * mm});
            skLineSegment(sketch, "E2625", {"start": v(55.06, -9.57) * mm, "end": v(55.04, -9.56) * mm});
            skLineSegment(sketch, "E2626", {"start": v(55.04, -9.56) * mm, "end": v(55, -9.55) * mm});
            skLineSegment(sketch, "E2627", {"start": v(55, -9.55) * mm, "end": v(54.97, -9.54) * mm});
            skLineSegment(sketch, "E2628", {"start": v(54.97, -9.54) * mm, "end": v(54.93, -9.52) * mm});
            skLineSegment(sketch, "E2629", {"start": v(54.93, -9.52) * mm, "end": v(54.89, -9.5) * mm});
            skLineSegment(sketch, "E2630", {"start": v(54.89, -9.5) * mm, "end": v(54.84, -9.49) * mm});
            skLineSegment(sketch, "E2631", {"start": v(54.84, -9.49) * mm, "end": v(54.8, -9.47) * mm});
            skLineSegment(sketch, "E2632", {"start": v(60.17, 2.7) * mm, "end": v(60.19, 2.7) * mm});
            skLineSegment(sketch, "E2633", {"start": v(60.19, 2.7) * mm, "end": v(60.22, 2.72) * mm});
            skLineSegment(sketch, "E2634", {"start": v(60.22, 2.72) * mm, "end": v(60.25, 2.73) * mm});
            skLineSegment(sketch, "E2635", {"start": v(60.25, 2.73) * mm, "end": v(60.3, 2.74) * mm});
            skLineSegment(sketch, "E2636", {"start": v(60.3, 2.74) * mm, "end": v(60.33, 2.75) * mm});
            skLineSegment(sketch, "E2637", {"start": v(60.33, 2.75) * mm, "end": v(60.38, 2.75) * mm});
            skLineSegment(sketch, "E2638", {"start": v(60.38, 2.75) * mm, "end": v(60.42, 2.76) * mm});
            skLineSegment(sketch, "E2639", {"start": v(60.42, 2.76) * mm, "end": v(60.47, 2.76) * mm});
            skLineSegment(sketch, "E2640", {"start": v(60.47, 2.76) * mm, "end": v(60.5, 2.77) * mm});
            skLineSegment(sketch, "E2641", {"start": v(60.5, 2.77) * mm, "end": v(60.53, 2.77) * mm});
            skLineSegment(sketch, "E2642", {"start": v(60.53, 2.77) * mm, "end": v(60.56, 2.77) * mm});
            skLineSegment(sketch, "E2643", {"start": v(60.56, 2.77) * mm, "end": v(60.59, 2.78) * mm});
            skLineSegment(sketch, "E2644", {"start": v(60.59, 2.78) * mm, "end": v(60.61, 2.78) * mm});
            skLineSegment(sketch, "E2645", {"start": v(60.61, 2.78) * mm, "end": v(60.63, 2.78) * mm});
            skLineSegment(sketch, "E2646", {"start": v(60.63, 2.78) * mm, "end": v(60.65, 2.79) * mm});
            skLineSegment(sketch, "E2647", {"start": v(60.65, 2.79) * mm, "end": v(60.67, 2.8) * mm});
            skLineSegment(sketch, "E2648", {"start": v(60.67, 2.8) * mm, "end": v(60.68, 2.8) * mm});
            skLineSegment(sketch, "E2649", {"start": v(60.68, 2.8) * mm, "end": v(60.7, 2.81) * mm});
            skLineSegment(sketch, "E2650", {"start": v(60.7, 2.81) * mm, "end": v(60.71, 2.83) * mm});
            skLineSegment(sketch, "E2651", {"start": v(60.71, 2.83) * mm, "end": v(60.73, 2.84) * mm});
            skLineSegment(sketch, "E2652", {"start": v(60.73, 2.84) * mm, "end": v(60.74, 2.86) * mm});
            skLineSegment(sketch, "E2653", {"start": v(60.74, 2.86) * mm, "end": v(60.76, 2.87) * mm});
            skLineSegment(sketch, "E2654", {"start": v(60.76, 2.87) * mm, "end": v(60.78, 2.9) * mm});
            skLineSegment(sketch, "E2655", {"start": v(60.78, 2.9) * mm, "end": v(60.8, 2.92) * mm});
            skLineSegment(sketch, "E2656", {"start": v(60.8, 2.92) * mm, "end": v(60.82, 2.95) * mm});
            skLineSegment(sketch, "E2657", {"start": v(60.82, 2.95) * mm, "end": v(60.85, 2.98) * mm});
            skLineSegment(sketch, "E2658", {"start": v(60.85, 2.98) * mm, "end": v(60.88, 3.03) * mm});
            skLineSegment(sketch, "E2659", {"start": v(60.88, 3.03) * mm, "end": v(60.92, 3.07) * mm});
            skLineSegment(sketch, "E2660", {"start": v(60.92, 3.07) * mm, "end": v(60.96, 3.11) * mm});
            skLineSegment(sketch, "E2661", {"start": v(60.96, 3.11) * mm, "end": v(61, 3.16) * mm});
            skLineSegment(sketch, "E2662", {"start": v(61, 3.16) * mm, "end": v(61.04, 3.2) * mm});
            skLineSegment(sketch, "E2663", {"start": v(61.04, 3.2) * mm, "end": v(61.07, 3.24) * mm});
            skLineSegment(sketch, "E2664", {"start": v(61.07, 3.24) * mm, "end": v(61.14, 3.32) * mm});
            skLineSegment(sketch, "E2665", {"start": v(61.14, 3.32) * mm, "end": v(61.2, 3.4) * mm});
            skLineSegment(sketch, "E2666", {"start": v(61.2, 3.4) * mm, "end": v(61.27, 3.49) * mm});
            skLineSegment(sketch, "E2667", {"start": v(61.27, 3.49) * mm, "end": v(61.33, 3.58) * mm});
            skLineSegment(sketch, "E2668", {"start": v(61.33, 3.58) * mm, "end": v(61.4, 3.67) * mm});
            skLineSegment(sketch, "E2669", {"start": v(61.4, 3.67) * mm, "end": v(61.45, 3.76) * mm});
            skLineSegment(sketch, "E2670", {"start": v(61.45, 3.76) * mm, "end": v(61.5, 3.85) * mm});
            skLineSegment(sketch, "E2671", {"start": v(61.5, 3.85) * mm, "end": v(61.56, 3.95) * mm});
            skLineSegment(sketch, "E2672", {"start": v(61.56, 3.95) * mm, "end": v(61.6, 4.04) * mm});
            skLineSegment(sketch, "E2673", {"start": v(61.6, 4.04) * mm, "end": v(61.65, 4.12) * mm});
            skLineSegment(sketch, "E2674", {"start": v(61.65, 4.12) * mm, "end": v(61.69, 4.2) * mm});
            skLineSegment(sketch, "E2675", {"start": v(61.69, 4.2) * mm, "end": v(61.72, 4.27) * mm});
            skLineSegment(sketch, "E2676", {"start": v(61.72, 4.27) * mm, "end": v(61.74, 4.34) * mm});
            skLineSegment(sketch, "E2677", {"start": v(61.74, 4.34) * mm, "end": v(61.75, 4.4) * mm});
            skLineSegment(sketch, "E2678", {"start": v(61.75, 4.4) * mm, "end": v(61.76, 4.44) * mm});
            skLineSegment(sketch, "E2679", {"start": v(61.76, 4.44) * mm, "end": v(61.75, 4.47) * mm});
            skLineSegment(sketch, "E2680", {"start": v(61.75, 4.47) * mm, "end": v(61.75, 4.48) * mm});
            skLineSegment(sketch, "E2681", {"start": v(61.75, 4.48) * mm, "end": v(61.73, 4.5) * mm});
            skLineSegment(sketch, "E2682", {"start": v(61.73, 4.5) * mm, "end": v(61.7, 4.5) * mm});
            skLineSegment(sketch, "E2683", {"start": v(61.7, 4.5) * mm, "end": v(61.68, 4.52) * mm});
            skLineSegment(sketch, "E2684", {"start": v(61.68, 4.52) * mm, "end": v(61.64, 4.54) * mm});
            skLineSegment(sketch, "E2685", {"start": v(61.64, 4.54) * mm, "end": v(61.6, 4.55) * mm});
            skLineSegment(sketch, "E2686", {"start": v(61.6, 4.55) * mm, "end": v(61.56, 4.57) * mm});
            skLineSegment(sketch, "E2687", {"start": v(61.56, 4.57) * mm, "end": v(61.52, 4.58) * mm});
            skLineSegment(sketch, "E2688", {"start": v(61.52, 4.58) * mm, "end": v(61.47, 4.6) * mm});
            skLineSegment(sketch, "E2689", {"start": v(61.47, 4.6) * mm, "end": v(61.41, 4.6) * mm});
            skLineSegment(sketch, "E2690", {"start": v(61.41, 4.6) * mm, "end": v(61.35, 4.63) * mm});
            skLineSegment(sketch, "E2691", {"start": v(61.35, 4.63) * mm, "end": v(61.27, 4.65) * mm});
            skLineSegment(sketch, "E2692", {"start": v(61.27, 4.65) * mm, "end": v(61.2, 4.68) * mm});
            skLineSegment(sketch, "E2693", {"start": v(61.2, 4.68) * mm, "end": v(61.12, 4.7) * mm});
            skLineSegment(sketch, "E2694", {"start": v(61.12, 4.7) * mm, "end": v(61.05, 4.73) * mm});
            skLineSegment(sketch, "E2695", {"start": v(61.05, 4.73) * mm, "end": v(60.98, 4.75) * mm});
            skLineSegment(sketch, "E2696", {"start": v(60.98, 4.75) * mm, "end": v(60.91, 4.77) * mm});
            skLineSegment(sketch, "E2697", {"start": v(60.91, 4.77) * mm, "end": v(60.85, 4.8) * mm});
            skLineSegment(sketch, "E2698", {"start": v(60.85, 4.8) * mm, "end": v(60.8, 4.81) * mm});
            skLineSegment(sketch, "E2699", {"start": v(60.8, 4.81) * mm, "end": v(60.74, 4.83) * mm});
            skLineSegment(sketch, "E2700", {"start": v(60.74, 4.83) * mm, "end": v(60.69, 4.85) * mm});
            skLineSegment(sketch, "E2701", {"start": v(60.69, 4.85) * mm, "end": v(60.64, 4.86) * mm});
            skLineSegment(sketch, "E2702", {"start": v(60.64, 4.86) * mm, "end": v(60.6, 4.87) * mm});
            skLineSegment(sketch, "E2703", {"start": v(60.6, 4.87) * mm, "end": v(60.56, 4.89) * mm});
            skLineSegment(sketch, "E2704", {"start": v(60.56, 4.89) * mm, "end": v(60.52, 4.9) * mm});
            skLineSegment(sketch, "E2705", {"start": v(60.52, 4.9) * mm, "end": v(60.5, 4.9) * mm});
            skLineSegment(sketch, "E2706", {"start": v(60.5, 4.9) * mm, "end": v(60.46, 4.9) * mm});
            skLineSegment(sketch, "E2707", {"start": v(60.46, 4.9) * mm, "end": v(60.43, 4.91) * mm});
            skLineSegment(sketch, "E2708", {"start": v(60.43, 4.91) * mm, "end": v(60.4, 4.92) * mm});
            skLineSegment(sketch, "E2709", {"start": v(60.4, 4.92) * mm, "end": v(60.38, 4.92) * mm});
            skLineSegment(sketch, "E2710", {"start": v(60.38, 4.92) * mm, "end": v(60.36, 4.92) * mm});
            skLineSegment(sketch, "E2711", {"start": v(60.36, 4.92) * mm, "end": v(60.35, 4.91) * mm});
            skLineSegment(sketch, "E2712", {"start": v(60.35, 4.91) * mm, "end": v(60.33, 4.9) * mm});
            skLineSegment(sketch, "E2713", {"start": v(60.33, 4.9) * mm, "end": v(60.32, 4.9) * mm});
            skLineSegment(sketch, "E2714", {"start": v(60.32, 4.9) * mm, "end": v(60.3, 4.9) * mm});
            skLineSegment(sketch, "E2715", {"start": v(60.3, 4.9) * mm, "end": v(60.3, 4.88) * mm});
            skLineSegment(sketch, "E2716", {"start": v(60.3, 4.88) * mm, "end": v(60.29, 4.87) * mm});
            skLineSegment(sketch, "E2717", {"start": v(60.29, 4.87) * mm, "end": v(60.28, 4.85) * mm});
            skLineSegment(sketch, "E2718", {"start": v(60.28, 4.85) * mm, "end": v(60.28, 4.83) * mm});
            skLineSegment(sketch, "E2719", {"start": v(60.28, 4.83) * mm, "end": v(60.27, 4.81) * mm});
            skLineSegment(sketch, "E2720", {"start": v(60.27, 4.81) * mm, "end": v(60.27, 4.8) * mm});
            skLineSegment(sketch, "E2721", {"start": v(60.27, 4.8) * mm, "end": v(60.26, 4.77) * mm});
            skLineSegment(sketch, "E2722", {"start": v(60.26, 4.77) * mm, "end": v(60.26, 4.74) * mm});
            skLineSegment(sketch, "E2723", {"start": v(60.26, 4.74) * mm, "end": v(60.26, 4.71) * mm});
            skLineSegment(sketch, "E2724", {"start": v(60.26, 4.71) * mm, "end": v(60.26, 4.68) * mm});
            skLineSegment(sketch, "E2725", {"start": v(60.26, 4.68) * mm, "end": v(60.26, 4.65) * mm});
            skLineSegment(sketch, "E2726", {"start": v(60.26, 4.65) * mm, "end": v(60.26, 4.61) * mm});
            skLineSegment(sketch, "E2727", {"start": v(60.26, 4.61) * mm, "end": v(60.26, 4.57) * mm});
            skLineSegment(sketch, "E2728", {"start": v(60.26, 4.57) * mm, "end": v(60.26, 4.44) * mm});
            skLineSegment(sketch, "E2729", {"start": v(60.26, 4.44) * mm, "end": v(60.26, 4.31) * mm});
            skLineSegment(sketch, "E2730", {"start": v(60.26, 4.31) * mm, "end": v(60.25, 4.18) * mm});
            skLineSegment(sketch, "E2731", {"start": v(60.25, 4.18) * mm, "end": v(60.24, 4.05) * mm});
            skLineSegment(sketch, "E2732", {"start": v(60.24, 4.05) * mm, "end": v(60.24, 3.92) * mm});
            skLineSegment(sketch, "E2733", {"start": v(60.24, 3.92) * mm, "end": v(60.23, 3.79) * mm});
            skLineSegment(sketch, "E2734", {"start": v(60.23, 3.79) * mm, "end": v(60.22, 3.66) * mm});
            skLineSegment(sketch, "E2735", {"start": v(60.22, 3.66) * mm, "end": v(60.2, 3.53) * mm});
            skLineSegment(sketch, "E2736", {"start": v(60.2, 3.53) * mm, "end": v(60.19, 3.4) * mm});
            skLineSegment(sketch, "E2737", {"start": v(60.19, 3.4) * mm, "end": v(60.17, 3.3) * mm});
            skLineSegment(sketch, "E2738", {"start": v(60.17, 3.3) * mm, "end": v(60.16, 3.18) * mm});
            skLineSegment(sketch, "E2739", {"start": v(60.16, 3.18) * mm, "end": v(60.14, 3.07) * mm});
            skLineSegment(sketch, "E2740", {"start": v(60.14, 3.07) * mm, "end": v(60.12, 2.97) * mm});
            skLineSegment(sketch, "E2741", {"start": v(60.12, 2.97) * mm, "end": v(60.1, 2.88) * mm});
            skLineSegment(sketch, "E2742", {"start": v(60.1, 2.88) * mm, "end": v(60.08, 2.8) * mm});
            skLineSegment(sketch, "E2743", {"start": v(60.08, 2.8) * mm, "end": v(60.06, 2.72) * mm});
            skLineSegment(sketch, "E2744", {"start": v(60.06, 2.72) * mm, "end": v(60.05, 2.69) * mm});
            skLineSegment(sketch, "E2745", {"start": v(60.05, 2.69) * mm, "end": v(60.04, 2.66) * mm});
            skLineSegment(sketch, "E2746", {"start": v(60.04, 2.66) * mm, "end": v(60.05, 2.65) * mm});
            skLineSegment(sketch, "E2747", {"start": v(60.05, 2.65) * mm, "end": v(60.06, 2.64) * mm});
            skLineSegment(sketch, "E2748", {"start": v(60.06, 2.64) * mm, "end": v(60.07, 2.64) * mm});
            skLineSegment(sketch, "E2749", {"start": v(60.07, 2.64) * mm, "end": v(60.1, 2.65) * mm});
            skLineSegment(sketch, "E2750", {"start": v(60.1, 2.65) * mm, "end": v(60.13, 2.67) * mm});
            skLineSegment(sketch, "E2751", {"start": v(60.13, 2.67) * mm, "end": v(60.17, 2.7) * mm});
            skSolve(sketch);
        }
        {
            var Q0;
            Q0=makeQuery(id+"F10.imprint","IMPRINT",FACE,{"disambiguationData":[TD([[makeQuery(id+"F10.imprint","IMPRINT",EDGE,{"derivedFrom":sQuery(id+"F10.wireOp",EDGE,"E1111")}),-1.0]])]});
            var Q1;
            Q1=sQuery(id+"F10.wireOp",EDGE,"E2542");
            var Q2;
            Q2=sQuery(id+"F10.wireOp",EDGE,"E1272");
            var Q3;
            Q3=sQuery(id+"F10.wireOp",EDGE,"E1274");
            var Q4;
            Q4=sQuery(id+"F10.wireOp",EDGE,"E1277");
            var Q5;
            Q5=sQuery(id+"F10.wireOp",EDGE,"E2554");
            var Q6;
            Q6=sQuery(id+"F10.wireOp",EDGE,"E2537");
            var Q7;
            Q7=sQuery(id+"F10.wireOp",EDGE,"E2543");
            var Q8;
            Q8=sQuery(id+"F10.wireOp",EDGE,"E1271");
            var Q9;
            Q9=sQuery(id+"F10.wireOp",EDGE,"E1273");
            var Q10;
            Q10=sQuery(id+"F10.wireOp",EDGE,"E1276");
            var Q11;
            Q11=sQuery(id+"F10.wireOp",EDGE,"E2538");
            var Q12;
            Q12=sQuery(id+"F10.wireOp",EDGE,"E2555");
            var Q13;
            Q13=sQuery(id+"F10.wireOp",EDGE,"E2544");
            var Q14;
            Q14=sQuery(id+"F10.wireOp",EDGE,"E1269");
            var Q15;
            Q15=sQuery(id+"F10.wireOp",EDGE,"E2546");
            var Q16;
            Q16=sQuery(id+"F10.wireOp",EDGE,"E2539");
            var Q17;
            Q17=sQuery(id+"F10.wireOp",EDGE,"E1275");
            var Q18;
            Q18=sQuery(id+"F10.wireOp",EDGE,"E2545");
            var Q19;
            Q19=sQuery(id+"F10.wireOp",EDGE,"E2521");
            var Q20;
            Q20=sQuery(id+"F10.wireOp",EDGE,"E1278");
            var Q21;
            Q21=sQuery(id+"F10.wireOp",EDGE,"E2527");
            var Q22;
            Q22=sQuery(id+"F10.wireOp",EDGE,"E1282");
            var Q23;
            Q23=sQuery(id+"F10.wireOp",EDGE,"E1266");
            var Q24;
            Q24=sQuery(id+"F10.wireOp",EDGE,"E1268");
            var Q25;
            Q25=sQuery(id+"F10.wireOp",EDGE,"E2550");
            var Q26;
            Q26=sQuery(id+"F10.wireOp",EDGE,"E2533");
            var Q27;
            Q27=sQuery(id+"F10.wireOp",EDGE,"E2522");
            var Q28;
            Q28=sQuery(id+"F10.wireOp",EDGE,"E2528");
            var Q29;
            Q29=sQuery(id+"F10.wireOp",EDGE,"E1281");
            var Q30;
            Q30=sQuery(id+"F10.wireOp",EDGE,"E1270");
            var Q31;
            Q31=sQuery(id+"F10.wireOp",EDGE,"E2540");
            var Q32;
            Q32=sQuery(id+"F10.wireOp",EDGE,"E2549");
            var Q33;
            Q33=sQuery(id+"F10.wireOp",EDGE,"E2523");
            var Q34;
            Q34=sQuery(id+"F10.wireOp",EDGE,"E2529");
            var Q35;
            Q35=sQuery(id+"F10.wireOp",EDGE,"E1280");
            var Q36;
            Q36=sQuery(id+"F10.wireOp",EDGE,"E1267");
            var Q37;
            Q37=sQuery(id+"F10.wireOp",EDGE,"E2551");
            var Q38;
            Q38=sQuery(id+"F10.wireOp",EDGE,"E2534");
            var Q39;
            Q39=sQuery(id+"F10.wireOp",EDGE,"E2524");
            var Q40;
            Q40=sQuery(id+"F10.wireOp",EDGE,"E2530");
            var Q41;
            Q41=sQuery(id+"F10.wireOp",EDGE,"E1279");
            var Q42;
            Q42=sQuery(id+"F10.wireOp",EDGE,"E2519");
            var Q43;
            Q43=sQuery(id+"F10.wireOp",EDGE,"E2531");
            var Q44;
            Q44=sQuery(id+"F10.wireOp",EDGE,"E2547");
            var Q45;
            Q45=sQuery(id+"F10.wireOp",EDGE,"E2564");
            var Q46;
            Q46=sQuery(id+"F10.wireOp",EDGE,"E1259");
            var Q47;
            Q47=sQuery(id+"F10.wireOp",EDGE,"E1262");
            var Q48;
            Q48=sQuery(id+"F10.wireOp",EDGE,"E2560");
            var Q49;
            Q49=sQuery(id+"F10.wireOp",EDGE,"E2520");
            var Q50;
            Q50=sQuery(id+"F10.wireOp",EDGE,"E2552");
            var Q51;
            Q51=sQuery(id+"F10.wireOp",EDGE,"E2541");
            var Q52;
            Q52=sQuery(id+"F10.wireOp",EDGE,"E2525");
            var Q53;
            Q53=sQuery(id+"F10.wireOp",EDGE,"E1258");
            var Q54;
            Q54=sQuery(id+"F10.wireOp",EDGE,"E2561");
            var Q55;
            Q55=sQuery(id+"F10.wireOp",EDGE,"E1261");
            var Q56;
            Q56=sQuery(id+"F10.wireOp",EDGE,"E2526");
            var Q57;
            Q57=sQuery(id+"F10.wireOp",EDGE,"E2548");
            var Q58;
            Q58=sQuery(id+"F10.wireOp",EDGE,"E2535");
            var Q59;
            Q59=sQuery(id+"F10.wireOp",EDGE,"E1285");
            var Q60;
            Q60=sQuery(id+"F10.wireOp",EDGE,"E2515");
            var Q61;
            Q61=sQuery(id+"F10.wireOp",EDGE,"E1257");
            var Q62;
            Q62=sQuery(id+"F10.wireOp",EDGE,"E2562");
            var Q63;
            Q63=sQuery(id+"F10.wireOp",EDGE,"E1260");
            var Q64;
            Q64=sQuery(id+"F10.wireOp",EDGE,"E2511");
            var Q65;
            Q65=sQuery(id+"F10.wireOp",EDGE,"E1265");
            var Q66;
            Q66=sQuery(id+"F10.wireOp",EDGE,"E2494");
            var Q67;
            Q67=sQuery(id+"F10.wireOp",EDGE,"E2553");
            var Q68;
            Q68=sQuery(id+"F10.wireOp",EDGE,"E2452");
            var Q69;
            Q69=sQuery(id+"F10.wireOp",EDGE,"E2532");
            var Q70;
            Q70=sQuery(id+"F10.wireOp",EDGE,"E1284");
            var Q71;
            Q71=sQuery(id+"F10.wireOp",EDGE,"E2502");
            var Q72;
            Q72=sQuery(id+"F10.wireOp",EDGE,"E1256");
            var Q73;
            Q73=sQuery(id+"F10.wireOp",EDGE,"E2556");
            var Q74;
            Q74=sQuery(id+"F10.wireOp",EDGE,"E2512");
            var Q75;
            Q75=sQuery(id+"F10.wireOp",EDGE,"E2463");
            var Q76;
            Q76=sQuery(id+"F10.wireOp",EDGE,"E1264");
            var Q77;
            Q77=sQuery(id+"F10.wireOp",EDGE,"E1283");
            var Q78;
            Q78=sQuery(id+"F10.wireOp",EDGE,"E2536");
            var Q79;
            Q79=sQuery(id+"F10.wireOp",EDGE,"E2566");
            var Q80;
            Q80=sQuery(id+"F10.wireOp",EDGE,"E1255");
            var Q81;
            Q81=sQuery(id+"F10.wireOp",EDGE,"E2464");
            var Q82;
            Q82=sQuery(id+"F10.wireOp",EDGE,"E2506");
            var Q83;
            Q83=sQuery(id+"F10.wireOp",EDGE,"E1263");
            var Q84;
            Q84=sQuery(id+"F10.wireOp",EDGE,"E1253");
            var Q85;
            Q85=sQuery(id+"F10.wireOp",EDGE,"E2563");
            var Q86;
            Q86=sQuery(id+"F10.wireOp",EDGE,"E2465");
            var Q87;
            Q87=sQuery(id+"F10.wireOp",EDGE,"E2513");
            var Q88;
            Q88=sQuery(id+"F10.wireOp",EDGE,"E1249");
            var Q89;
            Q89=sQuery(id+"F10.wireOp",EDGE,"E2569");
            var Q90;
            Q90=sQuery(id+"F10.wireOp",EDGE,"E1252");
            var Q91;
            Q91=sQuery(id+"F10.wireOp",EDGE,"E2557");
            var Q92;
            Q92=sQuery(id+"F10.wireOp",EDGE,"E1239");
            var Q93;
            Q93=sQuery(id+"F10.wireOp",EDGE,"E2572");
            var Q94;
            Q94=sQuery(id+"F10.wireOp",EDGE,"E2466");
            var Q95;
            Q95=sQuery(id+"F10.wireOp",EDGE,"E2507");
            var Q96;
            Q96=sQuery(id+"F10.wireOp",EDGE,"E2570");
            var Q97;
            Q97=sQuery(id+"F10.wireOp",EDGE,"E1246");
            var Q98;
            Q98=sQuery(id+"F10.wireOp",EDGE,"E1230");
            var Q99;
            Q99=sQuery(id+"F10.wireOp",EDGE,"E1254");
            var Q100;
            Q100=sQuery(id+"F10.wireOp",EDGE,"E1237");
            var Q101;
            Q101=sQuery(id+"F10.wireOp",EDGE,"E2558");
            var Q102;
            Q102=sQuery(id+"F10.wireOp",EDGE,"E2567");
            var Q103;
            Q103=sQuery(id+"F10.wireOp",EDGE,"E2573");
            var Q104;
            Q104=sQuery(id+"F10.wireOp",EDGE,"E2469");
            var Q105;
            Q105=sQuery(id+"F10.wireOp",EDGE,"E2598");
            var Q106;
            Q106=sQuery(id+"F10.wireOp",EDGE,"E1224");
            var Q107;
            Q107=sQuery(id+"F10.wireOp",EDGE,"E2514");
            var Q108;
            Q108=sQuery(id+"F10.wireOp",EDGE,"E1245");
            var Q109;
            Q109=sQuery(id+"F10.wireOp",EDGE,"E1229");
            var Q110;
            Q110=sQuery(id+"F10.wireOp",EDGE,"E2592");
            var Q111;
            Q111=sQuery(id+"F10.wireOp",EDGE,"E1214");
            var Q112;
            Q112=sQuery(id+"F10.wireOp",EDGE,"E1251");
            var Q113;
            Q113=sQuery(id+"F10.wireOp",EDGE,"E2559");
            var Q114;
            Q114=sQuery(id+"F10.wireOp",EDGE,"E1236");
            var Q115;
            Q115=sQuery(id+"F10.wireOp",EDGE,"E2568");
            var Q116;
            Q116=sQuery(id+"F10.wireOp",EDGE,"E2574");
            var Q117;
            Q117=sQuery(id+"F10.wireOp",EDGE,"E2460");
            var Q118;
            Q118=sQuery(id+"F10.wireOp",EDGE,"E1223");
            var Q119;
            Q119=sQuery(id+"F10.wireOp",EDGE,"E2517");
            var Q120;
            Q120=sQuery(id+"F10.wireOp",EDGE,"E1244");
            var Q121;
            Q121=sQuery(id+"F10.wireOp",EDGE,"E2571");
            var Q122;
            Q122=sQuery(id+"F10.wireOp",EDGE,"E1213");
            var Q123;
            Q123=sQuery(id+"F10.wireOp",EDGE,"E2576");
            var Q124;
            Q124=sQuery(id+"F10.wireOp",EDGE,"E2565");
            var Q125;
            Q125=sQuery(id+"F10.wireOp",EDGE,"E1238");
            var Q126;
            Q126=sQuery(id+"F10.wireOp",EDGE,"E2467");
            var Q127;
            Q127=sQuery(id+"F10.wireOp",EDGE,"E2508");
            var Q128;
            Q128=sQuery(id+"F10.wireOp",EDGE,"E1240");
            var Q129;
            Q129=sQuery(id+"F10.wireOp",EDGE,"E1243");
            var Q130;
            Q130=sQuery(id+"F10.wireOp",EDGE,"E1228");
            var Q131;
            Q131=sQuery(id+"F10.wireOp",EDGE,"E1212");
            var Q132;
            Q132=sQuery(id+"F10.wireOp",EDGE,"E2586");
            var Q133;
            Q133=sQuery(id+"F10.wireOp",EDGE,"E1235");
            var Q134;
            Q134=sQuery(id+"F10.wireOp",EDGE,"E2461");
            var Q135;
            Q135=sQuery(id+"F10.wireOp",EDGE,"E2518");
            var Q136;
            Q136=sQuery(id+"F10.wireOp",EDGE,"E1242");
            var Q137;
            Q137=sQuery(id+"F10.wireOp",EDGE,"E1227");
            var Q138;
            Q138=sQuery(id+"F10.wireOp",EDGE,"E1211");
            var Q139;
            Q139=sQuery(id+"F10.wireOp",EDGE,"E2593");
            var Q140;
            Q140=sQuery(id+"F10.wireOp",EDGE,"E1234");
            var Q141;
            Q141=sQuery(id+"F10.wireOp",EDGE,"E2468");
            var Q142;
            Q142=sQuery(id+"F10.wireOp",EDGE,"E2509");
            var Q143;
            Q143=sQuery(id+"F10.wireOp",EDGE,"E1241");
            var Q144;
            Q144=sQuery(id+"F10.wireOp",EDGE,"E1226");
            var Q145;
            Q145=sQuery(id+"F10.wireOp",EDGE,"E2577");
            var Q146;
            Q146=sQuery(id+"F10.wireOp",EDGE,"E1233");
            var Q147;
            Q147=sQuery(id+"F10.wireOp",EDGE,"E1250");
            var Q148;
            Q148=sQuery(id+"F10.wireOp",EDGE,"E2462");
            var Q149;
            Q149=sQuery(id+"F10.wireOp",EDGE,"E2516");
            var Q150;
            Q150=sQuery(id+"F10.wireOp",EDGE,"E1225");
            var Q151;
            Q151=sQuery(id+"F10.wireOp",EDGE,"E2594");
            var Q152;
            Q152=sQuery(id+"F10.wireOp",EDGE,"E1248");
            var Q153;
            Q153=sQuery(id+"F10.wireOp",EDGE,"E1232");
            var Q154;
            Q154=sQuery(id+"F10.wireOp",EDGE,"E2243");
            var Q155;
            Q155=sQuery(id+"F10.wireOp",EDGE,"E2510");
            var Q156;
            Q156=sQuery(id+"F10.wireOp",EDGE,"E1221");
            var Q157;
            Q157=sQuery(id+"F10.wireOp",EDGE,"E2233");
            var Q158;
            Q158=sQuery(id+"F10.wireOp",EDGE,"E2587");
            var Q159;
            Q159=sQuery(id+"F10.wireOp",EDGE,"E2247");
            var Q160;
            Q160=sQuery(id+"F10.wireOp",EDGE,"E2214");
            var Q161;
            Q161=sQuery(id+"F10.wireOp",EDGE,"E2198");
            var Q162;
            Q162=sQuery(id+"F10.wireOp",EDGE,"E1247");
            var Q163;
            Q163=sQuery(id+"F10.wireOp",EDGE,"E1231");
            var Q164;
            Q164=sQuery(id+"F10.wireOp",EDGE,"E2241");
            var Q165;
            Q165=sQuery(id+"F10.wireOp",EDGE,"E1220");
            var Q166;
            Q166=sQuery(id+"F10.wireOp",EDGE,"E2578");
            var Q167;
            Q167=sQuery(id+"F10.wireOp",EDGE,"E2221");
            var Q168;
            Q168=sQuery(id+"F10.wireOp",EDGE,"E2244");
            var Q169;
            Q169=sQuery(id+"F10.wireOp",EDGE,"E2211");
            var Q170;
            Q170=sQuery(id+"F10.wireOp",EDGE,"E2242");
            var Q171;
            Q171=sQuery(id+"F10.wireOp",EDGE,"E1222");
            var Q172;
            Q172=sQuery(id+"F10.wireOp",EDGE,"E2588");
            var Q173;
            Q173=sQuery(id+"F10.wireOp",EDGE,"E2282");
            var Q174;
            Q174=sQuery(id+"F10.wireOp",EDGE,"E2248");
            var Q175;
            Q175=sQuery(id+"F10.wireOp",EDGE,"E2215");
            var Q176;
            Q176=sQuery(id+"F10.wireOp",EDGE,"E2238");
            var Q177;
            Q177=sQuery(id+"F10.wireOp",EDGE,"E2205");
            var Q178;
            Q178=sQuery(id+"F10.wireOp",EDGE,"E2302");
            var Q179;
            Q179=sQuery(id+"F10.wireOp",EDGE,"E2376");
            var Q180;
            Q180=sQuery(id+"F10.wireOp",EDGE,"E2398");
            var Q181;
            Q181=sQuery(id+"F10.wireOp",EDGE,"E2285");
            var Q182;
            Q182=sQuery(id+"F10.wireOp",EDGE,"E2237");
            var Q183;
            Q183=sQuery(id+"F10.wireOp",EDGE,"E2366");
            var Q184;
            Q184=sQuery(id+"F10.wireOp",EDGE,"E2324");
            var Q185;
            Q185=sQuery(id+"F10.wireOp",EDGE,"E2253");
            var Q186;
            Q186=sQuery(id+"F10.wireOp",EDGE,"E2327");
            var Q187;
            Q187=sQuery(id+"F10.wireOp",EDGE,"E2382");
            var Q188;
            Q188=sQuery(id+"F10.wireOp",EDGE,"E1219");
            var Q189;
            Q189=sQuery(id+"F10.wireOp",EDGE,"E2373");
            var Q190;
            Q190=sQuery(id+"F10.wireOp",EDGE,"E2595");
            var Q191;
            Q191=sQuery(id+"F10.wireOp",EDGE,"E2249");
            var Q192;
            Q192=sQuery(id+"F10.wireOp",EDGE,"E2239");
            var Q193;
            Q193=sQuery(id+"F10.wireOp",EDGE,"E2212");
            var Q194;
            Q194=sQuery(id+"F10.wireOp",EDGE,"E2399");
            var Q195;
            Q195=sQuery(id+"F10.wireOp",EDGE,"E2199");
            var Q196;
            Q196=sQuery(id+"F10.wireOp",EDGE,"E2295");
            var Q197;
            Q197=sQuery(id+"F10.wireOp",EDGE,"E2263");
            var Q198;
            Q198=sQuery(id+"F10.wireOp",EDGE,"E2392");
            var Q199;
            Q199=sQuery(id+"F10.wireOp",EDGE,"E2269");
            var Q200;
            Q200=sQuery(id+"F10.wireOp",EDGE,"E2343");
            var Q201;
            Q201=sQuery(id+"F10.wireOp",EDGE,"E2230");
            var Q202;
            Q202=sQuery(id+"F10.wireOp",EDGE,"E2359");
            var Q203;
            Q203=sQuery(id+"F10.wireOp",EDGE,"E2311");
            var Q204;
            Q204=sQuery(id+"F10.wireOp",EDGE,"E1218");
            var Q205;
            Q205=sQuery(id+"F10.wireOp",EDGE,"E2371");
            var Q206;
            Q206=sQuery(id+"F10.wireOp",EDGE,"E2582");
            var Q207;
            Q207=sQuery(id+"F10.wireOp",EDGE,"E2250");
            var Q208;
            Q208=sQuery(id+"F10.wireOp",EDGE,"E2240");
            var Q209;
            Q209=sQuery(id+"F10.wireOp",EDGE,"E2400");
            var Q210;
            Q210=sQuery(id+"F10.wireOp",EDGE,"E2222");
            var Q211;
            Q211=sQuery(id+"F10.wireOp",EDGE,"E2303");
            var Q212;
            Q212=sQuery(id+"F10.wireOp",EDGE,"E2196");
            var Q213;
            Q213=sQuery(id+"F10.wireOp",EDGE,"E2383");
            var Q214;
            Q214=sQuery(id+"F10.wireOp",EDGE,"E2292");
            var Q215;
            Q215=sQuery(id+"F10.wireOp",EDGE,"E2260");
            var Q216;
            Q216=sQuery(id+"F10.wireOp",EDGE,"E2340");
            var Q217;
            Q217=sQuery(id+"F10.wireOp",EDGE,"E2227");
            var Q218;
            Q218=sQuery(id+"F10.wireOp",EDGE,"E2356");
            var Q219;
            Q219=sQuery(id+"F10.wireOp",EDGE,"E2308");
            var Q220;
            Q220=sQuery(id+"F10.wireOp",EDGE,"E1217");
            var Q221;
            Q221=sQuery(id+"F10.wireOp",EDGE,"E2374");
            var Q222;
            Q222=sQuery(id+"F10.wireOp",EDGE,"E2245");
            var Q223;
            Q223=sQuery(id+"F10.wireOp",EDGE,"E2579");
            var Q224;
            Q224=sQuery(id+"F10.wireOp",EDGE,"E2401");
            var Q225;
            Q225=sQuery(id+"F10.wireOp",EDGE,"E2216");
            var Q226;
            Q226=sQuery(id+"F10.wireOp",EDGE,"E2206");
            var Q227;
            Q227=sQuery(id+"F10.wireOp",EDGE,"E2296");
            var Q228;
            Q228=sQuery(id+"F10.wireOp",EDGE,"E2393");
            var Q229;
            Q229=sQuery(id+"F10.wireOp",EDGE,"E2270");
            var Q230;
            Q230=sQuery(id+"F10.wireOp",EDGE,"E2231");
            var Q231;
            Q231=sQuery(id+"F10.wireOp",EDGE,"E2367");
            var Q232;
            Q232=sQuery(id+"F10.wireOp",EDGE,"E2254");
            var Q233;
            Q233=sQuery(id+"F10.wireOp",EDGE,"E2279");
            var Q234;
            Q234=sQuery(id+"F10.wireOp",EDGE,"E2350");
            var Q235;
            Q235=sQuery(id+"F10.wireOp",EDGE,"E2318");
            var Q236;
            Q236=sQuery(id+"F10.wireOp",EDGE,"E1216");
            var Q237;
            Q237=sQuery(id+"F10.wireOp",EDGE,"E2246");
            var Q238;
            Q238=sQuery(id+"F10.wireOp",EDGE,"E2375");
            var Q239;
            Q239=sQuery(id+"F10.wireOp",EDGE,"E2406");
            var Q240;
            Q240=sQuery(id+"F10.wireOp",EDGE,"E2405");
            var Q241;
            Q241=sQuery(id+"F10.wireOp",EDGE,"E2589");
            var Q242;
            Q242=sQuery(id+"F10.wireOp",EDGE,"E2411");
            var Q243;
            Q243=sQuery(id+"F10.wireOp",EDGE,"E2395");
            var Q244;
            Q244=sQuery(id+"F10.wireOp",EDGE,"E2217");
            var Q245;
            Q245=sQuery(id+"F10.wireOp",EDGE,"E2304");
            var Q246;
            Q246=sQuery(id+"F10.wireOp",EDGE,"E2265");
            var Q247;
            Q247=sQuery(id+"F10.wireOp",EDGE,"E2200");
            var Q248;
            Q248=sQuery(id+"F10.wireOp",EDGE,"E2377");
            var Q249;
            Q249=sQuery(id+"F10.wireOp",EDGE,"E2264");
            var Q250;
            Q250=sQuery(id+"F10.wireOp",EDGE,"E2228");
            var Q251;
            Q251=sQuery(id+"F10.wireOp",EDGE,"E2360");
            var Q252;
            Q252=sQuery(id+"F10.wireOp",EDGE,"E2312");
            var Q253;
            Q253=sQuery(id+"F10.wireOp",EDGE,"E2276");
            var Q254;
            Q254=sQuery(id+"F10.wireOp",EDGE,"E2334");
            var Q255;
            Q255=sQuery(id+"F10.wireOp",EDGE,"E1215");
            var Q256;
            Q256=sQuery(id+"F10.wireOp",EDGE,"E2251");
            var Q257;
            Q257=sQuery(id+"F10.wireOp",EDGE,"E2372");
            var Q258;
            Q258=sQuery(id+"F10.wireOp",EDGE,"E2407");
            var Q259;
            Q259=sQuery(id+"F10.wireOp",EDGE,"E2213");
            var Q260;
            Q260=sQuery(id+"F10.wireOp",EDGE,"E2403");
            var Q261;
            Q261=sQuery(id+"F10.wireOp",EDGE,"E2396");
            var Q262;
            Q262=sQuery(id+"F10.wireOp",EDGE,"E2596");
            var Q263;
            Q263=sQuery(id+"F10.wireOp",EDGE,"E1288");
            var Q264;
            Q264=sQuery(id+"F10.wireOp",EDGE,"E2256");
            var Q265;
            Q265=sQuery(id+"F10.wireOp",EDGE,"E2207");
            var Q266;
            Q266=sQuery(id+"F10.wireOp",EDGE,"E2297");
            var Q267;
            Q267=sQuery(id+"F10.wireOp",EDGE,"E2232");
            var Q268;
            Q268=sQuery(id+"F10.wireOp",EDGE,"E2368");
            var Q269;
            Q269=sQuery(id+"F10.wireOp",EDGE,"E2255");
            var Q270;
            Q270=sQuery(id+"F10.wireOp",EDGE,"E2384");
            var Q271;
            Q271=sQuery(id+"F10.wireOp",EDGE,"E2319");
            var Q272;
            Q272=sQuery(id+"F10.wireOp",EDGE,"E2286");
            var Q273;
            Q273=sQuery(id+"F10.wireOp",EDGE,"E2328");
            var Q274;
            Q274=sQuery(id+"F10.wireOp",EDGE,"E2408");
            var Q275;
            Q275=sQuery(id+"F10.wireOp",EDGE,"E2424");
            var Q276;
            Q276=sQuery(id+"F10.wireOp",EDGE,"E2504");
            var Q277;
            Q277=sQuery(id+"F10.wireOp",EDGE,"E2414");
            var Q278;
            Q278=sQuery(id+"F10.wireOp",EDGE,"E2495");
            var Q279;
            Q279=sQuery(id+"F10.wireOp",EDGE,"E2440");
            var Q280;
            Q280=sQuery(id+"F10.wireOp",EDGE,"E2472");
            var Q281;
            Q281=sQuery(id+"F10.wireOp",EDGE,"E2195");
            var Q282;
            Q282=sQuery(id+"F10.wireOp",EDGE,"E1139");
            var Q283;
            Q283=sQuery(id+"F10.wireOp",EDGE,"E2193");
            var Q284;
            Q284=sQuery(id+"F10.wireOp",EDGE,"E2257");
            var Q285;
            Q285=sQuery(id+"F10.wireOp",EDGE,"E2404");
            var Q286;
            Q286=sQuery(id+"F10.wireOp",EDGE,"E2220");
            var Q287;
            Q287=sQuery(id+"F10.wireOp",EDGE,"E2397");
            var Q288;
            Q288=sQuery(id+"F10.wireOp",EDGE,"E1188");
            var Q289;
            Q289=sQuery(id+"F10.wireOp",EDGE,"E2583");
            var Q290;
            Q290=sQuery(id+"F10.wireOp",EDGE,"E1287");
            var Q291;
            Q291=sQuery(id+"F10.wireOp",EDGE,"E2614");
            var Q292;
            Q292=sQuery(id+"F10.wireOp",EDGE,"E2630");
            var Q293;
            Q293=sQuery(id+"F10.wireOp",EDGE,"E2298");
            var Q294;
            Q294=sQuery(id+"F10.wireOp",EDGE,"E2482");
            var Q295;
            Q295=sQuery(id+"F10.wireOp",EDGE,"E2266");
            var Q296;
            Q296=sQuery(id+"F10.wireOp",EDGE,"E1162");
            var Q297;
            Q297=sQuery(id+"F10.wireOp",EDGE,"E1210");
            var Q298;
            Q298=sQuery(id+"F10.wireOp",EDGE,"E2201");
            var Q299;
            Q299=sQuery(id+"F10.wireOp",EDGE,"E2223");
            var Q300;
            Q300=sQuery(id+"F10.wireOp",EDGE,"E2394");
            var Q301;
            Q301=sQuery(id+"F10.wireOp",EDGE,"E2361");
            var Q302;
            Q302=sQuery(id+"F10.wireOp",EDGE,"E1292");
            var Q303;
            Q303=sQuery(id+"F10.wireOp",EDGE,"E2313");
            var Q304;
            Q304=sQuery(id+"F10.wireOp",EDGE,"E2280");
            var Q305;
            Q305=sQuery(id+"F10.wireOp",EDGE,"E2409");
            var Q306;
            Q306=sQuery(id+"F10.wireOp",EDGE,"E2425");
            var Q307;
            Q307=sQuery(id+"F10.wireOp",EDGE,"E2344");
            var Q308;
            Q308=sQuery(id+"F10.wireOp",EDGE,"E2415");
            var Q309;
            Q309=sQuery(id+"F10.wireOp",EDGE,"E2496");
            var Q310;
            Q310=sQuery(id+"F10.wireOp",EDGE,"E2441");
            var Q311;
            Q311=sQuery(id+"F10.wireOp",EDGE,"E2609");
            var Q312;
            Q312=sQuery(id+"F10.wireOp",EDGE,"E2431");
            var Q313;
            Q313=sQuery(id+"F10.wireOp",EDGE,"E2505");
            var Q314;
            Q314=sQuery(id+"F10.wireOp",EDGE,"E2488");
            var Q315;
            Q315=sQuery(id+"F10.wireOp",EDGE,"E1150");
            var Q316;
            Q316=sQuery(id+"F10.wireOp",EDGE,"E1134");
            var Q317;
            Q317=sQuery(id+"F10.wireOp",EDGE,"E1198");
            var Q318;
            Q318=sQuery(id+"F10.wireOp",EDGE,"E1166");
            var Q319;
            Q319=sQuery(id+"F10.wireOp",EDGE,"E2618");
            var Q320;
            Q320=sQuery(id+"F10.wireOp",EDGE,"E1183");
            var Q321;
            Q321=sQuery(id+"F10.wireOp",EDGE,"E2210");
            var Q322;
            Q322=sQuery(id+"F10.wireOp",EDGE,"E1187");
            var Q323;
            Q323=sQuery(id+"F10.wireOp",EDGE,"E2194");
            var Q324;
            Q324=sQuery(id+"F10.wireOp",EDGE,"E2218");
            var Q325;
            Q325=sQuery(id+"F10.wireOp",EDGE,"E2402");
            var Q326;
            Q326=sQuery(id+"F10.wireOp",EDGE,"E1286");
            var Q327;
            Q327=sQuery(id+"F10.wireOp",EDGE,"E1300");
            var Q328;
            Q328=sQuery(id+"F10.wireOp",EDGE,"E2300");
            var Q329;
            Q329=sQuery(id+"F10.wireOp",EDGE,"E2261");
            var Q330;
            Q330=sQuery(id+"F10.wireOp",EDGE,"E2580");
            var Q331;
            Q331=sQuery(id+"F10.wireOp",EDGE,"E2615");
            var Q332;
            Q332=sQuery(id+"F10.wireOp",EDGE,"E2628");
            var Q333;
            Q333=sQuery(id+"F10.wireOp",EDGE,"E2208");
            var Q334;
            Q334=sQuery(id+"F10.wireOp",EDGE,"E2224");
            var Q335;
            Q335=sQuery(id+"F10.wireOp",EDGE,"E1161");
            var Q336;
            Q336=sQuery(id+"F10.wireOp",EDGE,"E1209");
            var Q337;
            Q337=sQuery(id+"F10.wireOp",EDGE,"E1290");
            var Q338;
            Q338=sQuery(id+"F10.wireOp",EDGE,"E2410");
            var Q339;
            Q339=sQuery(id+"F10.wireOp",EDGE,"E2352");
            var Q340;
            Q340=sQuery(id+"F10.wireOp",EDGE,"E2426");
            var Q341;
            Q341=sQuery(id+"F10.wireOp",EDGE,"E2378");
            var Q342;
            Q342=sQuery(id+"F10.wireOp",EDGE,"E2320");
            var Q343;
            Q343=sQuery(id+"F10.wireOp",EDGE,"E2287");
            var Q344;
            Q344=sQuery(id+"F10.wireOp",EDGE,"E2416");
            var Q345;
            Q345=sQuery(id+"F10.wireOp",EDGE,"E2497");
            var Q346;
            Q346=sQuery(id+"F10.wireOp",EDGE,"E2442");
            var Q347;
            Q347=sQuery(id+"F10.wireOp",EDGE,"E2351");
            var Q348;
            Q348=sQuery(id+"F10.wireOp",EDGE,"E2432");
            var Q349;
            Q349=sQuery(id+"F10.wireOp",EDGE,"E2489");
            var Q350;
            Q350=sQuery(id+"F10.wireOp",EDGE,"E2602");
            var Q351;
            Q351=sQuery(id+"F10.wireOp",EDGE,"E1149");
            var Q352;
            Q352=sQuery(id+"F10.wireOp",EDGE,"E1133");
            var Q353;
            Q353=sQuery(id+"F10.wireOp",EDGE,"E1197");
            var Q354;
            Q354=sQuery(id+"F10.wireOp",EDGE,"E2479");
            var Q355;
            Q355=sQuery(id+"F10.wireOp",EDGE,"E2625");
            var Q356;
            Q356=sQuery(id+"F10.wireOp",EDGE,"E1182");
            var Q357;
            Q357=sQuery(id+"F10.wireOp",EDGE,"E2219");
            var Q358;
            Q358=sQuery(id+"F10.wireOp",EDGE,"E2629");
            var Q359;
            Q359=sQuery(id+"F10.wireOp",EDGE,"E2188");
            var Q360;
            Q360=sQuery(id+"F10.wireOp",EDGE,"E2236");
            var Q361;
            Q361=sQuery(id+"F10.wireOp",EDGE,"E2197");
            var Q362;
            Q362=sQuery(id+"F10.wireOp",EDGE,"E2252");
            var Q363;
            Q363=sQuery(id+"F10.wireOp",EDGE,"E2293");
            var Q364;
            Q364=sQuery(id+"F10.wireOp",EDGE,"E2590");
            var Q365;
            Q365=sQuery(id+"F10.wireOp",EDGE,"E2611");
            var Q366;
            Q366=sQuery(id+"F10.wireOp",EDGE,"E1160");
            var Q367;
            Q367=sQuery(id+"F10.wireOp",EDGE,"E1208");
            var Q368;
            Q368=sQuery(id+"F10.wireOp",EDGE,"E1289");
            var Q369;
            Q369=sQuery(id+"F10.wireOp",EDGE,"E2417");
            var Q370;
            Q370=sQuery(id+"F10.wireOp",EDGE,"E2369");
            var Q371;
            Q371=sQuery(id+"F10.wireOp",EDGE,"E2314");
            var Q372;
            Q372=sQuery(id+"F10.wireOp",EDGE,"E2498");
            var Q373;
            Q373=sQuery(id+"F10.wireOp",EDGE,"E2443");
            var Q374;
            Q374=sQuery(id+"F10.wireOp",EDGE,"E2385");
            var Q375;
            Q375=sQuery(id+"F10.wireOp",EDGE,"E2433");
            var Q376;
            Q376=sQuery(id+"F10.wireOp",EDGE,"E2271");
            var Q377;
            Q377=sQuery(id+"F10.wireOp",EDGE,"E2490");
            var Q378;
            Q378=sQuery(id+"F10.wireOp",EDGE,"E1148");
            var Q379;
            Q379=sQuery(id+"F10.wireOp",EDGE,"E1132");
            var Q380;
            Q380=sQuery(id+"F10.wireOp",EDGE,"E1196");
            var Q381;
            Q381=sQuery(id+"F10.wireOp",EDGE,"E2335");
            var Q382;
            Q382=sQuery(id+"F10.wireOp",EDGE,"E2610");
            var Q383;
            Q383=sQuery(id+"F10.wireOp",EDGE,"E2473");
            var Q384;
            Q384=sQuery(id+"F10.wireOp",EDGE,"E2619");
            var Q385;
            Q385=sQuery(id+"F10.wireOp",EDGE,"E1165");
            var Q386;
            Q386=sQuery(id+"F10.wireOp",EDGE,"E2204");
            var Q387;
            Q387=sQuery(id+"F10.wireOp",EDGE,"E2301");
            var Q388;
            Q388=sQuery(id+"F10.wireOp",EDGE,"E2262");
            var Q389;
            Q389=sQuery(id+"F10.wireOp",EDGE,"E2229");
            var Q390;
            Q390=sQuery(id+"F10.wireOp",EDGE,"E2584");
            var Q391;
            Q391=sQuery(id+"F10.wireOp",EDGE,"E2412");
            var Q392;
            Q392=sQuery(id+"F10.wireOp",EDGE,"E2444");
            var Q393;
            Q393=sQuery(id+"F10.wireOp",EDGE,"E2631");
            var Q394;
            Q394=sQuery(id+"F10.wireOp",EDGE,"E1159");
            var Q395;
            Q395=sQuery(id+"F10.wireOp",EDGE,"E2501");
            var Q396;
            Q396=sQuery(id+"F10.wireOp",EDGE,"E1207");
            var Q397;
            Q397=sQuery(id+"F10.wireOp",EDGE,"E2427");
            var Q398;
            Q398=sQuery(id+"F10.wireOp",EDGE,"E2434");
            var Q399;
            Q399=sQuery(id+"F10.wireOp",EDGE,"E2379");
            var Q400;
            Q400=sQuery(id+"F10.wireOp",EDGE,"E2321");
            var Q401;
            Q401=sQuery(id+"F10.wireOp",EDGE,"E2362");
            var Q402;
            Q402=sQuery(id+"F10.wireOp",EDGE,"E2491");
            var Q403;
            Q403=sQuery(id+"F10.wireOp",EDGE,"E2281");
            var Q404;
            Q404=sQuery(id+"F10.wireOp",EDGE,"E1147");
            var Q405;
            Q405=sQuery(id+"F10.wireOp",EDGE,"E1131");
            var Q406;
            Q406=sQuery(id+"F10.wireOp",EDGE,"E1195");
            var Q407;
            Q407=sQuery(id+"F10.wireOp",EDGE,"E2329");
            var Q408;
            Q408=sQuery(id+"F10.wireOp",EDGE,"E2603");
            var Q409;
            Q409=sQuery(id+"F10.wireOp",EDGE,"E2480");
            var Q410;
            Q410=sQuery(id+"F10.wireOp",EDGE,"E2626");
            var Q411;
            Q411=sQuery(id+"F10.wireOp",EDGE,"E1181");
            var Q412;
            Q412=sQuery(id+"F10.wireOp",EDGE,"E2234");
            var Q413;
            Q413=sQuery(id+"F10.wireOp",EDGE,"E2202");
            var Q414;
            Q414=sQuery(id+"F10.wireOp",EDGE,"E2149");
            var Q415;
            Q415=sQuery(id+"F10.wireOp",EDGE,"E2294");
            var Q416;
            Q416=sQuery(id+"F10.wireOp",EDGE,"E2259");
            var Q417;
            Q417=sQuery(id+"F10.wireOp",EDGE,"E2413");
            var Q418;
            Q418=sQuery(id+"F10.wireOp",EDGE,"E2591");
            var Q419;
            Q419=sQuery(id+"F10.wireOp",EDGE,"E1157");
            var Q420;
            Q420=sQuery(id+"F10.wireOp",EDGE,"E1205");
            var Q421;
            Q421=sQuery(id+"F10.wireOp",EDGE,"E2435");
            var Q422;
            Q422=sQuery(id+"F10.wireOp",EDGE,"E2492");
            var Q423;
            Q423=sQuery(id+"F10.wireOp",EDGE,"E2421");
            var Q424;
            Q424=sQuery(id+"F10.wireOp",EDGE,"E2499");
            var Q425;
            Q425=sQuery(id+"F10.wireOp",EDGE,"E2389");
            var Q426;
            Q426=sQuery(id+"F10.wireOp",EDGE,"E2437");
            var Q427;
            Q427=sQuery(id+"F10.wireOp",EDGE,"E2605");
            var Q428;
            Q428=sQuery(id+"F10.wireOp",EDGE,"E2627");
            var Q429;
            Q429=sQuery(id+"F10.wireOp",EDGE,"E2353");
            var Q430;
            Q430=sQuery(id+"F10.wireOp",EDGE,"E2305");
            var Q431;
            Q431=sQuery(id+"F10.wireOp",EDGE,"E2288");
            var Q432;
            Q432=sQuery(id+"F10.wireOp",EDGE,"E1146");
            var Q433;
            Q433=sQuery(id+"F10.wireOp",EDGE,"E1130");
            var Q434;
            Q434=sQuery(id+"F10.wireOp",EDGE,"E1194");
            var Q435;
            Q435=sQuery(id+"F10.wireOp",EDGE,"E2345");
            var Q436;
            Q436=sQuery(id+"F10.wireOp",EDGE,"E2474");
            var Q437;
            Q437=sQuery(id+"F10.wireOp",EDGE,"E1164");
            var Q438;
            Q438=sQuery(id+"F10.wireOp",EDGE,"E2190");
            var Q439;
            Q439=sQuery(id+"F10.wireOp",EDGE,"E2447");
            var Q440;
            Q440=sQuery(id+"F10.wireOp",EDGE,"E2140");
            var Q441;
            Q441=sQuery(id+"F10.wireOp",EDGE,"E2156");
            var Q442;
            Q442=sQuery(id+"F10.wireOp",EDGE,"E2182");
            var Q443;
            Q443=sQuery(id+"F10.wireOp",EDGE,"E2126");
            var Q444;
            Q444=sQuery(id+"F10.wireOp",EDGE,"E2456");
            var Q445;
            Q445=sQuery(id+"F10.wireOp",EDGE,"E2258");
            var Q446;
            Q446=sQuery(id+"F10.wireOp",EDGE,"E2209");
            var Q447;
            Q447=sQuery(id+"F10.wireOp",EDGE,"E2225");
            var Q448;
            Q448=sQuery(id+"F10.wireOp",EDGE,"E2299");
            var Q449;
            Q449=sQuery(id+"F10.wireOp",EDGE,"E2177");
            var Q450;
            Q450=sQuery(id+"F10.wireOp",EDGE,"E2575");
            var Q451;
            Q451=sQuery(id+"F10.wireOp",EDGE,"E2438");
            var Q452;
            Q452=sQuery(id+"F10.wireOp",EDGE,"E2493");
            var Q453;
            Q453=sQuery(id+"F10.wireOp",EDGE,"E1156");
            var Q454;
            Q454=sQuery(id+"F10.wireOp",EDGE,"E1204");
            var Q455;
            Q455=sQuery(id+"F10.wireOp",EDGE,"E2500");
            var Q456;
            Q456=sQuery(id+"F10.wireOp",EDGE,"E2428");
            var Q457;
            Q457=sQuery(id+"F10.wireOp",EDGE,"E2357");
            var Q458;
            Q458=sQuery(id+"F10.wireOp",EDGE,"E2380");
            var Q459;
            Q459=sQuery(id+"F10.wireOp",EDGE,"E2325");
            var Q460;
            Q460=sQuery(id+"F10.wireOp",EDGE,"E2612");
            var Q461;
            Q461=sQuery(id+"F10.wireOp",EDGE,"E2621");
            var Q462;
            Q462=sQuery(id+"F10.wireOp",EDGE,"E1145");
            var Q463;
            Q463=sQuery(id+"F10.wireOp",EDGE,"E1129");
            var Q464;
            Q464=sQuery(id+"F10.wireOp",EDGE,"E1193");
            var Q465;
            Q465=sQuery(id+"F10.wireOp",EDGE,"E2272");
            var Q466;
            Q466=sQuery(id+"F10.wireOp",EDGE,"E2336");
            var Q467;
            Q467=sQuery(id+"F10.wireOp",EDGE,"E2481");
            var Q468;
            Q468=sQuery(id+"F10.wireOp",EDGE,"E2191");
            var Q469;
            Q469=sQuery(id+"F10.wireOp",EDGE,"E1180");
            var Q470;
            Q470=sQuery(id+"F10.wireOp",EDGE,"E2448");
            var Q471;
            Q471=sQuery(id+"F10.wireOp",EDGE,"E2141");
            var Q472;
            Q472=sQuery(id+"F10.wireOp",EDGE,"E2457");
            var Q473;
            Q473=sQuery(id+"F10.wireOp",EDGE,"E2150");
            var Q474;
            Q474=sQuery(id+"F10.wireOp",EDGE,"E2166");
            var Q475;
            Q475=sQuery(id+"F10.wireOp",EDGE,"E2189");
            var Q476;
            Q476=sQuery(id+"F10.wireOp",EDGE,"E2125");
            var Q477;
            Q477=sQuery(id+"F10.wireOp",EDGE,"E2179");
            var Q478;
            Q478=sQuery(id+"F10.wireOp",EDGE,"E2235");
            var Q479;
            Q479=sQuery(id+"F10.wireOp",EDGE,"E2203");
            var Q480;
            Q480=sQuery(id+"F10.wireOp",EDGE,"E2585");
            var Q481;
            Q481=sQuery(id+"F10.wireOp",EDGE,"E2503");
            var Q482;
            Q482=sQuery(id+"F10.wireOp",EDGE,"E1158");
            var Q483;
            Q483=sQuery(id+"F10.wireOp",EDGE,"E2436");
            var Q484;
            Q484=sQuery(id+"F10.wireOp",EDGE,"E1206");
            var Q485;
            Q485=sQuery(id+"F10.wireOp",EDGE,"E2277");
            var Q486;
            Q486=sQuery(id+"F10.wireOp",EDGE,"E2364");
            var Q487;
            Q487=sQuery(id+"F10.wireOp",EDGE,"E2419");
            var Q488;
            Q488=sQuery(id+"F10.wireOp",EDGE,"E2387");
            var Q489;
            Q489=sQuery(id+"F10.wireOp",EDGE,"E2309");
            var Q490;
            Q490=sQuery(id+"F10.wireOp",EDGE,"E2606");
            var Q491;
            Q491=sQuery(id+"F10.wireOp",EDGE,"E2622");
            var Q492;
            Q492=sQuery(id+"F10.wireOp",EDGE,"E1144");
            var Q493;
            Q493=sQuery(id+"F10.wireOp",EDGE,"E1128");
            var Q494;
            Q494=sQuery(id+"F10.wireOp",EDGE,"E1192");
            var Q495;
            Q495=sQuery(id+"F10.wireOp",EDGE,"E2192");
            var Q496;
            Q496=sQuery(id+"F10.wireOp",EDGE,"E2475");
            var Q497;
            Q497=sQuery(id+"F10.wireOp",EDGE,"E2330");
            var Q498;
            Q498=sQuery(id+"F10.wireOp",EDGE,"E1163");
            var Q499;
            Q499=sQuery(id+"F10.wireOp",EDGE,"E2449");
            var Q500;
            Q500=sQuery(id+"F10.wireOp",EDGE,"E2142");
            var Q501;
            Q501=sQuery(id+"F10.wireOp",EDGE,"E2458");
            var Q502;
            Q502=sQuery(id+"F10.wireOp",EDGE,"E2183");
            var Q503;
            Q503=sQuery(id+"F10.wireOp",EDGE,"E2147");
            var Q504;
            Q504=sQuery(id+"F10.wireOp",EDGE,"E2108");
            var Q505;
            Q505=sQuery(id+"F10.wireOp",EDGE,"E2163");
            var Q506;
            Q506=sQuery(id+"F10.wireOp",EDGE,"E2173");
            var Q507;
            Q507=sQuery(id+"F10.wireOp",EDGE,"E2134");
            var Q508;
            Q508=sQuery(id+"F10.wireOp",EDGE,"E2110");
            var Q509;
            Q509=sQuery(id+"F10.wireOp",EDGE,"E1155");
            var Q510;
            Q510=sQuery(id+"F10.wireOp",EDGE,"E2226");
            var Q511;
            Q511=sQuery(id+"F10.wireOp",EDGE,"E1203");
            var Q512;
            Q512=sQuery(id+"F10.wireOp",EDGE,"E2597");
            var Q513;
            Q513=sQuery(id+"F10.wireOp",EDGE,"E2430");
            var Q514;
            Q514=sQuery(id+"F10.wireOp",EDGE,"E2284");
            var Q515;
            Q515=sQuery(id+"F10.wireOp",EDGE,"E2365");
            var Q516;
            Q516=sQuery(id+"F10.wireOp",EDGE,"E2422");
            var Q517;
            Q517=sQuery(id+"F10.wireOp",EDGE,"E2390");
            var Q518;
            Q518=sQuery(id+"F10.wireOp",EDGE,"E2316");
            var Q519;
            Q519=sQuery(id+"F10.wireOp",EDGE,"E2616");
            var Q520;
            Q520=sQuery(id+"F10.wireOp",EDGE,"E2599");
            var Q521;
            Q521=sQuery(id+"F10.wireOp",EDGE,"E2485");
            var Q522;
            Q522=sQuery(id+"F10.wireOp",EDGE,"E1143");
            var Q523;
            Q523=sQuery(id+"F10.wireOp",EDGE,"E1127");
            var Q524;
            Q524=sQuery(id+"F10.wireOp",EDGE,"E1191");
            var Q525;
            Q525=sQuery(id+"F10.wireOp",EDGE,"E2450");
            var Q526;
            Q526=sQuery(id+"F10.wireOp",EDGE,"E2143");
            var Q527;
            Q527=sQuery(id+"F10.wireOp",EDGE,"E2346");
            var Q528;
            Q528=sQuery(id+"F10.wireOp",EDGE,"E2459");
            var Q529;
            Q529=sQuery(id+"F10.wireOp",EDGE,"E1179");
            var Q530;
            Q530=sQuery(id+"F10.wireOp",EDGE,"E2184");
            var Q531;
            Q531=sQuery(id+"F10.wireOp",EDGE,"E2107");
            var Q532;
            Q532=sQuery(id+"F10.wireOp",EDGE,"E2151");
            var Q533;
            Q533=sQuery(id+"F10.wireOp",EDGE,"E2135");
            var Q534;
            Q534=sQuery(id+"F10.wireOp",EDGE,"E2157");
            var Q535;
            Q535=sQuery(id+"F10.wireOp",EDGE,"E2180");
            var Q536;
            Q536=sQuery(id+"F10.wireOp",EDGE,"E2109");
            var Q537;
            Q537=sQuery(id+"F10.wireOp",EDGE,"E2031");
            var Q538;
            Q538=sQuery(id+"F10.wireOp",EDGE,"E1154");
            var Q539;
            Q539=sQuery(id+"F10.wireOp",EDGE,"E1202");
            var Q540;
            Q540=sQuery(id+"F10.wireOp",EDGE,"E1123");
            var Q541;
            Q541=sQuery(id+"F10.wireOp",EDGE,"E2144");
            var Q542;
            Q542=sQuery(id+"F10.wireOp",EDGE,"E2370");
            var Q543;
            Q543=sQuery(id+"F10.wireOp",EDGE,"E2581");
            var Q544;
            Q544=sQuery(id+"F10.wireOp",EDGE,"E2439");
            var Q545;
            Q545=sQuery(id+"F10.wireOp",EDGE,"E2268");
            var Q546;
            Q546=sQuery(id+"F10.wireOp",EDGE,"E2429");
            var Q547;
            Q547=sQuery(id+"F10.wireOp",EDGE,"E2355");
            var Q548;
            Q548=sQuery(id+"F10.wireOp",EDGE,"E2381");
            var Q549;
            Q549=sQuery(id+"F10.wireOp",EDGE,"E2455");
            var Q550;
            Q550=sQuery(id+"F10.wireOp",EDGE,"E2037");
            var Q551;
            Q551=sQuery(id+"F10.wireOp",EDGE,"E2326");
            var Q552;
            Q552=sQuery(id+"F10.wireOp",EDGE,"E2607");
            var Q553;
            Q553=sQuery(id+"F10.wireOp",EDGE,"E2623");
            var Q554;
            Q554=sQuery(id+"F10.wireOp",EDGE,"E1141");
            var Q555;
            Q555=sQuery(id+"F10.wireOp",EDGE,"E1189");
            var Q556;
            Q556=sQuery(id+"F10.wireOp",EDGE,"E2476");
            var Q557;
            Q557=sQuery(id+"F10.wireOp",EDGE,"E2453");
            var Q558;
            Q558=sQuery(id+"F10.wireOp",EDGE,"E2337");
            var Q559;
            Q559=sQuery(id+"F10.wireOp",EDGE,"E2185");
            var Q560;
            Q560=sQuery(id+"F10.wireOp",EDGE,"E1178");
            var Q561;
            Q561=sQuery(id+"F10.wireOp",EDGE,"E2136");
            var Q562;
            Q562=sQuery(id+"F10.wireOp",EDGE,"E2106");
            var Q563;
            Q563=sQuery(id+"F10.wireOp",EDGE,"E2043");
            var Q564;
            Q564=sQuery(id+"F10.wireOp",EDGE,"E2148");
            var Q565;
            Q565=sQuery(id+"F10.wireOp",EDGE,"E2167");
            var Q566;
            Q566=sQuery(id+"F10.wireOp",EDGE,"E2174");
            var Q567;
            Q567=sQuery(id+"F10.wireOp",EDGE,"E2124");
            var Q568;
            Q568=sQuery(id+"F10.wireOp",EDGE,"E2060");
            var Q569;
            Q569=sQuery(id+"F10.wireOp",EDGE,"E2650");
            var Q570;
            Q570=sQuery(id+"F10.wireOp",EDGE,"E2061");
            var Q571;
            Q571=sQuery(id+"F10.wireOp",EDGE,"E2077");
            var Q572;
            Q572=sQuery(id+"F10.wireOp",EDGE,"E2634");
            var Q573;
            Q573=sQuery(id+"F10.wireOp",EDGE,"E1153");
            var Q574;
            Q574=sQuery(id+"F10.wireOp",EDGE,"E1201");
            var Q575;
            Q575=sQuery(id+"F10.wireOp",EDGE,"E1122");
            var Q576;
            Q576=sQuery(id+"F10.wireOp",EDGE,"E2145");
            var Q577;
            Q577=sQuery(id+"F10.wireOp",EDGE,"E2186");
            var Q578;
            Q578=sQuery(id+"F10.wireOp",EDGE,"E2291");
            var Q579;
            Q579=sQuery(id+"F10.wireOp",EDGE,"E2420");
            var Q580;
            Q580=sQuery(id+"F10.wireOp",EDGE,"E2391");
            var Q581;
            Q581=sQuery(id+"F10.wireOp",EDGE,"E2358");
            var Q582;
            Q582=sQuery(id+"F10.wireOp",EDGE,"E2617");
            var Q583;
            Q583=sQuery(id+"F10.wireOp",EDGE,"E1190");
            var Q584;
            Q584=sQuery(id+"F10.wireOp",EDGE,"E2323");
            var Q585;
            Q585=sQuery(id+"F10.wireOp",EDGE,"E2600");
            var Q586;
            Q586=sQuery(id+"F10.wireOp",EDGE,"E1140");
            var Q587;
            Q587=sQuery(id+"F10.wireOp",EDGE,"E2341");
            var Q588;
            Q588=sQuery(id+"F10.wireOp",EDGE,"E2470");
            var Q589;
            Q589=sQuery(id+"F10.wireOp",EDGE,"E2451");
            var Q590;
            Q590=sQuery(id+"F10.wireOp",EDGE,"E2070");
            var Q591;
            Q591=sQuery(id+"F10.wireOp",EDGE,"E1320");
            var Q592;
            Q592=sQuery(id+"F10.wireOp",EDGE,"E1177");
            var Q593;
            Q593=sQuery(id+"F10.wireOp",EDGE,"E2137");
            var Q594;
            Q594=sQuery(id+"F10.wireOp",EDGE,"E2105");
            var Q595;
            Q595=sQuery(id+"F10.wireOp",EDGE,"E2152");
            var Q596;
            Q596=sQuery(id+"F10.wireOp",EDGE,"E2175");
            var Q597;
            Q597=sQuery(id+"F10.wireOp",EDGE,"E2123");
            var Q598;
            Q598=sQuery(id+"F10.wireOp",EDGE,"E2091");
            var Q599;
            Q599=sQuery(id+"F10.wireOp",EDGE,"E2059");
            var Q600;
            Q600=sQuery(id+"F10.wireOp",EDGE,"E2164");
            var Q601;
            Q601=sQuery(id+"F10.wireOp",EDGE,"E2641");
            var Q602;
            Q602=sQuery(id+"F10.wireOp",EDGE,"E2657");
            var Q603;
            Q603=sQuery(id+"F10.wireOp",EDGE,"E1310");
            var Q604;
            Q604=sQuery(id+"F10.wireOp",EDGE,"E1294");
            var Q605;
            Q605=sQuery(id+"F10.wireOp",EDGE,"E2093");
            var Q606;
            Q606=sQuery(id+"F10.wireOp",EDGE,"E1200");
            var Q607;
            Q607=sQuery(id+"F10.wireOp",EDGE,"E1186");
            var Q608;
            Q608=sQuery(id+"F10.wireOp",EDGE,"E2139");
            var Q609;
            Q609=sQuery(id+"F10.wireOp",EDGE,"E1121");
            var Q610;
            Q610=sQuery(id+"F10.wireOp",EDGE,"E2187");
            var Q611;
            Q611=sQuery(id+"F10.wireOp",EDGE,"E2363");
            var Q612;
            Q612=sQuery(id+"F10.wireOp",EDGE,"E2423");
            var Q613;
            Q613=sQuery(id+"F10.wireOp",EDGE,"E2278");
            var Q614;
            Q614=sQuery(id+"F10.wireOp",EDGE,"E2608");
            var Q615;
            Q615=sQuery(id+"F10.wireOp",EDGE,"E2624");
            var Q616;
            Q616=sQuery(id+"F10.wireOp",EDGE,"E2388");
            var Q617;
            Q617=sQuery(id+"F10.wireOp",EDGE,"E1142");
            var Q618;
            Q618=sQuery(id+"F10.wireOp",EDGE,"E2310");
            var Q619;
            Q619=sQuery(id+"F10.wireOp",EDGE,"E2332");
            var Q620;
            Q620=sQuery(id+"F10.wireOp",EDGE,"E2483");
            var Q621;
            Q621=sQuery(id+"F10.wireOp",EDGE,"E2454");
            var Q622;
            Q622=sQuery(id+"F10.wireOp",EDGE,"E2132");
            var Q623;
            Q623=sQuery(id+"F10.wireOp",EDGE,"E2068");
            var Q624;
            Q624=sQuery(id+"F10.wireOp",EDGE,"E1319");
            var Q625;
            Q625=sQuery(id+"F10.wireOp",EDGE,"E1176");
            var Q626;
            Q626=sQuery(id+"F10.wireOp",EDGE,"E2153");
            var Q627;
            Q627=sQuery(id+"F10.wireOp",EDGE,"E2176");
            var Q628;
            Q628=sQuery(id+"F10.wireOp",EDGE,"E2104");
            var Q629;
            Q629=sQuery(id+"F10.wireOp",EDGE,"E2057");
            var Q630;
            Q630=sQuery(id+"F10.wireOp",EDGE,"E1338");
            var Q631;
            Q631=sQuery(id+"F10.wireOp",EDGE,"E2122");
            var Q632;
            Q632=sQuery(id+"F10.wireOp",EDGE,"E2158");
            var Q633;
            Q633=sQuery(id+"F10.wireOp",EDGE,"E2651");
            var Q634;
            Q634=sQuery(id+"F10.wireOp",EDGE,"E2635");
            var Q635;
            Q635=sQuery(id+"F10.wireOp",EDGE,"E1309");
            var Q636;
            Q636=sQuery(id+"F10.wireOp",EDGE,"E1293");
            var Q637;
            Q637=sQuery(id+"F10.wireOp",EDGE,"E2076");
            var Q638;
            Q638=sQuery(id+"F10.wireOp",EDGE,"E1326");
            var Q639;
            Q639=sQuery(id+"F10.wireOp",EDGE,"E2747");
            var Q640;
            Q640=sQuery(id+"F10.wireOp",EDGE,"E1199");
            var Q641;
            Q641=sQuery(id+"F10.wireOp",EDGE,"E1152");
            var Q642;
            Q642=sQuery(id+"F10.wireOp",EDGE,"E1185");
            var Q643;
            Q643=sQuery(id+"F10.wireOp",EDGE,"E2146");
            var Q644;
            Q644=sQuery(id+"F10.wireOp",EDGE,"E1120");
            var Q645;
            Q645=sQuery(id+"F10.wireOp",EDGE,"E2154");
            var Q646;
            Q646=sQuery(id+"F10.wireOp",EDGE,"E2354");
            var Q647;
            Q647=sQuery(id+"F10.wireOp",EDGE,"E2418");
            var Q648;
            Q648=sQuery(id+"F10.wireOp",EDGE,"E2386");
            var Q649;
            Q649=sQuery(id+"F10.wireOp",EDGE,"E2620");
            var Q650;
            Q650=sQuery(id+"F10.wireOp",EDGE,"E2275");
            var Q651;
            Q651=sQuery(id+"F10.wireOp",EDGE,"E2601");
            var Q652;
            Q652=sQuery(id+"F10.wireOp",EDGE,"E2181");
            var Q653;
            Q653=sQuery(id+"F10.wireOp",EDGE,"E2307");
            var Q654;
            Q654=sQuery(id+"F10.wireOp",EDGE,"E2348");
            var Q655;
            Q655=sQuery(id+"F10.wireOp",EDGE,"E2445");
            var Q656;
            Q656=sQuery(id+"F10.wireOp",EDGE,"E2131");
            var Q657;
            Q657=sQuery(id+"F10.wireOp",EDGE,"E2067");
            var Q658;
            Q658=sQuery(id+"F10.wireOp",EDGE,"E2486");
            var Q659;
            Q659=sQuery(id+"F10.wireOp",EDGE,"E1317");
            var Q660;
            Q660=sQuery(id+"F10.wireOp",EDGE,"E2744");
            var Q661;
            Q661=sQuery(id+"F10.wireOp",EDGE,"E1175");
            var Q662;
            Q662=sQuery(id+"F10.wireOp",EDGE,"E2103");
            var Q663;
            Q663=sQuery(id+"F10.wireOp",EDGE,"E2121");
            var Q664;
            Q664=sQuery(id+"F10.wireOp",EDGE,"E2168");
            var Q665;
            Q665=sQuery(id+"F10.wireOp",EDGE,"E1291");
            var Q666;
            Q666=sQuery(id+"F10.wireOp",EDGE,"E1308");
            var Q667;
            Q667=sQuery(id+"F10.wireOp",EDGE,"E1324");
            var Q668;
            Q668=sQuery(id+"F10.wireOp",EDGE,"E2642");
            var Q669;
            Q669=sQuery(id+"F10.wireOp",EDGE,"E2658");
            var Q670;
            Q670=sQuery(id+"F10.wireOp",EDGE,"E1325");
            var Q671;
            Q671=sQuery(id+"F10.wireOp",EDGE,"E2092");
            var Q672;
            Q672=sQuery(id+"F10.wireOp",EDGE,"E1151");
            var Q673;
            Q673=sQuery(id+"F10.wireOp",EDGE,"E1392");
            var Q674;
            Q674=sQuery(id+"F10.wireOp",EDGE,"E1298");
            var Q675;
            Q675=sQuery(id+"F10.wireOp",EDGE,"E2155");
            var Q676;
            Q676=sQuery(id+"F10.wireOp",EDGE,"E1119");
            var Q677;
            Q677=sQuery(id+"F10.wireOp",EDGE,"E2289");
            var Q678;
            Q678=sQuery(id+"F10.wireOp",EDGE,"E2613");
            var Q679;
            Q679=sQuery(id+"F10.wireOp",EDGE,"E2446");
            var Q680;
            Q680=sQuery(id+"F10.wireOp",EDGE,"E2172");
            var Q681;
            Q681=sQuery(id+"F10.wireOp",EDGE,"E2317");
            var Q682;
            Q682=sQuery(id+"F10.wireOp",EDGE,"E2069");
            var Q683;
            Q683=sQuery(id+"F10.wireOp",EDGE,"E2342");
            var Q684;
            Q684=sQuery(id+"F10.wireOp",EDGE,"E2133");
            var Q685;
            Q685=sQuery(id+"F10.wireOp",EDGE,"E2477");
            var Q686;
            Q686=sQuery(id+"F10.wireOp",EDGE,"E1316");
            var Q687;
            Q687=sQuery(id+"F10.wireOp",EDGE,"E1173");
            var Q688;
            Q688=sQuery(id+"F10.wireOp",EDGE,"E2745");
            var Q689;
            Q689=sQuery(id+"F10.wireOp",EDGE,"E2102");
            var Q690;
            Q690=sQuery(id+"F10.wireOp",EDGE,"E1447");
            var Q691;
            Q691=sQuery(id+"F10.wireOp",EDGE,"E2743");
            var Q692;
            Q692=sQuery(id+"F10.wireOp",EDGE,"E2120");
            var Q693;
            Q693=sQuery(id+"F10.wireOp",EDGE,"E2159");
            var Q694;
            Q694=sQuery(id+"F10.wireOp",EDGE,"E1434");
            var Q695;
            Q695=sQuery(id+"F10.wireOp",EDGE,"E1530");
            var Q696;
            Q696=sQuery(id+"F10.wireOp",EDGE,"E1307");
            var Q697;
            Q697=sQuery(id+"F10.wireOp",EDGE,"E1339");
            var Q698;
            Q698=sQuery(id+"F10.wireOp",EDGE,"E1323");
            var Q699;
            Q699=sQuery(id+"F10.wireOp",EDGE,"E2058");
            var Q700;
            Q700=sQuery(id+"F10.wireOp",EDGE,"E2075");
            var Q701;
            Q701=sQuery(id+"F10.wireOp",EDGE,"E1342");
            var Q702;
            Q702=sQuery(id+"F10.wireOp",EDGE,"E1390");
            var Q703;
            Q703=sQuery(id+"F10.wireOp",EDGE,"E1374");
            var Q704;
            Q704=sQuery(id+"F10.wireOp",EDGE,"E1358");
            var Q705;
            Q705=sQuery(id+"F10.wireOp",EDGE,"E1470");
            var Q706;
            Q706=sQuery(id+"F10.wireOp",EDGE,"E1454");
            var Q707;
            Q707=sQuery(id+"F10.wireOp",EDGE,"E1438");
            var Q708;
            Q708=sQuery(id+"F10.wireOp",EDGE,"E1502");
            var Q709;
            Q709=sQuery(id+"F10.wireOp",EDGE,"E1486");
            var Q710;
            Q710=sQuery(id+"F10.wireOp",EDGE,"E1297");
            var Q711;
            Q711=sQuery(id+"F10.wireOp",EDGE,"E2066");
            var Q712;
            Q712=sQuery(id+"F10.wireOp",EDGE,"E1118");
            var Q713;
            Q713=sQuery(id+"F10.wireOp",EDGE,"E2178");
            var Q714;
            Q714=sQuery(id+"F10.wireOp",EDGE,"E2138");
            var Q715;
            Q715=sQuery(id+"F10.wireOp",EDGE,"E2273");
            var Q716;
            Q716=sQuery(id+"F10.wireOp",EDGE,"E2315");
            var Q717;
            Q717=sQuery(id+"F10.wireOp",EDGE,"E2604");
            var Q718;
            Q718=sQuery(id+"F10.wireOp",EDGE,"E2339");
            var Q719;
            Q719=sQuery(id+"F10.wireOp",EDGE,"E2746");
            var Q720;
            Q720=sQuery(id+"F10.wireOp",EDGE,"E1318");
            var Q721;
            Q721=sQuery(id+"F10.wireOp",EDGE,"E2471");
            var Q722;
            Q722=sQuery(id+"F10.wireOp",EDGE,"E1172");
            var Q723;
            Q723=sQuery(id+"F10.wireOp",EDGE,"E2100");
            var Q724;
            Q724=sQuery(id+"F10.wireOp",EDGE,"E2119");
            var Q725;
            Q725=sQuery(id+"F10.wireOp",EDGE,"E2740");
            var Q726;
            Q726=sQuery(id+"F10.wireOp",EDGE,"E2169");
            var Q727;
            Q727=sQuery(id+"F10.wireOp",EDGE,"E2056");
            var Q728;
            Q728=sQuery(id+"F10.wireOp",EDGE,"E1337");
            var Q729;
            Q729=sQuery(id+"F10.wireOp",EDGE,"E1433");
            var Q730;
            Q730=sQuery(id+"F10.wireOp",EDGE,"E1529");
            var Q731;
            Q731=sQuery(id+"F10.wireOp",EDGE,"E1306");
            var Q732;
            Q732=sQuery(id+"F10.wireOp",EDGE,"E1322");
            var Q733;
            Q733=sQuery(id+"F10.wireOp",EDGE,"E2074");
            var Q734;
            Q734=sQuery(id+"F10.wireOp",EDGE,"E1341");
            var Q735;
            Q735=sQuery(id+"F10.wireOp",EDGE,"E1373");
            var Q736;
            Q736=sQuery(id+"F10.wireOp",EDGE,"E1357");
            var Q737;
            Q737=sQuery(id+"F10.wireOp",EDGE,"E1469");
            var Q738;
            Q738=sQuery(id+"F10.wireOp",EDGE,"E1453");
            var Q739;
            Q739=sQuery(id+"F10.wireOp",EDGE,"E1437");
            var Q740;
            Q740=sQuery(id+"F10.wireOp",EDGE,"E1406");
            var Q741;
            Q741=sQuery(id+"F10.wireOp",EDGE,"E1422");
            var Q742;
            Q742=sQuery(id+"F10.wireOp",EDGE,"E1518");
            var Q743;
            Q743=sQuery(id+"F10.wireOp",EDGE,"E1296");
            var Q744;
            Q744=sQuery(id+"F10.wireOp",EDGE,"E2065");
            var Q745;
            Q745=sQuery(id+"F10.wireOp",EDGE,"E2130");
            var Q746;
            Q746=sQuery(id+"F10.wireOp",EDGE,"E1315");
            var Q747;
            Q747=sQuery(id+"F10.wireOp",EDGE,"E1117");
            var Q748;
            Q748=sQuery(id+"F10.wireOp",EDGE,"E2267");
            var Q749;
            Q749=sQuery(id+"F10.wireOp",EDGE,"E2322");
            var Q750;
            Q750=sQuery(id+"F10.wireOp",EDGE,"E2748");
            var Q751;
            Q751=sQuery(id+"F10.wireOp",EDGE,"E2165");
            var Q752;
            Q752=sQuery(id+"F10.wireOp",EDGE,"E2349");
            var Q753;
            Q753=sQuery(id+"F10.wireOp",EDGE,"E2484");
            var Q754;
            Q754=sQuery(id+"F10.wireOp",EDGE,"E1174");
            var Q755;
            Q755=sQuery(id+"F10.wireOp",EDGE,"E2099");
            var Q756;
            Q756=sQuery(id+"F10.wireOp",EDGE,"E1380");
            var Q757;
            Q757=sQuery(id+"F10.wireOp",EDGE,"E2118");
            var Q758;
            Q758=sQuery(id+"F10.wireOp",EDGE,"E2646");
            var Q759;
            Q759=sQuery(id+"F10.wireOp",EDGE,"E2055");
            var Q760;
            Q760=sQuery(id+"F10.wireOp",EDGE,"E1432");
            var Q761;
            Q761=sQuery(id+"F10.wireOp",EDGE,"E1528");
            var Q762;
            Q762=sQuery(id+"F10.wireOp",EDGE,"E1305");
            var Q763;
            Q763=sQuery(id+"F10.wireOp",EDGE,"E1321");
            var Q764;
            Q764=sQuery(id+"F10.wireOp",EDGE,"E1386");
            var Q765;
            Q765=sQuery(id+"F10.wireOp",EDGE,"E2090");
            var Q766;
            Q766=sQuery(id+"F10.wireOp",EDGE,"E1356");
            var Q767;
            Q767=sQuery(id+"F10.wireOp",EDGE,"E1340");
            var Q768;
            Q768=sQuery(id+"F10.wireOp",EDGE,"E1436");
            var Q769;
            Q769=sQuery(id+"F10.wireOp",EDGE,"E1452");
            var Q770;
            Q770=sQuery(id+"F10.wireOp",EDGE,"E1389");
            var Q771;
            Q771=sQuery(id+"F10.wireOp",EDGE,"E1501");
            var Q772;
            Q772=sQuery(id+"F10.wireOp",EDGE,"E1485");
            var Q773;
            Q773=sQuery(id+"F10.wireOp",EDGE,"E1295");
            var Q774;
            Q774=sQuery(id+"F10.wireOp",EDGE,"E2064");
            var Q775;
            Q775=sQuery(id+"F10.wireOp",EDGE,"E2129");
            var Q776;
            Q776=sQuery(id+"F10.wireOp",EDGE,"E1314");
            var Q777;
            Q777=sQuery(id+"F10.wireOp",EDGE,"E1171");
            var Q778;
            Q778=sQuery(id+"F10.wireOp",EDGE,"E1116");
            var Q779;
            Q779=sQuery(id+"F10.wireOp",EDGE,"E2283");
            var Q780;
            Q780=sQuery(id+"F10.wireOp",EDGE,"E2306");
            var Q781;
            Q781=sQuery(id+"F10.wireOp",EDGE,"E2160");
            var Q782;
            Q782=sQuery(id+"F10.wireOp",EDGE,"E2749");
            var Q783;
            Q783=sQuery(id+"F10.wireOp",EDGE,"E2333");
            var Q784;
            Q784=sQuery(id+"F10.wireOp",EDGE,"E2487");
            var Q785;
            Q785=sQuery(id+"F10.wireOp",EDGE,"E2101");
            var Q786;
            Q786=sQuery(id+"F10.wireOp",EDGE,"E1349");
            var Q787;
            Q787=sQuery(id+"F10.wireOp",EDGE,"E2116");
            var Q788;
            Q788=sQuery(id+"F10.wireOp",EDGE,"E2643");
            var Q789;
            Q789=sQuery(id+"F10.wireOp",EDGE,"E1431");
            var Q790;
            Q790=sQuery(id+"F10.wireOp",EDGE,"E1527");
            var Q791;
            Q791=sQuery(id+"F10.wireOp",EDGE,"E2662");
            var Q792;
            Q792=sQuery(id+"F10.wireOp",EDGE,"E1304");
            var Q793;
            Q793=sQuery(id+"F10.wireOp",EDGE,"E1336");
            var Q794;
            Q794=sQuery(id+"F10.wireOp",EDGE,"E1385");
            var Q795;
            Q795=sQuery(id+"F10.wireOp",EDGE,"E2073");
            var Q796;
            Q796=sQuery(id+"F10.wireOp",EDGE,"E1435");
            var Q797;
            Q797=sQuery(id+"F10.wireOp",EDGE,"E1372");
            var Q798;
            Q798=sQuery(id+"F10.wireOp",EDGE,"E1468");
            var Q799;
            Q799=sQuery(id+"F10.wireOp",EDGE,"E1405");
            var Q800;
            Q800=sQuery(id+"F10.wireOp",EDGE,"E1421");
            var Q801;
            Q801=sQuery(id+"F10.wireOp",EDGE,"E1517");
            var Q802;
            Q802=sQuery(id+"F10.wireOp",EDGE,"E2063");
            var Q803;
            Q803=sQuery(id+"F10.wireOp",EDGE,"E2128");
            var Q804;
            Q804=sQuery(id+"F10.wireOp",EDGE,"E1313");
            var Q805;
            Q805=sQuery(id+"F10.wireOp",EDGE,"E1170");
            var Q806;
            Q806=sQuery(id+"F10.wireOp",EDGE,"E2098");
            var Q807;
            Q807=sQuery(id+"F10.wireOp",EDGE,"E1443");
            var Q808;
            Q808=sQuery(id+"F10.wireOp",EDGE,"E1115");
            var Q809;
            Q809=sQuery(id+"F10.wireOp",EDGE,"E2290");
            var Q810;
            Q810=sQuery(id+"F10.wireOp",EDGE,"E2170");
            var Q811;
            Q811=sQuery(id+"F10.wireOp",EDGE,"E2331");
            var Q812;
            Q812=sQuery(id+"F10.wireOp",EDGE,"E2478");
            var Q813;
            Q813=sQuery(id+"F10.wireOp",EDGE,"E1348");
            var Q814;
            Q814=sQuery(id+"F10.wireOp",EDGE,"E2115");
            var Q815;
            Q815=sQuery(id+"F10.wireOp",EDGE,"E1556");
            var Q816;
            Q816=sQuery(id+"F10.wireOp",EDGE,"E1429");
            var Q817;
            Q817=sQuery(id+"F10.wireOp",EDGE,"E1525");
            var Q818;
            Q818=sQuery(id+"F10.wireOp",EDGE,"E1637");
            var Q819;
            Q819=sQuery(id+"F10.wireOp",EDGE,"E2750");
            var Q820;
            Q820=sQuery(id+"F10.wireOp",EDGE,"E1303");
            var Q821;
            Q821=sQuery(id+"F10.wireOp",EDGE,"E1335");
            var Q822;
            Q822=sQuery(id+"F10.wireOp",EDGE,"E2659");
            var Q823;
            Q823=sQuery(id+"F10.wireOp",EDGE,"E1384");
            var Q824;
            Q824=sQuery(id+"F10.wireOp",EDGE,"E2089");
            var Q825;
            Q825=sQuery(id+"F10.wireOp",EDGE,"E1546");
            var Q826;
            Q826=sQuery(id+"F10.wireOp",EDGE,"E1355");
            var Q827;
            Q827=sQuery(id+"F10.wireOp",EDGE,"E1467");
            var Q828;
            Q828=sQuery(id+"F10.wireOp",EDGE,"E1451");
            var Q829;
            Q829=sQuery(id+"F10.wireOp",EDGE,"E1388");
            var Q830;
            Q830=sQuery(id+"F10.wireOp",EDGE,"E1484");
            var Q831;
            Q831=sQuery(id+"F10.wireOp",EDGE,"E1516");
            var Q832;
            Q832=sQuery(id+"F10.wireOp",EDGE,"E2738");
            var Q833;
            Q833=sQuery(id+"F10.wireOp",EDGE,"E1550");
            var Q834;
            Q834=sQuery(id+"F10.wireOp",EDGE,"E1534");
            var Q835;
            Q835=sQuery(id+"F10.wireOp",EDGE,"E1614");
            var Q836;
            Q836=sQuery(id+"F10.wireOp",EDGE,"E1598");
            var Q837;
            Q837=sQuery(id+"F10.wireOp",EDGE,"E1582");
            var Q838;
            Q838=sQuery(id+"F10.wireOp",EDGE,"E1646");
            var Q839;
            Q839=sQuery(id+"F10.wireOp",EDGE,"E2062");
            var Q840;
            Q840=sQuery(id+"F10.wireOp",EDGE,"E2127");
            var Q841;
            Q841=sQuery(id+"F10.wireOp",EDGE,"E1169");
            var Q842;
            Q842=sQuery(id+"F10.wireOp",EDGE,"E1442");
            var Q843;
            Q843=sQuery(id+"F10.wireOp",EDGE,"E1114");
            var Q844;
            Q844=sQuery(id+"F10.wireOp",EDGE,"E2274");
            var Q845;
            Q845=sQuery(id+"F10.wireOp",EDGE,"E2161");
            var Q846;
            Q846=sQuery(id+"F10.wireOp",EDGE,"E2347");
            var Q847;
            Q847=sQuery(id+"F10.wireOp",EDGE,"E1350");
            var Q848;
            Q848=sQuery(id+"F10.wireOp",EDGE,"E2117");
            var Q849;
            Q849=sQuery(id+"F10.wireOp",EDGE,"E1428");
            var Q850;
            Q850=sQuery(id+"F10.wireOp",EDGE,"E1524");
            var Q851;
            Q851=sQuery(id+"F10.wireOp",EDGE,"E1636");
            var Q852;
            Q852=sQuery(id+"F10.wireOp",EDGE,"E1301");
            var Q853;
            Q853=sQuery(id+"F10.wireOp",EDGE,"E1333");
            var Q854;
            Q854=sQuery(id+"F10.wireOp",EDGE,"E2735");
            var Q855;
            Q855=sQuery(id+"F10.wireOp",EDGE,"E2637");
            var Q856;
            Q856=sQuery(id+"F10.wireOp",EDGE,"E2054");
            var Q857;
            Q857=sQuery(id+"F10.wireOp",EDGE,"E1383");
            var Q858;
            Q858=sQuery(id+"F10.wireOp",EDGE,"E2072");
            var Q859;
            Q859=sQuery(id+"F10.wireOp",EDGE,"E1545");
            var Q860;
            Q860=sQuery(id+"F10.wireOp",EDGE,"E1466");
            var Q861;
            Q861=sQuery(id+"F10.wireOp",EDGE,"E1450");
            var Q862;
            Q862=sQuery(id+"F10.wireOp",EDGE,"E1371");
            var Q863;
            Q863=sQuery(id+"F10.wireOp",EDGE,"E1420");
            var Q864;
            Q864=sQuery(id+"F10.wireOp",EDGE,"E1404");
            var Q865;
            Q865=sQuery(id+"F10.wireOp",EDGE,"E1500");
            var Q866;
            Q866=sQuery(id+"F10.wireOp",EDGE,"E1549");
            var Q867;
            Q867=sQuery(id+"F10.wireOp",EDGE,"E1533");
            var Q868;
            Q868=sQuery(id+"F10.wireOp",EDGE,"E1581");
            var Q869;
            Q869=sQuery(id+"F10.wireOp",EDGE,"E1645");
            var Q870;
            Q870=sQuery(id+"F10.wireOp",EDGE,"E1566");
            var Q871;
            Q871=sQuery(id+"F10.wireOp",EDGE,"E1630");
            var Q872;
            Q872=sQuery(id+"F10.wireOp",EDGE,"E1168");
            var Q873;
            Q873=sQuery(id+"F10.wireOp",EDGE,"E1441");
            var Q874;
            Q874=sQuery(id+"F10.wireOp",EDGE,"E2114");
            var Q875;
            Q875=sQuery(id+"F10.wireOp",EDGE,"E1347");
            var Q876;
            Q876=sQuery(id+"F10.wireOp",EDGE,"E1113");
            var Q877;
            Q877=sQuery(id+"F10.wireOp",EDGE,"E2162");
            var Q878;
            Q878=sQuery(id+"F10.wireOp",EDGE,"E2338");
            var Q879;
            Q879=sQuery(id+"F10.wireOp",EDGE,"E1302");
            var Q880;
            Q880=sQuery(id+"F10.wireOp",EDGE,"E1430");
            var Q881;
            Q881=sQuery(id+"F10.wireOp",EDGE,"E1526");
            var Q882;
            Q882=sQuery(id+"F10.wireOp",EDGE,"E1638");
            var Q883;
            Q883=sQuery(id+"F10.wireOp",EDGE,"E2736");
            var Q884;
            Q884=sQuery(id+"F10.wireOp",EDGE,"E1332");
            var Q885;
            Q885=sQuery(id+"F10.wireOp",EDGE,"E1381");
            var Q886;
            Q886=sQuery(id+"F10.wireOp",EDGE,"E2647");
            var Q887;
            Q887=sQuery(id+"F10.wireOp",EDGE,"E2653");
            var Q888;
            Q888=sQuery(id+"F10.wireOp",EDGE,"E2088");
            var Q889;
            Q889=sQuery(id+"F10.wireOp",EDGE,"E1465");
            var Q890;
            Q890=sQuery(id+"F10.wireOp",EDGE,"E1449");
            var Q891;
            Q891=sQuery(id+"F10.wireOp",EDGE,"E1354");
            var Q892;
            Q892=sQuery(id+"F10.wireOp",EDGE,"E1387");
            var Q893;
            Q893=sQuery(id+"F10.wireOp",EDGE,"E1483");
            var Q894;
            Q894=sQuery(id+"F10.wireOp",EDGE,"E1515");
            var Q895;
            Q895=sQuery(id+"F10.wireOp",EDGE,"E1532");
            var Q896;
            Q896=sQuery(id+"F10.wireOp",EDGE,"E1580");
            var Q897;
            Q897=sQuery(id+"F10.wireOp",EDGE,"E1548");
            var Q898;
            Q898=sQuery(id+"F10.wireOp",EDGE,"E1644");
            var Q899;
            Q899=sQuery(id+"F10.wireOp",EDGE,"E1613");
            var Q900;
            Q900=sQuery(id+"F10.wireOp",EDGE,"E1597");
            var Q901;
            Q901=sQuery(id+"F10.wireOp",EDGE,"E1440");
            var Q902;
            Q902=sQuery(id+"F10.wireOp",EDGE,"E1184");
            var Q903;
            Q903=sQuery(id+"F10.wireOp",EDGE,"E2113");
            var Q904;
            Q904=sQuery(id+"F10.wireOp",EDGE,"E1346");
            var Q905;
            Q905=sQuery(id+"F10.wireOp",EDGE,"E1635");
            var Q906;
            Q906=sQuery(id+"F10.wireOp",EDGE,"E2171");
            var Q907;
            Q907=sQuery(id+"F10.wireOp",EDGE,"E1299");
            var Q908;
            Q908=sQuery(id+"F10.wireOp",EDGE,"E1427");
            var Q909;
            Q909=sQuery(id+"F10.wireOp",EDGE,"E1523");
            var Q910;
            Q910=sQuery(id+"F10.wireOp",EDGE,"E1112");
            var Q911;
            Q911=sQuery(id+"F10.wireOp",EDGE,"E2737");
            var Q912;
            Q912=sQuery(id+"F10.wireOp",EDGE,"E1334");
            var Q913;
            Q913=sQuery(id+"F10.wireOp",EDGE,"E1382");
            var Q914;
            Q914=sQuery(id+"F10.wireOp",EDGE,"E2644");
            var Q915;
            Q915=sQuery(id+"F10.wireOp",EDGE,"E2663");
            var Q916;
            Q916=sQuery(id+"F10.wireOp",EDGE,"E2071");
            var Q917;
            Q917=sQuery(id+"F10.wireOp",EDGE,"E1464");
            var Q918;
            Q918=sQuery(id+"F10.wireOp",EDGE,"E1448");
            var Q919;
            Q919=sQuery(id+"F10.wireOp",EDGE,"E1370");
            var Q920;
            Q920=sQuery(id+"F10.wireOp",EDGE,"E1419");
            var Q921;
            Q921=sQuery(id+"F10.wireOp",EDGE,"E1403");
            var Q922;
            Q922=sQuery(id+"F10.wireOp",EDGE,"E1499");
            var Q923;
            Q923=sQuery(id+"F10.wireOp",EDGE,"E1531");
            var Q924;
            Q924=sQuery(id+"F10.wireOp",EDGE,"E1579");
            var Q925;
            Q925=sQuery(id+"F10.wireOp",EDGE,"E1547");
            var Q926;
            Q926=sQuery(id+"F10.wireOp",EDGE,"E1643");
            var Q927;
            Q927=sQuery(id+"F10.wireOp",EDGE,"E1565");
            var Q928;
            Q928=sQuery(id+"F10.wireOp",EDGE,"E1629");
            var Q929;
            Q929=sQuery(id+"F10.wireOp",EDGE,"E1439");
            var Q930;
            Q930=sQuery(id+"F10.wireOp",EDGE,"E1167");
            var Q931;
            Q931=sQuery(id+"F10.wireOp",EDGE,"E1312");
            var Q932;
            Q932=sQuery(id+"F10.wireOp",EDGE,"E2112");
            var Q933;
            Q933=sQuery(id+"F10.wireOp",EDGE,"E1345");
            var Q934;
            Q934=sQuery(id+"F10.wireOp",EDGE,"E1634");
            var Q935;
            Q935=sQuery(id+"F10.wireOp",EDGE,"E1426");
            var Q936;
            Q936=sQuery(id+"F10.wireOp",EDGE,"E1522");
            var Q937;
            Q937=sQuery(id+"F10.wireOp",EDGE,"E1331");
            var Q938;
            Q938=sQuery(id+"F10.wireOp",EDGE,"E1379");
            var Q939;
            Q939=sQuery(id+"F10.wireOp",EDGE,"E1111");
            var Q940;
            Q940=sQuery(id+"F10.wireOp",EDGE,"E2739");
            var Q941;
            Q941=sQuery(id+"F10.wireOp",EDGE,"E1445");
            var Q942;
            Q942=sQuery(id+"F10.wireOp",EDGE,"E1541");
            var Q943;
            Q943=sQuery(id+"F10.wireOp",EDGE,"E2751");
            var Q944;
            Q944=sQuery(id+"F10.wireOp",EDGE,"E2660");
            var Q945;
            Q945=sQuery(id+"F10.wireOp",EDGE,"E1463");
            var Q946;
            Q946=sQuery(id+"F10.wireOp",EDGE,"E2087");
            var Q947;
            Q947=sQuery(id+"F10.wireOp",EDGE,"E1544");
            var Q948;
            Q948=sQuery(id+"F10.wireOp",EDGE,"E1353");
            var Q949;
            Q949=sQuery(id+"F10.wireOp",EDGE,"E1402");
            var Q950;
            Q950=sQuery(id+"F10.wireOp",EDGE,"E1482");
            var Q951;
            Q951=sQuery(id+"F10.wireOp",EDGE,"E1514");
            var Q952;
            Q952=sQuery(id+"F10.wireOp",EDGE,"E1578");
            var Q953;
            Q953=sQuery(id+"F10.wireOp",EDGE,"E1642");
            var Q954;
            Q954=sQuery(id+"F10.wireOp",EDGE,"E1564");
            var Q955;
            Q955=sQuery(id+"F10.wireOp",EDGE,"E1612");
            var Q956;
            Q956=sQuery(id+"F10.wireOp",EDGE,"E1311");
            var Q957;
            Q957=sQuery(id+"F10.wireOp",EDGE,"E2111");
            var Q958;
            Q958=sQuery(id+"F10.wireOp",EDGE,"E1344");
            var Q959;
            Q959=sQuery(id+"F10.wireOp",EDGE,"E1521");
            var Q960;
            Q960=sQuery(id+"F10.wireOp",EDGE,"E1633");
            var Q961;
            Q961=sQuery(id+"F10.wireOp",EDGE,"E1425");
            var Q962;
            Q962=sQuery(id+"F10.wireOp",EDGE,"E1330");
            var Q963;
            Q963=sQuery(id+"F10.wireOp",EDGE,"E1378");
            var Q964;
            Q964=sQuery(id+"F10.wireOp",EDGE,"E1125");
            var Q965;
            Q965=sQuery(id+"F10.wireOp",EDGE,"E1444");
            var Q966;
            Q966=sQuery(id+"F10.wireOp",EDGE,"E1540");
            var Q967;
            Q967=sQuery(id+"F10.wireOp",EDGE,"E1461");
            var Q968;
            Q968=sQuery(id+"F10.wireOp",EDGE,"E2638");
            var Q969;
            Q969=sQuery(id+"F10.wireOp",EDGE,"E2654");
            var Q970;
            Q970=sQuery(id+"F10.wireOp",EDGE,"E2086");
            var Q971;
            Q971=sQuery(id+"F10.wireOp",EDGE,"E1543");
            var Q972;
            Q972=sQuery(id+"F10.wireOp",EDGE,"E1369");
            var Q973;
            Q973=sQuery(id+"F10.wireOp",EDGE,"E1577");
            var Q974;
            Q974=sQuery(id+"F10.wireOp",EDGE,"E1641");
            var Q975;
            Q975=sQuery(id+"F10.wireOp",EDGE,"E1418");
            var Q976;
            Q976=sQuery(id+"F10.wireOp",EDGE,"E1498");
            var Q977;
            Q977=sQuery(id+"F10.wireOp",EDGE,"E1596");
            var Q978;
            Q978=sQuery(id+"F10.wireOp",EDGE,"E1628");
            var Q979;
            Q979=sQuery(id+"F10.wireOp",EDGE,"E1343");
            var Q980;
            Q980=sQuery(id+"F10.wireOp",EDGE,"E1520");
            var Q981;
            Q981=sQuery(id+"F10.wireOp",EDGE,"E1632");
            var Q982;
            Q982=sQuery(id+"F10.wireOp",EDGE,"E1329");
            var Q983;
            Q983=sQuery(id+"F10.wireOp",EDGE,"E1377");
            var Q984;
            Q984=sQuery(id+"F10.wireOp",EDGE,"E1124");
            var Q985;
            Q985=sQuery(id+"F10.wireOp",EDGE,"E1446");
            var Q986;
            Q986=sQuery(id+"F10.wireOp",EDGE,"E1542");
            var Q987;
            Q987=sQuery(id+"F10.wireOp",EDGE,"E1460");
            var Q988;
            Q988=sQuery(id+"F10.wireOp",EDGE,"E2632");
            var Q989;
            Q989=sQuery(id+"F10.wireOp",EDGE,"E2084");
            var Q990;
            Q990=sQuery(id+"F10.wireOp",EDGE,"E2052");
            var Q991;
            Q991=sQuery(id+"F10.wireOp",EDGE,"E1352");
            var Q992;
            Q992=sQuery(id+"F10.wireOp",EDGE,"E1576");
            var Q993;
            Q993=sQuery(id+"F10.wireOp",EDGE,"E1640");
            var Q994;
            Q994=sQuery(id+"F10.wireOp",EDGE,"E1401");
            var Q995;
            Q995=sQuery(id+"F10.wireOp",EDGE,"E1481");
            var Q996;
            Q996=sQuery(id+"F10.wireOp",EDGE,"E1513");
            var Q997;
            Q997=sQuery(id+"F10.wireOp",EDGE,"E1563");
            var Q998;
            Q998=sQuery(id+"F10.wireOp",EDGE,"E1611");
            var Q999;
            Q999=sQuery(id+"F10.wireOp",EDGE,"E1519");
            var Q1000;
            Q1000=sQuery(id+"F10.wireOp",EDGE,"E1551");
            var Q1001;
            Q1001=sQuery(id+"F10.wireOp",EDGE,"E1472");
            var Q1002;
            Q1002=sQuery(id+"F10.wireOp",EDGE,"E1328");
            var Q1003;
            Q1003=sQuery(id+"F10.wireOp",EDGE,"E1376");
            var Q1004;
            Q1004=sQuery(id+"F10.wireOp",EDGE,"E1539");
            var Q1005;
            Q1005=sQuery(id+"F10.wireOp",EDGE,"E1126");
            var Q1006;
            Q1006=sQuery(id+"F10.wireOp",EDGE,"E1462");
            var Q1007;
            Q1007=sQuery(id+"F10.wireOp",EDGE,"E2083");
            var Q1008;
            Q1008=sQuery(id+"F10.wireOp",EDGE,"E2648");
            var Q1009;
            Q1009=sQuery(id+"F10.wireOp",EDGE,"E2664");
            var Q1010;
            Q1010=sQuery(id+"F10.wireOp",EDGE,"E1575");
            var Q1011;
            Q1011=sQuery(id+"F10.wireOp",EDGE,"E1639");
            var Q1012;
            Q1012=sQuery(id+"F10.wireOp",EDGE,"E1368");
            var Q1013;
            Q1013=sQuery(id+"F10.wireOp",EDGE,"E1480");
            var Q1014;
            Q1014=sQuery(id+"F10.wireOp",EDGE,"E1417");
            var Q1015;
            Q1015=sQuery(id+"F10.wireOp",EDGE,"E1497");
            var Q1016;
            Q1016=sQuery(id+"F10.wireOp",EDGE,"E1595");
            var Q1017;
            Q1017=sQuery(id+"F10.wireOp",EDGE,"E1627");
            var Q1018;
            Q1018=sQuery(id+"F10.wireOp",EDGE,"E1375");
            var Q1019;
            Q1019=sQuery(id+"F10.wireOp",EDGE,"E1471");
            var Q1020;
            Q1020=sQuery(id+"F10.wireOp",EDGE,"E1327");
            var Q1021;
            Q1021=sQuery(id+"F10.wireOp",EDGE,"E1538");
            var Q1022;
            Q1022=sQuery(id+"F10.wireOp",EDGE,"E1138");
            var Q1023;
            Q1023=sQuery(id+"F10.wireOp",EDGE,"E1459");
            var Q1024;
            Q1024=sQuery(id+"F10.wireOp",EDGE,"E2085");
            var Q1025;
            Q1025=sQuery(id+"F10.wireOp",EDGE,"E2639");
            var Q1026;
            Q1026=sQuery(id+"F10.wireOp",EDGE,"E2051");
            var Q1027;
            Q1027=sQuery(id+"F10.wireOp",EDGE,"E1573");
            var Q1028;
            Q1028=sQuery(id+"F10.wireOp",EDGE,"E1653");
            var Q1029;
            Q1029=sQuery(id+"F10.wireOp",EDGE,"E1351");
            var Q1030;
            Q1030=sQuery(id+"F10.wireOp",EDGE,"E1479");
            var Q1031;
            Q1031=sQuery(id+"F10.wireOp",EDGE,"E1400");
            var Q1032;
            Q1032=sQuery(id+"F10.wireOp",EDGE,"E1512");
            var Q1033;
            Q1033=sQuery(id+"F10.wireOp",EDGE,"E1562");
            var Q1034;
            Q1034=sQuery(id+"F10.wireOp",EDGE,"E1610");
            var Q1035;
            Q1035=sQuery(id+"F10.wireOp",EDGE,"E1537");
            var Q1036;
            Q1036=sQuery(id+"F10.wireOp",EDGE,"E1137");
            var Q1037;
            Q1037=sQuery(id+"F10.wireOp",EDGE,"E1458");
            var Q1038;
            Q1038=sQuery(id+"F10.wireOp",EDGE,"E2082");
            var Q1039;
            Q1039=sQuery(id+"F10.wireOp",EDGE,"E2633");
            var Q1040;
            Q1040=sQuery(id+"F10.wireOp",EDGE,"E1510");
            var Q1041;
            Q1041=sQuery(id+"F10.wireOp",EDGE,"E2655");
            var Q1042;
            Q1042=sQuery(id+"F10.wireOp",EDGE,"E1572");
            var Q1043;
            Q1043=sQuery(id+"F10.wireOp",EDGE,"E1652");
            var Q1044;
            Q1044=sQuery(id+"F10.wireOp",EDGE,"E1367");
            var Q1045;
            Q1045=sQuery(id+"F10.wireOp",EDGE,"E1495");
            var Q1046;
            Q1046=sQuery(id+"F10.wireOp",EDGE,"E1416");
            var Q1047;
            Q1047=sQuery(id+"F10.wireOp",EDGE,"E1496");
            var Q1048;
            Q1048=sQuery(id+"F10.wireOp",EDGE,"E1594");
            var Q1049;
            Q1049=sQuery(id+"F10.wireOp",EDGE,"E1626");
            var Q1050;
            Q1050=sQuery(id+"F10.wireOp",EDGE,"E1536");
            var Q1051;
            Q1051=sQuery(id+"F10.wireOp",EDGE,"E1136");
            var Q1052;
            Q1052=sQuery(id+"F10.wireOp",EDGE,"E1457");
            var Q1053;
            Q1053=sQuery(id+"F10.wireOp",EDGE,"E2081");
            var Q1054;
            Q1054=sQuery(id+"F10.wireOp",EDGE,"E2640");
            var Q1055;
            Q1055=sQuery(id+"F10.wireOp",EDGE,"E2053");
            var Q1056;
            Q1056=sQuery(id+"F10.wireOp",EDGE,"E1654");
            var Q1057;
            Q1057=sQuery(id+"F10.wireOp",EDGE,"E1588");
            var Q1058;
            Q1058=sQuery(id+"F10.wireOp",EDGE,"E1365");
            var Q1059;
            Q1059=sQuery(id+"F10.wireOp",EDGE,"E1477");
            var Q1060;
            Q1060=sQuery(id+"F10.wireOp",EDGE,"E1399");
            var Q1061;
            Q1061=sQuery(id+"F10.wireOp",EDGE,"E1511");
            var Q1062;
            Q1062=sQuery(id+"F10.wireOp",EDGE,"E1561");
            var Q1063;
            Q1063=sQuery(id+"F10.wireOp",EDGE,"E1609");
            var Q1064;
            Q1064=sQuery(id+"F10.wireOp",EDGE,"E1535");
            var Q1065;
            Q1065=sQuery(id+"F10.wireOp",EDGE,"E1135");
            var Q1066;
            Q1066=sQuery(id+"F10.wireOp",EDGE,"E1456");
            var Q1067;
            Q1067=sQuery(id+"F10.wireOp",EDGE,"E2097");
            var Q1068;
            Q1068=sQuery(id+"F10.wireOp",EDGE,"E1651");
            var Q1069;
            Q1069=sQuery(id+"F10.wireOp",EDGE,"E2741");
            var Q1070;
            Q1070=sQuery(id+"F10.wireOp",EDGE,"E2649");
            var Q1071;
            Q1071=sQuery(id+"F10.wireOp",EDGE,"E1574");
            var Q1072;
            Q1072=sQuery(id+"F10.wireOp",EDGE,"E1364");
            var Q1073;
            Q1073=sQuery(id+"F10.wireOp",EDGE,"E1493");
            var Q1074;
            Q1074=sQuery(id+"F10.wireOp",EDGE,"E1509");
            var Q1075;
            Q1075=sQuery(id+"F10.wireOp",EDGE,"E1415");
            var Q1076;
            Q1076=sQuery(id+"F10.wireOp",EDGE,"E1593");
            var Q1077;
            Q1077=sQuery(id+"F10.wireOp",EDGE,"E1625");
            var Q1078;
            Q1078=sQuery(id+"F10.wireOp",EDGE,"E1455");
            var Q1079;
            Q1079=sQuery(id+"F10.wireOp",EDGE,"E2080");
            var Q1080;
            Q1080=sQuery(id+"F10.wireOp",EDGE,"E1650");
            var Q1081;
            Q1081=sQuery(id+"F10.wireOp",EDGE,"E1587");
            var Q1082;
            Q1082=sQuery(id+"F10.wireOp",EDGE,"E2742");
            var Q1083;
            Q1083=sQuery(id+"F10.wireOp",EDGE,"E2656");
            var Q1084;
            Q1084=sQuery(id+"F10.wireOp",EDGE,"E1366");
            var Q1085;
            Q1085=sQuery(id+"F10.wireOp",EDGE,"E1476");
            var Q1086;
            Q1086=sQuery(id+"F10.wireOp",EDGE,"E1508");
            var Q1087;
            Q1087=sQuery(id+"F10.wireOp",EDGE,"E1397");
            var Q1088;
            Q1088=sQuery(id+"F10.wireOp",EDGE,"E1560");
            var Q1089;
            Q1089=sQuery(id+"F10.wireOp",EDGE,"E1608");
            var Q1090;
            Q1090=sQuery(id+"F10.wireOp",EDGE,"E1649");
            var Q1091;
            Q1091=sQuery(id+"F10.wireOp",EDGE,"E2096");
            var Q1092;
            Q1092=sQuery(id+"F10.wireOp",EDGE,"E1571");
            var Q1093;
            Q1093=sQuery(id+"F10.wireOp",EDGE,"E1363");
            var Q1094;
            Q1094=sQuery(id+"F10.wireOp",EDGE,"E1507");
            var Q1095;
            Q1095=sQuery(id+"F10.wireOp",EDGE,"E2645");
            var Q1096;
            Q1096=sQuery(id+"F10.wireOp",EDGE,"E2661");
            var Q1097;
            Q1097=sQuery(id+"F10.wireOp",EDGE,"E1492");
            var Q1098;
            Q1098=sQuery(id+"F10.wireOp",EDGE,"E1413");
            var Q1099;
            Q1099=sQuery(id+"F10.wireOp",EDGE,"E1592");
            var Q1100;
            Q1100=sQuery(id+"F10.wireOp",EDGE,"E1624");
            var Q1101;
            Q1101=sQuery(id+"F10.wireOp",EDGE,"E1648");
            var Q1102;
            Q1102=sQuery(id+"F10.wireOp",EDGE,"E2079");
            var Q1103;
            Q1103=sQuery(id+"F10.wireOp",EDGE,"E1586");
            var Q1104;
            Q1104=sQuery(id+"F10.wireOp",EDGE,"E1362");
            var Q1105;
            Q1105=sQuery(id+"F10.wireOp",EDGE,"E1506");
            var Q1106;
            Q1106=sQuery(id+"F10.wireOp",EDGE,"E2636");
            var Q1107;
            Q1107=sQuery(id+"F10.wireOp",EDGE,"E2652");
            var Q1108;
            Q1108=sQuery(id+"F10.wireOp",EDGE,"E1478");
            var Q1109;
            Q1109=sQuery(id+"F10.wireOp",EDGE,"E1396");
            var Q1110;
            Q1110=sQuery(id+"F10.wireOp",EDGE,"E1559");
            var Q1111;
            Q1111=sQuery(id+"F10.wireOp",EDGE,"E1607");
            var Q1112;
            Q1112=sQuery(id+"F10.wireOp",EDGE,"E1663");
            var Q1113;
            Q1113=sQuery(id+"F10.wireOp",EDGE,"E1647");
            var Q1114;
            Q1114=sQuery(id+"F10.wireOp",EDGE,"E2095");
            var Q1115;
            Q1115=sQuery(id+"F10.wireOp",EDGE,"E1505");
            var Q1116;
            Q1116=sQuery(id+"F10.wireOp",EDGE,"E1361");
            var Q1117;
            Q1117=sQuery(id+"F10.wireOp",EDGE,"E1570");
            var Q1118;
            Q1118=sQuery(id+"F10.wireOp",EDGE,"E2050");
            var Q1119;
            Q1119=sQuery(id+"F10.wireOp",EDGE,"E1494");
            var Q1120;
            Q1120=sQuery(id+"F10.wireOp",EDGE,"E1412");
            var Q1121;
            Q1121=sQuery(id+"F10.wireOp",EDGE,"E1591");
            var Q1122;
            Q1122=sQuery(id+"F10.wireOp",EDGE,"E1623");
            var Q1123;
            Q1123=sQuery(id+"F10.wireOp",EDGE,"E1674");
            var Q1124;
            Q1124=sQuery(id+"F10.wireOp",EDGE,"E2078");
            var Q1125;
            Q1125=sQuery(id+"F10.wireOp",EDGE,"E1504");
            var Q1126;
            Q1126=sQuery(id+"F10.wireOp",EDGE,"E1360");
            var Q1127;
            Q1127=sQuery(id+"F10.wireOp",EDGE,"E1585");
            var Q1128;
            Q1128=sQuery(id+"F10.wireOp",EDGE,"E2049");
            var Q1129;
            Q1129=sQuery(id+"F10.wireOp",EDGE,"E1491");
            var Q1130;
            Q1130=sQuery(id+"F10.wireOp",EDGE,"E1398");
            var Q1131;
            Q1131=sQuery(id+"F10.wireOp",EDGE,"E1557");
            var Q1132;
            Q1132=sQuery(id+"F10.wireOp",EDGE,"E1605");
            var Q1133;
            Q1133=sQuery(id+"F10.wireOp",EDGE,"E1359");
            var Q1134;
            Q1134=sQuery(id+"F10.wireOp",EDGE,"E1503");
            var Q1135;
            Q1135=sQuery(id+"F10.wireOp",EDGE,"E2094");
            var Q1136;
            Q1136=sQuery(id+"F10.wireOp",EDGE,"E1569");
            var Q1137;
            Q1137=sQuery(id+"F10.wireOp",EDGE,"E1475");
            var Q1138;
            Q1138=sQuery(id+"F10.wireOp",EDGE,"E1414");
            var Q1139;
            Q1139=sQuery(id+"F10.wireOp",EDGE,"E1589");
            var Q1140;
            Q1140=sQuery(id+"F10.wireOp",EDGE,"E1621");
            var Q1141;
            Q1141=sQuery(id+"F10.wireOp",EDGE,"E1584");
            var Q1142;
            Q1142=sQuery(id+"F10.wireOp",EDGE,"E1490");
            var Q1143;
            Q1143=sQuery(id+"F10.wireOp",EDGE,"E1395");
            var Q1144;
            Q1144=sQuery(id+"F10.wireOp",EDGE,"E1558");
            var Q1145;
            Q1145=sQuery(id+"F10.wireOp",EDGE,"E1604");
            var Q1146;
            Q1146=sQuery(id+"F10.wireOp",EDGE,"E1568");
            var Q1147;
            Q1147=sQuery(id+"F10.wireOp",EDGE,"E1474");
            var Q1148;
            Q1148=sQuery(id+"F10.wireOp",EDGE,"E1411");
            var Q1149;
            Q1149=sQuery(id+"F10.wireOp",EDGE,"E1590");
            var Q1150;
            Q1150=sQuery(id+"F10.wireOp",EDGE,"E1620");
            var Q1151;
            Q1151=sQuery(id+"F10.wireOp",EDGE,"E1583");
            var Q1152;
            Q1152=sQuery(id+"F10.wireOp",EDGE,"E1473");
            var Q1153;
            Q1153=sQuery(id+"F10.wireOp",EDGE,"E1394");
            var Q1154;
            Q1154=sQuery(id+"F10.wireOp",EDGE,"E1555");
            var Q1155;
            Q1155=sQuery(id+"F10.wireOp",EDGE,"E1606");
            var Q1156;
            Q1156=sQuery(id+"F10.wireOp",EDGE,"E2039");
            var Q1157;
            Q1157=sQuery(id+"F10.wireOp",EDGE,"E2026");
            var Q1158;
            Q1158=sQuery(id+"F10.wireOp",EDGE,"E2029");
            var Q1159;
            Q1159=sQuery(id+"F10.wireOp",EDGE,"E2666");
            var Q1160;
            Q1160=sQuery(id+"F10.wireOp",EDGE,"E1489");
            var Q1161;
            Q1161=sQuery(id+"F10.wireOp",EDGE,"E1602");
            var Q1162;
            Q1162=sQuery(id+"F10.wireOp",EDGE,"E1410");
            var Q1163;
            Q1163=sQuery(id+"F10.wireOp",EDGE,"E1622");
            var Q1164;
            Q1164=sQuery(id+"F10.wireOp",EDGE,"E2038");
            var Q1165;
            Q1165=sQuery(id+"F10.wireOp",EDGE,"E2025");
            var Q1166;
            Q1166=sQuery(id+"F10.wireOp",EDGE,"E2028");
            var Q1167;
            Q1167=sQuery(id+"F10.wireOp",EDGE,"E2045");
            var Q1168;
            Q1168=sQuery(id+"F10.wireOp",EDGE,"E1488");
            var Q1169;
            Q1169=sQuery(id+"F10.wireOp",EDGE,"E1393");
            var Q1170;
            Q1170=sQuery(id+"F10.wireOp",EDGE,"E1554");
            var Q1171;
            Q1171=sQuery(id+"F10.wireOp",EDGE,"E1603");
            var Q1172;
            Q1172=sQuery(id+"F10.wireOp",EDGE,"E2670");
            var Q1173;
            Q1173=sQuery(id+"F10.wireOp",EDGE,"E2024");
            var Q1174;
            Q1174=sQuery(id+"F10.wireOp",EDGE,"E2027");
            var Q1175;
            Q1175=sQuery(id+"F10.wireOp",EDGE,"E2044");
            var Q1176;
            Q1176=sQuery(id+"F10.wireOp",EDGE,"E1424");
            var Q1177;
            Q1177=sQuery(id+"F10.wireOp",EDGE,"E1601");
            var Q1178;
            Q1178=sQuery(id+"F10.wireOp",EDGE,"E1409");
            var Q1179;
            Q1179=sQuery(id+"F10.wireOp",EDGE,"E2034");
            var Q1180;
            Q1180=sQuery(id+"F10.wireOp",EDGE,"E1619");
            var Q1181;
            Q1181=sQuery(id+"F10.wireOp",EDGE,"E2036");
            var Q1182;
            Q1182=sQuery(id+"F10.wireOp",EDGE,"E2023");
            var Q1183;
            Q1183=sQuery(id+"F10.wireOp",EDGE,"E2667");
            var Q1184;
            Q1184=sQuery(id+"F10.wireOp",EDGE,"E1487");
            var Q1185;
            Q1185=sQuery(id+"F10.wireOp",EDGE,"E1408");
            var Q1186;
            Q1186=sQuery(id+"F10.wireOp",EDGE,"E1553");
            var Q1187;
            Q1187=sQuery(id+"F10.wireOp",EDGE,"E2033");
            var Q1188;
            Q1188=sQuery(id+"F10.wireOp",EDGE,"E1618");
            var Q1189;
            Q1189=sQuery(id+"F10.wireOp",EDGE,"E2671");
            var Q1190;
            Q1190=sQuery(id+"F10.wireOp",EDGE,"E2022");
            var Q1191;
            Q1191=sQuery(id+"F10.wireOp",EDGE,"E2042");
            var Q1192;
            Q1192=sQuery(id+"F10.wireOp",EDGE,"E1391");
            var Q1193;
            Q1193=sQuery(id+"F10.wireOp",EDGE,"E1423");
            var Q1194;
            Q1194=sQuery(id+"F10.wireOp",EDGE,"E1600");
            var Q1195;
            Q1195=sQuery(id+"F10.wireOp",EDGE,"E2032");
            var Q1196;
            Q1196=sQuery(id+"F10.wireOp",EDGE,"E1617");
            var Q1197;
            Q1197=sQuery(id+"F10.wireOp",EDGE,"E2035");
            var Q1198;
            Q1198=sQuery(id+"F10.wireOp",EDGE,"E2020");
            var Q1199;
            Q1199=sQuery(id+"F10.wireOp",EDGE,"E2041");
            var Q1200;
            Q1200=sQuery(id+"F10.wireOp",EDGE,"E1407");
            var Q1201;
            Q1201=sQuery(id+"F10.wireOp",EDGE,"E2030");
            var Q1202;
            Q1202=sQuery(id+"F10.wireOp",EDGE,"E1552");
            var Q1203;
            Q1203=sQuery(id+"F10.wireOp",EDGE,"E1616");
            var Q1204;
            Q1204=sQuery(id+"F10.wireOp",EDGE,"E2672");
            var Q1205;
            Q1205=sQuery(id+"F10.wireOp",EDGE,"E2021");
            var Q1206;
            Q1206=sQuery(id+"F10.wireOp",EDGE,"E2040");
            var Q1207;
            Q1207=sQuery(id+"F10.wireOp",EDGE,"E1615");
            var Q1208;
            Q1208=sQuery(id+"F10.wireOp",EDGE,"E1599");
            var Q1209;
            Q1209=sQuery(id+"F10.wireOp",EDGE,"E2678");
            var Q1210;
            Q1210=sQuery(id+"F10.wireOp",EDGE,"E2669");
            var Q1211;
            Q1211=sQuery(id+"F10.wireOp",EDGE,"E1567");
            var Q1212;
            Q1212=sQuery(id+"F10.wireOp",EDGE,"E1631");
            var Q1213;
            Q1213=sQuery(id+"F10.wireOp",EDGE,"E2665");
            var Q1214;
            Q1214=sQuery(id+"F10.wireOp",EDGE,"E2668");
            var Q1215;
            Q1215=sQuery(id+"F10.wireOp",EDGE,"E2048");
            var Q1216;
            Q1216=sQuery(id+"F10.wireOp",EDGE,"E2047");
            var Q1217;
            Q1217=sQuery(id+"F10.wireOp",EDGE,"E2046");
            var Q1218;
            Q1218=sQuery(id+"F10.wireOp",EDGE,"E2015");
            var Q1219;
            Q1219=sQuery(id+"F10.wireOp",EDGE,"E1968");
            var Q1220;
            Q1220=sQuery(id+"F10.wireOp",EDGE,"E1938");
            var Q1221;
            Q1221=sQuery(id+"F10.wireOp",EDGE,"E2004");
            var Q1222;
            Q1222=sQuery(id+"F10.wireOp",EDGE,"E1685");
            var Q1223;
            Q1223=sQuery(id+"F10.wireOp",EDGE,"E2727");
            var Q1224;
            Q1224=sQuery(id+"F10.wireOp",EDGE,"E2679");
            var Q1225;
            Q1225=sQuery(id+"F10.wireOp",EDGE,"E1656");
            var Q1226;
            Q1226=sQuery(id+"F10.wireOp",EDGE,"E1993");
            var Q1227;
            Q1227=sQuery(id+"F10.wireOp",EDGE,"E2731");
            var Q1228;
            Q1228=sQuery(id+"F10.wireOp",EDGE,"E1677");
            var Q1229;
            Q1229=sQuery(id+"F10.wireOp",EDGE,"E2699");
            var Q1230;
            Q1230=sQuery(id+"F10.wireOp",EDGE,"E1694");
            var Q1231;
            Q1231=sQuery(id+"F10.wireOp",EDGE,"E1678");
            var Q1232;
            Q1232=sQuery(id+"F10.wireOp",EDGE,"E1662");
            var Q1233;
            Q1233=sQuery(id+"F10.wireOp",EDGE,"E1997");
            var Q1234;
            Q1234=sQuery(id+"F10.wireOp",EDGE,"E1981");
            var Q1235;
            Q1235=sQuery(id+"F10.wireOp",EDGE,"E1965");
            var Q1236;
            Q1236=sQuery(id+"F10.wireOp",EDGE,"E2721");
            var Q1237;
            Q1237=sQuery(id+"F10.wireOp",EDGE,"E2013");
            var Q1238;
            Q1238=sQuery(id+"F10.wireOp",EDGE,"E1726");
            var Q1239;
            Q1239=sQuery(id+"F10.wireOp",EDGE,"E1710");
            var Q1240;
            Q1240=sQuery(id+"F10.wireOp",EDGE,"E1790");
            var Q1241;
            Q1241=sQuery(id+"F10.wireOp",EDGE,"E1774");
            var Q1242;
            Q1242=sQuery(id+"F10.wireOp",EDGE,"E2689");
            var Q1243;
            Q1243=sQuery(id+"F10.wireOp",EDGE,"E1854");
            var Q1244;
            Q1244=sQuery(id+"F10.wireOp",EDGE,"E1918");
            var Q1245;
            Q1245=sQuery(id+"F10.wireOp",EDGE,"E1902");
            var Q1246;
            Q1246=sQuery(id+"F10.wireOp",EDGE,"E1682");
            var Q1247;
            Q1247=sQuery(id+"F10.wireOp",EDGE,"E1683");
            var Q1248;
            Q1248=sQuery(id+"F10.wireOp",EDGE,"E2697");
            var Q1249;
            Q1249=sQuery(id+"F10.wireOp",EDGE,"E1684");
            var Q1250;
            Q1250=sQuery(id+"F10.wireOp",EDGE,"E2680");
            var Q1251;
            Q1251=sQuery(id+"F10.wireOp",EDGE,"E2724");
            var Q1252;
            Q1252=sQuery(id+"F10.wireOp",EDGE,"E2734");
            var Q1253;
            Q1253=sQuery(id+"F10.wireOp",EDGE,"E1992");
            var Q1254;
            Q1254=sQuery(id+"F10.wireOp",EDGE,"E1676");
            var Q1255;
            Q1255=sQuery(id+"F10.wireOp",EDGE,"E1996");
            var Q1256;
            Q1256=sQuery(id+"F10.wireOp",EDGE,"E1980");
            var Q1257;
            Q1257=sQuery(id+"F10.wireOp",EDGE,"E1964");
            var Q1258;
            Q1258=sQuery(id+"F10.wireOp",EDGE,"E2012");
            var Q1259;
            Q1259=sQuery(id+"F10.wireOp",EDGE,"E1693");
            var Q1260;
            Q1260=sQuery(id+"F10.wireOp",EDGE,"E1661");
            var Q1261;
            Q1261=sQuery(id+"F10.wireOp",EDGE,"E1709");
            var Q1262;
            Q1262=sQuery(id+"F10.wireOp",EDGE,"E1853");
            var Q1263;
            Q1263=sQuery(id+"F10.wireOp",EDGE,"E2705");
            var Q1264;
            Q1264=sQuery(id+"F10.wireOp",EDGE,"E2673");
            var Q1265;
            Q1265=sQuery(id+"F10.wireOp",EDGE,"E1758");
            var Q1266;
            Q1266=sQuery(id+"F10.wireOp",EDGE,"E1742");
            var Q1267;
            Q1267=sQuery(id+"F10.wireOp",EDGE,"E1806");
            var Q1268;
            Q1268=sQuery(id+"F10.wireOp",EDGE,"E1870");
            var Q1269;
            Q1269=sQuery(id+"F10.wireOp",EDGE,"E1933");
            var Q1270;
            Q1270=sQuery(id+"F10.wireOp",EDGE,"E1681");
            var Q1271;
            Q1271=sQuery(id+"F10.wireOp",EDGE,"E2698");
            var Q1272;
            Q1272=sQuery(id+"F10.wireOp",EDGE,"E1686");
            var Q1273;
            Q1273=sQuery(id+"F10.wireOp",EDGE,"E2003");
            var Q1274;
            Q1274=sQuery(id+"F10.wireOp",EDGE,"E2728");
            var Q1275;
            Q1275=sQuery(id+"F10.wireOp",EDGE,"E2695");
            var Q1276;
            Q1276=sQuery(id+"F10.wireOp",EDGE,"E1675");
            var Q1277;
            Q1277=sQuery(id+"F10.wireOp",EDGE,"E1963");
            var Q1278;
            Q1278=sQuery(id+"F10.wireOp",EDGE,"E2011");
            var Q1279;
            Q1279=sQuery(id+"F10.wireOp",EDGE,"E1995");
            var Q1280;
            Q1280=sQuery(id+"F10.wireOp",EDGE,"E1979");
            var Q1281;
            Q1281=sQuery(id+"F10.wireOp",EDGE,"E1660");
            var Q1282;
            Q1282=sQuery(id+"F10.wireOp",EDGE,"E1708");
            var Q1283;
            Q1283=sQuery(id+"F10.wireOp",EDGE,"E1692");
            var Q1284;
            Q1284=sQuery(id+"F10.wireOp",EDGE,"E2715");
            var Q1285;
            Q1285=sQuery(id+"F10.wireOp",EDGE,"E2683");
            var Q1286;
            Q1286=sQuery(id+"F10.wireOp",EDGE,"E1725");
            var Q1287;
            Q1287=sQuery(id+"F10.wireOp",EDGE,"E1773");
            var Q1288;
            Q1288=sQuery(id+"F10.wireOp",EDGE,"E1885");
            var Q1289;
            Q1289=sQuery(id+"F10.wireOp",EDGE,"E1822");
            var Q1290;
            Q1290=sQuery(id+"F10.wireOp",EDGE,"E1886");
            var Q1291;
            Q1291=sQuery(id+"F10.wireOp",EDGE,"E1838");
            var Q1292;
            Q1292=sQuery(id+"F10.wireOp",EDGE,"E1680");
            var Q1293;
            Q1293=sQuery(id+"F10.wireOp",EDGE,"E2725");
            var Q1294;
            Q1294=sQuery(id+"F10.wireOp",EDGE,"E2729");
            var Q1295;
            Q1295=sQuery(id+"F10.wireOp",EDGE,"E2681");
            var Q1296;
            Q1296=sQuery(id+"F10.wireOp",EDGE,"E2719");
            var Q1297;
            Q1297=sQuery(id+"F10.wireOp",EDGE,"E1673");
            var Q1298;
            Q1298=sQuery(id+"F10.wireOp",EDGE,"E1962");
            var Q1299;
            Q1299=sQuery(id+"F10.wireOp",EDGE,"E2010");
            var Q1300;
            Q1300=sQuery(id+"F10.wireOp",EDGE,"E1994");
            var Q1301;
            Q1301=sQuery(id+"F10.wireOp",EDGE,"E1978");
            var Q1302;
            Q1302=sQuery(id+"F10.wireOp",EDGE,"E1659");
            var Q1303;
            Q1303=sQuery(id+"F10.wireOp",EDGE,"E1707");
            var Q1304;
            Q1304=sQuery(id+"F10.wireOp",EDGE,"E1691");
            var Q1305;
            Q1305=sQuery(id+"F10.wireOp",EDGE,"E1884");
            var Q1306;
            Q1306=sQuery(id+"F10.wireOp",EDGE,"E2722");
            var Q1307;
            Q1307=sQuery(id+"F10.wireOp",EDGE,"E2690");
            var Q1308;
            Q1308=sQuery(id+"F10.wireOp",EDGE,"E1757");
            var Q1309;
            Q1309=sQuery(id+"F10.wireOp",EDGE,"E1741");
            var Q1310;
            Q1310=sQuery(id+"F10.wireOp",EDGE,"E1789");
            var Q1311;
            Q1311=sQuery(id+"F10.wireOp",EDGE,"E1917");
            var Q1312;
            Q1312=sQuery(id+"F10.wireOp",EDGE,"E1949");
            var Q1313;
            Q1313=sQuery(id+"F10.wireOp",EDGE,"E1679");
            var Q1314;
            Q1314=sQuery(id+"F10.wireOp",EDGE,"E2002");
            var Q1315;
            Q1315=sQuery(id+"F10.wireOp",EDGE,"E2726");
            var Q1316;
            Q1316=sQuery(id+"F10.wireOp",EDGE,"E2700");
            var Q1317;
            Q1317=sQuery(id+"F10.wireOp",EDGE,"E2730");
            var Q1318;
            Q1318=sQuery(id+"F10.wireOp",EDGE,"E1672");
            var Q1319;
            Q1319=sQuery(id+"F10.wireOp",EDGE,"E1961");
            var Q1320;
            Q1320=sQuery(id+"F10.wireOp",EDGE,"E2009");
            var Q1321;
            Q1321=sQuery(id+"F10.wireOp",EDGE,"E1977");
            var Q1322;
            Q1322=sQuery(id+"F10.wireOp",EDGE,"E1658");
            var Q1323;
            Q1323=sQuery(id+"F10.wireOp",EDGE,"E1706");
            var Q1324;
            Q1324=sQuery(id+"F10.wireOp",EDGE,"E1690");
            var Q1325;
            Q1325=sQuery(id+"F10.wireOp",EDGE,"E1756");
            var Q1326;
            Q1326=sQuery(id+"F10.wireOp",EDGE,"E1740");
            var Q1327;
            Q1327=sQuery(id+"F10.wireOp",EDGE,"E1852");
            var Q1328;
            Q1328=sQuery(id+"F10.wireOp",EDGE,"E2706");
            var Q1329;
            Q1329=sQuery(id+"F10.wireOp",EDGE,"E2674");
            var Q1330;
            Q1330=sQuery(id+"F10.wireOp",EDGE,"E1805");
            var Q1331;
            Q1331=sQuery(id+"F10.wireOp",EDGE,"E1932");
            var Q1332;
            Q1332=sQuery(id+"F10.wireOp",EDGE,"E1901");
            var Q1333;
            Q1333=sQuery(id+"F10.wireOp",EDGE,"E2001");
            var Q1334;
            Q1334=sQuery(id+"F10.wireOp",EDGE,"E2732");
            var Q1335;
            Q1335=sQuery(id+"F10.wireOp",EDGE,"E1671");
            var Q1336;
            Q1336=sQuery(id+"F10.wireOp",EDGE,"E2717");
            var Q1337;
            Q1337=sQuery(id+"F10.wireOp",EDGE,"E2685");
            var Q1338;
            Q1338=sQuery(id+"F10.wireOp",EDGE,"E2008");
            var Q1339;
            Q1339=sQuery(id+"F10.wireOp",EDGE,"E1976");
            var Q1340;
            Q1340=sQuery(id+"F10.wireOp",EDGE,"E1960");
            var Q1341;
            Q1341=sQuery(id+"F10.wireOp",EDGE,"E1657");
            var Q1342;
            Q1342=sQuery(id+"F10.wireOp",EDGE,"E1705");
            var Q1343;
            Q1343=sQuery(id+"F10.wireOp",EDGE,"E1689");
            var Q1344;
            Q1344=sQuery(id+"F10.wireOp",EDGE,"E1883");
            var Q1345;
            Q1345=sQuery(id+"F10.wireOp",EDGE,"E1724");
            var Q1346;
            Q1346=sQuery(id+"F10.wireOp",EDGE,"E1772");
            var Q1347;
            Q1347=sQuery(id+"F10.wireOp",EDGE,"E1821");
            var Q1348;
            Q1348=sQuery(id+"F10.wireOp",EDGE,"E1869");
            var Q1349;
            Q1349=sQuery(id+"F10.wireOp",EDGE,"E1837");
            var Q1350;
            Q1350=sQuery(id+"F10.wireOp",EDGE,"E2000");
            var Q1351;
            Q1351=sQuery(id+"F10.wireOp",EDGE,"E2733");
            var Q1352;
            Q1352=sQuery(id+"F10.wireOp",EDGE,"E1988");
            var Q1353;
            Q1353=sQuery(id+"F10.wireOp",EDGE,"E1717");
            var Q1354;
            Q1354=sQuery(id+"F10.wireOp",EDGE,"E1669");
            var Q1355;
            Q1355=sQuery(id+"F10.wireOp",EDGE,"E2692");
            var Q1356;
            Q1356=sQuery(id+"F10.wireOp",EDGE,"E2701");
            var Q1357;
            Q1357=sQuery(id+"F10.wireOp",EDGE,"E1655");
            var Q1358;
            Q1358=sQuery(id+"F10.wireOp",EDGE,"E2007");
            var Q1359;
            Q1359=sQuery(id+"F10.wireOp",EDGE,"E1975");
            var Q1360;
            Q1360=sQuery(id+"F10.wireOp",EDGE,"E1688");
            var Q1361;
            Q1361=sQuery(id+"F10.wireOp",EDGE,"E1755");
            var Q1362;
            Q1362=sQuery(id+"F10.wireOp",EDGE,"E1739");
            var Q1363;
            Q1363=sQuery(id+"F10.wireOp",EDGE,"E1851");
            var Q1364;
            Q1364=sQuery(id+"F10.wireOp",EDGE,"E1804");
            var Q1365;
            Q1365=sQuery(id+"F10.wireOp",EDGE,"E1931");
            var Q1366;
            Q1366=sQuery(id+"F10.wireOp",EDGE,"E1948");
            var Q1367;
            Q1367=sQuery(id+"F10.wireOp",EDGE,"E1999");
            var Q1368;
            Q1368=sQuery(id+"F10.wireOp",EDGE,"E1670");
            var Q1369;
            Q1369=sQuery(id+"F10.wireOp",EDGE,"E1987");
            var Q1370;
            Q1370=sQuery(id+"F10.wireOp",EDGE,"E1716");
            var Q1371;
            Q1371=sQuery(id+"F10.wireOp",EDGE,"E1668");
            var Q1372;
            Q1372=sQuery(id+"F10.wireOp",EDGE,"E2711");
            var Q1373;
            Q1373=sQuery(id+"F10.wireOp",EDGE,"E2676");
            var Q1374;
            Q1374=sQuery(id+"F10.wireOp",EDGE,"E2006");
            var Q1375;
            Q1375=sQuery(id+"F10.wireOp",EDGE,"E1959");
            var Q1376;
            Q1376=sQuery(id+"F10.wireOp",EDGE,"E1704");
            var Q1377;
            Q1377=sQuery(id+"F10.wireOp",EDGE,"E1850");
            var Q1378;
            Q1378=sQuery(id+"F10.wireOp",EDGE,"E1723");
            var Q1379;
            Q1379=sQuery(id+"F10.wireOp",EDGE,"E1771");
            var Q1380;
            Q1380=sQuery(id+"F10.wireOp",EDGE,"E1820");
            var Q1381;
            Q1381=sQuery(id+"F10.wireOp",EDGE,"E1916");
            var Q1382;
            Q1382=sQuery(id+"F10.wireOp",EDGE,"E1868");
            var Q1383;
            Q1383=sQuery(id+"F10.wireOp",EDGE,"E1998");
            var Q1384;
            Q1384=sQuery(id+"F10.wireOp",EDGE,"E1986");
            var Q1385;
            Q1385=sQuery(id+"F10.wireOp",EDGE,"E1667");
            var Q1386;
            Q1386=sQuery(id+"F10.wireOp",EDGE,"E1718");
            var Q1387;
            Q1387=sQuery(id+"F10.wireOp",EDGE,"E2019");
            var Q1388;
            Q1388=sQuery(id+"F10.wireOp",EDGE,"E2686");
            var Q1389;
            Q1389=sQuery(id+"F10.wireOp",EDGE,"E2708");
            var Q1390;
            Q1390=sQuery(id+"F10.wireOp",EDGE,"E1974");
            var Q1391;
            Q1391=sQuery(id+"F10.wireOp",EDGE,"E1687");
            var Q1392;
            Q1392=sQuery(id+"F10.wireOp",EDGE,"E1882");
            var Q1393;
            Q1393=sQuery(id+"F10.wireOp",EDGE,"E1754");
            var Q1394;
            Q1394=sQuery(id+"F10.wireOp",EDGE,"E1738");
            var Q1395;
            Q1395=sQuery(id+"F10.wireOp",EDGE,"E1788");
            var Q1396;
            Q1396=sQuery(id+"F10.wireOp",EDGE,"E1836");
            var Q1397;
            Q1397=sQuery(id+"F10.wireOp",EDGE,"E1900");
            var Q1398;
            Q1398=sQuery(id+"F10.wireOp",EDGE,"E1985");
            var Q1399;
            Q1399=sQuery(id+"F10.wireOp",EDGE,"E1666");
            var Q1400;
            Q1400=sQuery(id+"F10.wireOp",EDGE,"E1715");
            var Q1401;
            Q1401=sQuery(id+"F10.wireOp",EDGE,"E2005");
            var Q1402;
            Q1402=sQuery(id+"F10.wireOp",EDGE,"E2696");
            var Q1403;
            Q1403=sQuery(id+"F10.wireOp",EDGE,"E2718");
            var Q1404;
            Q1404=sQuery(id+"F10.wireOp",EDGE,"E1958");
            var Q1405;
            Q1405=sQuery(id+"F10.wireOp",EDGE,"E1703");
            var Q1406;
            Q1406=sQuery(id+"F10.wireOp",EDGE,"E1784");
            var Q1407;
            Q1407=sQuery(id+"F10.wireOp",EDGE,"E1881");
            var Q1408;
            Q1408=sQuery(id+"F10.wireOp",EDGE,"E1722");
            var Q1409;
            Q1409=sQuery(id+"F10.wireOp",EDGE,"E1770");
            var Q1410;
            Q1410=sQuery(id+"F10.wireOp",EDGE,"E1803");
            var Q1411;
            Q1411=sQuery(id+"F10.wireOp",EDGE,"E1915");
            var Q1412;
            Q1412=sQuery(id+"F10.wireOp",EDGE,"E1947");
            var Q1413;
            Q1413=sQuery(id+"F10.wireOp",EDGE,"E1984");
            var Q1414;
            Q1414=sQuery(id+"F10.wireOp",EDGE,"E1665");
            var Q1415;
            Q1415=sQuery(id+"F10.wireOp",EDGE,"E1714");
            var Q1416;
            Q1416=sQuery(id+"F10.wireOp",EDGE,"E2018");
            var Q1417;
            Q1417=sQuery(id+"F10.wireOp",EDGE,"E2687");
            var Q1418;
            Q1418=sQuery(id+"F10.wireOp",EDGE,"E1972");
            var Q1419;
            Q1419=sQuery(id+"F10.wireOp",EDGE,"E1701");
            var Q1420;
            Q1420=sQuery(id+"F10.wireOp",EDGE,"E2702");
            var Q1421;
            Q1421=sQuery(id+"F10.wireOp",EDGE,"E1849");
            var Q1422;
            Q1422=sQuery(id+"F10.wireOp",EDGE,"E1753");
            var Q1423;
            Q1423=sQuery(id+"F10.wireOp",EDGE,"E1737");
            var Q1424;
            Q1424=sQuery(id+"F10.wireOp",EDGE,"E1835");
            var Q1425;
            Q1425=sQuery(id+"F10.wireOp",EDGE,"E1819");
            var Q1426;
            Q1426=sQuery(id+"F10.wireOp",EDGE,"E1867");
            var Q1427;
            Q1427=sQuery(id+"F10.wireOp",EDGE,"E1983");
            var Q1428;
            Q1428=sQuery(id+"F10.wireOp",EDGE,"E1664");
            var Q1429;
            Q1429=sQuery(id+"F10.wireOp",EDGE,"E1713");
            var Q1430;
            Q1430=sQuery(id+"F10.wireOp",EDGE,"E2017");
            var Q1431;
            Q1431=sQuery(id+"F10.wireOp",EDGE,"E2688");
            var Q1432;
            Q1432=sQuery(id+"F10.wireOp",EDGE,"E1700");
            var Q1433;
            Q1433=sQuery(id+"F10.wireOp",EDGE,"E1956");
            var Q1434;
            Q1434=sQuery(id+"F10.wireOp",EDGE,"E2712");
            var Q1435;
            Q1435=sQuery(id+"F10.wireOp",EDGE,"E1880");
            var Q1436;
            Q1436=sQuery(id+"F10.wireOp",EDGE,"E1721");
            var Q1437;
            Q1437=sQuery(id+"F10.wireOp",EDGE,"E1769");
            var Q1438;
            Q1438=sQuery(id+"F10.wireOp",EDGE,"E1930");
            var Q1439;
            Q1439=sQuery(id+"F10.wireOp",EDGE,"E1787");
            var Q1440;
            Q1440=sQuery(id+"F10.wireOp",EDGE,"E1899");
            var Q1441;
            Q1441=sQuery(id+"F10.wireOp",EDGE,"E1982");
            var Q1442;
            Q1442=sQuery(id+"F10.wireOp",EDGE,"E1712");
            var Q1443;
            Q1443=sQuery(id+"F10.wireOp",EDGE,"E2016");
            var Q1444;
            Q1444=sQuery(id+"F10.wireOp",EDGE,"E2682");
            var Q1445;
            Q1445=sQuery(id+"F10.wireOp",EDGE,"E1702");
            var Q1446;
            Q1446=sQuery(id+"F10.wireOp",EDGE,"E1971");
            var Q1447;
            Q1447=sQuery(id+"F10.wireOp",EDGE,"E2703");
            var Q1448;
            Q1448=sQuery(id+"F10.wireOp",EDGE,"E1848");
            var Q1449;
            Q1449=sQuery(id+"F10.wireOp",EDGE,"E1720");
            var Q1450;
            Q1450=sQuery(id+"F10.wireOp",EDGE,"E1785");
            var Q1451;
            Q1451=sQuery(id+"F10.wireOp",EDGE,"E1834");
            var Q1452;
            Q1452=sQuery(id+"F10.wireOp",EDGE,"E1802");
            var Q1453;
            Q1453=sQuery(id+"F10.wireOp",EDGE,"E1946");
            var Q1454;
            Q1454=sQuery(id+"F10.wireOp",EDGE,"E1711");
            var Q1455;
            Q1455=sQuery(id+"F10.wireOp",EDGE,"E2014");
            var Q1456;
            Q1456=sQuery(id+"F10.wireOp",EDGE,"E1699");
            var Q1457;
            Q1457=sQuery(id+"F10.wireOp",EDGE,"E2693");
            var Q1458;
            Q1458=sQuery(id+"F10.wireOp",EDGE,"E2713");
            var Q1459;
            Q1459=sQuery(id+"F10.wireOp",EDGE,"E1955");
            var Q1460;
            Q1460=sQuery(id+"F10.wireOp",EDGE,"E1991");
            var Q1461;
            Q1461=sQuery(id+"F10.wireOp",EDGE,"E1752");
            var Q1462;
            Q1462=sQuery(id+"F10.wireOp",EDGE,"E1736");
            var Q1463;
            Q1463=sQuery(id+"F10.wireOp",EDGE,"E1866");
            var Q1464;
            Q1464=sQuery(id+"F10.wireOp",EDGE,"E1929");
            var Q1465;
            Q1465=sQuery(id+"F10.wireOp",EDGE,"E1818");
            var Q1466;
            Q1466=sQuery(id+"F10.wireOp",EDGE,"E1698");
            var Q1467;
            Q1467=sQuery(id+"F10.wireOp",EDGE,"E2677");
            var Q1468;
            Q1468=sQuery(id+"F10.wireOp",EDGE,"E2720");
            var Q1469;
            Q1469=sQuery(id+"F10.wireOp",EDGE,"E1973");
            var Q1470;
            Q1470=sQuery(id+"F10.wireOp",EDGE,"E1735");
            var Q1471;
            Q1471=sQuery(id+"F10.wireOp",EDGE,"E1879");
            var Q1472;
            Q1472=sQuery(id+"F10.wireOp",EDGE,"E1768");
            var Q1473;
            Q1473=sQuery(id+"F10.wireOp",EDGE,"E1928");
            var Q1474;
            Q1474=sQuery(id+"F10.wireOp",EDGE,"E1898");
            var Q1475;
            Q1475=sQuery(id+"F10.wireOp",EDGE,"E1786");
            var Q1476;
            Q1476=sQuery(id+"F10.wireOp",EDGE,"E1697");
            var Q1477;
            Q1477=sQuery(id+"F10.wireOp",EDGE,"E2684");
            var Q1478;
            Q1478=sQuery(id+"F10.wireOp",EDGE,"E2704");
            var Q1479;
            Q1479=sQuery(id+"F10.wireOp",EDGE,"E1957");
            var Q1480;
            Q1480=sQuery(id+"F10.wireOp",EDGE,"E1990");
            var Q1481;
            Q1481=sQuery(id+"F10.wireOp",EDGE,"E1719");
            var Q1482;
            Q1482=sQuery(id+"F10.wireOp",EDGE,"E1751");
            var Q1483;
            Q1483=sQuery(id+"F10.wireOp",EDGE,"E1833");
            var Q1484;
            Q1484=sQuery(id+"F10.wireOp",EDGE,"E1801");
            var Q1485;
            Q1485=sQuery(id+"F10.wireOp",EDGE,"E1914");
            var Q1486;
            Q1486=sQuery(id+"F10.wireOp",EDGE,"E1696");
            var Q1487;
            Q1487=sQuery(id+"F10.wireOp",EDGE,"E1954");
            var Q1488;
            Q1488=sQuery(id+"F10.wireOp",EDGE,"E2694");
            var Q1489;
            Q1489=sQuery(id+"F10.wireOp",EDGE,"E2714");
            var Q1490;
            Q1490=sQuery(id+"F10.wireOp",EDGE,"E1733");
            var Q1491;
            Q1491=sQuery(id+"F10.wireOp",EDGE,"E1877");
            var Q1492;
            Q1492=sQuery(id+"F10.wireOp",EDGE,"E1767");
            var Q1493;
            Q1493=sQuery(id+"F10.wireOp",EDGE,"E1927");
            var Q1494;
            Q1494=sQuery(id+"F10.wireOp",EDGE,"E1817");
            var Q1495;
            Q1495=sQuery(id+"F10.wireOp",EDGE,"E1945");
            var Q1496;
            Q1496=sQuery(id+"F10.wireOp",EDGE,"E1695");
            var Q1497;
            Q1497=sQuery(id+"F10.wireOp",EDGE,"E1970");
            var Q1498;
            Q1498=sQuery(id+"F10.wireOp",EDGE,"E2691");
            var Q1499;
            Q1499=sQuery(id+"F10.wireOp",EDGE,"E2709");
            var Q1500;
            Q1500=sQuery(id+"F10.wireOp",EDGE,"E1878");
            var Q1501;
            Q1501=sQuery(id+"F10.wireOp",EDGE,"E1732");
            var Q1502;
            Q1502=sQuery(id+"F10.wireOp",EDGE,"E1783");
            var Q1503;
            Q1503=sQuery(id+"F10.wireOp",EDGE,"E1800");
            var Q1504;
            Q1504=sQuery(id+"F10.wireOp",EDGE,"E1864");
            var Q1505;
            Q1505=sQuery(id+"F10.wireOp",EDGE,"E1865");
            var Q1506;
            Q1506=sQuery(id+"F10.wireOp",EDGE,"E1919");
            var Q1507;
            Q1507=sQuery(id+"F10.wireOp",EDGE,"E1969");
            var Q1508;
            Q1508=sQuery(id+"F10.wireOp",EDGE,"E2675");
            var Q1509;
            Q1509=sQuery(id+"F10.wireOp",EDGE,"E2716");
            var Q1510;
            Q1510=sQuery(id+"F10.wireOp",EDGE,"E1989");
            var Q1511;
            Q1511=sQuery(id+"F10.wireOp",EDGE,"E1734");
            var Q1512;
            Q1512=sQuery(id+"F10.wireOp",EDGE,"E1749");
            var Q1513;
            Q1513=sQuery(id+"F10.wireOp",EDGE,"E1832");
            var Q1514;
            Q1514=sQuery(id+"F10.wireOp",EDGE,"E1816");
            var Q1515;
            Q1515=sQuery(id+"F10.wireOp",EDGE,"E1897");
            var Q1516;
            Q1516=sQuery(id+"F10.wireOp",EDGE,"E1967");
            var Q1517;
            Q1517=sQuery(id+"F10.wireOp",EDGE,"E1731");
            var Q1518;
            Q1518=sQuery(id+"F10.wireOp",EDGE,"E2723");
            var Q1519;
            Q1519=sQuery(id+"F10.wireOp",EDGE,"E1765");
            var Q1520;
            Q1520=sQuery(id+"F10.wireOp",EDGE,"E1799");
            var Q1521;
            Q1521=sQuery(id+"F10.wireOp",EDGE,"E1926");
            var Q1522;
            Q1522=sQuery(id+"F10.wireOp",EDGE,"E1913");
            var Q1523;
            Q1523=sQuery(id+"F10.wireOp",EDGE,"E1966");
            var Q1524;
            Q1524=sQuery(id+"F10.wireOp",EDGE,"E1730");
            var Q1525;
            Q1525=sQuery(id+"F10.wireOp",EDGE,"E2710");
            var Q1526;
            Q1526=sQuery(id+"F10.wireOp",EDGE,"E1781");
            var Q1527;
            Q1527=sQuery(id+"F10.wireOp",EDGE,"E1815");
            var Q1528;
            Q1528=sQuery(id+"F10.wireOp",EDGE,"E1863");
            var Q1529;
            Q1529=sQuery(id+"F10.wireOp",EDGE,"E1944");
            var Q1530;
            Q1530=sQuery(id+"F10.wireOp",EDGE,"E1729");
            var Q1531;
            Q1531=sQuery(id+"F10.wireOp",EDGE,"E2707");
            var Q1532;
            Q1532=sQuery(id+"F10.wireOp",EDGE,"E1748");
            var Q1533;
            Q1533=sQuery(id+"F10.wireOp",EDGE,"E1847");
            var Q1534;
            Q1534=sQuery(id+"F10.wireOp",EDGE,"E1831");
            var Q1535;
            Q1535=sQuery(id+"F10.wireOp",EDGE,"E1896");
            var Q1536;
            Q1536=sQuery(id+"F10.wireOp",EDGE,"E1745");
            var Q1537;
            Q1537=sQuery(id+"F10.wireOp",EDGE,"E1764");
            var Q1538;
            Q1538=sQuery(id+"F10.wireOp",EDGE,"E1797");
            var Q1539;
            Q1539=sQuery(id+"F10.wireOp",EDGE,"E1861");
            var Q1540;
            Q1540=sQuery(id+"F10.wireOp",EDGE,"E1912");
            var Q1541;
            Q1541=sQuery(id+"F10.wireOp",EDGE,"E1728");
            var Q1542;
            Q1542=sQuery(id+"F10.wireOp",EDGE,"E1780");
            var Q1543;
            Q1543=sQuery(id+"F10.wireOp",EDGE,"E1860");
            var Q1544;
            Q1544=sQuery(id+"F10.wireOp",EDGE,"E1813");
            var Q1545;
            Q1545=sQuery(id+"F10.wireOp",EDGE,"E1943");
            var Q1546;
            Q1546=sQuery(id+"F10.wireOp",EDGE,"E1744");
            var Q1547;
            Q1547=sQuery(id+"F10.wireOp",EDGE,"E1750");
            var Q1548;
            Q1548=sQuery(id+"F10.wireOp",EDGE,"E1830");
            var Q1549;
            Q1549=sQuery(id+"F10.wireOp",EDGE,"E1829");
            var Q1550;
            Q1550=sQuery(id+"F10.wireOp",EDGE,"E1895");
            var Q1551;
            Q1551=sQuery(id+"F10.wireOp",EDGE,"E1727");
            var Q1552;
            Q1552=sQuery(id+"F10.wireOp",EDGE,"E1925");
            var Q1553;
            Q1553=sQuery(id+"F10.wireOp",EDGE,"E1766");
            var Q1554;
            Q1554=sQuery(id+"F10.wireOp",EDGE,"E1845");
            var Q1555;
            Q1555=sQuery(id+"F10.wireOp",EDGE,"E1911");
            var Q1556;
            Q1556=sQuery(id+"F10.wireOp",EDGE,"E1743");
            var Q1557;
            Q1557=sQuery(id+"F10.wireOp",EDGE,"E1862");
            var Q1558;
            Q1558=sQuery(id+"F10.wireOp",EDGE,"E1782");
            var Q1559;
            Q1559=sQuery(id+"F10.wireOp",EDGE,"E1796");
            var Q1560;
            Q1560=sQuery(id+"F10.wireOp",EDGE,"E1942");
            var Q1561;
            Q1561=sQuery(id+"F10.wireOp",EDGE,"E1779");
            var Q1562;
            Q1562=sQuery(id+"F10.wireOp",EDGE,"E1859");
            var Q1563;
            Q1563=sQuery(id+"F10.wireOp",EDGE,"E1812");
            var Q1564;
            Q1564=sQuery(id+"F10.wireOp",EDGE,"E1924");
            var Q1565;
            Q1565=sQuery(id+"F10.wireOp",EDGE,"E1922");
            var Q1566;
            Q1566=sQuery(id+"F10.wireOp",EDGE,"E1747");
            var Q1567;
            Q1567=sQuery(id+"F10.wireOp",EDGE,"E1828");
            var Q1568;
            Q1568=sQuery(id+"F10.wireOp",EDGE,"E1940");
            var Q1569;
            Q1569=sQuery(id+"F10.wireOp",EDGE,"E1858");
            var Q1570;
            Q1570=sQuery(id+"F10.wireOp",EDGE,"E1763");
            var Q1571;
            Q1571=sQuery(id+"F10.wireOp",EDGE,"E1844");
            var Q1572;
            Q1572=sQuery(id+"F10.wireOp",EDGE,"E1893");
            var Q1573;
            Q1573=sQuery(id+"F10.wireOp",EDGE,"E1921");
            var Q1574;
            Q1574=sQuery(id+"F10.wireOp",EDGE,"E1778");
            var Q1575;
            Q1575=sQuery(id+"F10.wireOp",EDGE,"E1798");
            var Q1576;
            Q1576=sQuery(id+"F10.wireOp",EDGE,"E1909");
            var Q1577;
            Q1577=sQuery(id+"F10.wireOp",EDGE,"E1936");
            var Q1578;
            Q1578=sQuery(id+"F10.wireOp",EDGE,"E1746");
            var Q1579;
            Q1579=sQuery(id+"F10.wireOp",EDGE,"E1814");
            var Q1580;
            Q1580=sQuery(id+"F10.wireOp",EDGE,"E1876");
            var Q1581;
            Q1581=sQuery(id+"F10.wireOp",EDGE,"E1857");
            var Q1582;
            Q1582=sQuery(id+"F10.wireOp",EDGE,"E1762");
            var Q1583;
            Q1583=sQuery(id+"F10.wireOp",EDGE,"E1846");
            var Q1584;
            Q1584=sQuery(id+"F10.wireOp",EDGE,"E1892");
            var Q1585;
            Q1585=sQuery(id+"F10.wireOp",EDGE,"E1920");
            var Q1586;
            Q1586=sQuery(id+"F10.wireOp",EDGE,"E1777");
            var Q1587;
            Q1587=sQuery(id+"F10.wireOp",EDGE,"E1843");
            var Q1588;
            Q1588=sQuery(id+"F10.wireOp",EDGE,"E1908");
            var Q1589;
            Q1589=sQuery(id+"F10.wireOp",EDGE,"E1935");
            var Q1590;
            Q1590=sQuery(id+"F10.wireOp",EDGE,"E1761");
            var Q1591;
            Q1591=sQuery(id+"F10.wireOp",EDGE,"E1795");
            var Q1592;
            Q1592=sQuery(id+"F10.wireOp",EDGE,"E1924");
            var Q1593;
            Q1593=sQuery(id+"F10.wireOp",EDGE,"E1776");
            var Q1594;
            Q1594=sQuery(id+"F10.wireOp",EDGE,"E1856");
            var Q1595;
            Q1595=sQuery(id+"F10.wireOp",EDGE,"E1811");
            var Q1596;
            Q1596=sQuery(id+"F10.wireOp",EDGE,"E1939");
            var Q1597;
            Q1597=sQuery(id+"F10.wireOp",EDGE,"E1934");
            var Q1598;
            Q1598=sQuery(id+"F10.wireOp",EDGE,"E1760");
            var Q1599;
            Q1599=sQuery(id+"F10.wireOp",EDGE,"E1827");
            var Q1600;
            Q1600=sQuery(id+"F10.wireOp",EDGE,"E1941");
            var Q1601;
            Q1601=sQuery(id+"F10.wireOp",EDGE,"E1775");
            var Q1602;
            Q1602=sQuery(id+"F10.wireOp",EDGE,"E1839");
            var Q1603;
            Q1603=sQuery(id+"F10.wireOp",EDGE,"E1842");
            var Q1604;
            Q1604=sQuery(id+"F10.wireOp",EDGE,"E1894");
            var Q1605;
            Q1605=sQuery(id+"F10.wireOp",EDGE,"E1759");
            var Q1606;
            Q1606=sQuery(id+"F10.wireOp",EDGE,"E1855");
            var Q1607;
            Q1607=sQuery(id+"F10.wireOp",EDGE,"E1794");
            var Q1608;
            Q1608=sQuery(id+"F10.wireOp",EDGE,"E1910");
            var Q1609;
            Q1609=sQuery(id+"F10.wireOp",EDGE,"E1810");
            var Q1610;
            Q1610=sQuery(id+"F10.wireOp",EDGE,"E1907");
            var Q1611;
            Q1611=sQuery(id+"F10.wireOp",EDGE,"E1826");
            var Q1612;
            Q1612=sQuery(id+"F10.wireOp",EDGE,"E1923");
            var Q1613;
            Q1613=sQuery(id+"F10.wireOp",EDGE,"E1841");
            var Q1614;
            Q1614=sQuery(id+"F10.wireOp",EDGE,"E1875");
            var Q1615;
            Q1615=sQuery(id+"F10.wireOp",EDGE,"E1793");
            var Q1616;
            Q1616=sQuery(id+"F10.wireOp",EDGE,"E1891");
            var Q1617;
            Q1617=sQuery(id+"F10.wireOp",EDGE,"E1809");
            var Q1618;
            Q1618=sQuery(id+"F10.wireOp",EDGE,"E1906");
            var Q1619;
            Q1619=sQuery(id+"F10.wireOp",EDGE,"E1825");
            var Q1620;
            Q1620=sQuery(id+"F10.wireOp",EDGE,"E1937");
            var Q1621;
            Q1621=sQuery(id+"F10.wireOp",EDGE,"E1840");
            var Q1622;
            Q1622=sQuery(id+"F10.wireOp",EDGE,"E1874");
            var Q1623;
            Q1623=sQuery(id+"F10.wireOp",EDGE,"E1792");
            var Q1624;
            Q1624=sQuery(id+"F10.wireOp",EDGE,"E1890");
            var Q1625;
            Q1625=sQuery(id+"F10.wireOp",EDGE,"E1808");
            var Q1626;
            Q1626=sQuery(id+"F10.wireOp",EDGE,"E1905");
            var Q1627;
            Q1627=sQuery(id+"F10.wireOp",EDGE,"E1824");
            var Q1628;
            Q1628=sQuery(id+"F10.wireOp",EDGE,"E1953");
            var Q1629;
            Q1629=sQuery(id+"F10.wireOp",EDGE,"E1791");
            var Q1630;
            Q1630=sQuery(id+"F10.wireOp",EDGE,"E1873");
            var Q1631;
            Q1631=sQuery(id+"F10.wireOp",EDGE,"E1807");
            var Q1632;
            Q1632=sQuery(id+"F10.wireOp",EDGE,"E1889");
            var Q1633;
            Q1633=sQuery(id+"F10.wireOp",EDGE,"E1823");
            var Q1634;
            Q1634=sQuery(id+"F10.wireOp",EDGE,"E1904");
            var Q1635;
            Q1635=sQuery(id+"F10.wireOp",EDGE,"E1872");
            var Q1636;
            Q1636=sQuery(id+"F10.wireOp",EDGE,"E1888");
            var Q1637;
            Q1637=sQuery(id+"F10.wireOp",EDGE,"E1952");
            var Q1638;
            Q1638=sQuery(id+"F10.wireOp",EDGE,"E1903");
            var Q1639;
            Q1639=sQuery(id+"F10.wireOp",EDGE,"E1871");
            var Q1640;
            Q1640=sQuery(id+"F10.wireOp",EDGE,"E1887");
            var Q1641;
            Q1641=sQuery(id+"F10.wireOp",EDGE,"E1951");
            var Q1642;
            Q1642=sQuery(id+"F10.wireOp",EDGE,"E1950");
            extrude(context, id + "F11", {"entities" : qUnion([Q0]), "operationType" : NewBodyOperationType.ADD, "surfaceOperationType" : NewSurfaceOperationType.ADD, "surfaceEntities" : qUnion([Q1, Q2, Q3, Q4, Q5, Q6, Q7, Q8, Q9, Q10, Q11, Q12, Q13, Q14, Q15, Q16, Q17, Q18, Q19, Q20, Q21, Q22, Q23, Q24, Q25, Q26, Q27, Q28, Q29, Q30, Q31, Q32, Q33, Q34, Q35, Q36, Q37, Q38, Q39, Q40, Q41, Q42, Q43, Q44, Q45, Q46, Q47, Q48, Q49, Q50, Q51, Q52, Q53, Q54, Q55, Q56, Q57, Q58, Q59, Q60, Q61, Q62, Q63, Q64, Q65, Q66, Q67, Q68, Q69, Q70, Q71, Q72, Q73, Q74, Q75, Q76, Q77, Q78, Q79, Q80, Q81, Q82, Q83, Q84, Q85, Q86, Q87, Q88, Q89, Q90, Q91, Q92, Q93, Q94, Q95, Q96, Q97, Q98, Q99, Q100, Q101, Q102, Q103, Q104, Q105, Q106, Q107, Q108, Q109, Q110, Q111, Q112, Q113, Q114, Q115, Q116, Q117, Q118, Q119, Q120, Q121, Q122, Q123, Q124, Q125, Q126, Q127, Q128, Q129, Q130, Q131, Q132, Q133, Q134, Q135, Q136, Q137, Q138, Q139, Q140, Q141, Q142, Q143, Q144, Q145, Q146, Q147, Q148, Q149, Q150, Q151, Q152, Q153, Q154, Q155, Q156, Q157, Q158, Q159, Q160, Q161, Q162, Q163, Q164, Q165, Q166, Q167, Q168, Q169, Q170, Q171, Q172, Q173, Q174, Q175, Q176, Q177, Q178, Q179, Q180, Q181, Q182, Q183, Q184, Q185, Q186, Q187, Q188, Q189, Q190, Q191, Q192, Q193, Q194, Q195, Q196, Q197, Q198, Q199, Q200, Q201, Q202, Q203, Q204, Q205, Q206, Q207, Q208, Q209, Q210, Q211, Q212, Q213, Q214, Q215, Q216, Q217, Q218, Q219, Q220, Q221, Q222, Q223, Q224, Q225, Q226, Q227, Q228, Q229, Q230, Q231, Q232, Q233, Q234, Q235, Q236, Q237, Q238, Q239, Q240, Q241, Q242, Q243, Q244, Q245, Q246, Q247, Q248, Q249, Q250, Q251, Q252, Q253, Q254, Q255, Q256, Q257, Q258, Q259, Q260, Q261, Q262, Q263, Q264, Q265, Q266, Q267, Q268, Q269, Q270, Q271, Q272, Q273, Q274, Q275, Q276, Q277, Q278, Q279, Q280, Q281, Q282, Q283, Q284, Q285, Q286, Q287, Q288, Q289, Q290, Q291, Q292, Q293, Q294, Q295, Q296, Q297, Q298, Q299, Q300, Q301, Q302, Q303, Q304, Q305, Q306, Q307, Q308, Q309, Q310, Q311, Q312, Q313, Q314, Q315, Q316, Q317, Q318, Q319, Q320, Q321, Q322, Q323, Q324, Q325, Q326, Q327, Q328, Q329, Q330, Q331, Q332, Q333, Q334, Q335, Q336, Q337, Q338, Q339, Q340, Q341, Q342, Q343, Q344, Q345, Q346, Q347, Q348, Q349, Q350, Q351, Q352, Q353, Q354, Q355, Q356, Q357, Q358, Q359, Q360, Q361, Q362, Q363, Q364, Q365, Q366, Q367, Q368, Q369, Q370, Q371, Q372, Q373, Q374, Q375, Q376, Q377, Q378, Q379, Q380, Q381, Q382, Q383, Q384, Q385, Q386, Q387, Q388, Q389, Q390, Q391, Q392, Q393, Q394, Q395, Q396, Q397, Q398, Q399, Q400, Q401, Q402, Q403, Q404, Q405, Q406, Q407, Q408, Q409, Q410, Q411, Q412, Q413, Q414, Q415, Q416, Q417, Q418, Q419, Q420, Q421, Q422, Q423, Q424, Q425, Q426, Q427, Q428, Q429, Q430, Q431, Q432, Q433, Q434, Q435, Q436, Q437, Q438, Q439, Q440, Q441, Q442, Q443, Q444, Q445, Q446, Q447, Q448, Q449, Q450, Q451, Q452, Q453, Q454, Q455, Q456, Q457, Q458, Q459, Q460, Q461, Q462, Q463, Q464, Q465, Q466, Q467, Q468, Q469, Q470, Q471, Q472, Q473, Q474, Q475, Q476, Q477, Q478, Q479, Q480, Q481, Q482, Q483, Q484, Q485, Q486, Q487, Q488, Q489, Q490, Q491, Q492, Q493, Q494, Q495, Q496, Q497, Q498, Q499, Q500, Q501, Q502, Q503, Q504, Q505, Q506, Q507, Q508, Q509, Q510, Q511, Q512, Q513, Q514, Q515, Q516, Q517, Q518, Q519, Q520, Q521, Q522, Q523, Q524, Q525, Q526, Q527, Q528, Q529, Q530, Q531, Q532, Q533, Q534, Q535, Q536, Q537, Q538, Q539, Q540, Q541, Q542, Q543, Q544, Q545, Q546, Q547, Q548, Q549, Q550, Q551, Q552, Q553, Q554, Q555, Q556, Q557, Q558, Q559, Q560, Q561, Q562, Q563, Q564, Q565, Q566, Q567, Q568, Q569, Q570, Q571, Q572, Q573, Q574, Q575, Q576, Q577, Q578, Q579, Q580, Q581, Q582, Q583, Q584, Q585, Q586, Q587, Q588, Q589, Q590, Q591, Q592, Q593, Q594, Q595, Q596, Q597, Q598, Q599, Q600, Q601, Q602, Q603, Q604, Q605, Q606, Q607, Q608, Q609, Q610, Q611, Q612, Q613, Q614, Q615, Q616, Q617, Q618, Q619, Q620, Q621, Q622, Q623, Q624, Q625, Q626, Q627, Q628, Q629, Q630, Q631, Q632, Q633, Q634, Q635, Q636, Q637, Q638, Q639, Q640, Q641, Q642, Q643, Q644, Q645, Q646, Q647, Q648, Q649, Q650, Q651, Q652, Q653, Q654, Q655, Q656, Q657, Q658, Q659, Q660, Q661, Q662, Q663, Q664, Q665, Q666, Q667, Q668, Q669, Q670, Q671, Q672, Q673, Q674, Q675, Q676, Q677, Q678, Q679, Q680, Q681, Q682, Q683, Q684, Q685, Q686, Q687, Q688, Q689, Q690, Q691, Q692, Q693, Q694, Q695, Q696, Q697, Q698, Q699, Q700, Q701, Q702, Q703, Q704, Q705, Q706, Q707, Q708, Q709, Q710, Q711, Q712, Q713, Q714, Q715, Q716, Q717, Q718, Q719, Q720, Q721, Q722, Q723, Q724, Q725, Q726, Q727, Q728, Q729, Q730, Q731, Q732, Q733, Q734, Q735, Q736, Q737, Q738, Q739, Q740, Q741, Q742, Q743, Q744, Q745, Q746, Q747, Q748, Q749, Q750, Q751, Q752, Q753, Q754, Q755, Q756, Q757, Q758, Q759, Q760, Q761, Q762, Q763, Q764, Q765, Q766, Q767, Q768, Q769, Q770, Q771, Q772, Q773, Q774, Q775, Q776, Q777, Q778, Q779, Q780, Q781, Q782, Q783, Q784, Q785, Q786, Q787, Q788, Q789, Q790, Q791, Q792, Q793, Q794, Q795, Q796, Q797, Q798, Q799, Q800, Q801, Q802, Q803, Q804, Q805, Q806, Q807, Q808, Q809, Q810, Q811, Q812, Q813, Q814, Q815, Q816, Q817, Q818, Q819, Q820, Q821, Q822, Q823, Q824, Q825, Q826, Q827, Q828, Q829, Q830, Q831, Q832, Q833, Q834, Q835, Q836, Q837, Q838, Q839, Q840, Q841, Q842, Q843, Q844, Q845, Q846, Q847, Q848, Q849, Q850, Q851, Q852, Q853, Q854, Q855, Q856, Q857, Q858, Q859, Q860, Q861, Q862, Q863, Q864, Q865, Q866, Q867, Q868, Q869, Q870, Q871, Q872, Q873, Q874, Q875, Q876, Q877, Q878, Q879, Q880, Q881, Q882, Q883, Q884, Q885, Q886, Q887, Q888, Q889, Q890, Q891, Q892, Q893, Q894, Q895, Q896, Q897, Q898, Q899, Q900, Q901, Q902, Q903, Q904, Q905, Q906, Q907, Q908, Q909, Q910, Q911, Q912, Q913, Q914, Q915, Q916, Q917, Q918, Q919, Q920, Q921, Q922, Q923, Q924, Q925, Q926, Q927, Q928, Q929, Q930, Q931, Q932, Q933, Q934, Q935, Q936, Q937, Q938, Q939, Q940, Q941, Q942, Q943, Q944, Q945, Q946, Q947, Q948, Q949, Q950, Q951, Q952, Q953, Q954, Q955, Q956, Q957, Q958, Q959, Q960, Q961, Q962, Q963, Q964, Q965, Q966, Q967, Q968, Q969, Q970, Q971, Q972, Q973, Q974, Q975, Q976, Q977, Q978, Q979, Q980, Q981, Q982, Q983, Q984, Q985, Q986, Q987, Q988, Q989, Q990, Q991, Q992, Q993, Q994, Q995, Q996, Q997, Q998, Q999, Q1000, Q1001, Q1002, Q1003, Q1004, Q1005, Q1006, Q1007, Q1008, Q1009, Q1010, Q1011, Q1012, Q1013, Q1014, Q1015, Q1016, Q1017, Q1018, Q1019, Q1020, Q1021, Q1022, Q1023, Q1024, Q1025, Q1026, Q1027, Q1028, Q1029, Q1030, Q1031, Q1032, Q1033, Q1034, Q1035, Q1036, Q1037, Q1038, Q1039, Q1040, Q1041, Q1042, Q1043, Q1044, Q1045, Q1046, Q1047, Q1048, Q1049, Q1050, Q1051, Q1052, Q1053, Q1054, Q1055, Q1056, Q1057, Q1058, Q1059, Q1060, Q1061, Q1062, Q1063, Q1064, Q1065, Q1066, Q1067, Q1068, Q1069, Q1070, Q1071, Q1072, Q1073, Q1074, Q1075, Q1076, Q1077, Q1078, Q1079, Q1080, Q1081, Q1082, Q1083, Q1084, Q1085, Q1086, Q1087, Q1088, Q1089, Q1090, Q1091, Q1092, Q1093, Q1094, Q1095, Q1096, Q1097, Q1098, Q1099, Q1100, Q1101, Q1102, Q1103, Q1104, Q1105, Q1106, Q1107, Q1108, Q1109, Q1110, Q1111, Q1112, Q1113, Q1114, Q1115, Q1116, Q1117, Q1118, Q1119, Q1120, Q1121, Q1122, Q1123, Q1124, Q1125, Q1126, Q1127, Q1128, Q1129, Q1130, Q1131, Q1132, Q1133, Q1134, Q1135, Q1136, Q1137, Q1138, Q1139, Q1140, Q1141, Q1142, Q1143, Q1144, Q1145, Q1146, Q1147, Q1148, Q1149, Q1150, Q1151, Q1152, Q1153, Q1154, Q1155, Q1156, Q1157, Q1158, Q1159, Q1160, Q1161, Q1162, Q1163, Q1164, Q1165, Q1166, Q1167, Q1168, Q1169, Q1170, Q1171, Q1172, Q1173, Q1174, Q1175, Q1176, Q1177, Q1178, Q1179, Q1180, Q1181, Q1182, Q1183, Q1184, Q1185, Q1186, Q1187, Q1188, Q1189, Q1190, Q1191, Q1192, Q1193, Q1194, Q1195, Q1196, Q1197, Q1198, Q1199, Q1200, Q1201, Q1202, Q1203, Q1204, Q1205, Q1206, Q1207, Q1208, Q1209, Q1210, Q1211, Q1212, Q1213, Q1214, Q1215, Q1216, Q1217, Q1218, Q1219, Q1220, Q1221, Q1222, Q1223, Q1224, Q1225, Q1226, Q1227, Q1228, Q1229, Q1230, Q1231, Q1232, Q1233, Q1234, Q1235, Q1236, Q1237, Q1238, Q1239, Q1240, Q1241, Q1242, Q1243, Q1244, Q1245, Q1246, Q1247, Q1248, Q1249, Q1250, Q1251, Q1252, Q1253, Q1254, Q1255, Q1256, Q1257, Q1258, Q1259, Q1260, Q1261, Q1262, Q1263, Q1264, Q1265, Q1266, Q1267, Q1268, Q1269, Q1270, Q1271, Q1272, Q1273, Q1274, Q1275, Q1276, Q1277, Q1278, Q1279, Q1280, Q1281, Q1282, Q1283, Q1284, Q1285, Q1286, Q1287, Q1288, Q1289, Q1290, Q1291, Q1292, Q1293, Q1294, Q1295, Q1296, Q1297, Q1298, Q1299, Q1300, Q1301, Q1302, Q1303, Q1304, Q1305, Q1306, Q1307, Q1308, Q1309, Q1310, Q1311, Q1312, Q1313, Q1314, Q1315, Q1316, Q1317, Q1318, Q1319, Q1320, Q1321, Q1322, Q1323, Q1324, Q1325, Q1326, Q1327, Q1328, Q1329, Q1330, Q1331, Q1332, Q1333, Q1334, Q1335, Q1336, Q1337, Q1338, Q1339, Q1340, Q1341, Q1342, Q1343, Q1344, Q1345, Q1346, Q1347, Q1348, Q1349, Q1350, Q1351, Q1352, Q1353, Q1354, Q1355, Q1356, Q1357, Q1358, Q1359, Q1360, Q1361, Q1362, Q1363, Q1364, Q1365, Q1366, Q1367, Q1368, Q1369, Q1370, Q1371, Q1372, Q1373, Q1374, Q1375, Q1376, Q1377, Q1378, Q1379, Q1380, Q1381, Q1382, Q1383, Q1384, Q1385, Q1386, Q1387, Q1388, Q1389, Q1390, Q1391, Q1392, Q1393, Q1394, Q1395, Q1396, Q1397, Q1398, Q1399, Q1400, Q1401, Q1402, Q1403, Q1404, Q1405, Q1406, Q1407, Q1408, Q1409, Q1410, Q1411, Q1412, Q1413, Q1414, Q1415, Q1416, Q1417, Q1418, Q1419, Q1420, Q1421, Q1422, Q1423, Q1424, Q1425, Q1426, Q1427, Q1428, Q1429, Q1430, Q1431, Q1432, Q1433, Q1434, Q1435, Q1436, Q1437, Q1438, Q1439, Q1440, Q1441, Q1442, Q1443, Q1444, Q1445, Q1446, Q1447, Q1448, Q1449, Q1450, Q1451, Q1452, Q1453, Q1454, Q1455, Q1456, Q1457, Q1458, Q1459, Q1460, Q1461, Q1462, Q1463, Q1464, Q1465, Q1466, Q1467, Q1468, Q1469, Q1470, Q1471, Q1472, Q1473, Q1474, Q1475, Q1476, Q1477, Q1478, Q1479, Q1480, Q1481, Q1482, Q1483, Q1484, Q1485, Q1486, Q1487, Q1488, Q1489, Q1490, Q1491, Q1492, Q1493, Q1494, Q1495, Q1496, Q1497, Q1498, Q1499, Q1500, Q1501, Q1502, Q1503, Q1504, Q1505, Q1506, Q1507, Q1508, Q1509, Q1510, Q1511, Q1512, Q1513, Q1514, Q1515, Q1516, Q1517, Q1518, Q1519, Q1520, Q1521, Q1522, Q1523, Q1524, Q1525, Q1526, Q1527, Q1528, Q1529, Q1530, Q1531, Q1532, Q1533, Q1534, Q1535, Q1536, Q1537, Q1538, Q1539, Q1540, Q1541, Q1542, Q1543, Q1544, Q1545, Q1546, Q1547, Q1548, Q1549, Q1550, Q1551, Q1552, Q1553, Q1554, Q1555, Q1556, Q1557, Q1558, Q1559, Q1560, Q1561, Q1562, Q1563, Q1564, Q1565, Q1566, Q1567, Q1568, Q1569, Q1570, Q1571, Q1572, Q1573, Q1574, Q1575, Q1576, Q1577, Q1578, Q1579, Q1580, Q1581, Q1582, Q1583, Q1584, Q1585, Q1586, Q1587, Q1588, Q1589, Q1590, Q1591, Q1592, Q1593, Q1594, Q1595, Q1596, Q1597, Q1598, Q1599, Q1600, Q1601, Q1602, Q1603, Q1604, Q1605, Q1606, Q1607, Q1608, Q1609, Q1610, Q1611, Q1612, Q1613, Q1614, Q1615, Q1616, Q1617, Q1618, Q1619, Q1620, Q1621, Q1622, Q1623, Q1624, Q1625, Q1626, Q1627, Q1628, Q1629, Q1630, Q1631, Q1632, Q1633, Q1634, Q1635, Q1636, Q1637, Q1638, Q1639, Q1640, Q1641, Q1642]), "depth" : 3 * mm, "offsetDistance" : 25 * mm});
        }
    });
